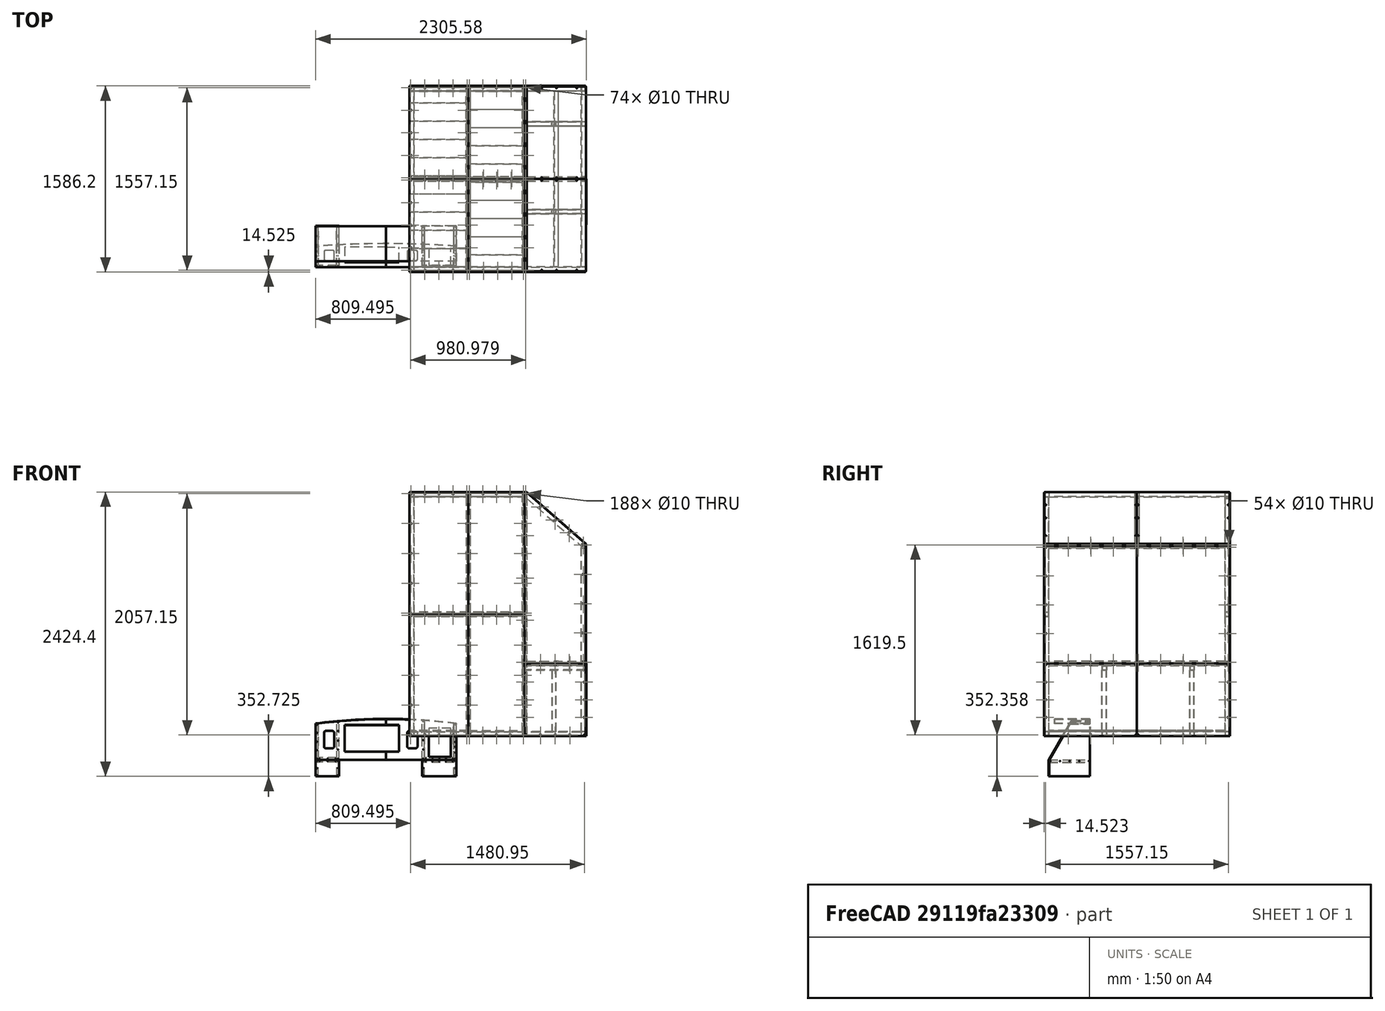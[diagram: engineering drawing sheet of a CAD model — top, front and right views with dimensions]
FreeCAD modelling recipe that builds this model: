
FCSTD DOCUMENT  (FreeCAD 1.0R39109 (Git))
Label: Estructura
License: All rights reserved
LicenseURL: https://en.wikipedia.org/wiki/All_rights_reserved
objects: Sketcher::SketchObject×137, PartDesign::SubShapeBinder×88, PartDesign::Pad×80, PartDesign::Body×74, PartDesign::Pocket×56, Part::FeaturePython×23, App::DocumentObjectGroup×18, PartDesign::Thickness×10, App::Part×4, PartDesign::Plane×3
note: 900 computed .brp shape members not serialized (recipe doc carries the construction recipe); baked Part::Feature solids carry a one-line shape summary decoded from their .brp

FEATURE [Sketcher::SketchObject] Sketch
  ArcFitTolerance = 1e-06
  AttachmentSupport = -> [XZ_Plane001]
  FullyConstrained = true
  MakeInternals = false
  MapMode = 5
  Placement = pos=(0,0,0) rot=(1,0,0;1.5708rad)
  sketch-geometry (4):
    g0: LineSegment StartX=0 StartY=0 StartZ=0 EndX=0 EndY=2000 EndZ=0
    g1: LineSegment StartX=0 StartY=0 StartZ=0 EndX=-38.1 EndY=0 EndZ=0
    g2: LineSegment StartX=-38.1 StartY=0 StartZ=0 EndX=-38.1 EndY=2000 EndZ=0
    g3: LineSegment StartX=0 StartY=2000 StartZ=0 EndX=-38.1 EndY=2000 EndZ=0
  constraints (11):
    c: Distance(g0) = 2000
    c: Coincident(g0,g-1)
    c: Vertical(g0)
    c: Distance(g1) = 38.1
    c: Coincident(g1,g0)
    c: PointOnObject(g1,g-1)
    c: Coincident(g2,g1)
    c: Vertical(g2)
    c: Coincident(g3,g0)
    c: Horizontal(g3)
    c: Coincident(g2,g3)
FEATURE [PartDesign::Pad] Pad
  Direction = (0,-1,2e-16)
  Length = 38.1
  Length2 = 10
  Placement = pos=(0,0,0) rot=(1,0,0;1.5708rad)
  Profile = -> Sketch
  ReferenceAxis = -> Sketch [N_Axis]
  Refine = true
  Suppressed = false
  Type = 0
FEATURE [Sketcher::SketchObject] Sketch001
  ArcFitTolerance = 1e-06
  AttachmentSupport = -> [Pad]
  ExternalGeometry = -> [Pad]
  FullyConstrained = true
  MakeInternals = false
  MapMode = 5
  Placement = pos=(0,8.8e-13,2000) rot=(0,0,1;3.14159rad)
  sketch-geometry (6):
    g0: LineSegment [constr] StartX=38.1 StartY=38.1 StartZ=0 EndX=0 EndY=0 EndZ=0
    g1: LineSegment StartX=2.7 StartY=2.7 StartZ=0 EndX=35.4 EndY=2.7 EndZ=0
    g2: LineSegment StartX=35.4 StartY=2.7 StartZ=0 EndX=35.4 EndY=35.4 EndZ=0
    g3: LineSegment StartX=35.4 StartY=35.4 StartZ=0 EndX=2.7 EndY=35.4 EndZ=0
    g4: LineSegment StartX=2.7 StartY=35.4 StartZ=0 EndX=2.7 EndY=2.7 EndZ=0
    g5: GeomPoint [constr] X=19.05 Y=19.05 Z=0
  constraints (14):
    c: Coincident(g0,g-3)
    c: Coincident(g0,g-1)
    c: Coincident(g1,g2)
    c: Coincident(g2,g3)
    c: Coincident(g3,g4)
    c: Coincident(g4,g1)
    c: Horizontal(g1)
    c: Horizontal(g3)
    c: Vertical(g2)
    c: Vertical(g4)
    c: Symmetric(g3,g1,g5)
    c: Symmetric(g0,g0,g5)
    c: PointOnObject(g2,g0)
    c: DistanceX(g2,g0) = 2.7
FEATURE [Sketcher::SketchObject] Sketch009
  ArcFitTolerance = 1e-06
  AttachmentSupport = -> [XY_Plane006]
  FullyConstrained = false
  MakeInternals = false
  MapMode = 5
  sketch-geometry (10):
    g0: LineSegment StartX=0 StartY=0 StartZ=0 EndX=-38.1 EndY=0 EndZ=0
    g1: LineSegment StartX=-38.1 StartY=0 StartZ=0 EndX=-38.1 EndY=-38.1 EndZ=0
    g2: LineSegment StartX=0 StartY=0 StartZ=0 EndX=-0.0294822 EndY=-38.1 EndZ=0
    g3: LineSegment StartX=-38.1 StartY=-38.1 StartZ=0 EndX=-0.0294822 EndY=-38.1 EndZ=0
    g4: LineSegment [constr] StartX=-38.1 StartY=0 StartZ=0 EndX=-0.0294822 EndY=-38.1 EndZ=0
    g5: LineSegment StartX=-2.72739 StartY=-35.4 StartZ=0 EndX=-2.72739 EndY=-2.7 EndZ=0
    g6: LineSegment StartX=-2.72739 StartY=-2.7 StartZ=0 EndX=-35.4021 EndY=-2.7 EndZ=0
    g7: LineSegment StartX=-35.4021 StartY=-2.7 StartZ=0 EndX=-35.4021 EndY=-35.4 EndZ=0
    g8: LineSegment StartX=-35.4021 StartY=-35.4 StartZ=0 EndX=-2.72739 EndY=-35.4 EndZ=0
    g9: GeomPoint [constr] X=-19.0647 Y=-19.05 Z=0
  constraints (24):
    c: Distance(g0) = 38.1
    c: Coincident(g0,g-1)
    c: PointOnObject(g0,g-1)
    c: Distance(g1) = 38.1
    c: Coincident(g1,g0)
    c: Vertical(g1)
    c: Coincident(g2,g0)
    c: Coincident(g3,g1)
    c: Horizontal(g3)
    c: Coincident(g2,g3)
    c: Coincident(g4,g0)
    c: Coincident(g4,g2)
    c: Coincident(g5,g6)
    c: Coincident(g6,g7)
    c: Coincident(g7,g8)
    c: Coincident(g8,g5)
    c: Vertical(g5)
    c: Vertical(g7)
    c: Horizontal(g6)
    c: Horizontal(g8)
    c: Symmetric(g7,g5,g9)
    c: Symmetric(g4,g4,g9)
    c: PointOnObject(g6,g4)
    c: DistanceY(g6,g0) = 2.7
FEATURE [PartDesign::Pad] Pad005
  Direction = (0,0,1)
  Length = 1600
  Length2 = 10
  Profile = -> Sketch009
  ReferenceAxis = -> Sketch009 [N_Axis]
  Refine = true
  Suppressed = false
  Type = 0
FEATURE [PartDesign::Body] Body005  label="Cuerpo008"
  AllowCompound = false
  Group = -> [Sketch009,Pad005]
  Origin = -> Origin006
  Placement = pos=(2000,0,38.1) rot=(0,0,1;0rad)
  Tip = -> Pad005
FEATURE [Part::FeaturePython] Clone016  label="Cuerpo009"  # Draft clone (typed FeaturePython)
  AttacherType = Attacher::AttachEngine3D
  Fuse = false
  Objects = -> [Body005]
  Placement = pos=(2000,1538.1,38.1) rot=(0,0,1;0rad)
  Scale = (1,1,1)
FEATURE [PartDesign::SubShapeBinder] Binder
  BindCopyOnChange = 0
  BindMode = 2
  ClaimChildren = false
  Context = -> Part [Body008.Binder.]
  Fuse = false
  MakeFace = true
  OffsetFill = false
  OffsetIntersection = false
  OffsetJoinType = 0
  OffsetOpenResult = false
  PartialLoad = false
  Refine = true
  Relative = true
  _Version = 2
FEATURE [Sketcher::SketchObject] Sketch014
  ArcFitTolerance = 1e-06
  AttachmentSupport = -> [Binder]
  ExternalGeometry = -> [Binder]
  FullyConstrained = true
  MakeInternals = false
  MapMode = 5
  Placement = pos=(0,-38.1,-8.4e-15) rot=(1,0,0;1.5708rad)
  sketch-geometry (4):
    g0: LineSegment StartX=1500 StartY=638.1 StartZ=0 EndX=1961.9 EndY=638.1 EndZ=0
    g1: LineSegment StartX=1961.9 StartY=638.1 StartZ=0 EndX=1961.9 EndY=600 EndZ=0
    g2: LineSegment StartX=1961.9 StartY=600 StartZ=0 EndX=1500 EndY=600 EndZ=0
    g3: LineSegment StartX=1500 StartY=600 StartZ=0 EndX=1500 EndY=638.1 EndZ=0
  constraints (8):
    c: Coincident(g0,g-3)
    c: Coincident(g0,g-4)
    c: Coincident(g1,g0)
    c: Coincident(g1,g-4)
    c: Coincident(g2,g1)
    c: Coincident(g2,g-3)
    c: Coincident(g3,g2)
    c: Coincident(g3,g0)
FEATURE [PartDesign::Pad] Pad008
  Direction = (0,-1,2e-16)
  Length = 38.1
  Length2 = 10
  Profile = -> Sketch014
  ReferenceAxis = -> Sketch014 [N_Axis]
  Refine = true
  Reversed = true
  Suppressed = false
  Type = 0
FEATURE [Sketcher::SketchObject] Sketch015
  ArcFitTolerance = 1e-06
  AttachmentSupport = -> [Pad008]
  ExternalGeometry = -> [Pad008]
  FullyConstrained = true
  MakeInternals = false
  MapMode = 5
  Placement = pos=(1500,0,0) rot=(0.57735,-0.57735,-0.57735;2.0944rad)
  sketch-geometry (6):
    g0: LineSegment [constr] StartX=-3.691e-13 StartY=638.1 StartZ=0 EndX=38.1 EndY=600 EndZ=0
    g1: LineSegment StartX=35.4 StartY=602.7 StartZ=0 EndX=35.4 EndY=635.4 EndZ=0
    g2: LineSegment StartX=35.4 StartY=635.4 StartZ=0 EndX=2.7 EndY=635.4 EndZ=0
    g3: LineSegment StartX=2.7 StartY=635.4 StartZ=0 EndX=2.7 EndY=602.7 EndZ=0
    g4: LineSegment StartX=2.7 StartY=602.7 StartZ=0 EndX=35.4 EndY=602.7 EndZ=0
    g5: GeomPoint [constr] X=19.05 Y=619.05 Z=0
  constraints (14):
    c: Coincident(g0,g-3)
    c: Coincident(g0,g-4)
    c: Coincident(g1,g2)
    c: Coincident(g2,g3)
    c: Coincident(g3,g4)
    c: Coincident(g4,g1)
    c: Vertical(g1)
    c: Vertical(g3)
    c: Horizontal(g2)
    c: Horizontal(g4)
    c: Symmetric(g3,g1,g5)
    c: Symmetric(g0,g0,g5)
    c: PointOnObject(g2,g0)
    c: DistanceY(g2,g0) = 2.7
FEATURE [PartDesign::Pocket] Pocket004
  BaseFeature = -> Pad008
  Direction = (1,0,0)
  Length = 5
  Length2 = 5
  Profile = -> Sketch015
  ReferenceAxis = -> Sketch015 [N_Axis]
  Refine = true
  Suppressed = false
  Type = 1
FEATURE [PartDesign::Body] Body008  label="Cuerpo"
  AllowCompound = false
  Group = -> [Binder,Sketch014,Pad008,Sketch015,Pocket004]
  Origin = -> Origin009
  Tip = -> Pocket004
FEATURE [Part::FeaturePython] Clone021  label="Cuerpo011"  # Draft clone (typed FeaturePython)
  AttacherType = Attacher::AttachEngine3D
  Fuse = false
  Objects = -> [Body008]
  Placement = pos=(-1.0872e-12,1538.1,-4.547e-13) rot=(0,0,1;0rad)
  Scale = (1,1,1)
FEATURE [App::DocumentObjectGroup] Group001  label="1.6m"
  Group = -> [Clone016,Body005]
FEATURE [Part::FeaturePython] Clone033  label="Cuerpo023"  # WARN: FeaturePython — macro-defined, semantics opaque (R4)
  AttacherType = Attacher::AttachEngine3D
  Fuse = false
  Placement = pos=(249.985,0,-1019.05) rot=(0,0,1;0rad)
  Scale = (1,1,1)
FEATURE [Part::FeaturePython] Clone034  label="Cuerpo024"  # WARN: FeaturePython — macro-defined, semantics opaque (R4)
  AttacherType = Attacher::AttachEngine3D
  Fuse = false
  Placement = pos=(249.985,1538.1,0) rot=(0,0,1;0rad)
  Scale = (1,1,1)
FEATURE [Part::FeaturePython] Clone035  label="Cuerpo025"  # WARN: FeaturePython — macro-defined, semantics opaque (R4)
  AttacherType = Attacher::AttachEngine3D
  Fuse = false
  Placement = pos=(249.985,1538.1,-1019.05) rot=(0,0,1;0rad)
  Scale = (1,1,1)
FEATURE [PartDesign::SubShapeBinder] Binder007
  BindCopyOnChange = 0
  BindMode = 2
  ClaimChildren = false
  Context = -> Body014 [Binder007.]
  Fuse = false
  MakeFace = true
  OffsetFill = false
  OffsetIntersection = false
  OffsetJoinType = 0
  OffsetOpenResult = false
  PartialLoad = false
  Refine = true
  Relative = true
  _Version = 2
FEATURE [Sketcher::SketchObject] Sketch028
  ArcFitTolerance = 1e-06
  AttachmentSupport = -> [Binder007]
  ExternalGeometry = -> [Binder007]
  FullyConstrained = true
  MakeInternals = false
  MapMode = 5
  Placement = pos=(2000,-4.4e-13,0) rot=(0.57735,0.57735,0.57735;2.0944rad)
  sketch-geometry (4):
    g0: LineSegment StartX=0 StartY=0 StartZ=0 EndX=1500 EndY=0 EndZ=0
    g1: LineSegment StartX=1500 StartY=0 StartZ=0 EndX=1500 EndY=38.1 EndZ=0
    g2: LineSegment StartX=1500 StartY=38.1 StartZ=0 EndX=0 EndY=38.1 EndZ=0
    g3: LineSegment StartX=0 StartY=38.1 StartZ=0 EndX=0 EndY=0 EndZ=0
  constraints (11):
    c: Coincident(g0,g1)
    c: Coincident(g1,g2)
    c: Coincident(g2,g3)
    c: Coincident(g3,g0)
    c: Horizontal(g0)
    c: Horizontal(g2)
    c: Vertical(g1)
    c: Vertical(g3)
    c: Coincident(g0,g-1)
    c: PointOnObject(g1,g-3)
    c: DistanceX(g0,g0) = 1500
FEATURE [PartDesign::Pad] Pad014
  Direction = (1,0,0)
  Length = 38.1
  Length2 = 10
  Profile = -> Sketch028
  ReferenceAxis = -> Sketch028 [N_Axis]
  Refine = true
  Reversed = true
  Suppressed = false
  Type = 0
FEATURE [Sketcher::SketchObject] Sketch029
  ArcFitTolerance = 1e-06
  AttachmentSupport = -> [Pad014]
  ExternalGeometry = -> [Pad014]
  FullyConstrained = true
  MakeInternals = false
  MapMode = 5
  Placement = pos=(0,1500,0) rot=(0,0.707107,0.707107;3.14159rad)
  sketch-geometry (6):
    g0: LineSegment [constr] StartX=-2000 StartY=0 StartZ=0 EndX=-1961.9 EndY=38.1 EndZ=0
    g1: LineSegment StartX=-1997.3 StartY=2.7 StartZ=0 EndX=-1964.6 EndY=2.7 EndZ=0
    g2: LineSegment StartX=-1964.6 StartY=2.7 StartZ=0 EndX=-1964.6 EndY=35.4 EndZ=0
    g3: LineSegment StartX=-1964.6 StartY=35.4 StartZ=0 EndX=-1997.3 EndY=35.4 EndZ=0
    g4: LineSegment StartX=-1997.3 StartY=35.4 StartZ=0 EndX=-1997.3 EndY=2.7 EndZ=0
    g5: GeomPoint [constr] X=-1980.95 Y=19.05 Z=0
  constraints (14):
    c: Coincident(g0,g-3)
    c: Coincident(g0,g-4)
    c: Coincident(g1,g2)
    c: Coincident(g2,g3)
    c: Coincident(g3,g4)
    c: Coincident(g4,g1)
    c: Horizontal(g1)
    c: Horizontal(g3)
    c: Vertical(g2)
    c: Vertical(g4)
    c: Symmetric(g3,g1,g5)
    c: Symmetric(g0,g0,g5)
    c: PointOnObject(g2,g0)
    c: DistanceY(g2,g0) = 2.7
FEATURE [PartDesign::Pocket] Pocket010
  BaseFeature = -> Pad014
  Direction = (0,-1,2e-16)
  Length = 5
  Length2 = 5
  Profile = -> Sketch029
  ReferenceAxis = -> Sketch029 [N_Axis]
  Refine = true
  Suppressed = false
  Type = 1
FEATURE [PartDesign::Body] Body014  label="Cuerpo026"
  AllowCompound = false
  Group = -> [Binder007,Sketch028,Pad014,Sketch029,Pocket010]
  Origin = -> Origin015
  Tip = -> Pocket010
FEATURE [Part::FeaturePython] Clone037  label="Cuerpo028"  # Draft clone (typed FeaturePython)
  AttacherType = Attacher::AttachEngine3D
  Fuse = false
  Objects = -> [Body014]
  Placement = pos=(-1.3642e-12,8.006e-13,600) rot=(0,0,1;0rad)
  Scale = (1,1,1)
FEATURE [Part::FeaturePython] Clone038  label="Cuerpo029"  # Draft clone (typed FeaturePython)
  AttacherType = Attacher::AttachEngine3D
  Fuse = false
  Objects = -> [Body014]
  Placement = pos=(-500,-7e-15,5.329e-13) rot=(0,0,1;0rad)
  Scale = (1,1,1)
FEATURE [Part::FeaturePython] Clone039  label="Cuerpo030"  # Draft clone (typed FeaturePython)
  AttacherType = Attacher::AttachEngine3D
  Fuse = false
  Objects = -> [Body014]
  Placement = pos=(-1461.93,4.4e-13,7.603e-13) rot=(0,0,1;0rad)
  Scale = (1,1,1)
FEATURE [Part::FeaturePython] Clone040  label="Cuerpo031"  # Draft clone (typed FeaturePython)
  AttacherType = Attacher::AttachEngine3D
  Fuse = false
  Objects = -> [Body014]
  Placement = pos=(-1461.93,4.4e-13,2038.1) rot=(0,0,1;0rad)
  Scale = (1,1,1)
FEATURE [Part::FeaturePython] Clone041  label="Cuerpo032"  # Draft clone (typed FeaturePython)
  AttacherType = Attacher::AttachEngine3D
  Fuse = false
  Objects = -> [Body014]
  Placement = pos=(-980.965,8.947e-13,2038.1) rot=(0,0,1;0rad)
  Scale = (1,1,1)
FEATURE [Part::FeaturePython] Clone042  label="Cuerpo033"  # Draft clone (typed FeaturePython)
  AttacherType = Attacher::AttachEngine3D
  Fuse = false
  Objects = -> [Body014]
  Placement = pos=(-500,8.947e-13,2038.1) rot=(0,0,1;0rad)
  Scale = (1,1,1)
FEATURE [Part::FeaturePython] Clone043  label="Cuerpo034"  # Draft clone (typed FeaturePython)
  AttacherType = Attacher::AttachEngine3D
  Fuse = false
  Objects = -> [Body014]
  Placement = pos=(-0.0294822,1.27e-12,1600) rot=(0,0,1;0rad)
  Scale = (1,1,1)
FEATURE [Part::FeaturePython] Clone044  label="Cuerpo035"  # Draft clone (typed FeaturePython)
  AttacherType = Attacher::AttachEngine3D
  Fuse = false
  Objects = -> [Body014]
  Placement = pos=(-230.95,5.732e-13,600) rot=(0,0,1;0rad)
  Scale = (1,1,1)
FEATURE [Part::FeaturePython] Clone045  label="Cuerpo036"  # Draft clone (typed FeaturePython)
  AttacherType = Attacher::AttachEngine3D
  Fuse = false
  Objects = -> [Body014]
  Placement = pos=(-499.971,5.732e-13,600) rot=(0,0,1;0rad)
  Scale = (1,1,1)
FEATURE [PartDesign::Pocket] Pocket
  BaseFeature = -> Pad
  Direction = (0,0,-1)
  Length = 5
  Length2 = 5
  Placement = pos=(0,0,0) rot=(1,0,0;1.5708rad)
  Profile = -> Sketch001
  ReferenceAxis = -> Sketch001 [N_Axis]
  Refine = true
  Suppressed = false
  Type = 1
FEATURE [PartDesign::Body] Body  label="SprVert"
  AllowCompound = false
  Group = -> [Sketch,Pad,Sketch001,Pocket]
  Origin = -> Origin001
  Placement = pos=(538.071,0,38.1) rot=(0,0,1;0rad)
  Tip = -> Pocket
FEATURE [Part::FeaturePython] Clone003  label="SprVert003"  # Draft clone (typed FeaturePython)
  AttacherType = Attacher::AttachEngine3D
  Fuse = false
  Objects = -> [Body]
  Placement = pos=(538.071,1538.1,38.1) rot=(0,0,1;0rad)
  Scale = (1,1,1)
FEATURE [Part::FeaturePython] Clone007  label="SprVert007"  # Draft clone (typed FeaturePython)
  AttacherType = Attacher::AttachEngine3D
  Fuse = false
  Objects = -> [Body]
  Placement = pos=(1500,1538.1,38.1) rot=(0,0,1;0rad)
  Scale = (1,1,1)
FEATURE [Part::FeaturePython] Clone008  label="SprVert008"  # Draft clone (typed FeaturePython)
  AttacherType = Attacher::AttachEngine3D
  Fuse = false
  Objects = -> [Body]
  Placement = pos=(1500,-7.4e-15,38.1) rot=(0,0,1;0rad)
  Scale = (1,1,1)
FEATURE [App::DocumentObjectGroup] Group  label="2m"
  Group = -> [Clone003,Clone007,Clone008,Body]
FEATURE [PartDesign::SubShapeBinder] Binder005
  BindCopyOnChange = 0
  BindMode = 2
  ClaimChildren = false
  Context = -> Part [Body012.Binder005.]
  Fuse = false
  MakeFace = true
  OffsetFill = false
  OffsetIntersection = false
  OffsetJoinType = 0
  OffsetOpenResult = false
  PartialLoad = false
  Refine = true
  Relative = true
  _Version = 2
FEATURE [Sketcher::SketchObject] Sketch024
  ArcFitTolerance = 1e-06
  AttachmentSupport = -> [Binder005]
  ExternalGeometry = -> [Binder005]
  FullyConstrained = true
  MakeInternals = false
  MapMode = 5
  Placement = pos=(0,-38.1,0) rot=(1,0,0;1.5708rad)
  sketch-geometry (6):
    g0: LineSegment [constr] StartX=38.1 StartY=1038.1 StartZ=0 EndX=1461.9 EndY=1038.1 EndZ=0
    g1: LineSegment StartX=1461.9 StartY=1019.05 StartZ=0 EndX=1461.9 EndY=1057.15 EndZ=0
    g2: LineSegment StartX=1461.9 StartY=1057.15 StartZ=0 EndX=38.1 EndY=1057.15 EndZ=0
    g3: LineSegment StartX=38.1 StartY=1057.15 StartZ=0 EndX=38.1 EndY=1019.05 EndZ=0
    g4: LineSegment StartX=38.1 StartY=1019.05 StartZ=0 EndX=1461.9 EndY=1019.05 EndZ=0
    g5: GeomPoint [constr] X=750 Y=1038.1 Z=0
  constraints (14):
    c: Symmetric(g-3,g-3,g0)
    c: Symmetric(g-4,g-4,g0)
    c: Coincident(g1,g2)
    c: Coincident(g2,g3)
    c: Coincident(g3,g4)
    c: Coincident(g4,g1)
    c: Vertical(g1)
    c: Vertical(g3)
    c: Horizontal(g2)
    c: Horizontal(g4)
    c: Symmetric(g3,g1,g5)
    c: Symmetric(g0,g0,g5)
    c: PointOnObject(g2,g-3)
    c: DistanceY(g1,g1) = 38.1
FEATURE [PartDesign::Pad] Pad012
  Direction = (0,-1,2e-16)
  Length = 38.1
  Length2 = 10
  Profile = -> Sketch024
  ReferenceAxis = -> Sketch024 [N_Axis]
  Refine = true
  Reversed = true
  Suppressed = false
  Type = 0
FEATURE [Sketcher::SketchObject] Sketch025
  ArcFitTolerance = 1e-06
  AttachmentSupport = -> [Pad012]
  ExternalGeometry = -> [Pad012]
  FullyConstrained = true
  MakeInternals = false
  MapMode = 5
  Placement = pos=(1461.9,0,0) rot=(0.57735,0.57735,0.57735;2.0944rad)
  sketch-geometry (6):
    g0: LineSegment [constr] StartX=-38.1 StartY=1057.15 StartZ=0 EndX=4.476e-13 EndY=1019.05 EndZ=0
    g1: LineSegment StartX=-2.7 StartY=1021.75 StartZ=0 EndX=-2.7 EndY=1054.45 EndZ=0
    g2: LineSegment StartX=-2.7 StartY=1054.45 StartZ=0 EndX=-35.4 EndY=1054.45 EndZ=0
    g3: LineSegment StartX=-35.4 StartY=1054.45 StartZ=0 EndX=-35.4 EndY=1021.75 EndZ=0
    g4: LineSegment StartX=-35.4 StartY=1021.75 StartZ=0 EndX=-2.7 EndY=1021.75 EndZ=0
    g5: GeomPoint [constr] X=-19.05 Y=1038.1 Z=0
  constraints (14):
    c: Coincident(g0,g-4)
    c: Coincident(g0,g-3)
    c: Coincident(g1,g2)
    c: Coincident(g2,g3)
    c: Coincident(g3,g4)
    c: Coincident(g4,g1)
    c: Vertical(g1)
    c: Vertical(g3)
    c: Horizontal(g2)
    c: Horizontal(g4)
    c: Symmetric(g3,g1,g5)
    c: Symmetric(g0,g0,g5)
    c: PointOnObject(g2,g0)
    c: DistanceY(g2,g0) = 2.7
FEATURE [PartDesign::Pocket] Pocket009
  BaseFeature = -> Pad012
  Direction = (-1,0,0)
  Length = 5
  Length2 = 5
  Profile = -> Sketch025
  ReferenceAxis = -> Sketch025 [N_Axis]
  Refine = true
  Suppressed = false
  Type = 1
FEATURE [PartDesign::SubShapeBinder] Binder008
  BindCopyOnChange = 0
  BindMode = 2
  ClaimChildren = false
  Context = -> Part [Body012.Binder008.]
  Fuse = false
  MakeFace = true
  OffsetFill = false
  OffsetIntersection = false
  OffsetJoinType = 0
  OffsetOpenResult = false
  PartialLoad = false
  Refine = true
  Relative = true
  _Version = 2
FEATURE [Sketcher::SketchObject] Sketch030
  ArcFitTolerance = 1e-06
  AttachmentSupport = -> [Pocket009]
  ExternalGeometry = -> [Pocket009,Binder008]
  FullyConstrained = false
  MakeInternals = false
  MapMode = 5
  Placement = pos=(0,-38.1,0) rot=(1,0,0;1.5708rad)
  sketch-geometry (6):
    g0: LineSegment StartX=538.071 StartY=1057.15 StartZ=0 EndX=38.1 EndY=1057.15 EndZ=0
    g1: LineSegment StartX=38.1 StartY=1057.15 StartZ=0 EndX=38.1 EndY=1019.05 EndZ=0
    g2: LineSegment StartX=38.1 StartY=1019.05 StartZ=0 EndX=538.071 EndY=1019.05 EndZ=0
    g3: LineSegment [constr] StartX=538.071 StartY=1210.51 StartZ=0 EndX=538.071 EndY=1019.05 EndZ=0
    g4: LineSegment [constr] StartX=538.071 StartY=1019.05 StartZ=0 EndX=415.801 EndY=1019.05 EndZ=0
    g5: LineSegment StartX=538.071 StartY=1057.15 StartZ=0 EndX=538.071 EndY=1019.05 EndZ=0
  constraints (16):
    c: Coincident(g0,g1)
    c: Coincident(g1,g2)
    c: Vertical(g1)
    c: Horizontal(g0)
    c: Horizontal(g2)
    c: PointOnObject(g3,g-5)
    c: PointOnObject(g0,g3)
    c: PointOnObject(g4,g-4)
    c: PointOnObject(g4,g-5)
    c: PointOnObject(g3,g4)
    c: Vertical(g3)
    c: Horizontal(g4)
    c: Coincident(g2,g3)
    c: Coincident(g5,g0)
    c: Coincident(g5,g4)
    c: Coincident(g0,g-3)
FEATURE [PartDesign::Pocket] Pocket011
  BaseFeature = -> Pocket009
  Direction = (0,1,-2e-16)
  Length = 5
  Length2 = 5
  Profile = -> Sketch030
  ReferenceAxis = -> Sketch030 [N_Axis]
  Refine = true
  Suppressed = false
  Type = 1
FEATURE [PartDesign::Body] Body012  label="Cuerpo018"
  AllowCompound = false
  Group = -> [Binder005,Sketch024,Pad012,Sketch025,Pocket009,Binder008,Sketch030,Pocket011]
  Origin = -> Origin013
  Placement = pos=(-6.821e-13,1538.1,4.69e-13) rot=(0,0,1;0rad)
  Tip = -> Pocket011
FEATURE [PartDesign::SubShapeBinder] Binder009
  BindCopyOnChange = 0
  BindMode = 2
  ClaimChildren = false
  Context = -> Part [Body016.Binder009.]
  Fuse = false
  MakeFace = true
  OffsetFill = false
  OffsetIntersection = false
  OffsetJoinType = 0
  OffsetOpenResult = false
  PartialLoad = false
  Refine = true
  Relative = true
  _Version = 2
FEATURE [Sketcher::SketchObject] Sketch033
  ArcFitTolerance = 1e-06
  AttachmentSupport = -> [Binder009]
  ExternalGeometry = -> [Binder009]
  FullyConstrained = true
  MakeInternals = false
  MapMode = 5
  Placement = pos=(0,0,0) rot=(1,0,0;1.5708rad)
  sketch-geometry (4):
    g0: LineSegment StartX=499.971 StartY=2076.2 StartZ=0 EndX=499.971 EndY=2038.1 EndZ=0
    g1: LineSegment StartX=499.971 StartY=2038.1 StartZ=0 EndX=1500 EndY=2038.1 EndZ=0
    g2: LineSegment StartX=1500 StartY=2038.1 StartZ=0 EndX=1500 EndY=2076.2 EndZ=0
    g3: LineSegment StartX=1500 StartY=2076.2 StartZ=0 EndX=499.971 EndY=2076.2 EndZ=0
  constraints (10):
    c: Coincident(g0,g1)
    c: Coincident(g1,g2)
    c: Coincident(g2,g3)
    c: Coincident(g3,g0)
    c: Vertical(g0)
    c: Vertical(g2)
    c: Horizontal(g1)
    c: Horizontal(g3)
    c: Coincident(g0,g-3)
    c: Coincident(g1,g-4)
FEATURE [PartDesign::Pad] Pad016
  Direction = (0,-1,2e-16)
  Length = 38.1
  Length2 = 10
  Profile = -> Sketch033
  ReferenceAxis = -> Sketch033 [N_Axis]
  Refine = true
  Suppressed = false
  Type = 0
FEATURE [Sketcher::SketchObject] Sketch034
  ArcFitTolerance = 1e-06
  AttachmentSupport = -> [Pad016]
  FullyConstrained = true
  MakeInternals = false
  MapMode = 5
  Placement = pos=(499.971,0,0) rot=(0.57735,-0.57735,-0.57735;2.0944rad)
FEATURE [PartDesign::Thickness] Thickness
  Base = -> Pad016 [Face1,Face3]
  BaseFeature = -> Pad016
  Intersection = false
  Join = 1
  Mode = 1
  Refine = true
  Reversed = true
  SupportTransform = false
  Suppressed = false
  Value = 2.7
FEATURE [PartDesign::Body] Body016  label="Cuerpo037"
  AllowCompound = false
  Group = -> [Binder009,Sketch033,Pad016,Sketch034,Thickness]
  Origin = -> Origin017
  Tip = -> Thickness
FEATURE [Part::FeaturePython] Clone047  label="Cuerpo039"  # Draft clone (typed FeaturePython)
  AttacherType = Attacher::AttachEngine3D
  Fuse = false
  Objects = -> [Body016]
  Placement = pos=(-1.1369e-12,1538.1,0) rot=(0,0,1;0rad)
  Scale = (1,1,1)
FEATURE [PartDesign::SubShapeBinder] Binder010
  BindCopyOnChange = 0
  BindMode = 2
  ClaimChildren = false
  Context = -> Part [Body017.Binder010.]
  Fuse = false
  MakeFace = true
  OffsetFill = false
  OffsetIntersection = false
  OffsetJoinType = 0
  OffsetOpenResult = false
  PartialLoad = false
  Refine = true
  Relative = true
  _Version = 2
FEATURE [Sketcher::SketchObject] Sketch035
  ArcFitTolerance = 1e-06
  AttachmentSupport = -> [Binder010]
  ExternalGeometry = -> [Binder010]
  FullyConstrained = true
  MakeInternals = false
  MapMode = 5
  Placement = pos=(0,-38.1,0) rot=(1,0,0;1.5708rad)
  sketch-geometry (6):
    g0: LineSegment [constr] StartX=38.1 StartY=1038.1 StartZ=0 EndX=1461.9 EndY=1038.1 EndZ=0
    g1: LineSegment StartX=1461.9 StartY=1019.05 StartZ=0 EndX=1461.9 EndY=1057.15 EndZ=0
    g2: LineSegment StartX=1461.9 StartY=1057.15 StartZ=0 EndX=38.1 EndY=1057.15 EndZ=0
    g3: LineSegment StartX=38.1 StartY=1057.15 StartZ=0 EndX=38.1 EndY=1019.05 EndZ=0
    g4: LineSegment StartX=38.1 StartY=1019.05 StartZ=0 EndX=1461.9 EndY=1019.05 EndZ=0
    g5: GeomPoint [constr] X=750 Y=1038.1 Z=0
  constraints (14):
    c: Symmetric(g-3,g-3,g0)
    c: Symmetric(g-4,g-4,g0)
    c: Coincident(g1,g2)
    c: Coincident(g2,g3)
    c: Coincident(g3,g4)
    c: Coincident(g4,g1)
    c: Vertical(g1)
    c: Vertical(g3)
    c: Horizontal(g2)
    c: Horizontal(g4)
    c: Symmetric(g3,g1,g5)
    c: Symmetric(g0,g0,g5)
    c: PointOnObject(g2,g-3)
    c: DistanceY(g1,g1) = 38.1
FEATURE [PartDesign::Pad] Pad017
  Direction = (0,-1,2e-16)
  Length = 38.1
  Length2 = 10
  Profile = -> Sketch035
  ReferenceAxis = -> Sketch035 [N_Axis]
  Refine = true
  Reversed = true
  Suppressed = false
  Type = 0
FEATURE [Sketcher::SketchObject] Sketch036
  ArcFitTolerance = 1e-06
  AttachmentSupport = -> [Pad017]
  ExternalGeometry = -> [Pad017]
  FullyConstrained = true
  MakeInternals = false
  MapMode = 5
  Placement = pos=(1461.9,0,0) rot=(0.57735,0.57735,0.57735;2.0944rad)
  sketch-geometry (6):
    g0: LineSegment [constr] StartX=-38.1 StartY=1057.15 StartZ=0 EndX=4.476e-13 EndY=1019.05 EndZ=0
    g1: LineSegment StartX=-2.7 StartY=1021.75 StartZ=0 EndX=-2.7 EndY=1054.45 EndZ=0
    g2: LineSegment StartX=-2.7 StartY=1054.45 StartZ=0 EndX=-35.4 EndY=1054.45 EndZ=0
    g3: LineSegment StartX=-35.4 StartY=1054.45 StartZ=0 EndX=-35.4 EndY=1021.75 EndZ=0
    g4: LineSegment StartX=-35.4 StartY=1021.75 StartZ=0 EndX=-2.7 EndY=1021.75 EndZ=0
    g5: GeomPoint [constr] X=-19.05 Y=1038.1 Z=0
  constraints (14):
    c: Coincident(g0,g-4)
    c: Coincident(g0,g-3)
    c: Coincident(g1,g2)
    c: Coincident(g2,g3)
    c: Coincident(g3,g4)
    c: Coincident(g4,g1)
    c: Vertical(g1)
    c: Vertical(g3)
    c: Horizontal(g2)
    c: Horizontal(g4)
    c: Symmetric(g3,g1,g5)
    c: Symmetric(g0,g0,g5)
    c: PointOnObject(g2,g0)
    c: DistanceY(g2,g0) = 2.7
FEATURE [PartDesign::Pocket] Pocket014
  BaseFeature = -> Pad017
  Direction = (-1,0,0)
  Length = 5
  Length2 = 5
  Profile = -> Sketch036
  ReferenceAxis = -> Sketch036 [N_Axis]
  Refine = true
  Suppressed = false
  Type = 1
FEATURE [PartDesign::SubShapeBinder] Binder011
  BindCopyOnChange = 0
  BindMode = 2
  ClaimChildren = false
  Context = -> Part [Body017.Binder011.]
  Fuse = false
  MakeFace = true
  OffsetFill = false
  OffsetIntersection = false
  OffsetJoinType = 0
  OffsetOpenResult = false
  PartialLoad = false
  Refine = true
  Relative = true
  _Version = 2
FEATURE [Sketcher::SketchObject] Sketch037
  ArcFitTolerance = 1e-06
  AttachmentSupport = -> [Pocket014]
  ExternalGeometry = -> [Pocket014,Binder011]
  FullyConstrained = false
  MakeInternals = false
  MapMode = 5
  Placement = pos=(0,-38.1,0) rot=(1,0,0;1.5708rad)
  sketch-geometry (6):
    g0: LineSegment StartX=538.071 StartY=1057.15 StartZ=0 EndX=38.1 EndY=1057.15 EndZ=0
    g1: LineSegment StartX=38.1 StartY=1057.15 StartZ=0 EndX=38.1 EndY=1019.05 EndZ=0
    g2: LineSegment StartX=38.1 StartY=1019.05 StartZ=0 EndX=538.071 EndY=1019.05 EndZ=0
    g3: LineSegment [constr] StartX=538.071 StartY=1210.51 StartZ=0 EndX=538.071 EndY=1019.05 EndZ=0
    g4: LineSegment [constr] StartX=538.071 StartY=1019.05 StartZ=0 EndX=415.801 EndY=1019.05 EndZ=0
    g5: LineSegment StartX=538.071 StartY=1057.15 StartZ=0 EndX=538.071 EndY=1019.05 EndZ=0
  constraints (16):
    c: Coincident(g0,g1)
    c: Coincident(g1,g2)
    c: Vertical(g1)
    c: Horizontal(g0)
    c: Horizontal(g2)
    c: PointOnObject(g3,g-5)
    c: PointOnObject(g0,g3)
    c: PointOnObject(g4,g-4)
    c: PointOnObject(g4,g-5)
    c: PointOnObject(g3,g4)
    c: Vertical(g3)
    c: Horizontal(g4)
    c: Coincident(g2,g3)
    c: Coincident(g5,g0)
    c: Coincident(g5,g4)
    c: Coincident(g0,g-3)
FEATURE [PartDesign::Pocket] Pocket015
  BaseFeature = -> Pocket014
  Direction = (0,1,-2e-16)
  Length = 5
  Length2 = 5
  Profile = -> Sketch037
  ReferenceAxis = -> Sketch037 [N_Axis]
  Refine = true
  Suppressed = false
  Type = 1
FEATURE [PartDesign::Body] Body017  label="Cuerpo040"
  AllowCompound = false
  Group = -> [Binder010,Sketch035,Pad017,Sketch036,Pocket014,Binder011,Sketch037,Pocket015]
  Origin = -> Origin018
  Placement = pos=(0,2.274e-13,1.43e-14) rot=(0,0,1;0rad)
  Tip = -> Pocket015
FEATURE [App::DocumentObjectGroup] Group005  label=".92"
  Group = -> [Body012,Body017]
FEATURE [Part::FeaturePython] Clone048  label="Cuerpo041"  # Draft clone (typed FeaturePython)
  AttacherType = Attacher::AttachEngine3D
  Fuse = false
  Objects = -> [Body014]
  Placement = pos=(-980.965,4.4e-13,7.958e-13) rot=(0,0,1;0rad)
  Scale = (1,1,1)
FEATURE [App::DocumentObjectGroup] Group009  label="1m"
  Group = -> [Clone047,Body016]
FEATURE [PartDesign::SubShapeBinder] Binder018
  BindCopyOnChange = 0
  BindMode = 2
  ClaimChildren = false
  Context = -> Part [Body021.Binder018.]
  Fuse = false
  MakeFace = true
  OffsetFill = false
  OffsetIntersection = false
  OffsetJoinType = 0
  OffsetOpenResult = false
  PartialLoad = false
  Refine = true
  Relative = true
  _Version = 2
FEATURE [Sketcher::SketchObject] Sketch041
  ArcFitTolerance = 1e-06
  AttachmentSupport = -> [Binder018]
  ExternalGeometry = -> [Binder018]
  FullyConstrained = false
  MakeInternals = false
  MapMode = 5
  Placement = pos=(0,-38.1,0) rot=(1,0,0;1.5708rad)
  sketch-geometry (8):
    g0: LineSegment [constr] StartX=1461.9 StartY=1057.15 StartZ=0 EndX=1461.9 EndY=2163.97 EndZ=0
    g1: LineSegment [constr] StartX=538.071 StartY=1057.15 StartZ=0 EndX=538.071 EndY=2246.61 EndZ=0
    g2: LineSegment [constr] StartX=999.985 StartY=1057.15 StartZ=0 EndX=999.985 EndY=2038.1 EndZ=0
    g3: LineSegment StartX=1019.04 StartY=1057.15 StartZ=0 EndX=1019.04 EndY=2038.1 EndZ=0
    g4: LineSegment StartX=1019.04 StartY=2038.1 StartZ=0 EndX=980.935 EndY=2038.1 EndZ=0
    g5: LineSegment StartX=980.935 StartY=2038.1 StartZ=0 EndX=980.935 EndY=1057.15 EndZ=0
    g6: LineSegment StartX=980.935 StartY=1057.15 StartZ=0 EndX=1019.04 EndY=1057.15 EndZ=0
    g7: GeomPoint [constr] X=999.985 Y=1547.62 Z=0
  constraints (16):
    c: Coincident(g0,g-4)
    c: Vertical(g0)
    c: Coincident(g1,g-3)
    c: Vertical(g1)
    c: Coincident(g3,g4)
    c: Coincident(g4,g5)
    c: Coincident(g5,g6)
    c: Coincident(g6,g3)
    c: Vertical(g3)
    c: Vertical(g5)
    c: Horizontal(g4)
    c: Horizontal(g6)
    c: Symmetric(g5,g3,g7)
    c: Symmetric(g2,g2,g7)
    c: PointOnObject(g4,g-5)
    c: DistanceX(g4,g3) = 38.1
FEATURE [PartDesign::Pad] Pad021
  Direction = (0,-1,2e-16)
  Length = 38.1
  Length2 = 10
  Profile = -> Sketch041
  ReferenceAxis = -> Sketch041 [N_Axis]
  Refine = true
  Reversed = true
  Suppressed = false
  Type = 0
FEATURE [PartDesign::Thickness] Thickness004
  Base = -> Pad021 [Face4,Face2]
  BaseFeature = -> Pad021
  Intersection = false
  Join = 0
  Mode = 0
  Refine = true
  Reversed = true
  SupportTransform = false
  Suppressed = false
  Value = 2.7
FEATURE [PartDesign::Body] Body021  label="Cuerpo045"
  AllowCompound = false
  Group = -> [Binder018,Sketch041,Pad021,Thickness004]
  Origin = -> Origin022
  Tip = -> Thickness004
FEATURE [App::DocumentObjectGroup] Group006  label=".98"
  Group = -> [Clone035,Clone033,Clone034,Body021]
FEATURE [PartDesign::SubShapeBinder] Binder020  label="Binder019"
  BindCopyOnChange = 0
  BindMode = 2
  ClaimChildren = false
  Context = -> Part [Body022.Binder019.]
  Fuse = false
  MakeFace = true
  OffsetFill = false
  OffsetIntersection = false
  OffsetJoinType = 0
  OffsetOpenResult = false
  PartialLoad = false
  Refine = true
  Relative = true
  _Version = 2
FEATURE [Sketcher::SketchObject] Sketch042
  ArcFitTolerance = 1e-06
  AttachmentSupport = -> [Binder020]
  ExternalGeometry = -> [Binder020]
  FullyConstrained = false
  MakeInternals = false
  MapMode = 5
  Placement = pos=(0,-38.1,0) rot=(1,0,0;1.5708rad)
  sketch-geometry (5):
    g0: LineSegment StartX=1500 StartY=2076.2 StartZ=0 EndX=1999.97 EndY=1638.1 EndZ=0
    g1: LineSegment StartX=1500 StartY=2025.54 StartZ=0 EndX=1961.9 EndY=1620.8 EndZ=0
    g2: LineSegment StartX=1500 StartY=2076.2 StartZ=0 EndX=1500 EndY=2025.54 EndZ=0
    g3: LineSegment StartX=1999.97 StartY=1638.1 StartZ=0 EndX=1961.9 EndY=1638.1 EndZ=0
    g4: LineSegment StartX=1961.9 StartY=1638.1 StartZ=0 EndX=1961.9 EndY=1620.8 EndZ=0
  constraints (11):
    c: Coincident(g0,g-4)
    c: Coincident(g0,g-3)
    c: Distance(g0) = 664.757
    c: Coincident(g2,g0)
    c: Vertical(g2)
    c: Coincident(g1,g2)
    c: Coincident(g3,g0)
    c: Coincident(g3,g-4)
    c: Coincident(g4,g3)
    c: Vertical(g4)
    c: Coincident(g1,g4)
FEATURE [PartDesign::Pad] Pad022
  Direction = (0,-1,2e-16)
  Length = 38.1
  Length2 = 10
  Profile = -> Sketch042
  ReferenceAxis = -> Sketch042 [N_Axis]
  Refine = true
  Reversed = true
  Suppressed = false
  Type = 0
FEATURE [PartDesign::Body] Body022  label="Cuerpo046"
  AllowCompound = false
  Group = -> [Binder020,Sketch042,Pad022]
  Origin = -> Origin023
  Tip = -> Pad022
FEATURE [Part::FeaturePython] Clone  label="Cuerpo047"  # Draft clone (typed FeaturePython)
  AttacherType = Attacher::AttachEngine3D
  Fuse = false
  Objects = -> [Body022]
  Placement = pos=(-0.0147411,769.05,0) rot=(0,0,1;0rad)
  Scale = (1,1,1)
FEATURE [Part::FeaturePython] Clone049  label="Cuerpo048"  # Draft clone (typed FeaturePython)
  AttacherType = Attacher::AttachEngine3D
  Fuse = false
  Objects = -> [Body022]
  Placement = pos=(-9.095e-13,1538.1,-4.547e-13) rot=(0,0,1;0rad)
  Scale = (1,1,1)
FEATURE [App::DocumentObjectGroup] Group004  label=".66m"
  Group = -> [Clone,Clone049,Body022]
FEATURE [Part::FeaturePython] Clone051  label="Cuerpo050"  # Draft clone (typed FeaturePython)
  AttacherType = Attacher::AttachEngine3D
  Fuse = false
  Objects = -> [Body014]
  Placement = pos=(1999.97,-2000,7.53e-13) rot=(0,0,1;1.5708rad)
  Scale = (1,1,1)
FEATURE [Part::FeaturePython] Clone052  label="Cuerpo051"  # Draft clone (typed FeaturePython)
  AttacherType = Attacher::AttachEngine3D
  Fuse = false
  Objects = -> [Body014]
  Placement = pos=(1999.97,-461.9,7.672e-13) rot=(0,0,1;1.5708rad)
  Scale = (1,1,1)
FEATURE [App::DocumentObjectGroup] Group008  label="1.5m"
  Group = -> [Clone038,Clone037,Clone040,Clone044,Clone042,Clone039,Clone045,Clone043,Clone041,Clone048,Clone052,Body014,Clone051]
FEATURE [PartDesign::SubShapeBinder] Binder021
  BindCopyOnChange = 0
  BindMode = 2
  ClaimChildren = false
  Context = -> Body023 [Binder021.]
  Fuse = false
  MakeFace = true
  OffsetFill = false
  OffsetIntersection = false
  OffsetJoinType = 0
  OffsetOpenResult = false
  PartialLoad = false
  Refine = true
  Relative = true
  _Version = 2
FEATURE [Sketcher::SketchObject] Sketch043
  ArcFitTolerance = 1e-06
  AttachmentSupport = -> [Binder021]
  ExternalGeometry = -> [Binder021]
  FullyConstrained = true
  MakeInternals = false
  MapMode = 5
  Placement = pos=(0,0,2076.2) rot=(0,0,1;0rad)
  sketch-geometry (6):
    g0: LineSegment [constr] StartX=538.071 StartY=750 StartZ=0 EndX=980.935 EndY=750 EndZ=0
    g1: LineSegment StartX=980.935 StartY=730.95 StartZ=0 EndX=980.935 EndY=769.05 EndZ=0
    g2: LineSegment StartX=980.935 StartY=769.05 StartZ=0 EndX=538.071 EndY=769.05 EndZ=0
    g3: LineSegment StartX=538.071 StartY=769.05 StartZ=0 EndX=538.071 EndY=730.95 EndZ=0
    g4: LineSegment StartX=538.071 StartY=730.95 StartZ=0 EndX=980.935 EndY=730.95 EndZ=0
    g5: GeomPoint [constr] X=759.503 Y=750 Z=0
  constraints (14):
    c: Symmetric(g-3,g-3,g0)
    c: Symmetric(g-4,g-4,g0)
    c: Coincident(g1,g2)
    c: Coincident(g2,g3)
    c: Coincident(g3,g4)
    c: Coincident(g4,g1)
    c: Vertical(g1)
    c: Vertical(g3)
    c: Horizontal(g2)
    c: Horizontal(g4)
    c: Symmetric(g3,g1,g5)
    c: Symmetric(g0,g0,g5)
    c: PointOnObject(g2,g-3)
    c: DistanceY(g1,g1) = 38.1
FEATURE [PartDesign::Pad] Pad023
  Direction = (0,0,1)
  Length = 38.1
  Length2 = 10
  Profile = -> Sketch043
  ReferenceAxis = -> Sketch043 [N_Axis]
  Refine = true
  Reversed = true
  Suppressed = false
  Type = 0
FEATURE [PartDesign::Thickness] Thickness005
  Base = -> Pad023 [Face3,Face1]
  BaseFeature = -> Pad023
  Intersection = false
  Join = 0
  Mode = 1
  Refine = true
  Reversed = true
  SupportTransform = false
  Suppressed = false
  Value = 2.7
FEATURE [PartDesign::Body] Body023  label="Cuerpo052"
  AllowCompound = false
  Group = -> [Binder021,Sketch043,Pad023,Thickness005]
  Origin = -> Origin024
  Tip = -> Thickness005
FEATURE [PartDesign::SubShapeBinder] Binder022
  BindCopyOnChange = 0
  BindMode = 2
  ClaimChildren = false
  Context = -> Body024 [Binder022.]
  Fuse = false
  MakeFace = true
  OffsetFill = false
  OffsetIntersection = false
  OffsetJoinType = 0
  OffsetOpenResult = false
  PartialLoad = false
  Refine = true
  Relative = true
  _Version = 2
FEATURE [Sketcher::SketchObject] Sketch044
  ArcFitTolerance = 1e-06
  AttachmentSupport = -> [Binder022]
  ExternalGeometry = -> [Binder022]
  FullyConstrained = true
  MakeInternals = false
  MapMode = 5
  Placement = pos=(0,0,2076.2) rot=(0,0,1;0rad)
  sketch-geometry (6):
    g0: LineSegment [constr] StartX=538.071 StartY=750 StartZ=0 EndX=980.935 EndY=750 EndZ=0
    g1: LineSegment StartX=980.935 StartY=730.95 StartZ=0 EndX=980.935 EndY=769.05 EndZ=0
    g2: LineSegment StartX=980.935 StartY=769.05 StartZ=0 EndX=538.071 EndY=769.05 EndZ=0
    g3: LineSegment StartX=538.071 StartY=769.05 StartZ=0 EndX=538.071 EndY=730.95 EndZ=0
    g4: LineSegment StartX=538.071 StartY=730.95 StartZ=0 EndX=980.935 EndY=730.95 EndZ=0
    g5: GeomPoint [constr] X=759.503 Y=750 Z=0
  constraints (14):
    c: Symmetric(g-3,g-3,g0)
    c: Symmetric(g-4,g-4,g0)
    c: Coincident(g1,g2)
    c: Coincident(g2,g3)
    c: Coincident(g3,g4)
    c: Coincident(g4,g1)
    c: Vertical(g1)
    c: Vertical(g3)
    c: Horizontal(g2)
    c: Horizontal(g4)
    c: Symmetric(g3,g1,g5)
    c: Symmetric(g0,g0,g5)
    c: PointOnObject(g2,g-3)
    c: DistanceY(g1,g1) = 38.1
FEATURE [PartDesign::Pad] Pad024
  Direction = (0,0,1)
  Length = 38.1
  Length2 = 10
  Profile = -> Sketch044
  ReferenceAxis = -> Sketch044 [N_Axis]
  Refine = true
  Reversed = true
  Suppressed = false
  Type = 0
FEATURE [PartDesign::Thickness] Thickness006
  Base = -> Pad024 [Face3,Face1]
  BaseFeature = -> Pad024
  Intersection = false
  Join = 0
  Mode = 1
  Refine = true
  Reversed = true
  SupportTransform = false
  Suppressed = false
  Value = 2.7
FEATURE [PartDesign::Body] Body024  label="Cuerpo053"
  AllowCompound = false
  Group = -> [Binder022,Sketch044,Pad024,Thickness006]
  Origin = -> Origin025
  Placement = pos=(480.965,0,-1.3642e-12) rot=(0,0,1;0rad)
  Tip = -> Thickness006
FEATURE [PartDesign::SubShapeBinder] Binder023
  BindCopyOnChange = 0
  BindMode = 2
  ClaimChildren = false
  Context = -> Part [Body025.Binder023.]
  Fuse = false
  MakeFace = true
  OffsetFill = false
  OffsetIntersection = false
  OffsetJoinType = 0
  OffsetOpenResult = false
  PartialLoad = false
  Refine = true
  Relative = true
  _Version = 2
FEATURE [Sketcher::SketchObject] Sketch045
  ArcFitTolerance = 1e-06
  AttachmentSupport = -> [Binder023]
  ExternalGeometry = -> [Binder023]
  FullyConstrained = true
  MakeInternals = false
  MapMode = 5
  Placement = pos=(0,0,38.1) rot=(0,0,1;0rad)
  sketch-geometry (6):
    g0: LineSegment [constr] StartX=1500.03 StartY=1519.05 StartZ=0 EndX=1961.93 EndY=1519.05 EndZ=0
    g1: LineSegment StartX=1961.93 StartY=1500 StartZ=0 EndX=1961.93 EndY=1538.1 EndZ=0
    g2: LineSegment StartX=1961.93 StartY=1538.1 StartZ=0 EndX=1500.03 EndY=1538.1 EndZ=0
    g3: LineSegment StartX=1500.03 StartY=1538.1 StartZ=0 EndX=1500.03 EndY=1500 EndZ=0
    g4: LineSegment StartX=1500.03 StartY=1500 StartZ=0 EndX=1961.93 EndY=1500 EndZ=0
    g5: GeomPoint [constr] X=1730.98 Y=1519.05 Z=0
  constraints (14):
    c: Symmetric(g-3,g-3,g0)
    c: Symmetric(g-4,g-4,g0)
    c: Coincident(g1,g2)
    c: Coincident(g2,g3)
    c: Coincident(g3,g4)
    c: Coincident(g4,g1)
    c: Vertical(g1)
    c: Vertical(g3)
    c: Horizontal(g2)
    c: Horizontal(g4)
    c: Symmetric(g3,g1,g5)
    c: Symmetric(g0,g0,g5)
    c: PointOnObject(g2,g-3)
    c: DistanceY(g3,g3) = 38.1
FEATURE [PartDesign::Pad] Pad025
  Direction = (0,0,1)
  Length = 38.1
  Length2 = 10
  Profile = -> Sketch045
  ReferenceAxis = -> Sketch045 [N_Axis]
  Refine = true
  Reversed = true
  Suppressed = false
  Type = 0
FEATURE [PartDesign::Thickness] Thickness007
  Base = -> Pad025 [Face1,Face3]
  BaseFeature = -> Pad025
  Intersection = false
  Join = 0
  Mode = 1
  Refine = true
  Reversed = true
  SupportTransform = false
  Suppressed = false
  Value = 2.7
FEATURE [PartDesign::Body] Body025  label="Cuerpo054"
  AllowCompound = false
  Group = -> [Binder023,Sketch045,Pad025,Thickness007]
  Origin = -> Origin026
  Placement = pos=(-0.0294822,-1048.1,5.755e-13) rot=(0,0,1;0rad)
  Tip = -> Thickness007
FEATURE [PartDesign::SubShapeBinder] Binder024
  BindCopyOnChange = 0
  BindMode = 2
  ClaimChildren = false
  Context = -> Part [Body026.Binder024.]
  Fuse = false
  MakeFace = true
  OffsetFill = false
  OffsetIntersection = false
  OffsetJoinType = 0
  OffsetOpenResult = false
  PartialLoad = false
  Refine = true
  Relative = true
  _Version = 2
FEATURE [Sketcher::SketchObject] Sketch046
  ArcFitTolerance = 1e-06
  AttachmentSupport = -> [Binder024]
  ExternalGeometry = -> [Binder024]
  FullyConstrained = true
  MakeInternals = false
  MapMode = 5
  Placement = pos=(0,0,600) rot=(1,0,0;3.14159rad)
  sketch-geometry (6):
    g0: LineSegment [constr] StartX=1461.93 StartY=-750 StartZ=0 EndX=2000 EndY=-750 EndZ=0
    g1: LineSegment StartX=1461.93 StartY=-769.05 StartZ=0 EndX=2000 EndY=-769.05 EndZ=0
    g2: LineSegment StartX=2000 StartY=-769.05 StartZ=0 EndX=2000 EndY=-730.95 EndZ=0
    g3: LineSegment StartX=2000 StartY=-730.95 StartZ=0 EndX=1461.93 EndY=-730.95 EndZ=0
    g4: LineSegment StartX=1461.93 StartY=-730.95 StartZ=0 EndX=1461.93 EndY=-769.05 EndZ=0
    g5: GeomPoint [constr] X=1730.96 Y=-750 Z=0
  constraints (14):
    c: Symmetric(g-3,g-3,g0)
    c: Symmetric(g-4,g-4,g0)
    c: Coincident(g1,g2)
    c: Coincident(g2,g3)
    c: Coincident(g3,g4)
    c: Coincident(g4,g1)
    c: Horizontal(g1)
    c: Horizontal(g3)
    c: Vertical(g2)
    c: Vertical(g4)
    c: Symmetric(g3,g1,g5)
    c: Symmetric(g0,g0,g5)
    c: PointOnObject(g2,g-4)
    c: DistanceY(g4,g4) = 38.1
FEATURE [PartDesign::Pad] Pad026
  Direction = (0,0,-1)
  Length = 38.1
  Length2 = 10
  Profile = -> Sketch046
  ReferenceAxis = -> Sketch046 [N_Axis]
  Refine = true
  Suppressed = false
  Type = 0
FEATURE [PartDesign::Thickness] Thickness008
  Base = -> Pad026 [Face4,Face2]
  BaseFeature = -> Pad026
  Intersection = false
  Join = 0
  Mode = 1
  Refine = true
  Reversed = true
  SupportTransform = false
  Suppressed = false
  Value = 2.7
FEATURE [PartDesign::Body] Body026  label="Cuerpo055"
  AllowCompound = false
  Group = -> [Binder024,Sketch046,Pad026,Thickness008]
  Origin = -> Origin027
  Placement = pos=(1.5916e-12,-279.05,0) rot=(0,0,1;0rad)
  Tip = -> Thickness008
FEATURE [PartDesign::SubShapeBinder] Binder025
  BindCopyOnChange = 0
  BindMode = 2
  ClaimChildren = false
  Context = -> Part [Body027.Binder025.]
  Fuse = false
  MakeFace = true
  OffsetFill = false
  OffsetIntersection = false
  OffsetJoinType = 0
  OffsetOpenResult = false
  PartialLoad = false
  Refine = true
  Relative = true
  _Version = 2
FEATURE [Sketcher::SketchObject] Sketch047
  ArcFitTolerance = 1e-06
  AttachmentSupport = -> [Binder025]
  ExternalGeometry = -> [Binder025]
  FullyConstrained = false
  MakeInternals = false
  MapMode = 5
  Placement = pos=(0,1500,0) rot=(1,0,0;1.5708rad)
  sketch-geometry (6):
    g0: LineSegment [constr] StartX=1730.96 StartY=561.9 StartZ=0 EndX=1730.95 EndY=38.1 EndZ=0
    g1: LineSegment StartX=1750.01 StartY=38.1 StartZ=0 EndX=1750.01 EndY=561.9 EndZ=0
    g2: LineSegment StartX=1750.01 StartY=561.9 StartZ=0 EndX=1711.91 EndY=561.9 EndZ=0
    g3: LineSegment StartX=1711.91 StartY=561.9 StartZ=0 EndX=1711.91 EndY=38.1 EndZ=0
    g4: LineSegment StartX=1711.91 StartY=38.1 StartZ=0 EndX=1750.01 EndY=38.1 EndZ=0
    g5: GeomPoint [constr] X=1730.96 Y=300 Z=0
  constraints (12):
    c: Coincident(g1,g2)
    c: Coincident(g2,g3)
    c: Coincident(g3,g4)
    c: Coincident(g4,g1)
    c: Vertical(g1)
    c: Vertical(g3)
    c: Horizontal(g2)
    c: Horizontal(g4)
    c: Symmetric(g3,g1,g5)
    c: Symmetric(g0,g0,g5)
    c: PointOnObject(g2,g-4)
    c: DistanceX(g2,g2) = 38.1
FEATURE [PartDesign::Pad] Pad027
  Direction = (0,-1,2e-16)
  Length = 38.1
  Length2 = 10
  Profile = -> Sketch047
  ReferenceAxis = -> Sketch047 [N_Axis]
  Refine = true
  Reversed = true
  Suppressed = false
  Type = 0
FEATURE [PartDesign::Thickness] Thickness009
  Base = -> Pad027 [Face2,Face4]
  BaseFeature = -> Pad027
  Intersection = false
  Join = 0
  Mode = 1
  Refine = true
  Reversed = true
  SupportTransform = false
  Suppressed = false
  Value = 2.7
FEATURE [PartDesign::Body] Body027  label="Cuerpo056"
  AllowCompound = false
  Group = -> [Binder025,Sketch047,Pad027,Thickness009]
  Origin = -> Origin028
  Placement = pos=(0.00737053,-1048.1,0) rot=(0,0,1;0rad)
  Tip = -> Thickness009
FEATURE [PartDesign::SubShapeBinder] Binder026
  BindCopyOnChange = 0
  BindMode = 2
  ClaimChildren = false
  Context = -> Part [Body028.Binder026.]
  Fuse = false
  MakeFace = true
  OffsetFill = false
  OffsetIntersection = false
  OffsetJoinType = 0
  OffsetOpenResult = false
  PartialLoad = false
  Refine = true
  Relative = true
  _Version = 2
FEATURE [Sketcher::SketchObject] Sketch048
  ArcFitTolerance = 1e-06
  AttachmentSupport = -> [Binder026]
  ExternalGeometry = -> [Binder026]
  FullyConstrained = false
  MakeInternals = false
  MapMode = 5
  Placement = pos=(0,1500,0) rot=(1,0,0;1.5708rad)
  sketch-geometry (6):
    g0: LineSegment [constr] StartX=1730.96 StartY=561.9 StartZ=0 EndX=1730.95 EndY=38.1 EndZ=0
    g1: LineSegment StartX=1750.01 StartY=38.1 StartZ=0 EndX=1750.01 EndY=561.9 EndZ=0
    g2: LineSegment StartX=1750.01 StartY=561.9 StartZ=0 EndX=1711.91 EndY=561.9 EndZ=0
    g3: LineSegment StartX=1711.91 StartY=561.9 StartZ=0 EndX=1711.91 EndY=38.1 EndZ=0
    g4: LineSegment StartX=1711.91 StartY=38.1 StartZ=0 EndX=1750.01 EndY=38.1 EndZ=0
    g5: GeomPoint [constr] X=1730.96 Y=300 Z=0
  constraints (12):
    c: Coincident(g1,g2)
    c: Coincident(g2,g3)
    c: Coincident(g3,g4)
    c: Coincident(g4,g1)
    c: Vertical(g1)
    c: Vertical(g3)
    c: Horizontal(g2)
    c: Horizontal(g4)
    c: Symmetric(g3,g1,g5)
    c: Symmetric(g0,g0,g5)
    c: PointOnObject(g2,g-4)
    c: DistanceX(g2,g2) = 38.1
FEATURE [PartDesign::Pad] Pad028
  Direction = (0,-1,2e-16)
  Length = 38.1
  Length2 = 10
  Profile = -> Sketch048
  ReferenceAxis = -> Sketch048 [N_Axis]
  Refine = true
  Reversed = true
  Suppressed = false
  Type = 0
FEATURE [PartDesign::Thickness] Thickness010
  Base = -> Pad028 [Face2,Face4]
  BaseFeature = -> Pad028
  Intersection = false
  Join = 0
  Mode = 1
  Refine = true
  Reversed = true
  SupportTransform = false
  Suppressed = false
  Value = 2.7
FEATURE [PartDesign::Body] Body028  label="Cuerpo057"
  AllowCompound = false
  Group = -> [Binder026,Sketch048,Pad028,Thickness010]
  Origin = -> Origin029
  Placement = pos=(0.00737053,-300,0) rot=(0,0,1;0rad)
  Tip = -> Thickness010
FEATURE [PartDesign::SubShapeBinder] Binder027
  BindCopyOnChange = 0
  BindMode = 2
  ClaimChildren = false
  Context = -> Part [Body029.Binder027.]
  Fuse = false
  MakeFace = true
  OffsetFill = false
  OffsetIntersection = false
  OffsetJoinType = 0
  OffsetOpenResult = false
  PartialLoad = false
  Refine = true
  Relative = true
  _Version = 2
FEATURE [Sketcher::SketchObject] Sketch049
  ArcFitTolerance = 1e-06
  AttachmentSupport = -> [Binder027]
  ExternalGeometry = -> [Binder027]
  FullyConstrained = true
  MakeInternals = false
  MapMode = 5
  Placement = pos=(0,0,38.1) rot=(0,0,1;0rad)
  sketch-geometry (6):
    g0: LineSegment [constr] StartX=1500.03 StartY=1519.05 StartZ=0 EndX=1961.93 EndY=1519.05 EndZ=0
    g1: LineSegment StartX=1961.93 StartY=1500 StartZ=0 EndX=1961.93 EndY=1538.1 EndZ=0
    g2: LineSegment StartX=1961.93 StartY=1538.1 StartZ=0 EndX=1500.03 EndY=1538.1 EndZ=0
    g3: LineSegment StartX=1500.03 StartY=1538.1 StartZ=0 EndX=1500.03 EndY=1500 EndZ=0
    g4: LineSegment StartX=1500.03 StartY=1500 StartZ=0 EndX=1961.93 EndY=1500 EndZ=0
    g5: GeomPoint [constr] X=1730.98 Y=1519.05 Z=0
  constraints (14):
    c: Symmetric(g-3,g-3,g0)
    c: Symmetric(g-4,g-4,g0)
    c: Coincident(g1,g2)
    c: Coincident(g2,g3)
    c: Coincident(g3,g4)
    c: Coincident(g4,g1)
    c: Vertical(g1)
    c: Vertical(g3)
    c: Horizontal(g2)
    c: Horizontal(g4)
    c: Symmetric(g3,g1,g5)
    c: Symmetric(g0,g0,g5)
    c: PointOnObject(g2,g-3)
    c: DistanceY(g3,g3) = 38.1
FEATURE [PartDesign::Pad] Pad029
  Direction = (0,0,1)
  Length = 38.1
  Length2 = 10
  Profile = -> Sketch049
  ReferenceAxis = -> Sketch049 [N_Axis]
  Refine = true
  Reversed = true
  Suppressed = false
  Type = 0
FEATURE [PartDesign::Thickness] Thickness011
  Base = -> Pad029 [Face1,Face3]
  BaseFeature = -> Pad029
  Intersection = false
  Join = 0
  Mode = 1
  Refine = true
  Reversed = true
  SupportTransform = false
  Suppressed = false
  Value = 2.7
FEATURE [PartDesign::Body] Body029  label="Cuerpo058"
  AllowCompound = false
  Group = -> [Binder027,Sketch049,Pad029,Thickness011]
  Origin = -> Origin030
  Placement = pos=(-0.0294822,-300,5.755e-13) rot=(0,0,1;0rad)
  Tip = -> Thickness011
FEATURE [PartDesign::SubShapeBinder] Binder028
  BindCopyOnChange = 0
  BindMode = 2
  ClaimChildren = false
  Context = -> Part [Body030.Binder028.]
  Fuse = false
  MakeFace = true
  OffsetFill = false
  OffsetIntersection = false
  OffsetJoinType = 0
  OffsetOpenResult = false
  PartialLoad = false
  Refine = true
  Relative = true
  _Version = 2
FEATURE [Sketcher::SketchObject] Sketch050
  ArcFitTolerance = 1e-06
  AttachmentSupport = -> [Binder028]
  ExternalGeometry = -> [Binder028]
  FullyConstrained = true
  MakeInternals = false
  MapMode = 5
  Placement = pos=(0,0,600) rot=(1,0,0;3.14159rad)
  sketch-geometry (6):
    g0: LineSegment [constr] StartX=1461.93 StartY=-750 StartZ=0 EndX=2000 EndY=-750 EndZ=0
    g1: LineSegment StartX=1461.93 StartY=-769.05 StartZ=0 EndX=2000 EndY=-769.05 EndZ=0
    g2: LineSegment StartX=2000 StartY=-769.05 StartZ=0 EndX=2000 EndY=-730.95 EndZ=0
    g3: LineSegment StartX=2000 StartY=-730.95 StartZ=0 EndX=1461.93 EndY=-730.95 EndZ=0
    g4: LineSegment StartX=1461.93 StartY=-730.95 StartZ=0 EndX=1461.93 EndY=-769.05 EndZ=0
    g5: GeomPoint [constr] X=1730.96 Y=-750 Z=0
  constraints (14):
    c: Symmetric(g-3,g-3,g0)
    c: Symmetric(g-4,g-4,g0)
    c: Coincident(g1,g2)
    c: Coincident(g2,g3)
    c: Coincident(g3,g4)
    c: Coincident(g4,g1)
    c: Horizontal(g1)
    c: Horizontal(g3)
    c: Vertical(g2)
    c: Vertical(g4)
    c: Symmetric(g3,g1,g5)
    c: Symmetric(g0,g0,g5)
    c: PointOnObject(g2,g-4)
    c: DistanceY(g4,g4) = 38.1
FEATURE [PartDesign::Pad] Pad030
  Direction = (0,0,-1)
  Length = 38.1
  Length2 = 10
  Profile = -> Sketch050
  ReferenceAxis = -> Sketch050 [N_Axis]
  Refine = true
  Suppressed = false
  Type = 0
FEATURE [PartDesign::Thickness] Thickness012
  Base = -> Pad030 [Face4,Face2]
  BaseFeature = -> Pad030
  Intersection = false
  Join = 0
  Mode = 1
  Refine = true
  Reversed = true
  SupportTransform = false
  Suppressed = false
  Value = 2.7
FEATURE [PartDesign::Body] Body030  label="Cuerpo059"
  AllowCompound = false
  Group = -> [Binder028,Sketch050,Pad030,Thickness012]
  Origin = -> Origin031
  Placement = pos=(1.5916e-12,469.05,0) rot=(0,0,1;0rad)
  Tip = -> Thickness012
FEATURE [App::DocumentObjectGroup] Group002  label=".46 m"
  Group = -> [Clone021,Body008,Body025,Body026,Body029,Body030]
FEATURE [App::DocumentObjectGroup] Group010  label=".44"
  Group = -> [Body023,Body024]
FEATURE [App::DocumentObjectGroup] Group011  label=".52"
  Group = -> [Body027,Body028]
FEATURE [App::DocumentObjectGroup] Group007  label="Main"
  Group = -> [Group,Group001,Group008,Group009,Group006,Group005,Group004,Group011,Group002,Group010]
FEATURE [App::Part] Part
  Group = -> [Group001,Group,Group005,Group008,Group004,Group006,Group009,Group007,Clone016,Clone003,Clone035,Clone038,Clone007,Clone008,Clone033,Clone034,Clone037,Clone040,Clone044,Clone042,Clone,Clone047,Clone039,Clone045,Clone043,Clone041,Clone048,Clone051,Clone052,Clone049,Body,Body014,Body005,Body012,Body008,Clone021,Group002,Body016,Body017,Body022,Body021,Group010,Body023,Body024,Body025,Body026,+5 more]
  Origin = -> Origin
FEATURE [PartDesign::SubShapeBinder] Binder029
  BindCopyOnChange = 0
  BindMode = 2
  ClaimChildren = false
  Context = -> Part001 [Body003.Binder029.]
  Fuse = false
  MakeFace = true
  OffsetFill = false
  OffsetIntersection = false
  OffsetJoinType = 0
  OffsetOpenResult = false
  PartialLoad = false
  Refine = true
  Relative = true
  _Version = 2
FEATURE [PartDesign::SubShapeBinder] Binder002
  BindCopyOnChange = 0
  BindMode = 2
  ClaimChildren = false
  Context = -> Part001 [Body032.Binder002.]
  Fuse = false
  MakeFace = true
  OffsetFill = false
  OffsetIntersection = false
  OffsetJoinType = 0
  OffsetOpenResult = false
  PartialLoad = false
  Refine = true
  Relative = true
  _Version = 2
FEATURE [PartDesign::SubShapeBinder] Binder003
  BindCopyOnChange = 0
  BindMode = 2
  ClaimChildren = false
  Context = -> Part001 [Body006.Binder003.]
  Fuse = false
  MakeFace = true
  OffsetFill = false
  OffsetIntersection = false
  OffsetJoinType = 0
  OffsetOpenResult = false
  PartialLoad = false
  Refine = true
  Relative = true
  _Version = 2
FEATURE [PartDesign::SubShapeBinder] Binder004
  BindCopyOnChange = 0
  BindMode = 2
  ClaimChildren = false
  Context = -> Part001 [Body004.Binder004.]
  Fuse = false
  MakeFace = true
  OffsetFill = false
  OffsetIntersection = false
  OffsetJoinType = 0
  OffsetOpenResult = false
  PartialLoad = false
  Refine = true
  Relative = true
  _Version = 2
FEATURE [PartDesign::SubShapeBinder] Binder030
  BindCopyOnChange = 0
  BindMode = 2
  ClaimChildren = false
  Context = -> Part001 [Body003.Binder030.]
  Fuse = false
  MakeFace = true
  OffsetFill = false
  OffsetIntersection = false
  OffsetJoinType = 0
  OffsetOpenResult = false
  PartialLoad = false
  Refine = true
  Relative = true
  _Version = 2
FEATURE [PartDesign::SubShapeBinder] Binder006
  BindCopyOnChange = 0
  BindMode = 2
  ClaimChildren = false
  Context = -> Part001 [Body007.Binder006.]
  Fuse = false
  MakeFace = true
  OffsetFill = false
  OffsetIntersection = false
  OffsetJoinType = 0
  OffsetOpenResult = false
  PartialLoad = false
  Refine = true
  Relative = true
  _Version = 2
FEATURE [PartDesign::SubShapeBinder] Binder031
  BindCopyOnChange = 0
  BindMode = 2
  ClaimChildren = false
  Context = -> Part001 [Body003.Binder031.]
  Fuse = false
  MakeFace = true
  OffsetFill = false
  OffsetIntersection = false
  OffsetJoinType = 0
  OffsetOpenResult = false
  PartialLoad = false
  Refine = true
  Relative = true
  _Version = 2
FEATURE [PartDesign::SubShapeBinder] Binder032
  BindCopyOnChange = 0
  BindMode = 2
  ClaimChildren = false
  Context = -> Part001 [Body033.Binder009.]
  Fuse = false
  MakeFace = true
  OffsetFill = false
  OffsetIntersection = false
  OffsetJoinType = 0
  OffsetOpenResult = false
  PartialLoad = false
  Refine = true
  Relative = true
  _Version = 2
FEATURE [PartDesign::SubShapeBinder] Binder012
  BindCopyOnChange = 0
  BindMode = 2
  ClaimChildren = false
  Context = -> Part001 [Body009.Binder012.]
  Fuse = false
  MakeFace = true
  OffsetFill = false
  OffsetIntersection = false
  OffsetJoinType = 0
  OffsetOpenResult = false
  PartialLoad = false
  Refine = true
  Relative = true
  _Version = 2
FEATURE [PartDesign::SubShapeBinder] Binder013
  BindCopyOnChange = 0
  BindMode = 2
  ClaimChildren = false
  Context = -> Part001 [Body010.Binder013.]
  Fuse = false
  MakeFace = true
  OffsetFill = false
  OffsetIntersection = false
  OffsetJoinType = 0
  OffsetOpenResult = false
  PartialLoad = false
  Refine = true
  Relative = true
  _Version = 2
FEATURE [PartDesign::SubShapeBinder] Binder014
  BindCopyOnChange = 0
  BindMode = 2
  ClaimChildren = false
  Context = -> Part001 [Body002.Binder014.]
  Fuse = false
  MakeFace = true
  OffsetFill = false
  OffsetIntersection = false
  OffsetJoinType = 0
  OffsetOpenResult = false
  PartialLoad = false
  Refine = true
  Relative = true
  _Version = 2
FEATURE [PartDesign::SubShapeBinder] Binder015
  BindCopyOnChange = 0
  BindMode = 2
  ClaimChildren = false
  Context = -> Part001 [Body011.Binder015.]
  Fuse = false
  MakeFace = true
  OffsetFill = false
  OffsetIntersection = false
  OffsetJoinType = 0
  OffsetOpenResult = false
  PartialLoad = false
  Refine = true
  Relative = true
  _Version = 2
FEATURE [PartDesign::SubShapeBinder] Binder016
  BindCopyOnChange = 0
  BindMode = 0
  ClaimChildren = false
  Context = -> Part001 [Body002.Binder016.]
  Fuse = false
  MakeFace = true
  OffsetFill = false
  OffsetIntersection = false
  OffsetJoinType = 0
  OffsetOpenResult = false
  PartialLoad = false
  Refine = true
  Relative = true
  Support = -> [Body011[Pocket044.Face21,Pocket044.Face5]]
  _Version = 2
FEATURE [PartDesign::SubShapeBinder] Binder017
  BindCopyOnChange = 0
  BindMode = 0
  ClaimChildren = false
  Context = -> Part001 [Body031.Binder017.]
  Fuse = false
  MakeFace = true
  OffsetFill = false
  OffsetIntersection = false
  OffsetJoinType = 0
  OffsetOpenResult = false
  PartialLoad = false
  Refine = true
  Relative = true
  Support = -> [Body011[Pocket044.Face5]]
  _Version = 2
FEATURE [PartDesign::SubShapeBinder] Binder033
  BindCopyOnChange = 0
  BindMode = 0
  ClaimChildren = false
  Context = -> Part001 [Body010.Binder033.]
  Fuse = false
  MakeFace = true
  OffsetFill = false
  OffsetIntersection = false
  OffsetJoinType = 0
  OffsetOpenResult = false
  PartialLoad = false
  Refine = true
  Relative = true
  Support = -> [Body011[Pocket044.Face2]]
  _Version = 2
FEATURE [PartDesign::SubShapeBinder] Binder019  label="Binder034"
  BindCopyOnChange = 0
  BindMode = 0
  ClaimChildren = false
  Context = -> Part001 [Body009.Binder019.]
  Fuse = false
  MakeFace = true
  OffsetFill = false
  OffsetIntersection = false
  OffsetJoinType = 0
  OffsetOpenResult = false
  PartialLoad = false
  Refine = true
  Relative = true
  Support = -> [Body011[Pocket044.Face4]]
  _Version = 2
FEATURE [PartDesign::SubShapeBinder] Binder034  label="Binder035"
  BindCopyOnChange = 0
  BindMode = 0
  ClaimChildren = false
  Context = -> Part001 [Body004.Binder034.]
  Fuse = false
  MakeFace = true
  OffsetFill = false
  OffsetIntersection = false
  OffsetJoinType = 0
  OffsetOpenResult = false
  PartialLoad = false
  Refine = true
  Relative = true
  Support = -> [Body033[Pocket051.Face2]]
  _Version = 2
FEATURE [PartDesign::SubShapeBinder] Binder035  label="Binder036"
  BindCopyOnChange = 0
  BindMode = 0
  ClaimChildren = false
  Context = -> Part001 [Body007.Binder035.]
  Fuse = false
  MakeFace = true
  OffsetFill = false
  OffsetIntersection = false
  OffsetJoinType = 0
  OffsetOpenResult = false
  PartialLoad = false
  Refine = true
  Relative = true
  Support = -> [Body033[Pocket051.Face4]]
  _Version = 2
FEATURE [PartDesign::SubShapeBinder] Binder036  label="Binder037"
  BindCopyOnChange = 0
  BindMode = 0
  ClaimChildren = false
  Context = -> Part001 [Body003.Binder036.]
  Fuse = false
  MakeFace = true
  OffsetFill = false
  OffsetIntersection = false
  OffsetJoinType = 0
  OffsetOpenResult = false
  PartialLoad = false
  Refine = true
  Relative = true
  Support = -> [Body033[Pocket051.Face34]]
  _Version = 2
FEATURE [PartDesign::SubShapeBinder] Binder037  label="Binder038"
  BindCopyOnChange = 0
  BindMode = 0
  ClaimChildren = false
  Context = -> Part001 [Body001.Binder037.]
  Fuse = false
  MakeFace = true
  OffsetFill = false
  OffsetIntersection = false
  OffsetJoinType = 0
  OffsetOpenResult = false
  PartialLoad = false
  Refine = true
  Relative = true
  Support = -> [Body033[Pocket051.Face5]]
  _Version = 2
FEATURE [PartDesign::Plane] CopyDatumPlane001
  Length = 1867.38
  Placement = pos=(0,198.18,0) rot=(1,0,0;1.5708rad)
  ResizeMode = 0
  Width = 292.292
FEATURE [PartDesign::Plane] DatumPlane001
  AttachmentSupport = -> [XZ_Plane034,Binder002]
  Length = 664.107
  MapMode = 53
  Placement = pos=(0,-71.8202,-1.59e-14) rot=(1,0,0;1.5708rad)
  ResizeMode = 0
  Width = 235.347
FEATURE [App::DocumentObjectGroup] Group014  label="CENTER"
FEATURE [Sketcher::SketchObject] Sketch051
  ArcFitTolerance = 1e-06
  AttachmentSupport = -> [YZ_Plane033]
  FullyConstrained = true
  MakeInternals = false
  MapMode = 5
  Placement = pos=(0,0,0) rot=(0.57735,0.57735,0.57735;2.0944rad)
  sketch-geometry (4):
    g0: LineSegment StartX=2 StartY=0 StartZ=0 EndX=2 EndY=140 EndZ=0
    g1: LineSegment StartX=0 StartY=140 StartZ=0 EndX=0 EndY=0 EndZ=0
    g2: LineSegment StartX=0 StartY=0 StartZ=0 EndX=2 EndY=0 EndZ=0
    g3: LineSegment StartX=0 StartY=140 StartZ=0 EndX=2 EndY=140 EndZ=0
  constraints (11):
    c: Vertical(g0)
    c: Vertical(g1)
    c: Distance(g0,g1) = 2
    c: Distance(g1,g1) = 140
    c: Coincident(g1,g2)
    c: Coincident(g1,g-1)
    c: Coincident(g0,g2)
    c: PointOnObject(g0,g-1)
    c: Coincident(g3,g1)
    c: Coincident(g3,g0)
    c: Horizontal(g3)
FEATURE [PartDesign::Pad] Pad031
  Direction = (1,0,0)
  Length = 200
  Length2 = 10
  Placement = pos=(0,0,0) rot=(1,1,1;2.0944rad)
  Profile = -> Sketch051
  ReferenceAxis = -> Sketch051 [N_Axis]
  Refine = true
  Suppressed = false
  Type = 0
FEATURE [Sketcher::SketchObject] Sketch005
  ArcFitTolerance = 1e-06
  AttachmentSupport = -> [YZ_Plane002]
  FullyConstrained = true
  MakeInternals = false
  MapMode = 5
  Placement = pos=(0,0,0) rot=(0.57735,0.57735,0.57735;2.0944rad)
  sketch-geometry (4):
    g0: LineSegment StartX=0 StartY=0 StartZ=0 EndX=0 EndY=140 EndZ=0
    g1: LineSegment StartX=0 StartY=0 StartZ=0 EndX=2 EndY=0 EndZ=0
    g2: LineSegment StartX=2 StartY=0 StartZ=0 EndX=2 EndY=140 EndZ=0
    g3: LineSegment StartX=0 StartY=140 StartZ=0 EndX=2 EndY=140 EndZ=0
  constraints (11):
    c: Distance(g0) = 140
    c: Coincident(g0,g-1)
    c: PointOnObject(g0,g-2)
    c: Distance(g1) = 2
    c: Coincident(g1,g0)
    c: Vertical(g2)
    c: Coincident(g3,g0)
    c: Coincident(g3,g2)
    c: Horizontal(g3)
    c: Coincident(g2,g1)
    c: Horizontal(g1)
FEATURE [PartDesign::Pad] Pad002
  Direction = (1,0,0)
  Length = 295
  Length2 = 10
  Placement = pos=(0,0,0) rot=(1,1,1;2.0944rad)
  Profile = -> Sketch005
  ReferenceAxis = -> Sketch005 [N_Axis]
  Refine = true
  Suppressed = false
  Type = 0
FEATURE [Sketcher::SketchObject] Sketch052
  ArcFitTolerance = 1e-06
  AttachmentSupport = -> [XZ_Plane003]
  FullyConstrained = false
  MakeInternals = false
  MapMode = 5
  Placement = pos=(0,0,0) rot=(1,0,0;1.5708rad)
  sketch-geometry (31):
    g0: LineSegment StartX=-300 StartY=-200 StartZ=0 EndX=300 EndY=-200 EndZ=0
    g1: LineSegment StartX=300 StartY=-200 StartZ=0 EndX=300 EndY=-120 EndZ=0
    g2: LineSegment StartX=-300 StartY=154.794 StartZ=0 EndX=-300 EndY=-200 EndZ=0
    g3: GeomPoint [constr] X=0 Y=0 Z=0
    g4: LineSegment StartX=-230 StartY=65.1308 StartZ=0 EndX=-230 EndY=-68.8692 EndZ=0
    g5: LineSegment StartX=-210 StartY=-88.8692 StartZ=0 EndX=-163 EndY=-88.8692 EndZ=0
    g6: LineSegment StartX=-143 StartY=-68.8692 StartZ=0 EndX=-143 EndY=65.1308 EndZ=0
    g7: LineSegment StartX=-163 StartY=85.1308 StartZ=0 EndX=-210 EndY=85.1308 EndZ=0
    g8: ArcOfCircle CenterX=-210 CenterY=65.1308 CenterZ=0 NormalX=0 NormalY=0 NormalZ=1 AngleXU=0 Radius=20 StartAngle=1.5708 EndAngle=3.14159
    g9: ArcOfCircle CenterX=-210 CenterY=-68.8692 CenterZ=0 NormalX=0 NormalY=0 NormalZ=1 AngleXU=0 Radius=20 StartAngle=3.14159 EndAngle=4.71239
    g10: ArcOfCircle CenterX=-163 CenterY=-68.8692 CenterZ=0 NormalX=0 NormalY=0 NormalZ=1 AngleXU=0 Radius=20 StartAngle=4.71239 EndAngle=6.28319
    g11: ArcOfCircle CenterX=-163 CenterY=65.1308 CenterZ=0 NormalX=0 NormalY=0 NormalZ=1 AngleXU=0 Radius=20 StartAngle=0 EndAngle=1.5708
    g12: GeomPoint [constr] X=-230 Y=85.1308 Z=0
    g13: GeomPoint [constr] X=-143 Y=-88.8692 Z=0
    g14: LineSegment [constr] StartX=-300 StartY=-120 StartZ=0 EndX=-55 EndY=-120 EndZ=0
    g15: LineSegment [constr] StartX=-55 StartY=-200 StartZ=0 EndX=-55 EndY=-120 EndZ=0
    g16: LineSegment StartX=-55 StartY=-120 StartZ=0 EndX=300 EndY=-120 EndZ=0
    g17: LineSegment StartX=300 StartY=142 StartZ=0 EndX=-55 EndY=142 EndZ=0
    g18: LineSegment StartX=-55 StartY=142 StartZ=0 EndX=-55 EndY=-120 EndZ=0
    g19: LineSegment [constr] StartX=-300 StartY=150 StartZ=0 EndX=-300 EndY=105.005 EndZ=0
    g20: LineSegment [constr] StartX=-300.037 StartY=80 StartZ=0 EndX=-234.617 EndY=80 EndZ=0
    g21: LineSegment [constr] StartX=-234.617 StartY=80 StartZ=0 EndX=-234.617 EndY=175 EndZ=0
    g22: LineSegment [constr] StartX=-234.617 StartY=175 StartZ=0 EndX=-300 EndY=150 EndZ=0
    g23: LineSegment StartX=300 StartY=142 StartZ=0 EndX=300 EndY=200 EndZ=0
    g24: LineSegment [constr] StartX=122.5 StartY=-120 StartZ=0 EndX=122.5 EndY=-200 EndZ=0
    g25: LineSegment [constr] StartX=-300 StartY=154.794 StartZ=0 EndX=900 EndY=154.794 EndZ=0
    g26: ArcOfCircle CenterX=299.932 CenterY=-3803.45 CenterZ=0 NormalX=0 NormalY=0 NormalZ=1 AngleXU=0 Radius=4003.45 StartAngle=1.57078 EndAngle=1.72122
    g27: LineSegment [constr] StartX=-230 StartY=65.1308 StartZ=0 EndX=-143 EndY=65.1308 EndZ=0
    g28: LineSegment [constr] StartX=-230 StartY=-68.8692 StartZ=0 EndX=-143 EndY=-68.8692 EndZ=0
    g29: LineSegment [constr] StartX=-186.5 StartY=-68.8692 StartZ=0 EndX=-186.5 EndY=126.261 EndZ=0
    g30: LineSegment [constr] StartX=-300 StartY=15.0643 StartZ=0 EndX=-230 EndY=15.0643 EndZ=0
  constraints (78):
    c: Coincident(g0,g1)
    c: Coincident(g2,g0)
    c: Horizontal(g0)
    c: Vertical(g1)
    c: Vertical(g2)
    c: Symmetric(g23,g0,g3)
    c: Distance(g1,g2) = 600
    c: Distance(g0,g19) = 350
    c: Coincident(g3,g-1)
    c: Tangent(g4,g8) = -1.5708
    c: Tangent(g4,g9) = -1.5708
    c: Tangent(g5,g9) = -1.5708
    c: Tangent(g5,g10) = -1.5708
    c: Tangent(g6,g10) = -1.5708
    c: Tangent(g6,g11) = -1.5708
    c: Tangent(g7,g11) = -1.5708
    c: Tangent(g7,g8) = -1.5708
    c: Vertical(g4)
    c: Vertical(g6)
    c: Horizontal(g5)
    c: Horizontal(g7)
    c: Equal(g8,g9)
    c: Equal(g9,g10)
    c: Equal(g10,g11)
    c: PointOnObject(g12,g4)
    c: PointOnObject(g12,g7)
    c: PointOnObject(g13,g5)
    c: PointOnObject(g13,g6)
    c: Radius(g9) = 20
    c: Distance(g14) = 245
    c: PointOnObject(g14,g2)
    c: Horizontal(g14)
    c: Distance(g15) = 80
    c: PointOnObject(g15,g0)
    c: Vertical(g15)
    c: Coincident(g14,g15)
    c: Coincident(g17,g18)
    c: Coincident(g18,g16)
    c: Horizontal(g16)
    c: Horizontal(g17)
    c: Vertical(g18)
    c: Distance(g16,g17) = 262
    c: Coincident(g16,g14)
    c: Coincident(g20,g21)
    c: Coincident(g21,g22)
    c: Coincident(g22,g19)
    c: Vertical(g19)
    c: Vertical(g21)
    c: Horizontal(g20)
    c: Distance(g19,g21) = 70
    c: Distance(g20,g22) = 70
    c: PointOnObject(g17,g23)
    c: Coincident(g1,g16)
    c: PointOnObject(g23,g17)
    c: Symmetric(g16,g16,g24)
    c: PointOnObject(g24,g0)
    c: Vertical(g24)
    c: Vertical(g23)
    c: Distance(g25) = 1200
    c: PointOnObject(g25,g19)
    c: Horizontal(g25)
    c: Coincident(g26,g25)
    c: Coincident(g2,g25)
    c: Coincident(g23,g26)
    c: DistanceY(g0,g23) = 400
    c: Coincident(g27,g4)
    c: Coincident(g27,g6)
    c: Coincident(g28,g4)
    c: Coincident(g28,g6)
    c: Symmetric(g28,g28,g29)
    c: Vertical(g29)
    c: Distance(g30) = 70
    c: PointOnObject(g30,g2)
    c: Horizontal(g30)
    c: DistanceY(g5,g7) = 174
    c: DistanceX(g4,g6) = 87
    c: DistanceX(g17,g17) = 355
    c: PointOnObject(g30,g4)
FEATURE [PartDesign::Pad] Pad003
  Direction = (0,-1,2e-16)
  Length = 2
  Length2 = 10
  Placement = pos=(0,0,0) rot=(1,0,0;1.5708rad)
  Profile = -> Sketch052
  ReferenceAxis = -> Sketch052 [N_Axis]
  Refine = true
  Reversed = true
  Suppressed = false
  Type = 0
FEATURE [Sketcher::SketchObject] Sketch012
  ArcFitTolerance = 1e-06
  AttachmentSupport = -> [Binder029]
  ExternalGeometry = -> [Binder029]
  FullyConstrained = true
  MakeInternals = false
  MapMode = 5
  Placement = pos=(0,86.1695,-49.75) rot=(1,0,0;1.0472rad)
  sketch-geometry (24):
    g0: LineSegment StartX=300 StartY=-176 StartZ=0 EndX=900 EndY=-176 EndZ=0
    g1: LineSegment StartX=900 StartY=-176 StartZ=0 EndX=900 EndY=178.794 EndZ=0
    g2: LineSegment StartX=300 StartY=-96 StartZ=0 EndX=410 EndY=-96 EndZ=0
    g3: LineSegment StartX=410 StartY=-96 StartZ=0 EndX=410 EndY=166 EndZ=0
    g4: LineSegment StartX=300 StartY=166 StartZ=0 EndX=410 EndY=166 EndZ=0
    g5: LineSegment [constr] StartX=-300 StartY=178.794 StartZ=0 EndX=900 EndY=178.794 EndZ=0
    g6: ArcOfCircle CenterX=299.932 CenterY=-3779.45 CenterZ=0 NormalX=0 NormalY=0 NormalZ=1 AngleXU=0 Radius=4003.47 StartAngle=1.42034 EndAngle=1.57078
    g7: LineSegment StartX=300 StartY=-96 StartZ=0 EndX=300 EndY=-176 EndZ=0
    g8: LineSegment StartX=500 StartY=-64.8692 StartZ=0 EndX=547 EndY=-64.8692 EndZ=0
    g9: LineSegment StartX=567 StartY=-44.8692 StartZ=0 EndX=567 EndY=89.1308 EndZ=0
    g10: LineSegment StartX=547 StartY=109.131 StartZ=0 EndX=500 EndY=109.131 EndZ=0
    g11: LineSegment StartX=480 StartY=89.1308 StartZ=0 EndX=480 EndY=-44.8692 EndZ=0
    g12: ArcOfCircle CenterX=500 CenterY=-44.8692 CenterZ=0 NormalX=0 NormalY=0 NormalZ=1 AngleXU=0 Radius=20 StartAngle=3.14159 EndAngle=4.71239
    g13: ArcOfCircle CenterX=547 CenterY=-44.8692 CenterZ=0 NormalX=0 NormalY=0 NormalZ=1 AngleXU=0 Radius=20 StartAngle=4.71239 EndAngle=6.28319
    g14: ArcOfCircle CenterX=547 CenterY=89.1308 CenterZ=0 NormalX=0 NormalY=0 NormalZ=1 AngleXU=0 Radius=20 StartAngle=0 EndAngle=1.5708
    g15: ArcOfCircle CenterX=500 CenterY=89.1308 CenterZ=0 NormalX=0 NormalY=0 NormalZ=1 AngleXU=0 Radius=20 StartAngle=1.5708 EndAngle=3.14159
    g16: GeomPoint [constr] X=480 Y=-64.8692 Z=0
    g17: GeomPoint [constr] X=567 Y=109.131 Z=0
    g18: LineSegment [constr] StartX=-143 StartY=-44.8692 StartZ=0 EndX=480 EndY=-44.8692 EndZ=0
    g19: LineSegment StartX=665 StartY=-146 StartZ=0 EndX=850 EndY=-146 EndZ=0
    g20: LineSegment StartX=850 StartY=-146 StartZ=0 EndX=850 EndY=134 EndZ=0
    g21: LineSegment StartX=850 StartY=134 StartZ=0 EndX=665 EndY=134 EndZ=0
    g22: LineSegment StartX=665 StartY=134 StartZ=0 EndX=665 EndY=-146 EndZ=0
    g23: LineSegment StartX=300 StartY=224.02 StartZ=0 EndX=300 EndY=166 EndZ=0
  constraints (61):
    c: Coincident(g0,g-3)
    c: Horizontal(g0)
    c: Coincident(g1,g0)
    c: Vertical(g1)
    c: Coincident(g2,g-7)
    c: Horizontal(g2)
    c: Coincident(g3,g2)
    c: Vertical(g3)
    c: Coincident(g4,g-5)
    c: Horizontal(g4)
    c: Coincident(g3,g4)
    c: DistanceX(g0,g0) = 600
    c: Coincident(g5,g-6)
    c: Coincident(g5,g1)
    c: Horizontal(g5)
    c: Coincident(g6,g-6)
    c: Coincident(g6,g1)
    c: Coincident(g7,g2)
    c: Coincident(g7,g0)
    c: DistanceX(g4,g4) = 110
    c: Tangent(g8,g12) = -1.5708
    c: Tangent(g8,g13) = -1.5708
    c: Tangent(g9,g13) = -1.5708
    c: Tangent(g9,g14) = -1.5708
    c: Tangent(g10,g14) = -1.5708
    c: Tangent(g10,g15) = -1.5708
    c: Tangent(g11,g15) = -1.5708
    c: Tangent(g11,g12) = -1.5708
    c: Horizontal(g8)
    c: Horizontal(g10)
    c: Vertical(g9)
    c: Vertical(g11)
    c: Equal(g12,g13)
    c: Equal(g13,g14)
    c: Equal(g14,g15)
    c: PointOnObject(g16,g8)
    c: PointOnObject(g16,g11)
    c: PointOnObject(g17,g9)
    c: PointOnObject(g17,g10)
    c: Equal(g15,g-8)
    c: Equal(g-10,g10)
    c: Equal(g-9,g11)
    c: Coincident(g18,g-9)
    c: Coincident(g18,g11)
    c: Horizontal(g18)
    c: DistanceX(g3,g11) = 70
    c: Coincident(g19,g20)
    c: Coincident(g20,g21)
    c: Coincident(g21,g22)
    c: Coincident(g22,g19)
    c: Horizontal(g19)
    c: Horizontal(g21)
    c: Vertical(g20)
    c: Vertical(g22)
    c: DistanceY(g22,g22) = 280
    c: DistanceX(g21,g21) = 185
    c: DistanceY(g0,g19) = 30
    c: DistanceX(g20,g1) = 50
    c: Coincident(g23,g6)
    c: Coincident(g23,g4)
    c: Vertical(g23)
FEATURE [PartDesign::Pad] Pad004
  Direction = (0,-0.866025,0.5)
  Length = 2
  Length2 = 10
  Profile = -> Sketch012
  ReferenceAxis = -> Sketch012 [N_Axis]
  Refine = true
  Reversed = true
  Suppressed = false
  Type = 0
FEATURE [Sketcher::SketchObject] Sketch053
  ArcFitTolerance = 1e-06
  AttachmentSupport = -> [DatumPlane001]
  ExternalGeometry = -> [Binder002]
  FullyConstrained = false
  MakeInternals = false
  MapMode = 5
  Placement = pos=(0,-71.8202,-1.59e-14) rot=(1,0,0;1.5708rad)
  sketch-geometry (4):
    g0: ArcOfCircle CenterX=299.094 CenterY=-4459.19 CenterZ=0 NormalX=0 NormalY=0 NormalZ=1 AngleXU=0 Radius=4603.43 StartAngle=1.5706 EndAngle=1.70131
    g1: LineSegment StartX=300 StartY=144.24 StartZ=0 EndX=300 EndY=146.24 EndZ=0
    g2: LineSegment StartX=-300 StartY=105.09 StartZ=0 EndX=-300 EndY=107.09 EndZ=0
    g3: ArcOfCircle CenterX=299.093 CenterY=-4457.17 CenterZ=0 NormalX=0 NormalY=0 NormalZ=1 AngleXU=0 Radius=4603.41 StartAngle=1.5706 EndAngle=1.70131
  constraints (10):
    c: Coincident(g0,g-5)
    c: Coincident(g0,g-4)
    c: Distance(g1) = 2
    c: Coincident(g1,g0)
    c: Vertical(g1)
    c: Distance(g2) = 2
    c: Coincident(g3,g2)
    c: Vertical(g2)
    c: Coincident(g3,g1)
    c: Coincident(g2,g0)
FEATURE [PartDesign::Pad] Pad032
  Direction = (0,-1,2e-16)
  Length = 300
  Length2 = 10
  Midplane = true
  Placement = pos=(0,-71.8202,-1.59e-14) rot=(1,0,0;1.5708rad)
  Profile = -> Sketch053
  ReferenceAxis = -> Sketch053 [N_Axis]
  Refine = true
  Suppressed = false
  Type = 0
FEATURE [PartDesign::Plane] DatumPlane002  label="Plano de refencia "
  AttachmentSupport = -> [Pad032]
  Length = 216.57
  MapMode = 5
  Placement = pos=(300,-71.8202,-1.59e-14) rot=(0.707107,0,0.707107;3.14159rad)
  ResizeMode = 0
  Width = 345.331
FEATURE [PartDesign::Body] Body032  label="LaminaSprPt1"
  AllowCompound = false
  Group = -> [Binder002,DatumPlane001,Sketch053,Pad032,DatumPlane002]
  Origin = -> Origin034
  Placement = pos=(0,270,0) rot=(0,0,1;0rad)
  Tip = -> Pad032
FEATURE [Sketcher::SketchObject] Sketch054
  ArcFitTolerance = 1e-06
  AttachmentSupport = -> [CopyDatumPlane001]
  ExternalGeometry = -> [Binder003]
  FullyConstrained = false
  MakeInternals = false
  MapMode = 5
  Placement = pos=(0,198.18,0) rot=(1,0,0;1.5708rad)
  sketch-geometry (4):
    g0: ArcOfCircle CenterX=-1712.36 CenterY=-4462.69 CenterZ=0 NormalX=0 NormalY=0 NormalZ=1 AngleXU=0 Radius=4346.96 StartAngle=1.43642 EndAngle=1.57485
    g1: LineSegment StartX=-1130 StartY=-154.91 StartZ=0 EndX=-1130 EndY=-152.91 EndZ=0
    g2: ArcOfCircle CenterX=-1712.37 CenterY=-4460.9 CenterZ=0 NormalX=0 NormalY=0 NormalZ=1 AngleXU=0 Radius=4347.18 StartAngle=1.43643 EndAngle=1.57485
    g3: LineSegment StartX=-1730 StartY=-113.76 StartZ=0 EndX=-1730 EndY=-115.76 EndZ=0
  constraints (10):
    c: Coincident(g0,g-5)
    c: Coincident(g0,g-4)
    c: Distance(g1) = 2
    c: Coincident(g1,g0)
    c: Vertical(g1)
    c: Coincident(g3,g2)
    c: Coincident(g3,g0)
    c: Vertical(g3)
    c: Coincident(g2,g1)
    c: DistanceY(g3,g3) = 2
FEATURE [PartDesign::Pad] Pad006
  Direction = (0,-1,2e-16)
  Length = 300
  Length2 = 10
  Midplane = true
  Placement = pos=(0,198.18,0) rot=(1,0,0;1.5708rad)
  Profile = -> Sketch054
  ReferenceAxis = -> Sketch054 [N_Axis]
  Refine = true
  Suppressed = false
  Type = 0
FEATURE [PartDesign::Body] Body006  label="LaminaSprPt2"
  AllowCompound = false
  Group = -> [CopyDatumPlane001,Sketch054,Binder003,Pad006]
  Origin = -> Origin007
  Placement = pos=(2030,0,260) rot=(0,0,1;0rad)
  Tip = -> Pad006
FEATURE [Sketcher::SketchObject] Sketch019
  ArcFitTolerance = 1e-06
  AttachmentSupport = -> [Pad002]
  ExternalGeometry = -> [Pad002]
  FullyConstrained = false
  MakeInternals = false
  MapMode = 5
  Placement = pos=(0,0,0) rot=(0.57735,0.57735,-0.57735;2.0944rad)
  sketch-geometry (26):
    g0: LineSegment [constr] StartX=-3.2e-14 StartY=295 StartZ=0 EndX=-10 EndY=295 EndZ=0
    g1: LineSegment [constr] StartX=-10 StartY=295 StartZ=0 EndX=-10 EndY=285 EndZ=0
    g2: LineSegment [constr] StartX=-10 StartY=285 StartZ=0 EndX=-3.2e-14 EndY=285 EndZ=0
    g3: LineSegment [constr] StartX=-3.2e-14 StartY=285 StartZ=0 EndX=-3.2e-14 EndY=295 EndZ=0
    g4: LineSegment [constr] StartX=-140 StartY=295 StartZ=0 EndX=-140 EndY=285 EndZ=0
    g5: LineSegment [constr] StartX=-140 StartY=285 StartZ=0 EndX=-130 EndY=285 EndZ=0
    g6: LineSegment [constr] StartX=-130 StartY=285 StartZ=0 EndX=-130 EndY=295 EndZ=0
    g7: LineSegment [constr] StartX=-130 StartY=295 StartZ=0 EndX=-140 EndY=295 EndZ=0
    g8: LineSegment [constr] StartX=-70 StartY=295 StartZ=0 EndX=-70 EndY=0 EndZ=0
    g9: LineSegment [constr] StartX=0 StartY=147.5 StartZ=0 EndX=-140 EndY=147.5 EndZ=0
    g10: Circle CenterX=-130 CenterY=285 CenterZ=0 NormalX=0 NormalY=0 NormalZ=1 AngleXU=0 Radius=1.5
    g11: Circle CenterX=-10 CenterY=285 CenterZ=0 NormalX=0 NormalY=0 NormalZ=1 AngleXU=0 Radius=1.5
    g12: LineSegment [constr] StartX=-10 StartY=285 StartZ=0 EndX=-130 EndY=285 EndZ=0
    g13: Circle CenterX=-70 CenterY=283.786 CenterZ=0 NormalX=0 NormalY=0 NormalZ=1 AngleXU=0 Radius=1.21447
    g14: LineSegment [constr] StartX=0 StartY=0 StartZ=0 EndX=0 EndY=10 EndZ=0
    g15: LineSegment [constr] StartX=0 StartY=10 StartZ=0 EndX=-10 EndY=10 EndZ=0
    g16: LineSegment [constr] StartX=-10 StartY=10 StartZ=0 EndX=-10 EndY=0 EndZ=0
    g17: LineSegment [constr] StartX=-10 StartY=0 StartZ=0 EndX=0 EndY=0 EndZ=0
    g18: LineSegment [constr] StartX=-140 StartY=0 StartZ=0 EndX=-130 EndY=0 EndZ=0
    g19: LineSegment [constr] StartX=-130 StartY=0 StartZ=0 EndX=-130 EndY=10 EndZ=0
    g20: LineSegment [constr] StartX=-130 StartY=10 StartZ=0 EndX=-140 EndY=10 EndZ=0
    g21: LineSegment [constr] StartX=-140 StartY=10 StartZ=0 EndX=-140 EndY=0 EndZ=0
    g22: LineSegment [constr] StartX=-130 StartY=9.85879 StartZ=0 EndX=-10 EndY=9.85879 EndZ=0
    g23: Circle CenterX=-10 CenterY=10 CenterZ=0 NormalX=0 NormalY=0 NormalZ=1 AngleXU=0 Radius=1.5
    g24: Circle CenterX=-70 CenterY=11.3588 CenterZ=0 NormalX=0 NormalY=0 NormalZ=1 AngleXU=0 Radius=1.5
    g25: Circle CenterX=-130 CenterY=10 CenterZ=0 NormalX=0 NormalY=0 NormalZ=1 AngleXU=0 Radius=1.5
  constraints (56):
    c: Coincident(g0,g1)
    c: Coincident(g1,g2)
    c: Coincident(g2,g3)
    c: Coincident(g3,g0)
    c: Horizontal(g0)
    c: Horizontal(g2)
    c: Vertical(g1)
    c: Vertical(g3)
    c: Distance(g1,g3) = 10
    c: Distance(g0,g2) = 10
    c: Coincident(g0,g-3)
    c: Coincident(g4,g5)
    c: Coincident(g5,g6)
    c: Coincident(g6,g7)
    c: Coincident(g7,g4)
    c: Vertical(g4)
    c: Vertical(g6)
    c: Horizontal(g5)
    c: Horizontal(g7)
    c: Distance(g4,g6) = 10
    c: Distance(g5,g7) = 10
    c: Coincident(g4,g-4)
    c: PointOnObject(g8,g-1)
    c: Vertical(g8)
    c: Symmetric(g-6,g-6,g9)
    c: Symmetric(g-7,g-7,g9)
    c: Coincident(g11,g1)
    c: Coincident(g12,g1)
    c: Coincident(g12,g10)
    c: Horizontal(g12)
    c: Tangent(g13,g12)
    c: Coincident(g14,g15)
    c: Coincident(g15,g16)
    c: Coincident(g16,g17)
    c: Coincident(g17,g14)
    c: Vertical(g14)
    c: Vertical(g16)
    c: Horizontal(g15)
    c: Horizontal(g17)
    c: Distance(g14,g16) = 10
    c: Distance(g15,g17) = 10
    c: Coincident(g14,g-1)
    c: Coincident(g18,g19)
    c: Coincident(g19,g20)
    c: Coincident(g20,g21)
    c: Coincident(g21,g18)
    c: Horizontal(g18)
    c: Horizontal(g20)
    c: Vertical(g19)
    c: Vertical(g21)
    c: Distance(g19,g21) = 10
    c: Distance(g18,g20) = 10
    c: Coincident(g18,g-7)
    c: Diameter(g24) = 3
    c: PointOnObject(g24,g8)
    c: Tangent(g24,g22)
FEATURE [PartDesign::Pocket] Pocket008
  BaseFeature = -> Pad002
  Direction = (0,1,0)
  Length = 5
  Length2 = 5
  Placement = pos=(0,0,0) rot=(1,1,1;2.0944rad)
  Profile = -> Sketch019
  ReferenceAxis = -> Sketch019 [N_Axis]
  Refine = true
  Suppressed = false
  Type = 0
FEATURE [Sketcher::SketchObject] Sketch020
  ArcFitTolerance = 1e-06
  AttachmentSupport = -> [Binder004]
  ExternalGeometry = -> [Binder004]
  FullyConstrained = false
  MakeInternals = false
  MapMode = 5
  Placement = pos=(-9e-16,-4.1,0) rot=(0,0.707107,0.707107;3.14159rad)
  sketch-geometry (10):
    g0: LineSegment [constr] StartX=-1180 StartY=-343.2 StartZ=0 EndX=-1160 EndY=-343.2 EndZ=0
    g1: LineSegment StartX=-1160 StartY=-341.2 StartZ=0 EndX=-1160 EndY=106.007 EndZ=0
    g2: LineSegment StartX=-1160 StartY=-343.2 StartZ=0 EndX=-1158 EndY=-343.2 EndZ=0
    g3: LineSegment StartX=-1158 StartY=-343.2 StartZ=0 EndX=-1158 EndY=108.007 EndZ=0
    g4: LineSegment StartX=-1158 StartY=108.007 StartZ=0 EndX=-1180 EndY=105.09 EndZ=0
    g5: LineSegment StartX=-1180 StartY=105.09 StartZ=0 EndX=-1180 EndY=103.09 EndZ=0
    g6: LineSegment StartX=-1180 StartY=103.09 StartZ=0 EndX=-1160 EndY=106.007 EndZ=0
    g7: LineSegment StartX=-1160 StartY=-343.2 StartZ=0 EndX=-1180 EndY=-343.2 EndZ=0
    g8: LineSegment StartX=-1180 StartY=-343.2 StartZ=0 EndX=-1180 EndY=-341.2 EndZ=0
    g9: LineSegment StartX=-1180 StartY=-341.2 StartZ=0 EndX=-1160 EndY=-341.2 EndZ=0
  constraints (26):
    c: Distance(g0) = 20
    c: Coincident(g0,g-3)
    c: Horizontal(g0)
    c: Vertical(g1)
    c: Distance(g2) = 2
    c: Coincident(g2,g0)
    c: Horizontal(g2)
    c: Coincident(g3,g2)
    c: PointOnObject(g3,g-5)
    c: Vertical(g3)
    c: Coincident(g4,g3)
    c: Coincident(g4,g-5)
    c: Distance(g5) = 2
    c: Coincident(g5,g4)
    c: Vertical(g5)
    c: Coincident(g6,g5)
    c: Coincident(g1,g6)
    c: DistanceY(g1,g3) = 2
    c: Coincident(g7,g0)
    c: Coincident(g7,g0)
    c: Distance(g8) = 2
    c: Coincident(g8,g0)
    c: Vertical(g8)
    c: Coincident(g9,g8)
    c: Horizontal(g9)
    c: Coincident(g1,g9)
FEATURE [PartDesign::Pad] Pad007
  Direction = (0,1,-2e-16)
  Length = 350
  Length2 = 10
  Profile = -> Sketch020
  ReferenceAxis = -> Sketch020 [N_Axis]
  Refine = true
  Suppressed = false
  Type = 0
FEATURE [Sketcher::SketchObject] Sketch021
  ArcFitTolerance = 1e-06
  AttachmentSupport = -> [Pad007]
  ExternalGeometry = -> [Binder004,Pad007]
  FullyConstrained = false
  MakeInternals = false
  MapMode = 5
  Placement = pos=(1160,0,0) rot=(0.57735,0.57735,0.57735;2.0944rad)
  sketch-geometry (3):
    g0: LineSegment StartX=-4.1 StartY=-203.2 StartZ=0 EndX=175.575 EndY=108.007 EndZ=0
    g1: LineSegment StartX=-4.1 StartY=108.007 StartZ=0 EndX=-4.1 EndY=-203.2 EndZ=0
    g2: LineSegment StartX=-4.1 StartY=108.007 StartZ=0 EndX=175.575 EndY=108.007 EndZ=0
  constraints (6):
    c: Angle(g-1,g0) = 1.0472
    c: Coincident(g0,g-4)
    c: Coincident(g1,g-5)
    c: Coincident(g1,g0)
    c: Coincident(g2,g1)
    c: Coincident(g0,g2)
FEATURE [PartDesign::Pocket] Pocket017
  BaseFeature = -> Pad007
  Direction = (-1,0,0)
  Length = 5
  Length2 = 5
  Midplane = true
  Profile = -> Sketch021
  ReferenceAxis = -> Sketch021 [N_Axis]
  Refine = true
  Suppressed = false
  Type = 1
FEATURE [Sketcher::SketchObject] Sketch022
  ArcFitTolerance = 1e-06
  AttachmentSupport = -> [Pocket017]
  ExternalGeometry = -> [Pocket017]
  FullyConstrained = true
  MakeInternals = false
  MapMode = 5
  Placement = pos=(1160,0,0) rot=(0.57735,0.57735,0.57735;2.0944rad)
  sketch-geometry (7):
    g0: LineSegment StartX=-4.1 StartY=-341.2 StartZ=0 EndX=-2.1 EndY=-341.2 EndZ=0
    g1: LineSegment StartX=-4.1 StartY=-341.2 StartZ=0 EndX=-4.1 EndY=-203.2 EndZ=0
    g2: LineSegment StartX=-4.1 StartY=-203.2 StartZ=0 EndX=172.736 EndY=103.09 EndZ=0
    g3: LineSegment StartX=-2.1 StartY=-341.2 StartZ=0 EndX=-2.1 EndY=-203.2 EndZ=0
    g4: LineSegment [constr] StartX=-4.1 StartY=-203.2 StartZ=0 EndX=-2.1 EndY=-203.2 EndZ=0
    g5: LineSegment StartX=-2.1 StartY=-203.2 StartZ=0 EndX=174.736 EndY=103.09 EndZ=0
    g6: LineSegment StartX=172.736 StartY=103.09 StartZ=0 EndX=174.736 EndY=103.09 EndZ=0
  constraints (17):
    c: Distance(g0) = 2
    c: Coincident(g0,g-5)
    c: Horizontal(g0)
    c: Coincident(g1,g0)
    c: Coincident(g1,g-5)
    c: Coincident(g2,g1)
    c: Coincident(g2,g-3)
    c: Coincident(g3,g0)
    c: Vertical(g3)
    c: Coincident(g4,g1)
    c: Coincident(g4,g3)
    c: Horizontal(g4)
    c: PointOnObject(g5,g-3)
    c: Coincident(g6,g2)
    c: Coincident(g6,g5)
    c: DistanceX(g6,g6) = 2
    c: Coincident(g5,g3)
FEATURE [PartDesign::Pad] Pad033
  BaseFeature = -> Pocket017
  Direction = (1,0,0)
  Length = 20
  Length2 = 10
  Profile = -> Sketch022
  ReferenceAxis = -> Sketch022 [N_Axis]
  Refine = true
  Suppressed = false
  Type = 0
FEATURE [Sketcher::SketchObject] Sketch023
  ArcFitTolerance = 1e-06
  AttachmentSupport = -> [Binder004]
  ExternalGeometry = -> [Binder004]
  FullyConstrained = true
  MakeInternals = false
  MapMode = 5
  Placement = pos=(-9e-16,-4.1,0) rot=(0,0.707107,0.707107;3.14159rad)
  sketch-geometry (3):
    g0: Circle CenterX=-1170 CenterY=-333.2 CenterZ=0 NormalX=0 NormalY=0 NormalZ=1 AngleXU=0 Radius=1.5
    g1: Circle CenterX=-1168.79 CenterY=-273.2 CenterZ=0 NormalX=0 NormalY=0 NormalZ=1 AngleXU=0 Radius=1.21447
    g2: Circle CenterX=-1170 CenterY=-213.2 CenterZ=0 NormalX=0 NormalY=0 NormalZ=1 AngleXU=0 Radius=1.5
  constraints (6):
    c: Coincident(g0,g-5)
    c: Equal(g0,g-5)
    c: Coincident(g1,g-4)
    c: Equal(g1,g-4)
    c: Coincident(g2,g-3)
    c: Equal(g2,g-3)
FEATURE [PartDesign::Pocket] Pocket018
  BaseFeature = -> Pad033
  Direction = (0,-1,2e-16)
  Length = 3
  Length2 = 5
  Profile = -> Sketch023
  ReferenceAxis = -> Sketch023 [N_Axis]
  Refine = true
  Reversed = true
  Suppressed = false
  Type = 0
FEATURE [Sketcher::SketchObject] Sketch055
  ArcFitTolerance = 1e-06
  AttachmentSupport = -> [Pocket018]
  ExternalGeometry = -> [Pocket018]
  FullyConstrained = false
  MakeInternals = false
  MapMode = 5
  Placement = pos=(-3.912e-13,84.9131,-49.0246) rot=(1,0,0;1.0472rad)
  sketch-geometry (45):
    g0: LineSegment [constr] StartX=1170 StartY=-186.687 StartZ=0 EndX=1180 EndY=-186.687 EndZ=0
    g1: LineSegment [constr] StartX=1170 StartY=-186.687 StartZ=0 EndX=1160 EndY=-186.687 EndZ=0
    g2: LineSegment [constr] StartX=1160 StartY=-186.687 StartZ=0 EndX=1160 EndY=175.647 EndZ=0
    g3: LineSegment [constr] StartX=1170 StartY=-186.687 StartZ=0 EndX=1170 EndY=-178.026 EndZ=0
    g4: LineSegment [constr] StartX=1170 StartY=-178.026 StartZ=0 EndX=1170 EndY=173.112 EndZ=0
    g5: LineSegment [constr] StartX=1170 StartY=173.112 StartZ=0 EndX=1170 EndY=153.112 EndZ=0
    g6: LineSegment [constr] StartX=1170 StartY=-178.06 StartZ=0 EndX=1180 EndY=-178.06 EndZ=0
    g7: LineSegment [constr] StartX=1180 StartY=-178.06 StartZ=0 EndX=1180 EndY=-168.06 EndZ=0
    g8: LineSegment [constr] StartX=1180 StartY=-168.06 StartZ=0 EndX=1170 EndY=-168.06 EndZ=0
    g9: LineSegment [constr] StartX=1170 StartY=-168.06 StartZ=0 EndX=1170 EndY=-178.06 EndZ=0
    g10: Circle CenterX=1170 CenterY=-168.06 CenterZ=0 NormalX=0 NormalY=0 NormalZ=1 AngleXU=0 Radius=1.5
    g11: LineSegment [constr] StartX=1170 StartY=-2.45712 StartZ=0 EndX=1180 EndY=-2.45712 EndZ=0
    g12: LineSegment [constr] StartX=1180 StartY=-2.45712 StartZ=0 EndX=1180 EndY=7.54288 EndZ=0
    g13: LineSegment [constr] StartX=1180 StartY=7.54288 StartZ=0 EndX=1170 EndY=7.54288 EndZ=0
    g14: LineSegment [constr] StartX=1170 StartY=7.54288 StartZ=0 EndX=1170 EndY=-2.45712 EndZ=0
    g15: Circle CenterX=1170 CenterY=-2.45712 CenterZ=0 NormalX=0 NormalY=0 NormalZ=1 AngleXU=0 Radius=1.5
    g16: LineSegment [constr] StartX=1170 StartY=173.112 StartZ=0 EndX=1170 EndY=163.112 EndZ=0
    g17: LineSegment [constr] StartX=1170 StartY=163.112 StartZ=0 EndX=1180 EndY=163.112 EndZ=0
    g18: LineSegment [constr] StartX=1180 StartY=163.112 StartZ=0 EndX=1180 EndY=173.112 EndZ=0
    g19: LineSegment [constr] StartX=1180 StartY=173.112 StartZ=0 EndX=1170 EndY=173.112 EndZ=0
    g20: Circle CenterX=1170 CenterY=165.291 CenterZ=0 NormalX=0 NormalY=0 NormalZ=1 AngleXU=0 Radius=1.5
    g21: LineSegment [constr] StartX=1297.09 StartY=68.0791 StartZ=0 EndX=1297.09 EndY=-37.9114 EndZ=0
    g22: LineSegment [constr] StartX=1297.09 StartY=15.0839 StartZ=0 EndX=1329.21 EndY=15.0839 EndZ=0
    g23: LineSegment [constr] StartX=1297.09 StartY=41.8939 StartZ=0 EndX=1329.2 EndY=41.8939 EndZ=0
    g24: LineSegment [constr] StartX=1297.09 StartY=-11.7261 StartZ=0 EndX=1329.2 EndY=-11.7261 EndZ=0
    g25: LineSegment [constr] StartX=1170 StartY=113.145 StartZ=0 EndX=1170 EndY=103.145 EndZ=0
    g26: LineSegment [constr] StartX=1170 StartY=103.145 StartZ=0 EndX=1180 EndY=103.145 EndZ=0
    g27: LineSegment [constr] StartX=1180 StartY=103.145 StartZ=0 EndX=1180 EndY=113.145 EndZ=0
    g28: LineSegment [constr] StartX=1180 StartY=113.145 StartZ=0 EndX=1170 EndY=113.145 EndZ=0
    g29: LineSegment [constr] StartX=1170 StartY=-51.3242 StartZ=0 EndX=1170 EndY=-61.3242 EndZ=0
    g30: LineSegment [constr] StartX=1170 StartY=-61.3242 StartZ=0 EndX=1180 EndY=-61.3242 EndZ=0
    g31: LineSegment [constr] StartX=1180 StartY=-61.3242 StartZ=0 EndX=1180 EndY=-51.3242 EndZ=0
    g32: LineSegment [constr] StartX=1180 StartY=-51.3242 StartZ=0 EndX=1170 EndY=-51.3242 EndZ=0
    g33: LineSegment [constr] StartX=1170 StartY=-118.06 StartZ=0 EndX=1180 EndY=-118.06 EndZ=0
    g34: LineSegment [constr] StartX=1180 StartY=-118.06 StartZ=0 EndX=1180 EndY=-108.06 EndZ=0
    g35: LineSegment [constr] StartX=1180 StartY=-108.06 StartZ=0 EndX=1170 EndY=-108.06 EndZ=0
    g36: LineSegment [constr] StartX=1170 StartY=-108.06 StartZ=0 EndX=1170 EndY=-118.06 EndZ=0
    g37: LineSegment [constr] StartX=1170 StartY=56.41 StartZ=0 EndX=1170 EndY=46.41 EndZ=0
    g38: LineSegment [constr] StartX=1170 StartY=46.41 StartZ=0 EndX=1180 EndY=46.41 EndZ=0
    g39: LineSegment [constr] StartX=1180 StartY=46.41 StartZ=0 EndX=1180 EndY=56.41 EndZ=0
    g40: LineSegment [constr] StartX=1180 StartY=56.41 StartZ=0 EndX=1170 EndY=56.41 EndZ=0
    g41: Circle CenterX=1170 CenterY=-108.06 CenterZ=0 NormalX=0 NormalY=0 NormalZ=1 AngleXU=0 Radius=1.5
    g42: Circle CenterX=1170 CenterY=-51.4132 CenterZ=0 NormalX=0 NormalY=0 NormalZ=1 AngleXU=0 Radius=1.5
    g43: Circle CenterX=1170 CenterY=46.41 CenterZ=0 NormalX=0 NormalY=0 NormalZ=1 AngleXU=0 Radius=1.5
    g44: Circle CenterX=1170 CenterY=103.145 CenterZ=0 NormalX=0 NormalY=0 NormalZ=1 AngleXU=0 Radius=1.5
  constraints (120):
    c: Coincident(g0,g-3)
    c: PointOnObject(g0,g-6)
    c: Horizontal(g0)
    c: Distance(g1) = 10
    c: Coincident(g1,g0)
    c: Horizontal(g1)
    c: Coincident(g2,g1)
    c: PointOnObject(g2,g-5)
    c: Vertical(g2)
    c: Coincident(g3,g0)
    c: PointOnObject(g3,g-4)
    c: Vertical(g3)
    c: Coincident(g4,g3)
    c: Vertical(g4)
    c: Distance(g5) = 20
    c: Coincident(g5,g4)
    c: PointOnObject(g5,g4)
    c: Coincident(g6,g7)
    c: Coincident(g7,g8)
    c: Coincident(g8,g9)
    c: Coincident(g9,g6)
    c: Horizontal(g6)
    c: Horizontal(g8)
    c: Vertical(g7)
    c: Vertical(g9)
    c: Distance(g7,g9) = 10
    c: Distance(g6,g8) = 10
    c: PointOnObject(g6,g3)
    c: Diameter(g10) = 3
    c: Coincident(g10,g8)
    c: Coincident(g11,g12)
    c: Coincident(g12,g13)
    c: Coincident(g13,g14)
    c: Coincident(g14,g11)
    c: Horizontal(g11)
    c: Horizontal(g13)
    c: Vertical(g12)
    c: Vertical(g14)
    c: Distance(g12,g14) = 10
    c: Distance(g11,g13) = 10
    c: Symmetric(g4,g4,g11)
    c: Diameter(g15) = 3
    c: Symmetric(g4,g4,g15)
    c: Coincident(g16,g17)
    c: Coincident(g17,g18)
    c: Coincident(g18,g19)
    c: Coincident(g19,g16)
    c: Vertical(g16)
    c: Vertical(g18)
    c: Horizontal(g17)
    c: Horizontal(g19)
    c: Distance(g16,g18) = 10
    c: Distance(g17,g19) = 10
    c: Coincident(g16,g4)
    c: Diameter(g20) = 3
    c: PointOnObject(g20,g4)
    c: Vertical(g21)
    c: Symmetric(g21,g21,g22)
    c: Horizontal(g22)
    c: PointOnObject(g23,g21)
    c: Horizontal(g23)
    c: PointOnObject(g24,g21)
    c: Horizontal(g24)
    c: Symmetric(g23,g24,g22)
    c: DistanceY(g22,g23) = 26.81
    c: Coincident(g25,g26)
    c: Coincident(g26,g27)
    c: Coincident(g27,g28)
    c: Coincident(g28,g25)
    c: Vertical(g25)
    c: Vertical(g27)
    c: Horizontal(g26)
    c: Horizontal(g28)
    c: Distance(g25,g27) = 10
    c: Distance(g26,g28) = 10
    c: PointOnObject(g25,g4)
    c: Coincident(g29,g30)
    c: Coincident(g30,g31)
    c: Coincident(g31,g32)
    c: Coincident(g32,g29)
    c: Vertical(g29)
    c: Vertical(g31)
    c: Horizontal(g30)
    c: Horizontal(g32)
    c: Distance(g29,g31) = 10
    c: Distance(g30,g32) = 10
    c: PointOnObject(g29,g4)
    c: Coincident(g33,g34)
    c: Coincident(g34,g35)
    c: Coincident(g35,g36)
    c: Coincident(g36,g33)
    c: Horizontal(g33)
    c: Horizontal(g35)
    c: Vertical(g34)
    c: Vertical(g36)
    c: Distance(g34,g36) = 10
    c: Distance(g33,g35) = 10
    c: Coincident(g37,g38)
    c: Coincident(g38,g39)
    c: Coincident(g39,g40)
    c: Coincident(g40,g37)
    c: Vertical(g37)
    c: Vertical(g39)
    c: Horizontal(g38)
    c: Horizontal(g40)
    c: Distance(g37,g39) = 10
    c: Distance(g38,g40) = 10
    c: Block(g11)
    c: Symmetric(g37,g29,g11)
    c: Symmetric(g35,g25,g11)
    c: Block(g8)
    c: DistanceY(g7,g33) = 50
    c: Diameter(g41) = 3
    c: Coincident(g41,g35)
    c: Diameter(g42) = 3
    c: PointOnObject(g42,g4)
    c: Diameter(g43) = 3
    c: Coincident(g43,g37)
    c: Diameter(g44) = 3
    c: Coincident(g44,g25)
FEATURE [PartDesign::Pocket] Pocket019
  BaseFeature = -> Pocket018
  Direction = (-4e-15,0.866026,-0.5)
  Length = 5
  Length2 = 5
  Profile = -> Sketch055
  ReferenceAxis = -> Sketch055 [N_Axis]
  Refine = true
  Suppressed = false
  Type = 0
FEATURE [Sketcher::SketchObject] Sketch056
  ArcFitTolerance = 1e-06
  AttachmentSupport = -> [Pocket019]
  ExternalGeometry = -> [Pocket019]
  FullyConstrained = true
  MakeInternals = false
  MapMode = 5
  Placement = pos=(34.0789,5.7e-14,257.027) rot=(0,1,0;0.13182rad)
  sketch-geometry (17):
    g0: LineSegment [constr] StartX=1155.95 StartY=345.9 StartZ=0 EndX=1145.95 EndY=345.9 EndZ=0
    g1: LineSegment [constr] StartX=1145.95 StartY=345.9 StartZ=0 EndX=1145.95 EndY=335.9 EndZ=0
    g2: LineSegment [constr] StartX=1145.95 StartY=335.9 StartZ=0 EndX=1155.95 EndY=335.9 EndZ=0
    g3: LineSegment [constr] StartX=1155.95 StartY=335.9 StartZ=0 EndX=1155.95 EndY=345.9 EndZ=0
    g4: LineSegment [constr] StartX=1155.95 StartY=173.891 StartZ=0 EndX=1155.95 EndY=183.891 EndZ=0
    g5: LineSegment [constr] StartX=1155.95 StartY=183.891 StartZ=0 EndX=1145.95 EndY=183.891 EndZ=0
    g6: LineSegment [constr] StartX=1145.95 StartY=183.891 StartZ=0 EndX=1145.95 EndY=173.891 EndZ=0
    g7: LineSegment [constr] StartX=1145.95 StartY=173.891 StartZ=0 EndX=1155.95 EndY=173.891 EndZ=0
    g8: LineSegment [constr] StartX=1155.95 StartY=259.896 StartZ=0 EndX=1155.95 EndY=269.896 EndZ=0
    g9: LineSegment [constr] StartX=1155.95 StartY=269.896 StartZ=0 EndX=1145.95 EndY=269.896 EndZ=0
    g10: LineSegment [constr] StartX=1145.95 StartY=269.896 StartZ=0 EndX=1145.95 EndY=259.896 EndZ=0
    g11: LineSegment [constr] StartX=1145.95 StartY=259.896 StartZ=0 EndX=1155.95 EndY=259.896 EndZ=0
    g12: LineSegment [constr] StartX=1145.95 StartY=335.9 StartZ=0 EndX=1145.95 EndY=269.896 EndZ=0
    g13: LineSegment [constr] StartX=1145.95 StartY=259.896 StartZ=0 EndX=1145.95 EndY=183.891 EndZ=0
    g14: Circle CenterX=1145.95 CenterY=183.891 CenterZ=0 NormalX=0 NormalY=0 NormalZ=1 AngleXU=0 Radius=1.5
    g15: Circle CenterX=1145.95 CenterY=259.896 CenterZ=0 NormalX=0 NormalY=0 NormalZ=1 AngleXU=0 Radius=1.5
    g16: Circle CenterX=1145.95 CenterY=335.9 CenterZ=0 NormalX=0 NormalY=0 NormalZ=1 AngleXU=0 Radius=1.5
  constraints (43):
    c: Coincident(g0,g1)
    c: Coincident(g1,g2)
    c: Coincident(g2,g3)
    c: Coincident(g3,g0)
    c: Horizontal(g0)
    c: Horizontal(g2)
    c: Vertical(g1)
    c: Vertical(g3)
    c: Distance(g1,g3) = 10
    c: Distance(g0,g2) = 10
    c: Coincident(g0,g-4)
    c: Coincident(g4,g5)
    c: Coincident(g5,g6)
    c: Coincident(g6,g7)
    c: Coincident(g7,g4)
    c: Vertical(g4)
    c: Vertical(g6)
    c: Horizontal(g5)
    c: Horizontal(g7)
    c: Distance(g4,g6) = 10
    c: Distance(g5,g7) = 10
    c: Coincident(g4,g-3)
    c: Coincident(g8,g9)
    c: Coincident(g9,g10)
    c: Coincident(g10,g11)
    c: Coincident(g11,g8)
    c: Vertical(g8)
    c: Vertical(g10)
    c: Horizontal(g9)
    c: Horizontal(g11)
    c: Distance(g8,g10) = 10
    c: Distance(g9,g11) = 10
    c: Symmetric(g-3,g-3,g8)
    c: Coincident(g12,g1)
    c: Coincident(g12,g9)
    c: Coincident(g13,g10)
    c: Coincident(g13,g5)
    c: Diameter(g14) = 3
    c: Coincident(g14,g5)
    c: Diameter(g15) = 3
    c: Coincident(g15,g10)
    c: Diameter(g16) = 3
    c: Coincident(g16,g1)
FEATURE [PartDesign::Pocket] Pocket012
  BaseFeature = -> Pocket019
  Direction = (-0.131439,0,-0.991324)
  Length = 5
  Length2 = 5
  Profile = -> Sketch056
  ReferenceAxis = -> Sketch056 [N_Axis]
  Refine = true
  Suppressed = false
  Type = 0
FEATURE [Sketcher::SketchObject] Sketch026
  ArcFitTolerance = 1e-06
  AttachmentSupport = -> [Pocket012]
  ExternalGeometry = -> [Pocket012]
  FullyConstrained = false
  MakeInternals = false
  MapMode = 5
  Placement = pos=(0,-7.51e-14,-341.2) rot=(0,0,1;0rad)
  sketch-geometry (27):
    g0: LineSegment [constr] StartX=1180 StartY=345.9 StartZ=0 EndX=1170 EndY=345.9 EndZ=0
    g1: LineSegment [constr] StartX=1170 StartY=345.9 StartZ=0 EndX=1170 EndY=335.9 EndZ=0
    g2: LineSegment [constr] StartX=1170 StartY=335.9 StartZ=0 EndX=1180 EndY=335.9 EndZ=0
    g3: LineSegment [constr] StartX=1180 StartY=335.9 StartZ=0 EndX=1180 EndY=345.9 EndZ=0
    g4: LineSegment [constr] StartX=1180 StartY=-2.1 StartZ=0 EndX=1180 EndY=7.9 EndZ=0
    g5: LineSegment [constr] StartX=1180 StartY=7.9 StartZ=0 EndX=1170 EndY=7.9 EndZ=0
    g6: LineSegment [constr] StartX=1170 StartY=7.9 StartZ=0 EndX=1170 EndY=-2.1 EndZ=0
    g7: LineSegment [constr] StartX=1170 StartY=-2.1 StartZ=0 EndX=1180 EndY=-2.1 EndZ=0
    g8: LineSegment [constr] StartX=1180 StartY=171.9 StartZ=0 EndX=1180 EndY=181.9 EndZ=0
    g9: LineSegment [constr] StartX=1180 StartY=181.9 StartZ=0 EndX=1170 EndY=181.9 EndZ=0
    g10: LineSegment [constr] StartX=1170 StartY=181.9 StartZ=0 EndX=1170 EndY=171.9 EndZ=0
    g11: LineSegment [constr] StartX=1170 StartY=171.9 StartZ=0 EndX=1180 EndY=171.9 EndZ=0
    g12: LineSegment [constr] StartX=1170 StartY=181.9 StartZ=0 EndX=1170 EndY=335.9 EndZ=0
    g13: LineSegment [constr] StartX=1170 StartY=258.9 StartZ=0 EndX=1180 EndY=258.9 EndZ=0
    g14: LineSegment [constr] StartX=1180 StartY=258.9 StartZ=0 EndX=1180 EndY=268.9 EndZ=0
    g15: LineSegment [constr] StartX=1180 StartY=268.9 StartZ=0 EndX=1170 EndY=268.9 EndZ=0
    g16: LineSegment [constr] StartX=1170 StartY=268.9 StartZ=0 EndX=1170 EndY=258.9 EndZ=0
    g17: LineSegment [constr] StartX=1170 StartY=171.9 StartZ=0 EndX=1170 EndY=7.9 EndZ=0
    g18: LineSegment [constr] StartX=1170 StartY=89.9 StartZ=0 EndX=1180 EndY=89.9 EndZ=0
    g19: LineSegment [constr] StartX=1180 StartY=89.9 StartZ=0 EndX=1180 EndY=99.9 EndZ=0
    g20: LineSegment [constr] StartX=1180 StartY=99.9 StartZ=0 EndX=1170 EndY=99.9 EndZ=0
    g21: LineSegment [constr] StartX=1170 StartY=99.9 StartZ=0 EndX=1170 EndY=89.9 EndZ=0
    g22: Circle CenterX=1170 CenterY=335.9 CenterZ=0 NormalX=0 NormalY=0 NormalZ=1 AngleXU=0 Radius=1.5
    g23: Circle CenterX=1170 CenterY=258.9 CenterZ=0 NormalX=0 NormalY=0 NormalZ=1 AngleXU=0 Radius=1.5
    g24: Circle CenterX=1170 CenterY=171.9 CenterZ=0 NormalX=0 NormalY=0 NormalZ=1 AngleXU=0 Radius=1.5
    g25: Circle CenterX=1170 CenterY=89.9 CenterZ=0 NormalX=0 NormalY=0 NormalZ=1 AngleXU=0 Radius=1.5
    g26: Circle CenterX=1170 CenterY=7.9 CenterZ=0 NormalX=0 NormalY=0 NormalZ=1 AngleXU=0 Radius=1.5
  constraints (59):
    c: Coincident(g0,g1)
    c: Coincident(g1,g2)
    c: Coincident(g2,g3)
    c: Coincident(g3,g0)
    c: Horizontal(g0)
    c: Horizontal(g2)
    c: Vertical(g1)
    c: Vertical(g3)
    c: Distance(g1,g3) = 10
    c: Distance(g0,g2) = 10
    c: Coincident(g0,g-3)
    c: Coincident(g4,g5)
    c: Coincident(g5,g6)
    c: Coincident(g6,g7)
    c: Coincident(g7,g4)
    c: Vertical(g4)
    c: Vertical(g6)
    c: Horizontal(g5)
    c: Horizontal(g7)
    c: Distance(g4,g6) = 10
    c: Distance(g5,g7) = 10
    c: Coincident(g4,g-3)
    c: Coincident(g8,g9)
    c: Coincident(g9,g10)
    c: Coincident(g10,g11)
    c: Coincident(g11,g8)
    c: Vertical(g8)
    c: Vertical(g10)
    c: Horizontal(g9)
    c: Horizontal(g11)
    c: Distance(g8,g10) = 10
    c: Distance(g9,g11) = 10
    c: Symmetric(g-3,g-3,g8)
    c: Coincident(g12,g9)
    c: Coincident(g12,g1)
    c: Coincident(g13,g14)
    c: Coincident(g14,g15)
    c: Coincident(g15,g16)
    c: Coincident(g16,g13)
    c: Horizontal(g13)
    c: Horizontal(g15)
    c: Vertical(g14)
    c: Vertical(g16)
    c: Distance(g13,g15) = 10
    c: Symmetric(g12,g12,g13)
    c: PointOnObject(g14,g-3)
    c: Coincident(g17,g10)
    c: Coincident(g17,g5)
    c: Coincident(g18,g19)
    c: Coincident(g19,g20)
    c: Coincident(g20,g21)
    c: Coincident(g21,g18)
    c: Horizontal(g18)
    c: Horizontal(g20)
    c: Vertical(g19)
    c: Vertical(g21)
    c: Distance(g18,g20) = 10
    c: Symmetric(g17,g17,g18)
    c: PointOnObject(g19,g-3)
FEATURE [PartDesign::Pocket] Pocket013
  BaseFeature = -> Pocket012
  Direction = (0,0,-1)
  Length = 5
  Length2 = 5
  Profile = -> Sketch026
  ReferenceAxis = -> Sketch026 [N_Axis]
  Refine = true
  Suppressed = false
  Type = 0
FEATURE [Sketcher::SketchObject] Sketch027
  ArcFitTolerance = 1e-06
  AttachmentSupport = -> [Pad004]
  ExternalGeometry = -> [Binder030]
  FullyConstrained = false
  MakeInternals = false
  MapMode = 5
  Placement = pos=(0,87.9016,-50.75) rot=(0,0.866025,0.5;3.14159rad)
  sketch-geometry (7):
    g0: Circle CenterX=-890 CenterY=167.291 CenterZ=0 NormalX=0 NormalY=0 NormalZ=1 AngleXU=0 Radius=1.5
    g1: Circle CenterX=-890 CenterY=105.145 CenterZ=0 NormalX=0 NormalY=0 NormalZ=1 AngleXU=0 Radius=1.5
    g2: Circle CenterX=-890 CenterY=48.4101 CenterZ=0 NormalX=0 NormalY=0 NormalZ=1 AngleXU=0 Radius=1.5
    g3: Circle CenterX=-890 CenterY=-0.457073 CenterZ=0 NormalX=0 NormalY=0 NormalZ=1 AngleXU=0 Radius=1.5
    g4: Circle CenterX=-890 CenterY=-49.4131 CenterZ=0 NormalX=0 NormalY=0 NormalZ=1 AngleXU=0 Radius=1.5
    g5: Circle CenterX=-890 CenterY=-106.06 CenterZ=0 NormalX=0 NormalY=0 NormalZ=1 AngleXU=0 Radius=1.5
    g6: Circle CenterX=-890 CenterY=-166.06 CenterZ=0 NormalX=0 NormalY=0 NormalZ=1 AngleXU=0 Radius=1.5
  constraints (7):
    c: Coincident(g0,g-3)
    c: Coincident(g1,g-4)
    c: Coincident(g2,g-5)
    c: Coincident(g3,g-6)
    c: Coincident(g4,g-7)
    c: Coincident(g5,g-8)
    c: Coincident(g6,g-9)
FEATURE [PartDesign::Pocket] Pocket020
  BaseFeature = -> Pad004
  Direction = (0,-0.866025,0.5)
  Length = 5
  Length2 = 5
  Profile = -> Sketch027
  ReferenceAxis = -> Sketch027 [N_Axis]
  Refine = true
  Suppressed = false
  Type = 0
FEATURE [Sketcher::SketchObject] Sketch057
  ArcFitTolerance = 1e-06
  AttachmentSupport = -> [Binder006]
  ExternalGeometry = -> [Binder006]
  FullyConstrained = true
  MakeInternals = false
  MapMode = 5
  Placement = pos=(0,-0.1,0) rot=(0,0.707107,0.707107;3.14159rad)
  sketch-geometry (8):
    g0: LineSegment StartX=-627 StartY=-343.2 StartZ=0 EndX=-627 EndY=133.254 EndZ=0
    g1: LineSegment StartX=-625 StartY=-341.2 StartZ=0 EndX=-625 EndY=131.254 EndZ=0
    g2: LineSegment StartX=-627 StartY=133.254 StartZ=0 EndX=-605.052 EndY=134.764 EndZ=0
    g3: LineSegment StartX=-605.052 StartY=134.764 StartZ=0 EndX=-605.052 EndY=132.764 EndZ=0
    g4: LineSegment StartX=-605.052 StartY=132.764 StartZ=0 EndX=-625 EndY=131.254 EndZ=0
    g5: LineSegment StartX=-605 StartY=-343.2 StartZ=0 EndX=-627 EndY=-343.2 EndZ=0
    g6: LineSegment StartX=-605 StartY=-343.2 StartZ=0 EndX=-605 EndY=-341.2 EndZ=0
    g7: LineSegment StartX=-605 StartY=-341.2 StartZ=0 EndX=-625 EndY=-341.2 EndZ=0
  constraints (23):
    c: Vertical(g0)
    c: Vertical(g1)
    c: PointOnObject(g0,g-4)
    c: Distance(g2) = 22
    c: Coincident(g2,g0)
    c: PointOnObject(g2,g-4)
    c: Distance(g3) = 2
    c: Coincident(g3,g2)
    c: Vertical(g3)
    c: Coincident(g4,g3)
    c: Coincident(g1,g4)
    c: DistanceY(g1,g0) = 2
    c: Coincident(g5,g-3)
    c: Horizontal(g5)
    c: Distance(g6) = 2
    c: Coincident(g6,g5)
    c: Vertical(g6)
    c: Coincident(g7,g6)
    c: Horizontal(g7)
    c: Coincident(g7,g1)
    c: Coincident(g5,g0)
    c: DistanceX(g0,g1) = 2
    c: DistanceX(g7,g7) = 20
FEATURE [PartDesign::Pad] Pad009
  Direction = (0,1,-2e-16)
  Length = 350
  Length2 = 10
  Profile = -> Sketch057
  ReferenceAxis = -> Sketch057 [N_Axis]
  Refine = true
  Suppressed = false
  Type = 0
FEATURE [Sketcher::SketchObject] Sketch058
  ArcFitTolerance = 1e-06
  AttachmentSupport = -> [Pad009]
  ExternalGeometry = -> [Binder006,Pad009]
  FullyConstrained = true
  MakeInternals = false
  MapMode = 5
  Placement = pos=(627,0,0) rot=(0.57735,0.57735,0.57735;2.0944rad)
  sketch-geometry (3):
    g0: LineSegment StartX=-0.1 StartY=-203.2 StartZ=0 EndX=195.023 EndY=134.764 EndZ=0
    g1: LineSegment StartX=195.023 StartY=134.764 StartZ=0 EndX=-0.1 EndY=134.764 EndZ=0
    g2: LineSegment StartX=-0.1 StartY=134.764 StartZ=0 EndX=-0.1 EndY=-203.2 EndZ=0
  constraints (8):
    c: Angle(g-1,g0) = 1.0472
    c: Coincident(g0,g-3)
    c: PointOnObject(g0,g-4)
    c: Coincident(g1,g0)
    c: Horizontal(g1)
    c: Coincident(g2,g1)
    c: Coincident(g2,g0)
    c: Vertical(g2)
FEATURE [PartDesign::Pocket] Pocket021
  BaseFeature = -> Pad009
  Direction = (-1,0,0)
  Length = 5
  Length2 = 5
  Profile = -> Sketch058
  ReferenceAxis = -> Sketch058 [N_Axis]
  Refine = true
  Suppressed = false
  Type = 1
FEATURE [Sketcher::SketchObject] Sketch059
  ArcFitTolerance = 1e-06
  AttachmentSupport = -> [Pocket021]
  ExternalGeometry = -> [Pocket021]
  FullyConstrained = true
  MakeInternals = false
  MapMode = 5
  Placement = pos=(625,0,0) rot=(0.57735,-0.57735,-0.57735;2.0944rad)
  sketch-geometry (7):
    g0: LineSegment StartX=0.1 StartY=-341.2 StartZ=0 EndX=0.1 EndY=-203.2 EndZ=0
    g1: LineSegment StartX=0.1 StartY=-203.2 StartZ=0 EndX=-192.997 EndY=131.254 EndZ=0
    g2: LineSegment StartX=-192.997 StartY=131.254 StartZ=0 EndX=-194.997 EndY=131.254 EndZ=0
    g3: LineSegment StartX=-194.997 StartY=131.254 StartZ=0 EndX=-1.9 EndY=-203.2 EndZ=0
    g4: LineSegment StartX=0.1 StartY=-341.2 StartZ=0 EndX=-1.9 EndY=-341.2 EndZ=0
    g5: LineSegment StartX=-1.9 StartY=-341.2 StartZ=0 EndX=-1.9 EndY=-203.2 EndZ=0
    g6: LineSegment [constr] StartX=-1.9 StartY=-203.2 StartZ=0 EndX=0.1 EndY=-203.2 EndZ=0
  constraints (17):
    c: Coincident(g0,g-3)
    c: Coincident(g0,g-4)
    c: Coincident(g1,g0)
    c: Coincident(g1,g-4)
    c: Distance(g2) = 2
    c: Coincident(g2,g1)
    c: Horizontal(g2)
    c: Coincident(g3,g2)
    c: Distance(g4) = 2
    c: Coincident(g4,g0)
    c: Horizontal(g4)
    c: Coincident(g5,g4)
    c: Coincident(g5,g3)
    c: Vertical(g5)
    c: Coincident(g6,g3)
    c: Coincident(g6,g0)
    c: Horizontal(g6)
FEATURE [PartDesign::Pad] Pad010
  BaseFeature = -> Pocket021
  Direction = (-1,0,0)
  Length = 20
  Length2 = 10
  Profile = -> Sketch059
  ReferenceAxis = -> Sketch059 [N_Axis]
  Refine = true
  Suppressed = false
  Type = 0
FEATURE [Sketcher::SketchObject] Sketch031
  ArcFitTolerance = 1e-06
  AttachmentSupport = -> [Binder006]
  ExternalGeometry = -> [Binder006]
  FullyConstrained = true
  MakeInternals = false
  MapMode = 5
  Placement = pos=(0,-0.1,0) rot=(0,0.707107,0.707107;3.14159rad)
  sketch-geometry (3):
    g0: Circle CenterX=-615 CenterY=-213.2 CenterZ=0 NormalX=0 NormalY=0 NormalZ=1 AngleXU=0 Radius=1.5
    g1: Circle CenterX=-616.359 CenterY=-273.2 CenterZ=0 NormalX=0 NormalY=0 NormalZ=1 AngleXU=0 Radius=1.5
    g2: Circle CenterX=-615 CenterY=-333.2 CenterZ=0 NormalX=0 NormalY=0 NormalZ=1 AngleXU=0 Radius=1.5
  constraints (6):
    c: Coincident(g0,g-3)
    c: Equal(g0,g-3)
    c: Coincident(g1,g-4)
    c: Equal(g1,g-4)
    c: Coincident(g2,g-5)
    c: Equal(g2,g-5)
FEATURE [PartDesign::Pocket] Pocket022
  BaseFeature = -> Pad010
  Direction = (0,-1,2e-16)
  Length = 5
  Length2 = 5
  Profile = -> Sketch031
  ReferenceAxis = -> Sketch031 [N_Axis]
  Refine = true
  Reversed = true
  Suppressed = false
  Type = 0
FEATURE [Sketcher::SketchObject] Sketch032
  ArcFitTolerance = 1e-06
  AttachmentSupport = -> [Pocket022]
  ExternalGeometry = -> [Pocket022]
  FullyConstrained = false
  MakeInternals = false
  MapMode = 5
  Placement = pos=(1.797e-13,87.9131,-50.7566) rot=(1,0,0;1.0472rad)
  sketch-geometry (26):
    g0: LineSegment [constr] StartX=605 StartY=-176.026 StartZ=0 EndX=615 EndY=-176.026 EndZ=0
    g1: LineSegment [constr] StartX=615 StartY=-176.026 StartZ=0 EndX=615 EndY=-166.026 EndZ=0
    g2: LineSegment [constr] StartX=615 StartY=-166.026 StartZ=0 EndX=605 EndY=-166.026 EndZ=0
    g3: LineSegment [constr] StartX=605 StartY=-166.026 StartZ=0 EndX=605 EndY=-176.026 EndZ=0
    g4: LineSegment [constr] StartX=605 StartY=210.167 StartZ=0 EndX=605 EndY=200.167 EndZ=0
    g5: LineSegment [constr] StartX=605 StartY=200.167 StartZ=0 EndX=615 EndY=200.167 EndZ=0
    g6: LineSegment [constr] StartX=615 StartY=200.167 StartZ=0 EndX=615 EndY=210.167 EndZ=0
    g7: LineSegment [constr] StartX=615 StartY=210.167 StartZ=0 EndX=605 EndY=210.167 EndZ=0
    g8: LineSegment [constr] StartX=605 StartY=17.0704 StartZ=0 EndX=615 EndY=17.0704 EndZ=0
    g9: LineSegment [constr] StartX=615 StartY=17.0704 StartZ=0 EndX=615 EndY=27.0704 EndZ=0
    g10: LineSegment [constr] StartX=615 StartY=27.0704 StartZ=0 EndX=605 EndY=27.0704 EndZ=0
    g11: LineSegment [constr] StartX=605 StartY=27.0704 StartZ=0 EndX=605 EndY=17.0704 EndZ=0
    g12: LineSegment [constr] StartX=615 StartY=-74.478 StartZ=0 EndX=605 EndY=-74.478 EndZ=0
    g13: LineSegment [constr] StartX=615 StartY=113.619 StartZ=0 EndX=615 EndY=123.619 EndZ=0
    g14: LineSegment [constr] StartX=615 StartY=123.619 StartZ=0 EndX=605 EndY=123.619 EndZ=0
    g15: LineSegment [constr] StartX=605 StartY=123.619 StartZ=0 EndX=605 EndY=113.619 EndZ=0
    g16: LineSegment [constr] StartX=605 StartY=113.619 StartZ=0 EndX=615 EndY=113.619 EndZ=0
    g17: LineSegment [constr] StartX=615 StartY=113.619 StartZ=0 EndX=615 EndY=200.167 EndZ=0
    g18: LineSegment [constr] StartX=615 StartY=113.619 StartZ=0 EndX=615 EndY=17.0704 EndZ=0
    g19: LineSegment [constr] StartX=615 StartY=-166.026 StartZ=0 EndX=615 EndY=-74.478 EndZ=0
    g20: LineSegment [constr] StartX=615 StartY=17.0704 StartZ=0 EndX=615 EndY=-74.478 EndZ=0
    g21: Circle CenterX=615 CenterY=-166.026 CenterZ=0 NormalX=0 NormalY=0 NormalZ=1 AngleXU=0 Radius=1.5
    g22: Circle CenterX=615 CenterY=17.0704 CenterZ=0 NormalX=0 NormalY=0 NormalZ=1 AngleXU=0 Radius=1.5
    g23: Circle CenterX=615 CenterY=113.619 CenterZ=0 NormalX=0 NormalY=0 NormalZ=1 AngleXU=0 Radius=1.5
    g24: Circle CenterX=615 CenterY=200.167 CenterZ=0 NormalX=0 NormalY=0 NormalZ=1 AngleXU=0 Radius=1.5
    g25: Circle CenterX=615 CenterY=-74.478 CenterZ=0 NormalX=0 NormalY=0 NormalZ=1 AngleXU=0 Radius=1.5
FEATURE [PartDesign::Pocket] Pocket023
  BaseFeature = -> Pocket022
  Direction = (1.3e-15,0.866026,-0.5)
  Length = 5
  Length2 = 5
  Profile = -> Sketch032
  ReferenceAxis = -> Sketch032 [N_Axis]
  Refine = true
  Suppressed = false
  Type = 0
FEATURE [Sketcher::SketchObject] Sketch060
  ArcFitTolerance = 1e-06
  AttachmentSupport = -> [Pocket023]
  ExternalGeometry = -> [Pocket023]
  FullyConstrained = false
  MakeInternals = false
  MapMode = 5
  Placement = pos=(0,-7.51e-14,-341.2) rot=(0,0,1;0rad)
  sketch-geometry (28):
    g0: LineSegment [constr] StartX=615 StartY=349.9 StartZ=0 EndX=615 EndY=1.9 EndZ=0
    g1: LineSegment [constr] StartX=615 StartY=175.9 StartZ=0 EndX=605 EndY=175.9 EndZ=0
    g2: LineSegment [constr] StartX=605 StartY=175.9 StartZ=0 EndX=605 EndY=185.9 EndZ=0
    g3: LineSegment [constr] StartX=605 StartY=185.9 StartZ=0 EndX=615 EndY=185.9 EndZ=0
    g4: LineSegment [constr] StartX=615 StartY=185.9 StartZ=0 EndX=615 EndY=175.9 EndZ=0
    g5: LineSegment [constr] StartX=605 StartY=185.9 StartZ=0 EndX=605 EndY=349.9 EndZ=0
    g6: LineSegment [constr] StartX=605 StartY=267.9 StartZ=0 EndX=615 EndY=267.9 EndZ=0
    g7: LineSegment [constr] StartX=615 StartY=267.9 StartZ=0 EndX=615 EndY=277.9 EndZ=0
    g8: LineSegment [constr] StartX=615 StartY=277.9 StartZ=0 EndX=605 EndY=277.9 EndZ=0
    g9: LineSegment [constr] StartX=605 StartY=277.9 StartZ=0 EndX=605 EndY=267.9 EndZ=0
    g10: LineSegment [constr] StartX=605 StartY=349.9 StartZ=0 EndX=605 EndY=339.9 EndZ=0
    g11: LineSegment [constr] StartX=605 StartY=339.9 StartZ=0 EndX=615 EndY=339.9 EndZ=0
    g12: LineSegment [constr] StartX=615 StartY=339.9 StartZ=0 EndX=615 EndY=349.9 EndZ=0
    g13: LineSegment [constr] StartX=615 StartY=349.9 StartZ=0 EndX=605 EndY=349.9 EndZ=0
    g14: LineSegment [constr] StartX=615 StartY=1.9 StartZ=0 EndX=615 EndY=11.9 EndZ=0
    g15: LineSegment [constr] StartX=615 StartY=11.9 StartZ=0 EndX=605 EndY=11.9 EndZ=0
    g16: LineSegment [constr] StartX=605 StartY=11.9 StartZ=0 EndX=605 EndY=1.9 EndZ=0
    g17: LineSegment [constr] StartX=605 StartY=1.9 StartZ=0 EndX=615 EndY=1.9 EndZ=0
    g18: LineSegment [constr] StartX=605 StartY=175.9 StartZ=0 EndX=605 EndY=11.9 EndZ=0
    g19: LineSegment [constr] StartX=605 StartY=93.9 StartZ=0 EndX=615 EndY=93.9 EndZ=0
    g20: LineSegment [constr] StartX=615 StartY=93.9 StartZ=0 EndX=615 EndY=103.9 EndZ=0
    g21: LineSegment [constr] StartX=615 StartY=103.9 StartZ=0 EndX=605 EndY=103.9 EndZ=0
    g22: LineSegment [constr] StartX=605 StartY=103.9 StartZ=0 EndX=605 EndY=93.9 EndZ=0
    g23: Circle CenterX=615 CenterY=11.9 CenterZ=0 NormalX=0 NormalY=0 NormalZ=1 AngleXU=0 Radius=1.5
    g24: Circle CenterX=615 CenterY=93.9 CenterZ=0 NormalX=0 NormalY=0 NormalZ=1 AngleXU=0 Radius=1.5
    g25: Circle CenterX=615 CenterY=175.9 CenterZ=0 NormalX=0 NormalY=0 NormalZ=1 AngleXU=0 Radius=1.5
    g26: Circle CenterX=615 CenterY=267.9 CenterZ=0 NormalX=0 NormalY=0 NormalZ=1 AngleXU=0 Radius=1.5
    g27: Circle CenterX=615 CenterY=339.9 CenterZ=0 NormalX=0 NormalY=0 NormalZ=1 AngleXU=0 Radius=1.5
  constraints (59):
    c: Symmetric(g-4,g-4,g0)
    c: Symmetric(g-3,g-3,g0)
    c: Coincident(g1,g2)
    c: Coincident(g2,g3)
    c: Coincident(g3,g4)
    c: Coincident(g4,g1)
    c: Horizontal(g1)
    c: Horizontal(g3)
    c: Vertical(g2)
    c: Vertical(g4)
    c: Symmetric(g0,g0,g1)
    c: DistanceY(g2,g2) = 10
    c: DistanceX(g3,g3) = 10
    c: Coincident(g5,g2)
    c: Coincident(g5,g-4)
    c: Coincident(g6,g7)
    c: Coincident(g7,g8)
    c: Coincident(g8,g9)
    c: Coincident(g9,g6)
    c: Horizontal(g6)
    c: Horizontal(g8)
    c: Vertical(g7)
    c: Vertical(g9)
    c: Distance(g6,g8) = 10
    c: Symmetric(g5,g5,g6)
    c: Coincident(g10,g11)
    c: Coincident(g11,g12)
    c: Coincident(g12,g13)
    c: Coincident(g13,g10)
    c: Vertical(g10)
    c: Vertical(g12)
    c: Horizontal(g11)
    c: Horizontal(g13)
    c: Distance(g11,g13) = 10
    c: Coincident(g10,g5)
    c: Coincident(g14,g15)
    c: Coincident(g15,g16)
    c: Coincident(g16,g17)
    c: Coincident(g17,g14)
    c: Vertical(g14)
    c: Vertical(g16)
    c: Horizontal(g15)
    c: Horizontal(g17)
    c: Distance(g14,g16) = 10
    c: Distance(g15,g17) = 10
    c: Coincident(g14,g0)
    c: Coincident(g18,g1)
    c: Coincident(g18,g15)
    c: Coincident(g19,g20)
    c: Coincident(g20,g21)
    c: Coincident(g21,g22)
    c: Coincident(g22,g19)
    c: Horizontal(g19)
    c: Horizontal(g21)
    c: Vertical(g20)
    c: Vertical(g22)
    c: Distance(g19,g21) = 10
    c: Symmetric(g18,g18,g19)
    c: Coincident(g25,g1)
FEATURE [PartDesign::Pocket] Pocket024
  BaseFeature = -> Pocket023
  Direction = (0,0,-1)
  Length = 5
  Length2 = 5
  Profile = -> Sketch060
  ReferenceAxis = -> Sketch060 [N_Axis]
  Refine = true
  Suppressed = false
  Type = 0
FEATURE [Sketcher::SketchObject] Sketch061
  ArcFitTolerance = 1e-06
  AttachmentSupport = -> [Binder031]
  ExternalGeometry = -> [Binder031]
  FullyConstrained = true
  MakeInternals = false
  MapMode = 5
  Placement = pos=(1.797e-13,87.9131,-50.7566) rot=(1,0,0;1.0472rad)
  sketch-geometry (5):
    g0: Circle CenterX=615 CenterY=-166.026 CenterZ=0 NormalX=0 NormalY=0 NormalZ=1 AngleXU=0 Radius=1.5
    g1: Circle CenterX=615 CenterY=-74.478 CenterZ=0 NormalX=0 NormalY=0 NormalZ=1 AngleXU=0 Radius=1.5
    g2: Circle CenterX=615 CenterY=17.0704 CenterZ=0 NormalX=0 NormalY=0 NormalZ=1 AngleXU=0 Radius=1.5
    g3: Circle CenterX=615 CenterY=113.619 CenterZ=0 NormalX=0 NormalY=0 NormalZ=1 AngleXU=0 Radius=1.5
    g4: Circle CenterX=615 CenterY=200.167 CenterZ=0 NormalX=0 NormalY=0 NormalZ=1 AngleXU=0 Radius=1.5
  constraints (10):
    c: Coincident(g0,g-7)
    c: Equal(g0,g-7)
    c: Coincident(g1,g-6)
    c: Equal(g1,g-6)
    c: Coincident(g2,g-5)
    c: Equal(g2,g-5)
    c: Coincident(g3,g-4)
    c: Equal(g3,g-4)
    c: Coincident(g4,g-3)
    c: Equal(g4,g-3)
FEATURE [PartDesign::Pocket] Pocket025
  BaseFeature = -> Pocket020
  Direction = (1.3e-15,0.866026,-0.5)
  Length = 5
  Length2 = 5
  Profile = -> Sketch061
  ReferenceAxis = -> Sketch061 [N_Axis]
  Refine = true
  Reversed = true
  Suppressed = false
  Type = 0
FEATURE [Sketcher::SketchObject] Sketch062
  ArcFitTolerance = 1e-06
  AttachmentSupport = -> [Pocket024]
  ExternalGeometry = -> [Pocket024]
  FullyConstrained = false
  MakeInternals = false
  MapMode = 5
  Placement = pos=(12.0795,3.87e-14,175.563) rot=(0,1,0;0.068696rad)
  sketch-geometry (16):
    g0: LineSegment [constr] StartX=594.374 StartY=195.023 StartZ=0 EndX=604.374 EndY=195.023 EndZ=0
    g1: LineSegment [constr] StartX=604.374 StartY=195.023 StartZ=0 EndX=604.374 EndY=205.023 EndZ=0
    g2: LineSegment [constr] StartX=604.374 StartY=205.023 StartZ=0 EndX=594.374 EndY=205.023 EndZ=0
    g3: LineSegment [constr] StartX=594.374 StartY=205.023 StartZ=0 EndX=594.374 EndY=195.023 EndZ=0
    g4: LineSegment [constr] StartX=594.374 StartY=349.9 StartZ=0 EndX=594.374 EndY=339.9 EndZ=0
    g5: LineSegment [constr] StartX=594.374 StartY=339.9 StartZ=0 EndX=604.374 EndY=339.9 EndZ=0
    g6: LineSegment [constr] StartX=604.374 StartY=339.9 StartZ=0 EndX=604.374 EndY=349.9 EndZ=0
    g7: LineSegment [constr] StartX=604.374 StartY=349.9 StartZ=0 EndX=594.374 EndY=349.9 EndZ=0
    g8: LineSegment [constr] StartX=604.374 StartY=339.9 StartZ=0 EndX=604.374 EndY=205.023 EndZ=0
    g9: LineSegment [constr] StartX=604.374 StartY=272.462 StartZ=0 EndX=604.374 EndY=282.462 EndZ=0
    g10: LineSegment [constr] StartX=604.374 StartY=282.462 StartZ=0 EndX=594.374 EndY=282.462 EndZ=0
    g11: LineSegment [constr] StartX=594.374 StartY=282.462 StartZ=0 EndX=594.374 EndY=272.462 EndZ=0
    g12: LineSegment [constr] StartX=594.374 StartY=272.462 StartZ=0 EndX=604.374 EndY=272.462 EndZ=0
    g13: Circle CenterX=604.374 CenterY=272.462 CenterZ=0 NormalX=0 NormalY=0 NormalZ=1 AngleXU=0 Radius=1.5
    g14: Circle CenterX=604.374 CenterY=339.9 CenterZ=0 NormalX=0 NormalY=0 NormalZ=1 AngleXU=0 Radius=1.5
    g15: Circle CenterX=604.374 CenterY=205.023 CenterZ=0 NormalX=0 NormalY=0 NormalZ=1 AngleXU=0 Radius=1.5
  constraints (40):
    c: Coincident(g0,g1)
    c: Coincident(g1,g2)
    c: Coincident(g2,g3)
    c: Coincident(g3,g0)
    c: Horizontal(g0)
    c: Horizontal(g2)
    c: Vertical(g1)
    c: Vertical(g3)
    c: Distance(g1,g3) = 10
    c: Distance(g0,g2) = 10
    c: Coincident(g0,g-5)
    c: Coincident(g4,g5)
    c: Coincident(g5,g6)
    c: Coincident(g6,g7)
    c: Coincident(g7,g4)
    c: Vertical(g4)
    c: Vertical(g6)
    c: Horizontal(g5)
    c: Horizontal(g7)
    c: Distance(g4,g6) = 10
    c: Distance(g5,g7) = 10
    c: Coincident(g4,g-6)
    c: Coincident(g8,g5)
    c: Coincident(g8,g1)
    c: Coincident(g9,g10)
    c: Coincident(g10,g11)
    c: Coincident(g11,g12)
    c: Coincident(g12,g9)
    c: Vertical(g9)
    c: Vertical(g11)
    c: Horizontal(g10)
    c: Horizontal(g12)
    c: Distance(g9,g11) = 10
    c: Distance(g10,g12) = 10
    c: Symmetric(g8,g8,g9)
    c: Diameter(g13) = 3
    c: Coincident(g13,g9)
    c: Diameter(g14) = 3
    c: Coincident(g14,g5)
    c: Coincident(g15,g1)
FEATURE [PartDesign::Pocket] Pocket026
  BaseFeature = -> Pocket024
  Direction = (-0.0686421,0,-0.997641)
  Length = 5
  Length2 = 5
  Profile = -> Sketch062
  ReferenceAxis = -> Sketch062 [N_Axis]
  Refine = true
  Suppressed = false
  Type = 0
FEATURE [Sketcher::SketchObject] Sketch063
  ArcFitTolerance = 1e-06
  AttachmentSupport = -> [Binder032]
  ExternalGeometry = -> [Binder032]
  FullyConstrained = false
  MakeInternals = false
  MapMode = 5
  Placement = pos=(0,-0.1,0) rot=(0,0.707107,0.707107;3.14159rad)
  sketch-geometry (8):
    g0: LineSegment [constr] StartX=-627 StartY=-239.145 StartZ=0 EndX=-627 EndY=-203.17 EndZ=0
    g1: LineSegment [constr] StartX=-627 StartY=-203.17 StartZ=0 EndX=-655.447 EndY=-203.17 EndZ=0
    g2: LineSegment [constr] StartX=-878 StartY=-203.17 StartZ=0 EndX=-878 EndY=-225.17 EndZ=0
    g3: LineSegment [constr] StartX=-878 StartY=-203.17 StartZ=0 EndX=-789.259 EndY=-203.17 EndZ=0
    g4: LineSegment StartX=-878 StartY=-225.17 StartZ=0 EndX=-627 EndY=-225.17 EndZ=0
    g5: LineSegment StartX=-878 StartY=-183.17 StartZ=0 EndX=-627 EndY=-183.17 EndZ=0
    g6: LineSegment StartX=-627 StartY=-225.17 StartZ=0 EndX=-627 EndY=-183.17 EndZ=0
    g7: LineSegment StartX=-878 StartY=-183.17 StartZ=0 EndX=-878 EndY=-225.17 EndZ=0
  constraints (17):
    c: Coincident(g3,g2)
    c: DistanceY(g2,g2) = 22
    c: PointOnObject(g2,g-3)
    c: PointOnObject(g3,g-4)
    c: Horizontal(g3)
    c: Vertical(g2)
    c: Coincident(g4,g2)
    c: PointOnObject(g4,g0)
    c: Horizontal(g4)
    c: PointOnObject(g5,g-3)
    c: PointOnObject(g5,g-5)
    c: Horizontal(g5)
    c: Coincident(g6,g4)
    c: Coincident(g6,g5)
    c: Vertical(g6)
    c: Coincident(g7,g5)
    c: Coincident(g7,g2)
FEATURE [PartDesign::Pad] Pad011
  Direction = (0,1,-2e-16)
  Length = 350
  Length2 = 10
  Profile = -> Sketch063
  ReferenceAxis = -> Sketch063 [N_Axis]
  Refine = true
  Suppressed = false
  Type = 0
FEATURE [Sketcher::SketchObject] Sketch064
  ArcFitTolerance = 1e-06
  AttachmentSupport = -> [Pad011]
  ExternalGeometry = -> [Pad011,Binder032]
  FullyConstrained = false
  MakeInternals = false
  MapMode = 5
  Placement = pos=(878,0,0) rot=(0.57735,0.57735,0.57735;2.0944rad)
  sketch-geometry (3):
    g0: LineSegment StartX=-0.1 StartY=-183.17 StartZ=0 EndX=11.464 EndY=-183.17 EndZ=0
    g1: LineSegment StartX=-0.1 StartY=-203.2 StartZ=0 EndX=-0.1 EndY=-183.17 EndZ=0
    g2: LineSegment StartX=-0.1 StartY=-203.2 StartZ=0 EndX=11.464 EndY=-183.17 EndZ=0
  constraints (6):
    c: Coincident(g0,g-3)
    c: PointOnObject(g0,g-3)
    c: Coincident(g1,g-4)
    c: Coincident(g1,g0)
    c: Coincident(g2,g1)
    c: PointOnObject(g2,g0)
FEATURE [PartDesign::Pocket] Pocket027
  BaseFeature = -> Pad011
  Direction = (-1,0,0)
  Length = 5
  Length2 = 5
  Profile = -> Sketch064
  ReferenceAxis = -> Sketch064 [N_Axis]
  Refine = true
  Suppressed = false
  Type = 1
FEATURE [Sketcher::SketchObject] Sketch038
  ArcFitTolerance = 1e-06
  AttachmentSupport = -> [Pocket027]
  ExternalGeometry = -> [Pocket027]
  FullyConstrained = false
  MakeInternals = false
  MapMode = 5
  Placement = pos=(878,0,0) rot=(0.57735,0.57735,0.57735;2.0944rad)
  sketch-geometry (6):
    g0: LineSegment StartX=13.464 StartY=-183.17 StartZ=0 EndX=1.9 EndY=-203.2 EndZ=0
    g1: LineSegment StartX=1.9 StartY=-203.2 StartZ=0 EndX=1.9 EndY=-223.17 EndZ=0
    g2: LineSegment StartX=1.9 StartY=-223.17 StartZ=0 EndX=349.9 EndY=-223.17 EndZ=0
    g3: LineSegment [constr] StartX=1.9 StartY=-203.2 StartZ=0 EndX=-0.1 EndY=-203.2 EndZ=0
    g4: LineSegment StartX=349.9 StartY=-223.17 StartZ=0 EndX=349.9 EndY=-183.17 EndZ=0
    g5: LineSegment StartX=349.9 StartY=-183.17 StartZ=0 EndX=13.464 EndY=-183.17 EndZ=0
  constraints (15):
    c: Coincident(g1,g0)
    c: Vertical(g1)
    c: Coincident(g2,g1)
    c: Horizontal(g2)
    c: Coincident(g3,g0)
    c: Horizontal(g3)
    c: DistanceX(g3,g3) = 2
    c: DistanceX(g-3,g0) = 2
    c: DistanceY(g-4,g1) = 2
    c: Coincident(g4,g2)
    c: Coincident(g4,g-5)
    c: Vertical(g4)
    c: Coincident(g5,g4)
    c: Coincident(g5,g0)
    c: Horizontal(g5)
FEATURE [PartDesign::Pocket] Pocket028
  BaseFeature = -> Pocket027
  Direction = (-1,0,0)
  Length = 5
  Length2 = 5
  Profile = -> Sketch038
  ReferenceAxis = -> Sketch038 [N_Axis]
  Refine = true
  Suppressed = false
  Type = 1
FEATURE [Sketcher::SketchObject] Sketch039
  ArcFitTolerance = 1e-06
  AttachmentSupport = -> [Pocket028]
  ExternalGeometry = -> [Pocket028]
  FullyConstrained = false
  MakeInternals = false
  MapMode = 5
  Placement = pos=(0,0,-223.17) rot=(0,0,1;0rad)
  sketch-geometry (16):
    g0: LineSegment StartX=878 StartY=349.9 StartZ=0 EndX=876 EndY=349.9 EndZ=0
    g1: LineSegment StartX=878 StartY=1.9 StartZ=0 EndX=878 EndY=349.9 EndZ=0
    g2: LineSegment StartX=627 StartY=349.9 StartZ=0 EndX=627 EndY=1.9 EndZ=0
    g3: LineSegment StartX=627 StartY=349.9 StartZ=0 EndX=629 EndY=349.9 EndZ=0
    g4: LineSegment [constr] StartX=627 StartY=1.9 StartZ=0 EndX=629 EndY=1.9 EndZ=0
    g5: LineSegment [constr] StartX=629 StartY=1.9 StartZ=0 EndX=629 EndY=3.9 EndZ=0
    g6: LineSegment [constr] StartX=629 StartY=3.9 StartZ=0 EndX=627 EndY=3.9 EndZ=0
    g7: LineSegment [constr] StartX=627 StartY=3.9 StartZ=0 EndX=627 EndY=1.9 EndZ=0
    g8: LineSegment [constr] StartX=878 StartY=1.9 StartZ=0 EndX=878 EndY=3.9 EndZ=0
    g9: LineSegment [constr] StartX=878 StartY=3.9 StartZ=0 EndX=876 EndY=3.9 EndZ=0
    g10: LineSegment [constr] StartX=876 StartY=3.9 StartZ=0 EndX=876 EndY=1.9 EndZ=0
    g11: LineSegment [constr] StartX=876 StartY=1.9 StartZ=0 EndX=878 EndY=1.9 EndZ=0
    g12: LineSegment StartX=627 StartY=1.9 StartZ=0 EndX=629 EndY=1.9 EndZ=0
    g13: LineSegment StartX=629 StartY=1.9 StartZ=0 EndX=629 EndY=349.9 EndZ=0
    g14: LineSegment StartX=878 StartY=1.9 StartZ=0 EndX=876 EndY=1.9 EndZ=0
    g15: LineSegment StartX=876 StartY=1.9 StartZ=0 EndX=876 EndY=349.9 EndZ=0
  constraints (37):
    c: Distance(g0) = 2
    c: Coincident(g0,g-4)
    c: Horizontal(g0)
    c: Coincident(g1,g-5)
    c: Coincident(g1,g0)
    c: Coincident(g2,g-3)
    c: Distance(g3) = 2
    c: Coincident(g3,g2)
    c: Horizontal(g3)
    c: Coincident(g4,g5)
    c: Coincident(g5,g6)
    c: Coincident(g6,g7)
    c: Coincident(g7,g4)
    c: Horizontal(g4)
    c: Horizontal(g6)
    c: Vertical(g7)
    c: Distance(g4,g6) = 2
    c: Coincident(g8,g9)
    c: Coincident(g9,g10)
    c: Coincident(g10,g11)
    c: Coincident(g11,g8)
    c: Vertical(g8)
    c: Vertical(g10)
    c: Horizontal(g9)
    c: Horizontal(g11)
    c: Distance(g8,g10) = 2
    c: Coincident(g8,g1)
    c: Coincident(g12,g2)
    c: Coincident(g12,g4)
    c: Horizontal(g12)
    c: Coincident(g13,g4)
    c: Coincident(g13,g3)
    c: Vertical(g13)
    c: Coincident(g14,g1)
    c: Coincident(g14,g10)
    c: Coincident(g15,g10)
    c: Coincident(g15,g0)
FEATURE [PartDesign::Pad] Pad034
  BaseFeature = -> Pocket028
  Direction = (0,0,1)
  Length = 20
  Length2 = 10
  Profile = -> Sketch039
  ReferenceAxis = -> Sketch039 [N_Axis]
  Refine = true
  Suppressed = false
  Type = 0
FEATURE [Sketcher::SketchObject] Sketch040
  ArcFitTolerance = 1e-06
  AttachmentSupport = -> [Pad031]
  ExternalGeometry = -> [Pad031]
  FullyConstrained = false
  MakeInternals = false
  MapMode = 5
  Placement = pos=(0,0,0) rot=(0.57735,0.57735,-0.57735;2.0944rad)
  sketch-geometry (32):
    g0: LineSegment [constr] StartX=-140 StartY=0 StartZ=0 EndX=0 EndY=0 EndZ=0
    g1: LineSegment [constr] StartX=-140 StartY=200 StartZ=0 EndX=0 EndY=200 EndZ=0
    g2: LineSegment [constr] StartX=0 StartY=0 StartZ=0 EndX=0 EndY=10 EndZ=0
    g3: LineSegment [constr] StartX=0 StartY=10 StartZ=0 EndX=-10 EndY=10 EndZ=0
    g4: LineSegment [constr] StartX=-10 StartY=10 StartZ=0 EndX=-10 EndY=0 EndZ=0
    g5: LineSegment [constr] StartX=-10 StartY=0 StartZ=0 EndX=0 EndY=0 EndZ=0
    g6: LineSegment [constr] StartX=-140 StartY=0 StartZ=0 EndX=-130 EndY=0 EndZ=0
    g7: LineSegment [constr] StartX=-130 StartY=0 StartZ=0 EndX=-130 EndY=10 EndZ=0
    g8: LineSegment [constr] StartX=-130 StartY=10 StartZ=0 EndX=-140 EndY=10 EndZ=0
    g9: LineSegment [constr] StartX=-140 StartY=10 StartZ=0 EndX=-140 EndY=0 EndZ=0
    g10: LineSegment [constr] StartX=-140 StartY=200 StartZ=0 EndX=-140 EndY=190 EndZ=0
    g11: LineSegment [constr] StartX=-140 StartY=190 StartZ=0 EndX=-130 EndY=190 EndZ=0
    g12: LineSegment [constr] StartX=-130 StartY=190 StartZ=0 EndX=-130 EndY=200 EndZ=0
    g13: LineSegment [constr] StartX=-130 StartY=200 StartZ=0 EndX=-140 EndY=200 EndZ=0
    g14: LineSegment [constr] StartX=0 StartY=200 StartZ=0 EndX=-10 EndY=200 EndZ=0
    g15: LineSegment [constr] StartX=-10 StartY=200 StartZ=0 EndX=-10 EndY=190 EndZ=0
    g16: LineSegment [constr] StartX=-10 StartY=190 StartZ=0 EndX=0 EndY=190 EndZ=0
    g17: LineSegment [constr] StartX=0 StartY=190 StartZ=0 EndX=0 EndY=200 EndZ=0
    g18: LineSegment [constr] StartX=-70 StartY=200 StartZ=0 EndX=-80 EndY=200 EndZ=0
    g19: LineSegment [constr] StartX=-80 StartY=200 StartZ=0 EndX=-80 EndY=190 EndZ=0
    g20: LineSegment [constr] StartX=-80 StartY=190 StartZ=0 EndX=-70 EndY=190 EndZ=0
    g21: LineSegment [constr] StartX=-70 StartY=190 StartZ=0 EndX=-70 EndY=200 EndZ=0
    g22: LineSegment [constr] StartX=-70 StartY=0 StartZ=0 EndX=-70 EndY=10 EndZ=0
    g23: LineSegment [constr] StartX=-70 StartY=10 StartZ=0 EndX=-80 EndY=10 EndZ=0
    g24: LineSegment [constr] StartX=-80 StartY=10 StartZ=0 EndX=-80 EndY=0 EndZ=0
    g25: LineSegment [constr] StartX=-80 StartY=0 StartZ=0 EndX=-70 EndY=0 EndZ=0
    g26: Circle CenterX=-130 CenterY=190 CenterZ=0 NormalX=0 NormalY=0 NormalZ=1 AngleXU=0 Radius=1.5
    g27: Circle CenterX=-70 CenterY=190 CenterZ=0 NormalX=0 NormalY=0 NormalZ=1 AngleXU=0 Radius=1.5
    g28: Circle CenterX=-10 CenterY=190 CenterZ=0 NormalX=0 NormalY=0 NormalZ=1 AngleXU=0 Radius=1.5
    g29: Circle CenterX=-10 CenterY=10 CenterZ=0 NormalX=0 NormalY=0 NormalZ=1 AngleXU=0 Radius=1.5
    g30: Circle CenterX=-70 CenterY=10 CenterZ=0 NormalX=0 NormalY=0 NormalZ=1 AngleXU=0 Radius=1.5
    g31: Circle CenterX=-130 CenterY=10 CenterZ=0 NormalX=0 NormalY=0 NormalZ=1 AngleXU=0 Radius=1.5
  constraints (71):
    c: Coincident(g0,g-5)
    c: Coincident(g0,g-1)
    c: Coincident(g1,g-4)
    c: Coincident(g1,g-3)
    c: Coincident(g2,g3)
    c: Coincident(g3,g4)
    c: Coincident(g4,g5)
    c: Coincident(g5,g2)
    c: Vertical(g2)
    c: Vertical(g4)
    c: Horizontal(g3)
    c: Horizontal(g5)
    c: Distance(g2,g4) = 10
    c: Distance(g3,g5) = 10
    c: Coincident(g2,g0)
    c: Coincident(g6,g7)
    c: Coincident(g7,g8)
    c: Coincident(g8,g9)
    c: Coincident(g9,g6)
    c: Horizontal(g6)
    c: Horizontal(g8)
    c: Vertical(g7)
    c: Vertical(g9)
    c: Distance(g7,g9) = 10
    c: Distance(g6,g8) = 10
    c: Coincident(g6,g0)
    c: Coincident(g10,g11)
    c: Coincident(g11,g12)
    c: Coincident(g12,g13)
    c: Coincident(g13,g10)
    c: Vertical(g10)
    c: Vertical(g12)
    c: Horizontal(g11)
    c: Horizontal(g13)
    c: Distance(g10,g12) = 10
    c: Distance(g11,g13) = 10
    c: Coincident(g10,g1)
    c: Coincident(g14,g15)
    c: Coincident(g15,g16)
    c: Coincident(g16,g17)
    c: Coincident(g17,g14)
    c: Horizontal(g14)
    c: Horizontal(g16)
    c: Vertical(g15)
    c: Vertical(g17)
    c: Distance(g15,g17) = 10
    c: Distance(g14,g16) = 10
    c: Coincident(g14,g1)
    c: Coincident(g18,g19)
    c: Coincident(g19,g20)
    c: Coincident(g20,g21)
    c: Coincident(g21,g18)
    c: Horizontal(g18)
    c: Horizontal(g20)
    c: Vertical(g19)
    c: Vertical(g21)
    c: Distance(g19,g21) = 10
    c: Distance(g18,g20) = 10
    c: Symmetric(g1,g1,g18)
    c: Coincident(g22,g23)
    c: Coincident(g23,g24)
    c: Coincident(g24,g25)
    c: Coincident(g25,g22)
    c: Vertical(g22)
    c: Vertical(g24)
    c: Horizontal(g23)
    c: Horizontal(g25)
    c: Distance(g22,g24) = 10
    c: Distance(g23,g25) = 10
    c: Symmetric(g0,g0,g22)
    c: Coincident(g26,g11)
FEATURE [PartDesign::Pocket] Pocket016
  BaseFeature = -> Pad031
  Direction = (0,1,0)
  Length = 5
  Length2 = 5
  Placement = pos=(0,0,0) rot=(1,1,1;2.0944rad)
  Profile = -> Sketch040
  ReferenceAxis = -> Sketch040 [N_Axis]
  Refine = true
  Suppressed = false
  Type = 0
FEATURE [Sketcher::SketchObject] Sketch065
  ArcFitTolerance = 1e-06
  AttachmentSupport = -> [Binder012]
  ExternalGeometry = -> [Binder012]
  FullyConstrained = true
  MakeInternals = false
  MapMode = 5
  Placement = pos=(0,-0.1,0) rot=(0,0.707107,0.707107;3.14159rad)
  sketch-geometry (8):
    g0: LineSegment StartX=278 StartY=-343.2 StartZ=0 EndX=278 EndY=107.924 EndZ=0
    g1: LineSegment StartX=278 StartY=107.924 StartZ=0 EndX=300 EndY=105.09 EndZ=0
    g2: LineSegment StartX=300 StartY=-343.2 StartZ=0 EndX=278 EndY=-343.2 EndZ=0
    g3: LineSegment StartX=300 StartY=-343.2 StartZ=0 EndX=300 EndY=-341.2 EndZ=0
    g4: LineSegment StartX=300 StartY=-341.2 StartZ=0 EndX=280 EndY=-341.2 EndZ=0
    g5: LineSegment StartX=280 StartY=-341.2 StartZ=0 EndX=280 EndY=105.924 EndZ=0
    g6: LineSegment StartX=300 StartY=105.09 StartZ=0 EndX=300 EndY=103.09 EndZ=0
    g7: LineSegment StartX=300 StartY=103.09 StartZ=0 EndX=280 EndY=105.924 EndZ=0
  constraints (22):
    c: PointOnObject(g0,g-4)
    c: Vertical(g0)
    c: Coincident(g1,g0)
    c: Coincident(g1,g-4)
    c: Distance(g2) = 22
    c: Coincident(g2,g-3)
    c: Horizontal(g2)
    c: Coincident(g0,g2)
    c: Distance(g3) = 2
    c: Coincident(g3,g2)
    c: Vertical(g3)
    c: Distance(g4) = 20
    c: Coincident(g4,g3)
    c: Horizontal(g4)
    c: Coincident(g5,g4)
    c: Vertical(g5)
    c: Coincident(g6,g1)
    c: Vertical(g6)
    c: Coincident(g7,g6)
    c: Coincident(g7,g5)
    c: DistanceY(g6,g6) = 2
    c: DistanceY(g5,g0) = 2
FEATURE [PartDesign::Pad] Pad013
  Direction = (0,1,-2e-16)
  Length = 350
  Length2 = 10
  Profile = -> Sketch065
  ReferenceAxis = -> Sketch065 [N_Axis]
  Refine = true
  Suppressed = false
  Type = 0
FEATURE [Sketcher::SketchObject] Sketch066
  ArcFitTolerance = 1e-06
  AttachmentSupport = -> [Pad013]
  ExternalGeometry = -> [Binder012,Pad013]
  FullyConstrained = true
  MakeInternals = false
  MapMode = 5
  Placement = pos=(-280,0,0) rot=(0.57735,-0.57735,-0.57735;2.0944rad)
  sketch-geometry (3):
    g0: LineSegment StartX=0.1 StartY=-203.2 StartZ=0 EndX=-179.527 EndY=107.924 EndZ=0
    g1: LineSegment StartX=0.1 StartY=107.924 StartZ=0 EndX=-179.527 EndY=107.924 EndZ=0
    g2: LineSegment StartX=0.1 StartY=107.924 StartZ=0 EndX=0.1 EndY=-203.2 EndZ=0
  constraints (7):
    c: PointOnObject(g-5,g0)
    c: Coincident(g0,g-3)
    c: Coincident(g1,g-4)
    c: Coincident(g2,g1)
    c: Coincident(g2,g0)
    c: PointOnObject(g0,g-4)
    c: Coincident(g1,g0)
FEATURE [PartDesign::Pocket] Pocket029
  BaseFeature = -> Pad013
  Direction = (1,0,0)
  Length = 5
  Length2 = 5
  Midplane = true
  Profile = -> Sketch066
  ReferenceAxis = -> Sketch066 [N_Axis]
  Refine = true
  Suppressed = false
  Type = 1
FEATURE [Sketcher::SketchObject] Sketch067
  ArcFitTolerance = 1e-06
  AttachmentSupport = -> [Pocket029]
  ExternalGeometry = -> [Pocket029]
  FullyConstrained = true
  MakeInternals = false
  MapMode = 5
  Placement = pos=(-280,0,0) rot=(0.57735,-0.57735,-0.57735;2.0944rad)
  sketch-geometry (7):
    g0: LineSegment StartX=-176.737 StartY=103.09 StartZ=0 EndX=0.1 EndY=-203.2 EndZ=0
    g1: LineSegment StartX=0.1 StartY=-203.2 StartZ=0 EndX=0.1 EndY=-341.2 EndZ=0
    g2: LineSegment StartX=0.1 StartY=-341.2 StartZ=0 EndX=-1.9 EndY=-341.2 EndZ=0
    g3: LineSegment StartX=-1.9 StartY=-341.2 StartZ=0 EndX=-1.9 EndY=-203.2 EndZ=0
    g4: LineSegment StartX=-1.9 StartY=-203.2 StartZ=0 EndX=-178.737 EndY=103.09 EndZ=0
    g5: LineSegment StartX=-178.737 StartY=103.09 StartZ=0 EndX=-176.737 EndY=103.09 EndZ=0
    g6: LineSegment [constr] StartX=-1.9 StartY=-203.2 StartZ=0 EndX=0.1 EndY=-203.2 EndZ=0
  constraints (17):
    c: Coincident(g0,g-3)
    c: Coincident(g0,g-5)
    c: Coincident(g1,g0)
    c: Coincident(g1,g-4)
    c: Distance(g2) = 2
    c: Coincident(g2,g1)
    c: Horizontal(g2)
    c: Coincident(g3,g2)
    c: Vertical(g3)
    c: Coincident(g4,g3)
    c: PointOnObject(g4,g-3)
    c: Coincident(g5,g4)
    c: Coincident(g5,g0)
    c: DistanceX(g5,g5) = 2
    c: Coincident(g6,g3)
    c: Coincident(g6,g0)
    c: Horizontal(g6)
FEATURE [PartDesign::Pad] Pad035
  BaseFeature = -> Pocket029
  Direction = (-1,0,0)
  Length = 20
  Length2 = 10
  Profile = -> Sketch067
  ReferenceAxis = -> Sketch067 [N_Axis]
  Refine = true
  Suppressed = false
  Type = 0
FEATURE [Sketcher::SketchObject] Sketch068
  ArcFitTolerance = 1e-06
  AttachmentSupport = -> [Binder013]
  ExternalGeometry = -> [Binder013]
  FullyConstrained = true
  MakeInternals = false
  MapMode = 5
  Placement = pos=(0,-0.1,0) rot=(0,0.707107,0.707107;3.14159rad)
  sketch-geometry (9):
    g0: LineSegment StartX=100 StartY=-343.2 StartZ=0 EndX=100 EndY=-341.2 EndZ=0
    g1: LineSegment StartX=100 StartY=-341.2 StartZ=0 EndX=120 EndY=-341.2 EndZ=0
    g2: LineSegment StartX=120 StartY=-341.2 StartZ=0 EndX=120 EndY=122.94 EndZ=0
    g3: LineSegment StartX=100 StartY=-343.2 StartZ=0 EndX=122 EndY=-343.2 EndZ=0
    g4: LineSegment StartX=122 StartY=-343.2 StartZ=0 EndX=122 EndY=124.94 EndZ=0
    g5: LineSegment [constr] StartX=100 StartY=-341.2 StartZ=0 EndX=100 EndY=126.907 EndZ=0
    g6: LineSegment StartX=122 StartY=124.94 StartZ=0 EndX=100 EndY=126.907 EndZ=0
    g7: LineSegment StartX=100 StartY=126.907 StartZ=0 EndX=100 EndY=124.907 EndZ=0
    g8: LineSegment StartX=100 StartY=124.907 StartZ=0 EndX=120 EndY=122.94 EndZ=0
  constraints (25):
    c: Distance(g0) = 2
    c: Coincident(g0,g-3)
    c: Vertical(g0)
    c: Distance(g1) = 20
    c: Coincident(g1,g0)
    c: Horizontal(g1)
    c: Coincident(g2,g1)
    c: Vertical(g2)
    c: Distance(g3) = 22
    c: Coincident(g3,g0)
    c: Horizontal(g3)
    c: Coincident(g4,g3)
    c: PointOnObject(g4,g-4)
    c: Vertical(g4)
    c: Coincident(g5,g0)
    c: PointOnObject(g5,g-4)
    c: Vertical(g5)
    c: Coincident(g6,g4)
    c: Coincident(g6,g5)
    c: Distance(g7) = 2
    c: Coincident(g7,g5)
    c: PointOnObject(g7,g5)
    c: Coincident(g8,g7)
    c: Coincident(g2,g8)
    c: DistanceY(g2,g4) = 2
FEATURE [PartDesign::Pad] Pad015
  Direction = (0,1,-2e-16)
  Length = 350
  Length2 = 10
  Profile = -> Sketch068
  ReferenceAxis = -> Sketch068 [N_Axis]
  Refine = true
  Suppressed = false
  Type = 0
FEATURE [Sketcher::SketchObject] Sketch069
  ArcFitTolerance = 1e-06
  AttachmentSupport = -> [Pad015]
  ExternalGeometry = -> [Pad015]
  FullyConstrained = false
  MakeInternals = false
  MapMode = 5
  Placement = pos=(-120,0,0) rot=(0.57735,0.57735,0.57735;2.0944rad)
  sketch-geometry (3):
    g0: LineSegment StartX=-0.1 StartY=-203.2 StartZ=0 EndX=190.488 EndY=126.907 EndZ=0
    g1: LineSegment StartX=-0.1 StartY=126.907 StartZ=0 EndX=190.488 EndY=126.907 EndZ=0
    g2: LineSegment StartX=-0.1 StartY=126.907 StartZ=0 EndX=-0.1 EndY=-203.2 EndZ=0
  constraints (6):
    c: Coincident(g0,g-3)
    c: PointOnObject(g-3,g0)
    c: Coincident(g1,g-4)
    c: Coincident(g2,g1)
    c: Coincident(g2,g0)
    c: Coincident(g0,g1)
FEATURE [PartDesign::Pocket] Pocket030
  BaseFeature = -> Pad015
  Direction = (-1,0,0)
  Length = 5
  Length2 = 5
  Midplane = true
  Profile = -> Sketch069
  ReferenceAxis = -> Sketch069 [N_Axis]
  Refine = true
  Suppressed = false
  Type = 1
FEATURE [Sketcher::SketchObject] Sketch070
  ArcFitTolerance = 1e-06
  AttachmentSupport = -> [Pocket030]
  ExternalGeometry = -> [Pocket030]
  FullyConstrained = true
  MakeInternals = false
  MapMode = 5
  Placement = pos=(-120,0,0) rot=(0.57735,0.57735,0.57735;2.0944rad)
  sketch-geometry (7):
    g0: LineSegment StartX=188.197 StartY=122.94 StartZ=0 EndX=190.197 EndY=122.94 EndZ=0
    g1: LineSegment StartX=188.197 StartY=122.94 StartZ=0 EndX=-0.1 EndY=-203.2 EndZ=0
    g2: LineSegment StartX=-0.1 StartY=-203.2 StartZ=0 EndX=-0.1 EndY=-341.2 EndZ=0
    g3: LineSegment StartX=-0.1 StartY=-341.2 StartZ=0 EndX=1.9 EndY=-341.2 EndZ=0
    g4: LineSegment StartX=1.9 StartY=-341.2 StartZ=0 EndX=1.9 EndY=-203.2 EndZ=0
    g5: LineSegment StartX=1.9 StartY=-203.2 StartZ=0 EndX=190.197 EndY=122.94 EndZ=0
    g6: LineSegment [constr] StartX=-0.1 StartY=-203.2 StartZ=0 EndX=1.9 EndY=-203.2 EndZ=0
  constraints (17):
    c: Distance(g0) = 2
    c: Coincident(g0,g-7)
    c: PointOnObject(g0,g-7)
    c: Coincident(g1,g0)
    c: Coincident(g1,g-4)
    c: Coincident(g2,g1)
    c: Coincident(g2,g-4)
    c: Distance(g3) = 2
    c: Coincident(g3,g2)
    c: Horizontal(g3)
    c: Coincident(g4,g3)
    c: Vertical(g4)
    c: Coincident(g5,g4)
    c: Coincident(g5,g0)
    c: Coincident(g6,g1)
    c: Coincident(g6,g4)
    c: Horizontal(g6)
FEATURE [PartDesign::Pad] Pad036
  BaseFeature = -> Pocket030
  Direction = (1,0,0)
  Length = 20
  Length2 = 10
  Profile = -> Sketch070
  ReferenceAxis = -> Sketch070 [N_Axis]
  Refine = true
  Suppressed = false
  Type = 0
FEATURE [Sketcher::SketchObject] Sketch071
  ArcFitTolerance = 1e-06
  AttachmentSupport = -> [Pad035]
  ExternalGeometry = -> [Pad035]
  FullyConstrained = false
  MakeInternals = false
  MapMode = 5
  Placement = pos=(0,-7.51e-14,-341.2) rot=(0,0,1;0rad)
  sketch-geometry (28):
    g0: LineSegment [constr] StartX=-300 StartY=1.9 StartZ=0 EndX=-290 EndY=1.9 EndZ=0
    g1: LineSegment [constr] StartX=-290 StartY=1.9 StartZ=0 EndX=-290 EndY=11.9 EndZ=0
    g2: LineSegment [constr] StartX=-290 StartY=11.9 StartZ=0 EndX=-300 EndY=11.9 EndZ=0
    g3: LineSegment [constr] StartX=-300 StartY=11.9 StartZ=0 EndX=-300 EndY=1.9 EndZ=0
    g4: LineSegment [constr] StartX=-300 StartY=1.9 StartZ=0 EndX=-300 EndY=349.9 EndZ=0
    g5: LineSegment [constr] StartX=-300 StartY=349.9 StartZ=0 EndX=-300 EndY=339.9 EndZ=0
    g6: LineSegment [constr] StartX=-300 StartY=339.9 StartZ=0 EndX=-290 EndY=339.9 EndZ=0
    g7: LineSegment [constr] StartX=-290 StartY=339.9 StartZ=0 EndX=-290 EndY=349.9 EndZ=0
    g8: LineSegment [constr] StartX=-290 StartY=349.9 StartZ=0 EndX=-300 EndY=349.9 EndZ=0
    g9: LineSegment [constr] StartX=-300 StartY=175.9 StartZ=0 EndX=-290 EndY=175.9 EndZ=0
    g10: LineSegment [constr] StartX=-290 StartY=175.9 StartZ=0 EndX=-290 EndY=185.9 EndZ=0
    g11: LineSegment [constr] StartX=-290 StartY=185.9 StartZ=0 EndX=-300 EndY=185.9 EndZ=0
    g12: LineSegment [constr] StartX=-300 StartY=185.9 StartZ=0 EndX=-300 EndY=175.9 EndZ=0
    g13: LineSegment [constr] StartX=-290 StartY=339.9 StartZ=0 EndX=-290 EndY=185.9 EndZ=0
    g14: LineSegment [constr] StartX=-290 StartY=11.9 StartZ=0 EndX=-290 EndY=175.9 EndZ=0
    g15: LineSegment [constr] StartX=-290 StartY=93.9 StartZ=0 EndX=-290 EndY=103.9 EndZ=0
    g16: LineSegment [constr] StartX=-290 StartY=103.9 StartZ=0 EndX=-300 EndY=103.9 EndZ=0
    g17: LineSegment [constr] StartX=-300 StartY=103.9 StartZ=0 EndX=-300 EndY=93.9 EndZ=0
    g18: LineSegment [constr] StartX=-300 StartY=93.9 StartZ=0 EndX=-290 EndY=93.9 EndZ=0
    g19: LineSegment [constr] StartX=-290 StartY=262.9 StartZ=0 EndX=-290 EndY=272.9 EndZ=0
    g20: LineSegment [constr] StartX=-290 StartY=272.9 StartZ=0 EndX=-300 EndY=272.9 EndZ=0
    g21: LineSegment [constr] StartX=-300 StartY=272.9 StartZ=0 EndX=-300 EndY=262.9 EndZ=0
    g22: LineSegment [constr] StartX=-300 StartY=262.9 StartZ=0 EndX=-290 EndY=262.9 EndZ=0
    g23: Circle CenterX=-290 CenterY=339.9 CenterZ=0 NormalX=0 NormalY=0 NormalZ=1 AngleXU=0 Radius=1.5
    g24: Circle CenterX=-290 CenterY=262.9 CenterZ=0 NormalX=0 NormalY=0 NormalZ=1 AngleXU=0 Radius=1.5
    g25: Circle CenterX=-290 CenterY=175.9 CenterZ=0 NormalX=0 NormalY=0 NormalZ=1 AngleXU=0 Radius=1.5
    g26: Circle CenterX=-290 CenterY=93.9 CenterZ=0 NormalX=0 NormalY=0 NormalZ=1 AngleXU=0 Radius=1.5
    g27: Circle CenterX=-290 CenterY=11.9 CenterZ=0 NormalX=0 NormalY=0 NormalZ=1 AngleXU=0 Radius=1.5
  constraints (61):
    c: Coincident(g0,g1)
    c: Coincident(g1,g2)
    c: Coincident(g2,g3)
    c: Coincident(g3,g0)
    c: Horizontal(g0)
    c: Horizontal(g2)
    c: Vertical(g1)
    c: Vertical(g3)
    c: Distance(g1,g3) = 10
    c: Distance(g0,g2) = 10
    c: Coincident(g0,g-4)
    c: Coincident(g4,g0)
    c: Coincident(g4,g-3)
    c: Coincident(g5,g6)
    c: Coincident(g6,g7)
    c: Coincident(g7,g8)
    c: Coincident(g8,g5)
    c: Vertical(g5)
    c: Vertical(g7)
    c: Horizontal(g6)
    c: Horizontal(g8)
    c: Distance(g5,g7) = 10
    c: Distance(g6,g8) = 10
    c: Coincident(g5,g4)
    c: Coincident(g9,g10)
    c: Coincident(g10,g11)
    c: Coincident(g11,g12)
    c: Coincident(g12,g9)
    c: Horizontal(g9)
    c: Horizontal(g11)
    c: Vertical(g10)
    c: Vertical(g12)
    c: Distance(g10,g12) = 10
    c: Distance(g9,g11) = 10
    c: Symmetric(g4,g4,g9)
    c: Coincident(g13,g6)
    c: Coincident(g13,g10)
    c: Coincident(g14,g1)
    c: Coincident(g14,g9)
    c: Coincident(g15,g16)
    c: Coincident(g16,g17)
    c: Coincident(g17,g18)
    c: Coincident(g18,g15)
    c: Vertical(g15)
    c: Vertical(g17)
    c: Horizontal(g16)
    c: Horizontal(g18)
    c: Distance(g16,g18) = 10
    c: Symmetric(g14,g14,g15)
    c: PointOnObject(g16,g4)
    c: Coincident(g19,g20)
    c: Coincident(g20,g21)
    c: Coincident(g21,g22)
    c: Coincident(g22,g19)
    c: Vertical(g19)
    c: Vertical(g21)
    c: Horizontal(g20)
    c: Horizontal(g22)
    c: Distance(g20,g22) = 10
    c: Symmetric(g13,g13,g19)
    c: Coincident(g23,g6)
FEATURE [PartDesign::Pocket] Pocket031
  BaseFeature = -> Pad035
  Direction = (0,0,-1)
  Length = 5
  Length2 = 5
  Profile = -> Sketch071
  ReferenceAxis = -> Sketch071 [N_Axis]
  Refine = true
  Suppressed = false
  Type = 0
FEATURE [Sketcher::SketchObject] Sketch072
  ArcFitTolerance = 1e-06
  AttachmentSupport = -> [Pocket031]
  ExternalGeometry = -> [Pocket031]
  FullyConstrained = true
  MakeInternals = false
  MapMode = 5
  Placement = pos=(-20.2233,3.17e-14,142.731) rot=(0.997525,0,0.070317;3.14159rad)
  sketch-geometry (16):
    g0: LineSegment [constr] StartX=-282.571 StartY=-349.9 StartZ=0 EndX=-272.571 EndY=-349.9 EndZ=0
    g1: LineSegment [constr] StartX=-272.571 StartY=-349.9 StartZ=0 EndX=-272.571 EndY=-339.9 EndZ=0
    g2: LineSegment [constr] StartX=-272.571 StartY=-339.9 StartZ=0 EndX=-282.571 EndY=-339.9 EndZ=0
    g3: LineSegment [constr] StartX=-282.571 StartY=-339.9 StartZ=0 EndX=-282.571 EndY=-349.9 EndZ=0
    g4: LineSegment [constr] StartX=-282.571 StartY=-349.9 StartZ=0 EndX=-282.571 EndY=-176.737 EndZ=0
    g5: LineSegment [constr] StartX=-282.571 StartY=-176.737 StartZ=0 EndX=-282.571 EndY=-186.737 EndZ=0
    g6: LineSegment [constr] StartX=-282.571 StartY=-186.737 StartZ=0 EndX=-272.571 EndY=-186.737 EndZ=0
    g7: LineSegment [constr] StartX=-272.571 StartY=-186.737 StartZ=0 EndX=-272.571 EndY=-176.737 EndZ=0
    g8: LineSegment [constr] StartX=-272.571 StartY=-176.737 StartZ=0 EndX=-282.571 EndY=-176.737 EndZ=0
    g9: LineSegment [constr] StartX=-282.571 StartY=-263.318 StartZ=0 EndX=-272.571 EndY=-263.318 EndZ=0
    g10: LineSegment [constr] StartX=-272.571 StartY=-263.318 StartZ=0 EndX=-272.571 EndY=-253.318 EndZ=0
    g11: LineSegment [constr] StartX=-272.571 StartY=-253.318 StartZ=0 EndX=-282.571 EndY=-253.318 EndZ=0
    g12: LineSegment [constr] StartX=-282.571 StartY=-253.318 StartZ=0 EndX=-282.571 EndY=-263.318 EndZ=0
    g13: Circle CenterX=-272.571 CenterY=-263.318 CenterZ=0 NormalX=0 NormalY=0 NormalZ=1 AngleXU=0 Radius=1.5
    g14: Circle CenterX=-272.571 CenterY=-186.737 CenterZ=0 NormalX=0 NormalY=0 NormalZ=1 AngleXU=0 Radius=1.5
    g15: Circle CenterX=-272.571 CenterY=-339.9 CenterZ=0 NormalX=0 NormalY=0 NormalZ=1 AngleXU=0 Radius=1.5
  constraints (41):
    c: Coincident(g0,g1)
    c: Coincident(g1,g2)
    c: Coincident(g2,g3)
    c: Coincident(g3,g0)
    c: Horizontal(g0)
    c: Horizontal(g2)
    c: Vertical(g1)
    c: Vertical(g3)
    c: Distance(g1,g3) = 10
    c: Distance(g0,g2) = 10
    c: Coincident(g0,g-3)
    c: Coincident(g4,g0)
    c: Coincident(g4,g-5)
    c: Coincident(g5,g6)
    c: Coincident(g6,g7)
    c: Coincident(g7,g8)
    c: Coincident(g8,g5)
    c: Vertical(g5)
    c: Vertical(g7)
    c: Horizontal(g6)
    c: Horizontal(g8)
    c: Distance(g5,g7) = 10
    c: Distance(g6,g8) = 10
    c: Coincident(g5,g4)
    c: Coincident(g9,g10)
    c: Coincident(g10,g11)
    c: Coincident(g11,g12)
    c: Coincident(g12,g9)
    c: Horizontal(g9)
    c: Horizontal(g11)
    c: Vertical(g10)
    c: Vertical(g12)
    c: Distance(g10,g12) = 10
    c: Distance(g9,g11) = 10
    c: Symmetric(g4,g4,g9)
    c: Diameter(g13) = 3
    c: Coincident(g13,g9)
    c: Diameter(g14) = 3
    c: Coincident(g14,g6)
    c: Diameter(g15) = 3
    c: Coincident(g15,g1)
FEATURE [PartDesign::Pocket] Pocket032
  BaseFeature = -> Pocket031
  Direction = (-0.140287,0,0.990111)
  Length = 5
  Length2 = 5
  Profile = -> Sketch072
  ReferenceAxis = -> Sketch072 [N_Axis]
  Refine = true
  Suppressed = false
  Type = 0
FEATURE [Sketcher::SketchObject] Sketch073
  ArcFitTolerance = 1e-06
  AttachmentSupport = -> [Pocket032]
  ExternalGeometry = -> [Pocket032]
  FullyConstrained = false
  MakeInternals = false
  MapMode = 5
  Placement = pos=(4.659e-13,87.9132,-50.7567) rot=(1,0,0;1.0472rad)
  sketch-geometry (28):
    g0: LineSegment [constr] StartX=-300 StartY=-176.026 StartZ=0 EndX=-300 EndY=177.647 EndZ=0
    g1: LineSegment [constr] StartX=-300 StartY=-176.026 StartZ=0 EndX=-290 EndY=-176.026 EndZ=0
    g2: LineSegment [constr] StartX=-290 StartY=-176.026 StartZ=0 EndX=-290 EndY=-166.026 EndZ=0
    g3: LineSegment [constr] StartX=-290 StartY=-166.026 StartZ=0 EndX=-300 EndY=-166.026 EndZ=0
    g4: LineSegment [constr] StartX=-300 StartY=-166.026 StartZ=0 EndX=-300 EndY=-176.026 EndZ=0
    g5: LineSegment [constr] StartX=-300 StartY=177.647 StartZ=0 EndX=-300 EndY=167.647 EndZ=0
    g6: LineSegment [constr] StartX=-300 StartY=167.647 StartZ=0 EndX=-290 EndY=167.647 EndZ=0
    g7: LineSegment [constr] StartX=-290 StartY=167.647 StartZ=0 EndX=-290 EndY=177.647 EndZ=0
    g8: LineSegment [constr] StartX=-290 StartY=177.647 StartZ=0 EndX=-300 EndY=177.647 EndZ=0
    g9: LineSegment [constr] StartX=-300 StartY=0.810216 StartZ=0 EndX=-290 EndY=0.810216 EndZ=0
    g10: LineSegment [constr] StartX=-290 StartY=0.810216 StartZ=0 EndX=-290 EndY=10.8102 EndZ=0
    g11: LineSegment [constr] StartX=-290 StartY=10.8102 StartZ=0 EndX=-300 EndY=10.8102 EndZ=0
    g12: LineSegment [constr] StartX=-300 StartY=10.8102 StartZ=0 EndX=-300 EndY=0.810216 EndZ=0
    g13: LineSegment [constr] StartX=-290 StartY=167.647 StartZ=0 EndX=-290 EndY=10.8102 EndZ=0
    g14: LineSegment [constr] StartX=-290 StartY=0.810216 StartZ=0 EndX=-290 EndY=-166.026 EndZ=0
    g15: LineSegment [constr] StartX=-290 StartY=-82.6081 StartZ=0 EndX=-290 EndY=-72.6081 EndZ=0
    g16: LineSegment [constr] StartX=-290 StartY=-72.6081 StartZ=0 EndX=-300 EndY=-72.6081 EndZ=0
    g17: LineSegment [constr] StartX=-300 StartY=-72.6081 StartZ=0 EndX=-300 EndY=-82.6081 EndZ=0
    g18: LineSegment [constr] StartX=-300 StartY=-82.6081 StartZ=0 EndX=-290 EndY=-82.6081 EndZ=0
    g19: LineSegment [constr] StartX=-290 StartY=89.2285 StartZ=0 EndX=-290 EndY=99.2285 EndZ=0
    g20: LineSegment [constr] StartX=-290 StartY=99.2285 StartZ=0 EndX=-300 EndY=99.2285 EndZ=0
    g21: LineSegment [constr] StartX=-300 StartY=99.2285 StartZ=0 EndX=-300 EndY=89.2285 EndZ=0
    g22: LineSegment [constr] StartX=-300 StartY=89.2285 StartZ=0 EndX=-290 EndY=89.2285 EndZ=0
    g23: Circle CenterX=-290 CenterY=167.647 CenterZ=0 NormalX=0 NormalY=0 NormalZ=1 AngleXU=0 Radius=1.5
    g24: Circle CenterX=-290 CenterY=89.2285 CenterZ=0 NormalX=0 NormalY=0 NormalZ=1 AngleXU=0 Radius=1.5
    g25: Circle CenterX=-290 CenterY=0.810216 CenterZ=0 NormalX=0 NormalY=0 NormalZ=1 AngleXU=0 Radius=1.5
    g26: Circle CenterX=-290 CenterY=-82.6081 CenterZ=0 NormalX=0 NormalY=0 NormalZ=1 AngleXU=0 Radius=1.5
    g27: Circle CenterX=-290 CenterY=-166.026 CenterZ=0 NormalX=0 NormalY=0 NormalZ=1 AngleXU=0 Radius=1.5
  constraints (62):
    c: Coincident(g0,g-3)
    c: Coincident(g0,g-4)
    c: Coincident(g1,g2)
    c: Coincident(g2,g3)
    c: Coincident(g3,g4)
    c: Coincident(g4,g1)
    c: Horizontal(g1)
    c: Horizontal(g3)
    c: Vertical(g2)
    c: Vertical(g4)
    c: Distance(g2,g4) = 10
    c: Distance(g1,g3) = 10
    c: Coincident(g1,g0)
    c: Coincident(g5,g6)
    c: Coincident(g6,g7)
    c: Coincident(g7,g8)
    c: Coincident(g8,g5)
    c: Vertical(g5)
    c: Vertical(g7)
    c: Horizontal(g6)
    c: Horizontal(g8)
    c: Distance(g5,g7) = 10
    c: Distance(g6,g8) = 10
    c: Coincident(g5,g0)
    c: Coincident(g9,g10)
    c: Coincident(g10,g11)
    c: Coincident(g11,g12)
    c: Coincident(g12,g9)
    c: Horizontal(g9)
    c: Horizontal(g11)
    c: Vertical(g10)
    c: Vertical(g12)
    c: Distance(g10,g12) = 10
    c: Distance(g9,g11) = 10
    c: Symmetric(g0,g0,g9)
    c: Coincident(g13,g6)
    c: Coincident(g13,g10)
    c: Coincident(g14,g9)
    c: Coincident(g14,g2)
    c: Coincident(g15,g16)
    c: Coincident(g16,g17)
    c: Coincident(g17,g18)
    c: Coincident(g18,g15)
    c: Vertical(g15)
    c: Vertical(g17)
    c: Horizontal(g16)
    c: Horizontal(g18)
    c: Distance(g16,g18) = 10
    c: Symmetric(g14,g14,g15)
    c: PointOnObject(g16,g0)
    c: Coincident(g19,g20)
    c: Coincident(g20,g21)
    c: Coincident(g21,g22)
    c: Coincident(g22,g19)
    c: Vertical(g19)
    c: Vertical(g21)
    c: Horizontal(g20)
    c: Horizontal(g22)
    c: Distance(g20,g22) = 10
    c: Symmetric(g13,g13,g19)
    c: PointOnObject(g20,g0)
    c: Coincident(g23,g6)
FEATURE [PartDesign::Pocket] Pocket033
  BaseFeature = -> Pocket032
  Direction = (4.6e-15,0.866025,-0.5)
  Length = 5
  Length2 = 5
  Profile = -> Sketch073
  ReferenceAxis = -> Sketch073 [N_Axis]
  Refine = true
  Suppressed = false
  Type = 0
FEATURE [Sketcher::SketchObject] Sketch074
  ArcFitTolerance = 1e-06
  AttachmentSupport = -> [Pocket033]
  ExternalGeometry = -> [Binder012]
  FullyConstrained = true
  MakeInternals = false
  MapMode = 5
  Placement = pos=(0,1.9,0) rot=(0,0.707107,0.707107;3.14159rad)
  sketch-geometry (3):
    g0: Circle CenterX=290 CenterY=-213.2 CenterZ=0 NormalX=0 NormalY=0 NormalZ=1 AngleXU=0 Radius=1.5
    g1: Circle CenterX=290 CenterY=-273.2 CenterZ=0 NormalX=0 NormalY=0 NormalZ=1 AngleXU=0 Radius=1.5
    g2: Circle CenterX=290 CenterY=-333.2 CenterZ=0 NormalX=0 NormalY=0 NormalZ=1 AngleXU=0 Radius=1.5
  constraints (6):
    c: Coincident(g0,g-3)
    c: Equal(g0,g-3)
    c: Coincident(g1,g-4)
    c: Equal(g1,g-4)
    c: Coincident(g2,g-5)
    c: Equal(g2,g-5)
FEATURE [PartDesign::Pocket] Pocket034
  BaseFeature = -> Pocket033
  Direction = (0,-1,2e-16)
  Length = 5
  Length2 = 5
  Profile = -> Sketch074
  ReferenceAxis = -> Sketch074 [N_Axis]
  Refine = true
  Suppressed = false
  Type = 0
FEATURE [Sketcher::SketchObject] Sketch075
  ArcFitTolerance = 1e-06
  AttachmentSupport = -> [Pad036]
  ExternalGeometry = -> [Pad036]
  FullyConstrained = false
  MakeInternals = false
  MapMode = 5
  Placement = pos=(-2.406e-13,87.9132,-50.7567) rot=(1,0,0;1.0472rad)
  sketch-geometry (28):
    g0: LineSegment [constr] StartX=-100 StartY=-176.026 StartZ=0 EndX=-100 EndY=200.567 EndZ=0
    g1: LineSegment [constr] StartX=-100 StartY=-176.026 StartZ=0 EndX=-100 EndY=-166.026 EndZ=0
    g2: LineSegment [constr] StartX=-100 StartY=-166.026 StartZ=0 EndX=-110 EndY=-166.026 EndZ=0
    g3: LineSegment [constr] StartX=-110 StartY=-166.026 StartZ=0 EndX=-110 EndY=-176.026 EndZ=0
    g4: LineSegment [constr] StartX=-110 StartY=-176.026 StartZ=0 EndX=-100 EndY=-176.026 EndZ=0
    g5: LineSegment [constr] StartX=-100 StartY=12.2705 StartZ=0 EndX=-100 EndY=22.2705 EndZ=0
    g6: LineSegment [constr] StartX=-100 StartY=22.2705 StartZ=0 EndX=-110 EndY=22.2705 EndZ=0
    g7: LineSegment [constr] StartX=-110 StartY=22.2705 StartZ=0 EndX=-110 EndY=12.2705 EndZ=0
    g8: LineSegment [constr] StartX=-110 StartY=12.2705 StartZ=0 EndX=-100 EndY=12.2705 EndZ=0
    g9: LineSegment [constr] StartX=-100 StartY=200.567 StartZ=0 EndX=-110 EndY=200.567 EndZ=0
    g10: LineSegment [constr] StartX=-110 StartY=200.567 StartZ=0 EndX=-110 EndY=190.567 EndZ=0
    g11: LineSegment [constr] StartX=-110 StartY=190.567 StartZ=0 EndX=-100 EndY=190.567 EndZ=0
    g12: LineSegment [constr] StartX=-100 StartY=190.567 StartZ=0 EndX=-100 EndY=200.567 EndZ=0
    g13: LineSegment [constr] StartX=-110 StartY=190.567 StartZ=0 EndX=-110 EndY=22.2705 EndZ=0
    g14: LineSegment [constr] StartX=-110 StartY=12.2705 StartZ=0 EndX=-110 EndY=-166.026 EndZ=0
    g15: LineSegment [constr] StartX=-110 StartY=-76.8779 StartZ=0 EndX=-100 EndY=-76.8779 EndZ=0
    g16: LineSegment [constr] StartX=-100 StartY=-76.8779 StartZ=0 EndX=-100 EndY=-66.8779 EndZ=0
    g17: LineSegment [constr] StartX=-100 StartY=-66.8779 StartZ=0 EndX=-110 EndY=-66.8779 EndZ=0
    g18: LineSegment [constr] StartX=-110 StartY=-66.8779 StartZ=0 EndX=-110 EndY=-76.8779 EndZ=0
    g19: LineSegment [constr] StartX=-110 StartY=106.419 StartZ=0 EndX=-100 EndY=106.419 EndZ=0
    g20: LineSegment [constr] StartX=-100 StartY=106.419 StartZ=0 EndX=-100 EndY=116.419 EndZ=0
    g21: LineSegment [constr] StartX=-100 StartY=116.419 StartZ=0 EndX=-110 EndY=116.419 EndZ=0
    g22: LineSegment [constr] StartX=-110 StartY=116.419 StartZ=0 EndX=-110 EndY=106.419 EndZ=0
    g23: Circle CenterX=-110 CenterY=190.567 CenterZ=0 NormalX=0 NormalY=0 NormalZ=1 AngleXU=0 Radius=1.5
    g24: Circle CenterX=-110 CenterY=106.419 CenterZ=0 NormalX=0 NormalY=0 NormalZ=1 AngleXU=0 Radius=1.5
    g25: Circle CenterX=-110 CenterY=12.2705 CenterZ=0 NormalX=0 NormalY=0 NormalZ=1 AngleXU=0 Radius=1.5
    g26: Circle CenterX=-110 CenterY=-76.8779 CenterZ=0 NormalX=0 NormalY=0 NormalZ=1 AngleXU=0 Radius=1.5
    g27: Circle CenterX=-110 CenterY=-166.026 CenterZ=0 NormalX=0 NormalY=0 NormalZ=1 AngleXU=0 Radius=1.5
  constraints (64):
    c: Coincident(g0,g-4)
    c: Coincident(g0,g-3)
    c: Coincident(g1,g2)
    c: Coincident(g2,g3)
    c: Coincident(g3,g4)
    c: Coincident(g4,g1)
    c: Vertical(g1)
    c: Vertical(g3)
    c: Horizontal(g2)
    c: Horizontal(g4)
    c: Distance(g1,g3) = 10
    c: Distance(g2,g4) = 10
    c: Coincident(g1,g0)
    c: Coincident(g5,g6)
    c: Coincident(g6,g7)
    c: Coincident(g7,g8)
    c: Coincident(g8,g5)
    c: Vertical(g5)
    c: Vertical(g7)
    c: Horizontal(g6)
    c: Horizontal(g8)
    c: Distance(g5,g7) = 10
    c: Distance(g6,g8) = 10
    c: Symmetric(g0,g0,g5)
    c: Coincident(g9,g10)
    c: Coincident(g10,g11)
    c: Coincident(g11,g12)
    c: Coincident(g12,g9)
    c: Horizontal(g9)
    c: Horizontal(g11)
    c: Vertical(g10)
    c: Vertical(g12)
    c: Distance(g10,g12) = 10
    c: Distance(g9,g11) = 10
    c: Coincident(g9,g0)
    c: Coincident(g13,g10)
    c: Coincident(g13,g6)
    c: Coincident(g14,g7)
    c: Coincident(g14,g2)
    c: Coincident(g15,g16)
    c: Coincident(g16,g17)
    c: Coincident(g17,g18)
    c: Coincident(g18,g15)
    c: Horizontal(g15)
    c: Horizontal(g17)
    c: Vertical(g16)
    c: Vertical(g18)
    c: Distance(g15,g17) = 10
    c: Symmetric(g14,g14,g15)
    c: PointOnObject(g16,g0)
    c: Coincident(g19,g20)
    c: Coincident(g20,g21)
    c: Coincident(g21,g22)
    c: Coincident(g22,g19)
    c: Horizontal(g19)
    c: Horizontal(g21)
    c: Vertical(g20)
    c: Vertical(g22)
    c: Distance(g19,g21) = 10
    c: Symmetric(g13,g13,g19)
    c: PointOnObject(g20,g0)
    c: Coincident(g23,g10)
    c: Coincident(g25,g7)
    c: Coincident(g27,g2)
FEATURE [PartDesign::Pocket] Pocket035
  BaseFeature = -> Pad036
  Direction = (-2.4e-15,0.866025,-0.5)
  Length = 5
  Length2 = 5
  Profile = -> Sketch075
  ReferenceAxis = -> Sketch075 [N_Axis]
  Refine = true
  Suppressed = false
  Type = 0
FEATURE [Sketcher::SketchObject] Sketch076
  ArcFitTolerance = 1e-06
  AttachmentSupport = -> [Pocket035]
  ExternalGeometry = -> [Binder013]
  FullyConstrained = true
  MakeInternals = false
  MapMode = 5
  Placement = pos=(7e-16,-0.1,1e-16) rot=(1,0,0;1.5708rad)
  sketch-geometry (3):
    g0: Circle CenterX=-110 CenterY=-333.2 CenterZ=0 NormalX=0 NormalY=0 NormalZ=1 AngleXU=0 Radius=1.5
    g1: Circle CenterX=-110 CenterY=-273.2 CenterZ=0 NormalX=0 NormalY=0 NormalZ=1 AngleXU=0 Radius=1.5
    g2: Circle CenterX=-110 CenterY=-213.2 CenterZ=0 NormalX=0 NormalY=0 NormalZ=1 AngleXU=0 Radius=1.5
  constraints (6):
    c: Coincident(g0,g-5)
    c: Equal(g0,g-5)
    c: Coincident(g1,g-4)
    c: Equal(g1,g-4)
    c: Coincident(g2,g-3)
    c: Equal(g2,g-3)
FEATURE [PartDesign::Pocket] Pocket036
  BaseFeature = -> Pocket035
  Direction = (-7.4e-15,1,-2e-16)
  Length = 5
  Length2 = 5
  Profile = -> Sketch076
  ReferenceAxis = -> Sketch076 [N_Axis]
  Refine = true
  Suppressed = false
  Type = 0
FEATURE [Sketcher::SketchObject] Sketch077
  ArcFitTolerance = 1e-06
  AttachmentSupport = -> [Pocket036]
  ExternalGeometry = -> [Pocket036]
  FullyConstrained = false
  MakeInternals = false
  MapMode = 5
  Placement = pos=(0,-7.51e-14,-341.2) rot=(0,0,1;0rad)
  sketch-geometry (28):
    g0: LineSegment [constr] StartX=-100 StartY=349.9 StartZ=0 EndX=-100 EndY=1.9 EndZ=0
    g1: LineSegment [constr] StartX=-100 StartY=1.9 StartZ=0 EndX=-100 EndY=11.9 EndZ=0
    g2: LineSegment [constr] StartX=-100 StartY=11.9 StartZ=0 EndX=-110 EndY=11.9 EndZ=0
    g3: LineSegment [constr] StartX=-110 StartY=11.9 StartZ=0 EndX=-110 EndY=1.9 EndZ=0
    g4: LineSegment [constr] StartX=-110 StartY=1.9 StartZ=0 EndX=-100 EndY=1.9 EndZ=0
    g5: LineSegment [constr] StartX=-100 StartY=349.9 StartZ=0 EndX=-110 EndY=349.9 EndZ=0
    g6: LineSegment [constr] StartX=-110 StartY=349.9 StartZ=0 EndX=-110 EndY=339.9 EndZ=0
    g7: LineSegment [constr] StartX=-110 StartY=339.9 StartZ=0 EndX=-100 EndY=339.9 EndZ=0
    g8: LineSegment [constr] StartX=-100 StartY=339.9 StartZ=0 EndX=-100 EndY=349.9 EndZ=0
    g9: LineSegment [constr] StartX=-100 StartY=175.9 StartZ=0 EndX=-100 EndY=185.9 EndZ=0
    g10: LineSegment [constr] StartX=-100 StartY=185.9 StartZ=0 EndX=-110 EndY=185.9 EndZ=0
    g11: LineSegment [constr] StartX=-110 StartY=185.9 StartZ=0 EndX=-110 EndY=175.9 EndZ=0
    g12: LineSegment [constr] StartX=-110 StartY=175.9 StartZ=0 EndX=-100 EndY=175.9 EndZ=0
    g13: LineSegment [constr] StartX=-110 StartY=175.9 StartZ=0 EndX=-110 EndY=11.9 EndZ=0
    g14: LineSegment [constr] StartX=-110 StartY=93.9 StartZ=0 EndX=-100 EndY=93.9 EndZ=0
    g15: LineSegment [constr] StartX=-100 StartY=93.9 StartZ=0 EndX=-100 EndY=103.9 EndZ=0
    g16: LineSegment [constr] StartX=-100 StartY=103.9 StartZ=0 EndX=-110 EndY=103.9 EndZ=0
    g17: LineSegment [constr] StartX=-110 StartY=103.9 StartZ=0 EndX=-110 EndY=93.9 EndZ=0
    g18: Circle CenterX=-110 CenterY=339.9 CenterZ=0 NormalX=0 NormalY=0 NormalZ=1 AngleXU=0 Radius=1.5
    g19: Circle CenterX=-110 CenterY=175.9 CenterZ=0 NormalX=0 NormalY=0 NormalZ=1 AngleXU=0 Radius=1.5
    g20: Circle CenterX=-110 CenterY=93.9 CenterZ=0 NormalX=0 NormalY=0 NormalZ=1 AngleXU=0 Radius=1.5
    g21: Circle CenterX=-110 CenterY=11.9 CenterZ=0 NormalX=0 NormalY=0 NormalZ=1 AngleXU=0 Radius=1.5
    g22: LineSegment [constr] StartX=-110 StartY=339.9 StartZ=0 EndX=-110 EndY=175.9 EndZ=0
    g23: LineSegment [constr] StartX=-110 StartY=257.9 StartZ=0 EndX=-100 EndY=257.9 EndZ=0
    g24: LineSegment [constr] StartX=-100 StartY=257.9 StartZ=0 EndX=-100 EndY=267.9 EndZ=0
    g25: LineSegment [constr] StartX=-100 StartY=267.9 StartZ=0 EndX=-110 EndY=267.9 EndZ=0
    g26: LineSegment [constr] StartX=-110 StartY=267.9 StartZ=0 EndX=-110 EndY=257.9 EndZ=0
    g27: Circle CenterX=-110 CenterY=257.9 CenterZ=0 NormalX=0 NormalY=0 NormalZ=1 AngleXU=0 Radius=1.5
  constraints (61):
    c: Coincident(g0,g-4)
    c: Coincident(g0,g-3)
    c: Coincident(g1,g2)
    c: Coincident(g2,g3)
    c: Coincident(g3,g4)
    c: Coincident(g4,g1)
    c: Vertical(g1)
    c: Vertical(g3)
    c: Horizontal(g2)
    c: Horizontal(g4)
    c: Distance(g1,g3) = 10
    c: Distance(g2,g4) = 10
    c: Coincident(g1,g0)
    c: Coincident(g5,g6)
    c: Coincident(g6,g7)
    c: Coincident(g7,g8)
    c: Coincident(g8,g5)
    c: Horizontal(g5)
    c: Horizontal(g7)
    c: Vertical(g6)
    c: Vertical(g8)
    c: Distance(g6,g8) = 10
    c: Distance(g5,g7) = 10
    c: Coincident(g5,g0)
    c: Coincident(g9,g10)
    c: Coincident(g10,g11)
    c: Coincident(g11,g12)
    c: Coincident(g12,g9)
    c: Vertical(g9)
    c: Vertical(g11)
    c: Horizontal(g10)
    c: Horizontal(g12)
    c: Distance(g9,g11) = 10
    c: Distance(g10,g12) = 10
    c: Symmetric(g0,g0,g9)
    c: Coincident(g13,g11)
    c: Coincident(g13,g2)
    c: Coincident(g14,g15)
    c: Coincident(g15,g16)
    c: Coincident(g16,g17)
    c: Coincident(g17,g14)
    c: Horizontal(g14)
    c: Horizontal(g16)
    c: Vertical(g15)
    c: Vertical(g17)
    c: Distance(g14,g16) = 10
    c: Symmetric(g13,g13,g14)
    c: PointOnObject(g15,g0)
    c: Coincident(g18,g6)
    c: Coincident(g22,g6)
    c: Coincident(g22,g19)
    c: Vertical(g22)
    c: Coincident(g23,g24)
    c: Coincident(g24,g25)
    c: Coincident(g25,g26)
    c: Coincident(g26,g23)
    c: Horizontal(g23)
    c: Horizontal(g25)
    c: Vertical(g24)
    c: Vertical(g26)
    c: Distance(g24,g26) = 10
FEATURE [PartDesign::Pocket] Pocket037
  BaseFeature = -> Pocket036
  Direction = (0,0,-1)
  Length = 5
  Length2 = 5
  Profile = -> Sketch077
  ReferenceAxis = -> Sketch077 [N_Axis]
  Refine = true
  Suppressed = false
  Type = 0
FEATURE [Sketcher::SketchObject] Sketch078
  ArcFitTolerance = 1e-06
  AttachmentSupport = -> [Pocket037]
  ExternalGeometry = -> [Pocket037]
  FullyConstrained = false
  MakeInternals = false
  MapMode = 5
  Placement = pos=(-12.0542,2.98e-14,134.773) rot=(0,-1,0;0.089203rad)
  sketch-geometry (15):
    g0: LineSegment [constr] StartX=-88.2969 StartY=349.9 StartZ=0 EndX=-98.2969 EndY=349.9 EndZ=0
    g1: LineSegment [constr] StartX=-98.2969 StartY=349.9 StartZ=0 EndX=-98.2969 EndY=339.9 EndZ=0
    g2: LineSegment [constr] StartX=-98.2969 StartY=339.9 StartZ=0 EndX=-88.2969 EndY=339.9 EndZ=0
    g3: LineSegment [constr] StartX=-88.2969 StartY=339.9 StartZ=0 EndX=-88.2969 EndY=349.9 EndZ=0
    g4: LineSegment [constr] StartX=-88.2969 StartY=190.488 StartZ=0 EndX=-88.2969 EndY=200.488 EndZ=0
    g5: LineSegment [constr] StartX=-88.2969 StartY=200.488 StartZ=0 EndX=-98.2969 EndY=200.488 EndZ=0
    g6: LineSegment [constr] StartX=-98.2969 StartY=200.488 StartZ=0 EndX=-98.2969 EndY=190.488 EndZ=0
    g7: LineSegment [constr] StartX=-98.2969 StartY=190.488 StartZ=0 EndX=-88.2969 EndY=190.488 EndZ=0
    g8: LineSegment [constr] StartX=-88.2969 StartY=270.194 StartZ=0 EndX=-88.2969 EndY=280.194 EndZ=0
    g9: LineSegment [constr] StartX=-88.2969 StartY=280.194 StartZ=0 EndX=-98.2969 EndY=280.194 EndZ=0
    g10: LineSegment [constr] StartX=-98.2969 StartY=280.194 StartZ=0 EndX=-98.2969 EndY=270.194 EndZ=0
    g11: LineSegment [constr] StartX=-98.2969 StartY=270.194 StartZ=0 EndX=-88.2969 EndY=270.194 EndZ=0
    g12: Circle CenterX=-98.2969 CenterY=200.488 CenterZ=0 NormalX=0 NormalY=0 NormalZ=1 AngleXU=0 Radius=1.5
    g13: Circle CenterX=-98.2969 CenterY=270.194 CenterZ=0 NormalX=0 NormalY=0 NormalZ=1 AngleXU=0 Radius=1.5
    g14: Circle CenterX=-98.2969 CenterY=339.9 CenterZ=0 NormalX=0 NormalY=0 NormalZ=1 AngleXU=0 Radius=1.5
  constraints (30):
    c: Coincident(g0,g1)
    c: Coincident(g1,g2)
    c: Coincident(g2,g3)
    c: Coincident(g3,g0)
    c: Horizontal(g0)
    c: Horizontal(g2)
    c: Vertical(g1)
    c: Vertical(g3)
    c: Distance(g1,g3) = 10
    c: Distance(g0,g2) = 10
    c: Coincident(g4,g5)
    c: Coincident(g5,g6)
    c: Coincident(g6,g7)
    c: Coincident(g7,g4)
    c: Vertical(g4)
    c: Vertical(g6)
    c: Horizontal(g5)
    c: Horizontal(g7)
    c: Distance(g4,g6) = 10
    c: Distance(g5,g7) = 10
    c: Coincident(g8,g9)
    c: Coincident(g9,g10)
    c: Coincident(g10,g11)
    c: Coincident(g11,g8)
    c: Vertical(g8)
    c: Vertical(g10)
    c: Horizontal(g9)
    c: Horizontal(g11)
    c: Distance(g8,g10) = 10
    c: Distance(g9,g11) = 10
FEATURE [PartDesign::Pocket] Pocket038
  BaseFeature = -> Pocket037
  Direction = (0.0890849,0,-0.996024)
  Length = 5
  Length2 = 5
  Profile = -> Sketch078
  ReferenceAxis = -> Sketch078 [N_Axis]
  Refine = true
  Suppressed = false
  Type = 0
FEATURE [Sketcher::SketchObject] Sketch079
  ArcFitTolerance = 1e-06
  AttachmentSupport = -> [Pocket037]
  ExternalGeometry = -> [Pocket037]
  FullyConstrained = false
  MakeInternals = false
  MapMode = 5
  Placement = pos=(-12.0542,2.98e-14,134.773) rot=(0,-1,0;0.089203rad)
  sketch-geometry (18):
    g0: LineSegment [constr] StartX=-88.2969 StartY=349.9 StartZ=0 EndX=-88.2969 EndY=190.488 EndZ=0
    g1: LineSegment [constr] StartX=-88.2969 StartY=190.488 StartZ=0 EndX=-88.2969 EndY=200.488 EndZ=0
    g2: LineSegment [constr] StartX=-88.2969 StartY=200.488 StartZ=0 EndX=-98.2969 EndY=200.488 EndZ=0
    g3: LineSegment [constr] StartX=-98.2969 StartY=200.488 StartZ=0 EndX=-98.2969 EndY=190.488 EndZ=0
    g4: LineSegment [constr] StartX=-98.2969 StartY=190.488 StartZ=0 EndX=-88.2969 EndY=190.488 EndZ=0
    g5: LineSegment [constr] StartX=-88.2969 StartY=349.9 StartZ=0 EndX=-98.2969 EndY=349.9 EndZ=0
    g6: LineSegment [constr] StartX=-98.2969 StartY=349.9 StartZ=0 EndX=-98.2969 EndY=339.9 EndZ=0
    g7: LineSegment [constr] StartX=-98.2969 StartY=339.9 StartZ=0 EndX=-88.2969 EndY=339.9 EndZ=0
    g8: LineSegment [constr] StartX=-88.2969 StartY=339.9 StartZ=0 EndX=-88.2969 EndY=349.9 EndZ=0
    g9: LineSegment [constr] StartX=-88.2969 StartY=270.194 StartZ=0 EndX=-88.2969 EndY=280.194 EndZ=0
    g10: LineSegment [constr] StartX=-88.2969 StartY=280.194 StartZ=0 EndX=-98.2969 EndY=280.194 EndZ=0
    g11: LineSegment [constr] StartX=-98.2969 StartY=280.194 StartZ=0 EndX=-98.2969 EndY=270.194 EndZ=0
    g12: LineSegment [constr] StartX=-98.2969 StartY=270.194 StartZ=0 EndX=-88.2969 EndY=270.194 EndZ=0
    g13: LineSegment [constr] StartX=-98.2969 StartY=270.194 StartZ=0 EndX=-98.2969 EndY=339.9 EndZ=0
    g14: LineSegment [constr] StartX=-98.2969 StartY=270.194 StartZ=0 EndX=-98.2969 EndY=200.488 EndZ=0
    g15: Circle CenterX=-98.2969 CenterY=200.488 CenterZ=0 NormalX=0 NormalY=0 NormalZ=1 AngleXU=0 Radius=1.5
    g16: Circle CenterX=-98.2969 CenterY=339.9 CenterZ=0 NormalX=0 NormalY=0 NormalZ=1 AngleXU=0 Radius=1.5
    g17: Circle CenterX=-98.2969 CenterY=270.194 CenterZ=0 NormalX=0 NormalY=0 NormalZ=1 AngleXU=0 Radius=1.5
  constraints (40):
    c: Coincident(g0,g-4)
    c: Coincident(g0,g-3)
    c: Coincident(g1,g2)
    c: Coincident(g2,g3)
    c: Coincident(g3,g4)
    c: Coincident(g4,g1)
    c: Vertical(g1)
    c: Vertical(g3)
    c: Horizontal(g2)
    c: Horizontal(g4)
    c: Distance(g1,g3) = 10
    c: Distance(g2,g4) = 10
    c: Coincident(g1,g0)
    c: Coincident(g5,g6)
    c: Coincident(g6,g7)
    c: Coincident(g7,g8)
    c: Coincident(g8,g5)
    c: Horizontal(g5)
    c: Horizontal(g7)
    c: Vertical(g6)
    c: Vertical(g8)
    c: Distance(g6,g8) = 10
    c: Distance(g5,g7) = 10
    c: Coincident(g5,g0)
    c: Coincident(g9,g10)
    c: Coincident(g10,g11)
    c: Coincident(g11,g12)
    c: Coincident(g12,g9)
    c: Vertical(g9)
    c: Vertical(g11)
    c: Horizontal(g10)
    c: Horizontal(g12)
    c: Distance(g9,g11) = 10
    c: Distance(g10,g12) = 10
    c: Symmetric(g0,g0,g9)
    c: Coincident(g13,g11)
    c: Coincident(g13,g6)
    c: Coincident(g14,g11)
    c: Coincident(g14,g2)
    c: Coincident(g15,g2)
FEATURE [PartDesign::Pocket] Pocket039
  BaseFeature = -> Pocket038
  Direction = (0.0890849,0,-0.996024)
  Length = 5
  Length2 = 5
  Profile = -> Sketch079
  ReferenceAxis = -> Sketch079 [N_Axis]
  Refine = true
  Suppressed = false
  Type = 0
FEATURE [Sketcher::SketchObject] Sketch080
  ArcFitTolerance = 1e-06
  AttachmentSupport = -> [Binder014]
  ExternalGeometry = -> [Binder014]
  FullyConstrained = true
  MakeInternals = false
  MapMode = 5
  Placement = pos=(0,3.73205,0) rot=(0,0.707107,0.707107;3.14159rad)
  sketch-geometry (10):
    g0: Circle CenterX=290 CenterY=-190 CenterZ=0 NormalX=0 NormalY=0 NormalZ=1 AngleXU=0 Radius=1.5
    g1: Circle CenterX=110 CenterY=-190 CenterZ=0 NormalX=0 NormalY=0 NormalZ=1 AngleXU=0 Radius=1.5
    g2: Circle CenterX=110 CenterY=-100.852 CenterZ=0 NormalX=0 NormalY=0 NormalZ=1 AngleXU=0 Radius=1.5
    g3: Circle CenterX=110 CenterY=-11.7032 CenterZ=0 NormalX=0 NormalY=0 NormalZ=1 AngleXU=0 Radius=1.5
    g4: Circle CenterX=110 CenterY=82.4453 CenterZ=0 NormalX=0 NormalY=0 NormalZ=1 AngleXU=0 Radius=1.5
    g5: Circle CenterX=110 CenterY=166.594 CenterZ=0 NormalX=0 NormalY=0 NormalZ=1 AngleXU=0 Radius=1.5
    g6: Circle CenterX=290 CenterY=143.673 CenterZ=0 NormalX=0 NormalY=0 NormalZ=1 AngleXU=0 Radius=1.5
    g7: Circle CenterX=290 CenterY=65.2549 CenterZ=0 NormalX=0 NormalY=0 NormalZ=1 AngleXU=0 Radius=1.5
    g8: Circle CenterX=290 CenterY=-23.1634 CenterZ=0 NormalX=0 NormalY=0 NormalZ=1 AngleXU=0 Radius=1.5
    g9: Circle CenterX=290 CenterY=-106.582 CenterZ=0 NormalX=0 NormalY=0 NormalZ=1 AngleXU=0 Radius=1.5
  constraints (20):
    c: Coincident(g0,g-10)
    c: Equal(g0,g-10)
    c: Coincident(g1,g-11)
    c: Equal(g1,g-11)
    c: Coincident(g2,g-12)
    c: Equal(g2,g-12)
    c: Coincident(g3,g-7)
    c: Equal(g3,g-7)
    c: Coincident(g4,g-4)
    c: Equal(g4,g-4)
    c: Coincident(g5,g-3)
    c: Equal(g5,g-3)
    c: Coincident(g6,g-6)
    c: Equal(g6,g-6)
    c: Coincident(g7,g-5)
    c: Equal(g7,g-5)
    c: Coincident(g8,g-8)
    c: Equal(g8,g-8)
    c: Coincident(g9,g-9)
    c: Equal(g9,g-9)
FEATURE [PartDesign::Pocket] Pocket040
  BaseFeature = -> Pad003
  Direction = (0,-1,2e-16)
  Length = 5
  Length2 = 5
  Placement = pos=(0,0,0) rot=(1,0,0;1.5708rad)
  Profile = -> Sketch080
  ReferenceAxis = -> Sketch080 [N_Axis]
  Refine = true
  Suppressed = false
  Type = 0
FEATURE [Sketcher::SketchObject] Sketch081
  ArcFitTolerance = 1e-06
  AttachmentSupport = -> [Binder015]
  ExternalGeometry = -> [Binder015]
  FullyConstrained = true
  MakeInternals = false
  MapMode = 5
  Placement = pos=(0,-0.1,0) rot=(0,0.707107,0.707107;3.14159rad)
  sketch-geometry (5):
    g0: LineSegment StartX=122 StartY=-223.2 StartZ=0 EndX=278 EndY=-223.2 EndZ=0
    g1: LineSegment StartX=278 StartY=-223.2 StartZ=0 EndX=278 EndY=-183.2 EndZ=0
    g2: LineSegment StartX=278 StartY=-183.2 StartZ=0 EndX=122 EndY=-183.2 EndZ=0
    g3: LineSegment StartX=122 StartY=-183.2 StartZ=0 EndX=122 EndY=-223.2 EndZ=0
    g4: GeomPoint [constr] X=200 Y=-203.2 Z=0
  constraints (12):
    c: Coincident(g0,g1)
    c: Coincident(g1,g2)
    c: Coincident(g2,g3)
    c: Coincident(g3,g0)
    c: Horizontal(g0)
    c: Horizontal(g2)
    c: Vertical(g1)
    c: Vertical(g3)
    c: Symmetric(g2,g0,g4)
    c: Distance(g0,g2) = 40
    c: Symmetric(g-5,g-5,g4)
    c: PointOnObject(g1,g-4)
FEATURE [PartDesign::Pad] Pad037
  Direction = (0,1,-2e-16)
  Length = 350
  Length2 = 10
  Profile = -> Sketch081
  ReferenceAxis = -> Sketch081 [N_Axis]
  Refine = true
  Suppressed = false
  Type = 0
FEATURE [Sketcher::SketchObject] Sketch082
  ArcFitTolerance = 1e-06
  AttachmentSupport = -> [Binder015]
  ExternalGeometry = -> [Binder015,Pad037]
  FullyConstrained = false
  MakeInternals = false
  MapMode = 5
  Placement = pos=(-122,0,0) rot=(0.57735,-0.57735,-0.57735;2.0944rad)
  sketch-geometry (9):
    g0: LineSegment [constr] StartX=0.1 StartY=-203.2 StartZ=0 EndX=-1.9 EndY=-203.2 EndZ=0
    g1: LineSegment StartX=-13.447 StartY=-183.2 StartZ=0 EndX=-1.9 EndY=-203.2 EndZ=0
    g2: LineSegment StartX=-1.9 StartY=-203.2 StartZ=0 EndX=-1.9 EndY=-221.2 EndZ=0
    g3: LineSegment StartX=-1.9 StartY=-221.2 StartZ=0 EndX=-349.9 EndY=-221.2 EndZ=0
    g4: LineSegment StartX=-13.447 StartY=-183.2 StartZ=0 EndX=-349.9 EndY=-183.2 EndZ=0
    g5: LineSegment StartX=-349.9 StartY=-221.2 StartZ=0 EndX=-349.9 EndY=-183.2 EndZ=0
    g6: LineSegment StartX=0.1 StartY=-183.2 StartZ=0 EndX=-11.447 EndY=-183.2 EndZ=0
    g7: LineSegment StartX=0.1 StartY=-183.2 StartZ=0 EndX=0.1 EndY=-203.2 EndZ=0
    g8: LineSegment StartX=0.1 StartY=-203.2 StartZ=0 EndX=-11.447 EndY=-183.2 EndZ=0
  constraints (22):
    c: PointOnObject(g6,g-3)
    c: Distance(g0) = 2
    c: Coincident(g0,g-3)
    c: Horizontal(g0)
    c: Coincident(g1,g0)
    c: Coincident(g2,g0)
    c: Vertical(g2)
    c: Coincident(g3,g2)
    c: Horizontal(g3)
    c: Horizontal(g4)
    c: Coincident(g5,g3)
    c: Vertical(g5)
    c: Coincident(g5,g4)
    c: Coincident(g6,g-4)
    c: Horizontal(g6)
    c: Coincident(g7,g6)
    c: Coincident(g7,g0)
    c: Coincident(g8,g0)
    c: Coincident(g4,g1)
    c: PointOnObject(g1,g-5)
    c: DistanceX(g1,g6) = 2
    c: Coincident(g8,g6)
FEATURE [PartDesign::Pocket] Pocket041
  BaseFeature = -> Pad037
  Direction = (1,0,0)
  Length = 5
  Length2 = 5
  Profile = -> Sketch082
  ReferenceAxis = -> Sketch082 [N_Axis]
  Refine = true
  Reversed = true
  Suppressed = false
  Type = 1
FEATURE [Sketcher::SketchObject] Sketch083
  ArcFitTolerance = 1e-06
  AttachmentSupport = -> [Pocket041]
  ExternalGeometry = -> [Pocket041]
  FullyConstrained = false
  MakeInternals = false
  MapMode = 5
  Placement = pos=(0,87.9132,-50.7567) rot=(1,0,0;1.0472rad)
  sketch-geometry (16):
    g0: LineSegment [constr] StartX=-278 StartY=-176.026 StartZ=0 EndX=-268 EndY=-176.026 EndZ=0
    g1: LineSegment [constr] StartX=-268 StartY=-176.026 StartZ=0 EndX=-268 EndY=-166.026 EndZ=0
    g2: LineSegment [constr] StartX=-268 StartY=-166.026 StartZ=0 EndX=-278 EndY=-166.026 EndZ=0
    g3: LineSegment [constr] StartX=-278 StartY=-166.026 StartZ=0 EndX=-278 EndY=-176.026 EndZ=0
    g4: LineSegment [constr] StartX=-122 StartY=-176.026 StartZ=0 EndX=-122 EndY=-166.026 EndZ=0
    g5: LineSegment [constr] StartX=-122 StartY=-166.026 StartZ=0 EndX=-132 EndY=-166.026 EndZ=0
    g6: LineSegment [constr] StartX=-132 StartY=-166.026 StartZ=0 EndX=-132 EndY=-176.026 EndZ=0
    g7: LineSegment [constr] StartX=-132 StartY=-176.026 StartZ=0 EndX=-122 EndY=-176.026 EndZ=0
    g8: LineSegment [constr] StartX=-268 StartY=-176.026 StartZ=0 EndX=-132 EndY=-176.026 EndZ=0
    g9: LineSegment [constr] StartX=-200 StartY=-176.026 StartZ=0 EndX=-190 EndY=-176.026 EndZ=0
    g10: LineSegment [constr] StartX=-190 StartY=-176.026 StartZ=0 EndX=-190 EndY=-166.026 EndZ=0
    g11: LineSegment [constr] StartX=-190 StartY=-166.026 StartZ=0 EndX=-200 EndY=-166.026 EndZ=0
    g12: LineSegment [constr] StartX=-200 StartY=-166.026 StartZ=0 EndX=-200 EndY=-176.026 EndZ=0
    g13: Circle CenterX=-200 CenterY=-166.026 CenterZ=0 NormalX=0 NormalY=0 NormalZ=1 AngleXU=0 Radius=1.5
    g14: Circle CenterX=-268 CenterY=-166.026 CenterZ=0 NormalX=0 NormalY=0 NormalZ=1 AngleXU=0 Radius=1.5
    g15: Circle CenterX=-132 CenterY=-166.026 CenterZ=0 NormalX=0 NormalY=0 NormalZ=1 AngleXU=0 Radius=1.5
  constraints (35):
    c: Coincident(g0,g1)
    c: Coincident(g1,g2)
    c: Coincident(g2,g3)
    c: Coincident(g3,g0)
    c: Horizontal(g0)
    c: Horizontal(g2)
    c: Vertical(g1)
    c: Vertical(g3)
    c: Distance(g1,g3) = 10
    c: Distance(g0,g2) = 10
    c: Coincident(g0,g-3)
    c: Coincident(g4,g5)
    c: Coincident(g5,g6)
    c: Coincident(g6,g7)
    c: Coincident(g7,g4)
    c: Vertical(g4)
    c: Vertical(g6)
    c: Horizontal(g5)
    c: Horizontal(g7)
    c: Distance(g4,g6) = 10
    c: Distance(g5,g7) = 10
    c: Coincident(g4,g-4)
    c: Coincident(g8,g0)
    c: Coincident(g8,g6)
    c: Coincident(g9,g10)
    c: Coincident(g10,g11)
    c: Coincident(g11,g12)
    c: Coincident(g12,g9)
    c: Horizontal(g9)
    c: Horizontal(g11)
    c: Vertical(g10)
    c: Vertical(g12)
    c: Distance(g10,g12) = 10
    c: Distance(g9,g11) = 10
    c: Symmetric(g8,g8,g9)
FEATURE [PartDesign::Pocket] Pocket042
  BaseFeature = -> Pocket041
  Direction = (0,0.866025,-0.5)
  Length = 5
  Length2 = 5
  Profile = -> Sketch083
  ReferenceAxis = -> Sketch083 [N_Axis]
  Refine = true
  Suppressed = false
  Type = 0
FEATURE [Sketcher::SketchObject] Sketch084
  ArcFitTolerance = 1e-06
  AttachmentSupport = -> [Pocket042]
  ExternalGeometry = -> [Pocket042]
  FullyConstrained = false
  MakeInternals = false
  MapMode = 5
  Placement = pos=(0,-0.1,0) rot=(1,0,0;1.5708rad)
  sketch-geometry (16):
    g0: LineSegment [constr] StartX=-122 StartY=-223.2 StartZ=0 EndX=-122 EndY=-213.2 EndZ=0
    g1: LineSegment [constr] StartX=-122 StartY=-213.2 StartZ=0 EndX=-132 EndY=-213.2 EndZ=0
    g2: LineSegment [constr] StartX=-132 StartY=-213.2 StartZ=0 EndX=-132 EndY=-223.2 EndZ=0
    g3: LineSegment [constr] StartX=-132 StartY=-223.2 StartZ=0 EndX=-122 EndY=-223.2 EndZ=0
    g4: LineSegment [constr] StartX=-278 StartY=-223.2 StartZ=0 EndX=-268 EndY=-223.2 EndZ=0
    g5: LineSegment [constr] StartX=-268 StartY=-223.2 StartZ=0 EndX=-268 EndY=-213.2 EndZ=0
    g6: LineSegment [constr] StartX=-268 StartY=-213.2 StartZ=0 EndX=-278 EndY=-213.2 EndZ=0
    g7: LineSegment [constr] StartX=-278 StartY=-213.2 StartZ=0 EndX=-278 EndY=-223.2 EndZ=0
    g8: LineSegment [constr] StartX=-268 StartY=-223.2 StartZ=0 EndX=-132 EndY=-223.2 EndZ=0
    g9: LineSegment [constr] StartX=-200 StartY=-223.2 StartZ=0 EndX=-190 EndY=-223.2 EndZ=0
    g10: LineSegment [constr] StartX=-190 StartY=-223.2 StartZ=0 EndX=-190 EndY=-213.2 EndZ=0
    g11: LineSegment [constr] StartX=-190 StartY=-213.2 StartZ=0 EndX=-200 EndY=-213.2 EndZ=0
    g12: LineSegment [constr] StartX=-200 StartY=-213.2 StartZ=0 EndX=-200 EndY=-223.2 EndZ=0
    g13: Circle CenterX=-200 CenterY=-213.2 CenterZ=0 NormalX=0 NormalY=0 NormalZ=1 AngleXU=0 Radius=1.5
    g14: Circle CenterX=-268 CenterY=-213.2 CenterZ=0 NormalX=0 NormalY=0 NormalZ=1 AngleXU=0 Radius=1.5
    g15: Circle CenterX=-132 CenterY=-213.2 CenterZ=0 NormalX=0 NormalY=0 NormalZ=1 AngleXU=0 Radius=1.5
  constraints (36):
    c: Coincident(g0,g1)
    c: Coincident(g1,g2)
    c: Coincident(g2,g3)
    c: Coincident(g3,g0)
    c: Vertical(g0)
    c: Vertical(g2)
    c: Horizontal(g1)
    c: Horizontal(g3)
    c: Distance(g0,g2) = 10
    c: Distance(g1,g3) = 10
    c: Coincident(g0,g-4)
    c: Coincident(g4,g5)
    c: Coincident(g5,g6)
    c: Coincident(g6,g7)
    c: Coincident(g7,g4)
    c: Horizontal(g4)
    c: Horizontal(g6)
    c: Vertical(g5)
    c: Vertical(g7)
    c: Distance(g5,g7) = 10
    c: Distance(g4,g6) = 10
    c: Coincident(g4,g-3)
    c: Coincident(g8,g4)
    c: Coincident(g8,g2)
    c: Coincident(g9,g10)
    c: Coincident(g10,g11)
    c: Coincident(g11,g12)
    c: Coincident(g12,g9)
    c: Horizontal(g9)
    c: Horizontal(g11)
    c: Vertical(g10)
    c: Vertical(g12)
    c: Distance(g10,g12) = 10
    c: Distance(g9,g11) = 10
    c: Symmetric(g8,g8,g9)
    c: Coincident(g13,g11)
FEATURE [PartDesign::Pocket] Pocket043
  BaseFeature = -> Pocket042
  Direction = (0,1,-2e-16)
  Length = 5
  Length2 = 5
  Profile = -> Sketch084
  ReferenceAxis = -> Sketch084 [N_Axis]
  Refine = true
  Suppressed = false
  Type = 0
FEATURE [Sketcher::SketchObject] Sketch085
  ArcFitTolerance = 1e-06
  AttachmentSupport = -> [Pocket043]
  ExternalGeometry = -> [Pocket043]
  FullyConstrained = true
  MakeInternals = false
  MapMode = 5
  Placement = pos=(0,1.9,0) rot=(0,0.707107,0.707107;3.14159rad)
  sketch-geometry (8):
    g0: LineSegment StartX=278 StartY=-203.2 StartZ=0 EndX=278 EndY=-221.2 EndZ=0
    g1: LineSegment StartX=278 StartY=-221.2 StartZ=0 EndX=276 EndY=-221.2 EndZ=0
    g2: LineSegment StartX=276 StartY=-221.2 StartZ=0 EndX=276 EndY=-203.2 EndZ=0
    g3: LineSegment StartX=278 StartY=-203.2 StartZ=0 EndX=276 EndY=-203.2 EndZ=0
    g4: LineSegment StartX=122 StartY=-203.2 StartZ=0 EndX=122 EndY=-221.2 EndZ=0
    g5: LineSegment StartX=122 StartY=-221.2 StartZ=0 EndX=124 EndY=-221.2 EndZ=0
    g6: LineSegment StartX=124 StartY=-221.2 StartZ=0 EndX=124 EndY=-203.2 EndZ=0
    g7: LineSegment StartX=124 StartY=-203.2 StartZ=0 EndX=122 EndY=-203.2 EndZ=0
  constraints (20):
    c: Coincident(g0,g-4)
    c: Coincident(g0,g-4)
    c: Distance(g1) = 2
    c: Coincident(g1,g0)
    c: Horizontal(g1)
    c: Coincident(g2,g1)
    c: Vertical(g2)
    c: Coincident(g3,g0)
    c: Horizontal(g3)
    c: Coincident(g3,g2)
    c: Coincident(g4,g-3)
    c: Coincident(g4,g-3)
    c: Distance(g5) = 2
    c: Horizontal(g5)
    c: Coincident(g6,g5)
    c: Vertical(g6)
    c: Coincident(g7,g6)
    c: Horizontal(g7)
    c: Coincident(g7,g4)
    c: Coincident(g5,g4)
FEATURE [PartDesign::Pad] Pad018
  BaseFeature = -> Pocket043
  Direction = (0,1,-2e-16)
  Length = 348
  Length2 = 10
  Profile = -> Sketch085
  ReferenceAxis = -> Sketch085 [N_Axis]
  Refine = true
  Suppressed = false
  Type = 0
FEATURE [Sketcher::SketchObject] Sketch086
  ArcFitTolerance = 1e-06
  AttachmentSupport = -> [Pad018]
  ExternalGeometry = -> [Pad018]
  FullyConstrained = false
  MakeInternals = false
  MapMode = 5
  Placement = pos=(-122,0,8.467e-13) rot=(0.57735,0.57735,0.57735;2.0944rad)
  sketch-geometry (28):
    g0: LineSegment [constr] StartX=349.9 StartY=-203.2 StartZ=0 EndX=339.9 EndY=-203.2 EndZ=0
    g1: LineSegment [constr] StartX=339.9 StartY=-203.2 StartZ=0 EndX=339.9 EndY=-213.2 EndZ=0
    g2: LineSegment [constr] StartX=339.9 StartY=-213.2 StartZ=0 EndX=349.9 EndY=-213.2 EndZ=0
    g3: LineSegment [constr] StartX=349.9 StartY=-213.2 StartZ=0 EndX=349.9 EndY=-203.2 EndZ=0
    g4: LineSegment [constr] StartX=1.9 StartY=-203.2 StartZ=0 EndX=1.9 EndY=-213.2 EndZ=0
    g5: LineSegment [constr] StartX=1.9 StartY=-213.2 StartZ=0 EndX=11.9 EndY=-213.2 EndZ=0
    g6: LineSegment [constr] StartX=11.9 StartY=-213.2 StartZ=0 EndX=11.9 EndY=-203.2 EndZ=0
    g7: LineSegment [constr] StartX=11.9 StartY=-203.2 StartZ=0 EndX=1.9 EndY=-203.2 EndZ=0
    g8: LineSegment [constr] StartX=11.9 StartY=-213.2 StartZ=0 EndX=339.9 EndY=-213.2 EndZ=0
    g9: LineSegment [constr] StartX=175.9 StartY=-213.2 StartZ=0 EndX=185.9 EndY=-213.2 EndZ=0
    g10: LineSegment [constr] StartX=185.9 StartY=-213.2 StartZ=0 EndX=185.9 EndY=-203.2 EndZ=0
    g11: LineSegment [constr] StartX=185.9 StartY=-203.2 StartZ=0 EndX=175.9 EndY=-203.2 EndZ=0
    g12: LineSegment [constr] StartX=175.9 StartY=-203.2 StartZ=0 EndX=175.9 EndY=-213.2 EndZ=0
    g13: LineSegment [constr] StartX=175.9 StartY=-203.2 StartZ=0 EndX=339.9 EndY=-203.2 EndZ=0
    g14: LineSegment [constr] StartX=175.9 StartY=-203.2 StartZ=0 EndX=11.9 EndY=-203.2 EndZ=0
    g15: LineSegment [constr] StartX=257.9 StartY=-203.2 StartZ=0 EndX=257.9 EndY=-213.2 EndZ=0
    g16: LineSegment [constr] StartX=257.9 StartY=-213.2 StartZ=0 EndX=267.9 EndY=-213.2 EndZ=0
    g17: LineSegment [constr] StartX=267.9 StartY=-213.2 StartZ=0 EndX=267.9 EndY=-203.2 EndZ=0
    g18: LineSegment [constr] StartX=267.9 StartY=-203.2 StartZ=0 EndX=257.9 EndY=-203.2 EndZ=0
    g19: LineSegment [constr] StartX=93.9 StartY=-203.2 StartZ=0 EndX=83.9 EndY=-203.2 EndZ=0
    g20: LineSegment [constr] StartX=83.9 StartY=-203.2 StartZ=0 EndX=83.9 EndY=-213.2 EndZ=0
    g21: LineSegment [constr] StartX=83.9 StartY=-213.2 StartZ=0 EndX=93.9 EndY=-213.2 EndZ=0
    g22: LineSegment [constr] StartX=93.9 StartY=-213.2 StartZ=0 EndX=93.9 EndY=-203.2 EndZ=0
    g23: Circle CenterX=257.9 CenterY=-213.2 CenterZ=0 NormalX=0 NormalY=0 NormalZ=1 AngleXU=0 Radius=1.5
    g24: Circle CenterX=339.9 CenterY=-213.2 CenterZ=0 NormalX=0 NormalY=0 NormalZ=1 AngleXU=0 Radius=1.5
    g25: Circle CenterX=175.9 CenterY=-213.2 CenterZ=0 NormalX=0 NormalY=0 NormalZ=1 AngleXU=0 Radius=1.5
    g26: Circle CenterX=93.9 CenterY=-213.2 CenterZ=0 NormalX=0 NormalY=0 NormalZ=1 AngleXU=0 Radius=1.5
    g27: Circle CenterX=11.9 CenterY=-213.2 CenterZ=0 NormalX=0 NormalY=0 NormalZ=1 AngleXU=0 Radius=1.5
  constraints (60):
    c: Coincident(g0,g1)
    c: Coincident(g1,g2)
    c: Coincident(g2,g3)
    c: Coincident(g3,g0)
    c: Horizontal(g0)
    c: Horizontal(g2)
    c: Vertical(g1)
    c: Vertical(g3)
    c: Distance(g1,g3) = 10
    c: Distance(g0,g2) = 10
    c: Coincident(g0,g-4)
    c: Coincident(g4,g5)
    c: Coincident(g5,g6)
    c: Coincident(g6,g7)
    c: Coincident(g7,g4)
    c: Vertical(g4)
    c: Vertical(g6)
    c: Horizontal(g5)
    c: Horizontal(g7)
    c: Distance(g4,g6) = 10
    c: Distance(g5,g7) = 10
    c: Coincident(g4,g-3)
    c: Coincident(g8,g5)
    c: Coincident(g8,g1)
    c: Coincident(g9,g10)
    c: Coincident(g10,g11)
    c: Coincident(g11,g12)
    c: Coincident(g12,g9)
    c: Horizontal(g9)
    c: Horizontal(g11)
    c: Vertical(g10)
    c: Vertical(g12)
    c: Distance(g10,g12) = 10
    c: Distance(g9,g11) = 10
    c: Symmetric(g8,g8,g9)
    c: Coincident(g13,g11)
    c: Coincident(g13,g0)
    c: Coincident(g14,g11)
    c: Coincident(g14,g6)
    c: Coincident(g15,g16)
    c: Coincident(g16,g17)
    c: Coincident(g17,g18)
    c: Coincident(g18,g15)
    c: Vertical(g15)
    c: Vertical(g17)
    c: Horizontal(g16)
    c: Horizontal(g18)
    c: Distance(g15,g17) = 10
    c: Symmetric(g13,g13,g15)
    c: PointOnObject(g16,g8)
    c: Coincident(g19,g20)
    c: Coincident(g20,g21)
    c: Coincident(g21,g22)
    c: Coincident(g22,g19)
    c: Horizontal(g19)
    c: Horizontal(g21)
    c: Vertical(g20)
    c: Vertical(g22)
    c: Distance(g20,g22) = 10
    c: Symmetric(g14,g14,g19)
FEATURE [PartDesign::Pocket] Pocket044
  BaseFeature = -> Pad018
  Direction = (-1,-1e-16,6.8e-15)
  Length = 5
  Length2 = 5
  Profile = -> Sketch086
  ReferenceAxis = -> Sketch086 [N_Axis]
  Refine = true
  Suppressed = false
  Type = 1
FEATURE [PartDesign::Body] Body011  label="SpHr2"
  AllowCompound = false
  Group = -> [Binder015,Sketch081,Pad037,Sketch082,Pocket041,Sketch083,Pocket042,Sketch084,Pocket043,Sketch085,Pad018,Sketch086,Pocket044]
  Origin = -> Origin012
  Tip = -> Pocket044
FEATURE [Sketcher::SketchObject] Sketch087
  ArcFitTolerance = 1e-06
  AttachmentSupport = -> [Pocket040]
  ExternalGeometry = -> [Binder016]
  FullyConstrained = true
  MakeInternals = false
  MapMode = 5
  Placement = pos=(0,2,0) rot=(-1,0,0;1.5708rad)
  sketch-geometry (3):
    g0: Circle CenterX=-132 CenterY=190 CenterZ=0 NormalX=0 NormalY=0 NormalZ=1 AngleXU=0 Radius=1.5
    g1: Circle CenterX=-200 CenterY=190 CenterZ=0 NormalX=0 NormalY=0 NormalZ=1 AngleXU=0 Radius=1.5
    g2: Circle CenterX=-268 CenterY=190 CenterZ=0 NormalX=0 NormalY=0 NormalZ=1 AngleXU=0 Radius=1.5
  constraints (6):
    c: Coincident(g0,g-5)
    c: Equal(g0,g-5)
    c: Coincident(g1,g-4)
    c: Equal(g1,g-4)
    c: Coincident(g2,g-3)
    c: Equal(g2,g-3)
FEATURE [PartDesign::Pocket] Pocket045
  BaseFeature = -> Pocket040
  Direction = (0,-1,-2e-16)
  Length = 5
  Length2 = 5
  Placement = pos=(0,0,0) rot=(1,0,0;1.5708rad)
  Profile = -> Sketch087
  ReferenceAxis = -> Sketch087 [N_Axis]
  Refine = true
  Suppressed = false
  Type = 0
FEATURE [PartDesign::Body] Body002  label="MainPt1"
  AllowCompound = false
  Group = -> [Sketch052,Pad003,Binder014,Sketch080,Pocket040,Binder016,Sketch087,Pocket045]
  Origin = -> Origin003
  Placement = pos=(0,98.1679,-28.9949) rot=(1,0,0;5.75959rad)
  Tip = -> Pocket045
FEATURE [Sketcher::SketchObject] Sketch088
  ArcFitTolerance = 1e-06
  AttachmentSupport = -> [Pocket016]
  ExternalGeometry = -> [Binder017]
  FullyConstrained = true
  MakeInternals = false
  MapMode = 5
  Placement = pos=(0,0,0) rot=(0.57735,0.57735,-0.57735;2.0944rad)
  sketch-geometry (3):
    g0: Circle CenterX=-130 CenterY=32 CenterZ=0 NormalX=0 NormalY=0 NormalZ=1 AngleXU=0 Radius=1.5
    g1: Circle CenterX=-130 CenterY=100 CenterZ=0 NormalX=0 NormalY=0 NormalZ=1 AngleXU=0 Radius=1.5
    g2: Circle CenterX=-130 CenterY=168 CenterZ=0 NormalX=0 NormalY=0 NormalZ=1 AngleXU=0 Radius=1.5
  constraints (6):
    c: Coincident(g0,g-5)
    c: Equal(g0,g-5)
    c: Coincident(g1,g-4)
    c: Equal(g1,g-4)
    c: Coincident(g2,g-3)
    c: Equal(g2,g-3)
FEATURE [PartDesign::Pocket] Pocket046
  BaseFeature = -> Pocket016
  Direction = (0,1,0)
  Length = 5
  Length2 = 5
  Placement = pos=(0,0,0) rot=(1,1,1;2.0944rad)
  Profile = -> Sketch088
  ReferenceAxis = -> Sketch088 [N_Axis]
  Refine = true
  Suppressed = false
  Type = 0
FEATURE [PartDesign::Body] Body031  label="PzDelantera2"
  AllowCompound = false
  Group = -> [Sketch051,Pad031,Sketch040,Pocket016,Binder017,Sketch088,Pocket046]
  Origin = -> Origin033
  Placement = pos=(-300,-2.1,-343.2) rot=(0,0,1;0rad)
  Tip = -> Pocket046
FEATURE [Sketcher::SketchObject] Sketch089
  ArcFitTolerance = 1e-06
  AttachmentSupport = -> [Binder033]
  ExternalGeometry = -> [Binder033]
  FullyConstrained = true
  MakeInternals = false
  MapMode = 5
  Placement = pos=(-124,0,0) rot=(0.57735,-0.57735,-0.57735;2.0944rad)
  sketch-geometry (5):
    g0: Circle CenterX=-339.9 CenterY=-213.2 CenterZ=0 NormalX=0 NormalY=0 NormalZ=1 AngleXU=0 Radius=1.5
    g1: Circle CenterX=-257.9 CenterY=-213.2 CenterZ=0 NormalX=0 NormalY=0 NormalZ=1 AngleXU=0 Radius=1.5
    g2: Circle CenterX=-175.9 CenterY=-213.2 CenterZ=0 NormalX=0 NormalY=0 NormalZ=1 AngleXU=0 Radius=1.5
    g3: Circle CenterX=-93.9 CenterY=-213.2 CenterZ=0 NormalX=0 NormalY=0 NormalZ=1 AngleXU=0 Radius=1.5
    g4: Circle CenterX=-11.9 CenterY=-213.2 CenterZ=0 NormalX=0 NormalY=0 NormalZ=1 AngleXU=0 Radius=1.5
  constraints (10):
    c: Coincident(g0,g-3)
    c: Equal(g0,g-3)
    c: Coincident(g1,g-4)
    c: Equal(g1,g-4)
    c: Coincident(g2,g-5)
    c: Equal(g2,g-5)
    c: Coincident(g3,g-6)
    c: Equal(g3,g-6)
    c: Coincident(g4,g-7)
    c: Equal(g4,g-7)
FEATURE [PartDesign::Pocket] Pocket047
  BaseFeature = -> Pocket039
  Direction = (1,0,0)
  Length = 5
  Length2 = 5
  Profile = -> Sketch089
  ReferenceAxis = -> Sketch089 [N_Axis]
  Refine = true
  Suppressed = false
  Type = 1
FEATURE [PartDesign::Body] Body010  label="SpVr4"
  AllowCompound = false
  Group = -> [Binder013,Sketch068,Pad015,Sketch069,Pocket030,Sketch070,Pad036,Sketch075,Pocket035,Sketch076,Pocket036,Sketch077,Pocket037,Sketch078,Pocket038,Sketch079,Pocket039,Binder033,Sketch089,Pocket047]
  Origin = -> Origin011
  Tip = -> Pocket047
FEATURE [Sketcher::SketchObject] Sketch090
  ArcFitTolerance = 1e-06
  AttachmentSupport = -> [Binder019]
  ExternalGeometry = -> [Binder019]
  FullyConstrained = true
  MakeInternals = false
  MapMode = 5
  Placement = pos=(-276,0,0) rot=(0.57735,0.57735,0.57735;2.0944rad)
  sketch-geometry (5):
    g0: Circle CenterX=339.9 CenterY=-213.2 CenterZ=0 NormalX=0 NormalY=0 NormalZ=1 AngleXU=0 Radius=1.5
    g1: Circle CenterX=257.9 CenterY=-213.2 CenterZ=0 NormalX=0 NormalY=0 NormalZ=1 AngleXU=0 Radius=1.5
    g2: Circle CenterX=175.9 CenterY=-213.2 CenterZ=0 NormalX=0 NormalY=0 NormalZ=1 AngleXU=0 Radius=1.5
    g3: Circle CenterX=93.9 CenterY=-213.2 CenterZ=0 NormalX=0 NormalY=0 NormalZ=1 AngleXU=0 Radius=1.5
    g4: Circle CenterX=11.9 CenterY=-213.2 CenterZ=0 NormalX=0 NormalY=0 NormalZ=1 AngleXU=0 Radius=1.5
  constraints (10):
    c: Coincident(g0,g-7)
    c: Equal(g0,g-7)
    c: Coincident(g1,g-6)
    c: Equal(g1,g-6)
    c: Coincident(g2,g-5)
    c: Equal(g2,g-5)
    c: Coincident(g3,g-4)
    c: Equal(g3,g-4)
    c: Coincident(g4,g-3)
    c: Equal(g4,g-3)
FEATURE [PartDesign::Pocket] Pocket048
  BaseFeature = -> Pocket034
  Direction = (-1,0,0)
  Length = 5
  Length2 = 5
  Profile = -> Sketch090
  ReferenceAxis = -> Sketch090 [N_Axis]
  Refine = true
  Suppressed = false
  Type = 0
FEATURE [PartDesign::Body] Body009  label="SpVr3"
  AllowCompound = false
  Group = -> [Binder012,Sketch065,Pad013,Sketch066,Pocket029,Sketch067,Pad035,Sketch071,Pocket031,Sketch072,Pocket032,Sketch073,Pocket033,Sketch074,Pocket034,Binder019,Sketch090,Pocket048]
  Origin = -> Origin010
  Tip = -> Pocket048
FEATURE [App::DocumentObjectGroup] Group013  label="LEFT"
  Group = -> [Body031,Body002,Body032,Body009,Body010,Body011]
FEATURE [Sketcher::SketchObject] Sketch091
  ArcFitTolerance = 1e-06
  AttachmentSupport = -> [Pad034]
  ExternalGeometry = -> [Pad034]
  FullyConstrained = false
  MakeInternals = false
  MapMode = 5
  Placement = pos=(0,87.9131,-50.7566) rot=(1,0,0;1.0472rad)
  sketch-geometry (28):
    g0: LineSegment [constr] StartX=627 StartY=-176.026 StartZ=0 EndX=637 EndY=-176.026 EndZ=0
    g1: LineSegment [constr] StartX=637 StartY=-176.026 StartZ=0 EndX=637 EndY=-166.026 EndZ=0
    g2: LineSegment [constr] StartX=637 StartY=-166.026 StartZ=0 EndX=627 EndY=-166.026 EndZ=0
    g3: LineSegment [constr] StartX=627 StartY=-166.026 StartZ=0 EndX=627 EndY=-176.026 EndZ=0
    g4: LineSegment [constr] StartX=878 StartY=-176.026 StartZ=0 EndX=878 EndY=-166.026 EndZ=0
    g5: LineSegment [constr] StartX=878 StartY=-166.026 StartZ=0 EndX=868 EndY=-166.026 EndZ=0
    g6: LineSegment [constr] StartX=868 StartY=-166.026 StartZ=0 EndX=868 EndY=-176.026 EndZ=0
    g7: LineSegment [constr] StartX=868 StartY=-176.026 StartZ=0 EndX=878 EndY=-176.026 EndZ=0
    g8: LineSegment [constr] StartX=868 StartY=-176.026 StartZ=0 EndX=637 EndY=-176.026 EndZ=0
    g9: LineSegment [constr] StartX=752.5 StartY=-176.026 StartZ=0 EndX=762.5 EndY=-176.026 EndZ=0
    g10: LineSegment [constr] StartX=762.5 StartY=-176.026 StartZ=0 EndX=762.5 EndY=-166.026 EndZ=0
    g11: LineSegment [constr] StartX=762.5 StartY=-166.026 StartZ=0 EndX=752.5 EndY=-166.026 EndZ=0
    g12: LineSegment [constr] StartX=752.5 StartY=-166.026 StartZ=0 EndX=752.5 EndY=-176.026 EndZ=0
    g13: LineSegment [constr] StartX=752.5 StartY=-166.026 StartZ=0 EndX=868 EndY=-166.026 EndZ=0
    g14: LineSegment [constr] StartX=752.5 StartY=-166.026 StartZ=0 EndX=637 EndY=-166.026 EndZ=0
    g15: LineSegment [constr] StartX=810.25 StartY=-166.026 StartZ=0 EndX=810.25 EndY=-176.026 EndZ=0
    g16: LineSegment [constr] StartX=810.25 StartY=-176.026 StartZ=0 EndX=820.25 EndY=-176.026 EndZ=0
    g17: LineSegment [constr] StartX=820.25 StartY=-176.026 StartZ=0 EndX=820.25 EndY=-166.026 EndZ=0
    g18: LineSegment [constr] StartX=820.25 StartY=-166.026 StartZ=0 EndX=810.25 EndY=-166.026 EndZ=0
    g19: LineSegment [constr] StartX=694.75 StartY=-166.026 StartZ=0 EndX=694.75 EndY=-176.026 EndZ=0
    g20: LineSegment [constr] StartX=694.75 StartY=-176.026 StartZ=0 EndX=704.75 EndY=-176.026 EndZ=0
    g21: LineSegment [constr] StartX=704.75 StartY=-176.026 StartZ=0 EndX=704.75 EndY=-166.026 EndZ=0
    g22: LineSegment [constr] StartX=704.75 StartY=-166.026 StartZ=0 EndX=694.75 EndY=-166.026 EndZ=0
    g23: Circle CenterX=868 CenterY=-166.026 CenterZ=0 NormalX=0 NormalY=0 NormalZ=1 AngleXU=0 Radius=1.5
    g24: Circle CenterX=810.25 CenterY=-166.026 CenterZ=0 NormalX=0 NormalY=0 NormalZ=1 AngleXU=0 Radius=1.5
    g25: Circle CenterX=752.5 CenterY=-166.026 CenterZ=0 NormalX=0 NormalY=0 NormalZ=1 AngleXU=0 Radius=1.5
    g26: Circle CenterX=694.75 CenterY=-166.026 CenterZ=0 NormalX=0 NormalY=0 NormalZ=1 AngleXU=0 Radius=1.5
    g27: Circle CenterX=637 CenterY=-166.026 CenterZ=0 NormalX=0 NormalY=0 NormalZ=1 AngleXU=0 Radius=1.5
  constraints (62):
    c: Coincident(g0,g1)
    c: Coincident(g1,g2)
    c: Coincident(g2,g3)
    c: Coincident(g3,g0)
    c: Horizontal(g0)
    c: Horizontal(g2)
    c: Vertical(g1)
    c: Vertical(g3)
    c: Distance(g1,g3) = 10
    c: Distance(g0,g2) = 10
    c: Coincident(g0,g-3)
    c: Coincident(g4,g5)
    c: Coincident(g5,g6)
    c: Coincident(g6,g7)
    c: Coincident(g7,g4)
    c: Vertical(g4)
    c: Vertical(g6)
    c: Horizontal(g5)
    c: Horizontal(g7)
    c: Distance(g4,g6) = 10
    c: Distance(g5,g7) = 10
    c: Coincident(g4,g-4)
    c: Coincident(g8,g6)
    c: Coincident(g8,g0)
    c: Coincident(g9,g10)
    c: Coincident(g10,g11)
    c: Coincident(g11,g12)
    c: Coincident(g12,g9)
    c: Horizontal(g9)
    c: Horizontal(g11)
    c: Vertical(g10)
    c: Vertical(g12)
    c: Distance(g10,g12) = 10
    c: Distance(g9,g11) = 10
    c: Symmetric(g8,g8,g9)
    c: Coincident(g13,g11)
    c: Coincident(g13,g5)
    c: Coincident(g14,g11)
    c: Coincident(g14,g1)
    c: Coincident(g15,g16)
    c: Coincident(g16,g17)
    c: Coincident(g17,g18)
    c: Coincident(g18,g15)
    c: Vertical(g15)
    c: Vertical(g17)
    c: Horizontal(g16)
    c: Horizontal(g18)
    c: Distance(g15,g17) = 10
    c: Symmetric(g13,g13,g15)
    c: PointOnObject(g16,g8)
    c: Coincident(g19,g20)
    c: Coincident(g20,g21)
    c: Coincident(g21,g22)
    c: Coincident(g22,g19)
    c: Vertical(g19)
    c: Vertical(g21)
    c: Horizontal(g20)
    c: Horizontal(g22)
    c: Distance(g19,g21) = 10
    c: Symmetric(g14,g14,g19)
    c: PointOnObject(g20,g8)
    c: Coincident(g23,g5)
FEATURE [PartDesign::Pocket] Pocket049
  BaseFeature = -> Pad034
  Direction = (0,0.866026,-0.5)
  Length = 5
  Length2 = 5
  Profile = -> Sketch091
  ReferenceAxis = -> Sketch091 [N_Axis]
  Refine = true
  Suppressed = false
  Type = 0
FEATURE [Sketcher::SketchObject] Sketch092
  ArcFitTolerance = 1e-06
  AttachmentSupport = -> [Pocket049]
  ExternalGeometry = -> [Pocket049]
  FullyConstrained = false
  MakeInternals = false
  MapMode = 5
  Placement = pos=(0,-0.1,0) rot=(1,0,0;1.5708rad)
  sketch-geometry (28):
    g0: LineSegment [constr] StartX=627 StartY=-225.17 StartZ=0 EndX=637 EndY=-225.17 EndZ=0
    g1: LineSegment [constr] StartX=637 StartY=-225.17 StartZ=0 EndX=637 EndY=-215.17 EndZ=0
    g2: LineSegment [constr] StartX=637 StartY=-215.17 StartZ=0 EndX=627 EndY=-215.17 EndZ=0
    g3: LineSegment [constr] StartX=627 StartY=-215.17 StartZ=0 EndX=627 EndY=-225.17 EndZ=0
    g4: LineSegment [constr] StartX=878 StartY=-225.17 StartZ=0 EndX=878 EndY=-215.17 EndZ=0
    g5: LineSegment [constr] StartX=878 StartY=-215.17 StartZ=0 EndX=868 EndY=-215.17 EndZ=0
    g6: LineSegment [constr] StartX=868 StartY=-215.17 StartZ=0 EndX=868 EndY=-225.17 EndZ=0
    g7: LineSegment [constr] StartX=868 StartY=-225.17 StartZ=0 EndX=878 EndY=-225.17 EndZ=0
    g8: LineSegment [constr] StartX=637 StartY=-225.17 StartZ=0 EndX=868 EndY=-225.17 EndZ=0
    g9: LineSegment [constr] StartX=752.5 StartY=-225.17 StartZ=0 EndX=762.5 EndY=-225.17 EndZ=0
    g10: LineSegment [constr] StartX=762.5 StartY=-225.17 StartZ=0 EndX=762.5 EndY=-215.17 EndZ=0
    g11: LineSegment [constr] StartX=762.5 StartY=-215.17 StartZ=0 EndX=752.5 EndY=-215.17 EndZ=0
    g12: LineSegment [constr] StartX=752.5 StartY=-215.17 StartZ=0 EndX=752.5 EndY=-225.17 EndZ=0
    g13: LineSegment [constr] StartX=752.5 StartY=-215.17 StartZ=0 EndX=868 EndY=-215.17 EndZ=0
    g14: LineSegment [constr] StartX=752.5 StartY=-215.17 StartZ=0 EndX=637 EndY=-215.17 EndZ=0
    g15: LineSegment [constr] StartX=810.25 StartY=-215.17 StartZ=0 EndX=800.25 EndY=-215.17 EndZ=0
    g16: LineSegment [constr] StartX=800.25 StartY=-215.17 StartZ=0 EndX=800.25 EndY=-225.17 EndZ=0
    g17: LineSegment [constr] StartX=800.25 StartY=-225.17 StartZ=0 EndX=810.25 EndY=-225.17 EndZ=0
    g18: LineSegment [constr] StartX=810.25 StartY=-225.17 StartZ=0 EndX=810.25 EndY=-215.17 EndZ=0
    g19: LineSegment [constr] StartX=694.75 StartY=-215.17 StartZ=0 EndX=684.75 EndY=-215.17 EndZ=0
    g20: LineSegment [constr] StartX=684.75 StartY=-215.17 StartZ=0 EndX=684.75 EndY=-225.17 EndZ=0
    g21: LineSegment [constr] StartX=684.75 StartY=-225.17 StartZ=0 EndX=694.75 EndY=-225.17 EndZ=0
    g22: LineSegment [constr] StartX=694.75 StartY=-225.17 StartZ=0 EndX=694.75 EndY=-215.17 EndZ=0
    g23: Circle CenterX=868 CenterY=-215.17 CenterZ=0 NormalX=0 NormalY=0 NormalZ=1 AngleXU=0 Radius=1.5
    g24: Circle CenterX=810.25 CenterY=-215.17 CenterZ=0 NormalX=0 NormalY=0 NormalZ=1 AngleXU=0 Radius=1.5
    g25: Circle CenterX=752.5 CenterY=-215.17 CenterZ=0 NormalX=0 NormalY=0 NormalZ=1 AngleXU=0 Radius=1.5
    g26: Circle CenterX=694.75 CenterY=-215.17 CenterZ=0 NormalX=0 NormalY=0 NormalZ=1 AngleXU=0 Radius=1.5
    g27: Circle CenterX=637 CenterY=-215.17 CenterZ=0 NormalX=0 NormalY=0 NormalZ=1 AngleXU=0 Radius=1.5
  constraints (60):
    c: Coincident(g0,g1)
    c: Coincident(g1,g2)
    c: Coincident(g2,g3)
    c: Coincident(g3,g0)
    c: Horizontal(g0)
    c: Horizontal(g2)
    c: Vertical(g1)
    c: Vertical(g3)
    c: Distance(g1,g3) = 10
    c: Distance(g0,g2) = 10
    c: Coincident(g0,g-3)
    c: Coincident(g4,g5)
    c: Coincident(g5,g6)
    c: Coincident(g6,g7)
    c: Coincident(g7,g4)
    c: Vertical(g4)
    c: Vertical(g6)
    c: Horizontal(g5)
    c: Horizontal(g7)
    c: Distance(g4,g6) = 10
    c: Distance(g5,g7) = 10
    c: Coincident(g4,g-4)
    c: Coincident(g8,g0)
    c: Coincident(g8,g6)
    c: Coincident(g9,g10)
    c: Coincident(g10,g11)
    c: Coincident(g11,g12)
    c: Coincident(g12,g9)
    c: Horizontal(g9)
    c: Horizontal(g11)
    c: Vertical(g10)
    c: Vertical(g12)
    c: Distance(g10,g12) = 10
    c: Distance(g9,g11) = 10
    c: Symmetric(g8,g8,g9)
    c: Coincident(g13,g11)
    c: Coincident(g13,g5)
    c: Coincident(g14,g11)
    c: Coincident(g14,g1)
    c: Coincident(g15,g16)
    c: Coincident(g16,g17)
    c: Coincident(g17,g18)
    c: Coincident(g18,g15)
    c: Horizontal(g15)
    c: Horizontal(g17)
    c: Vertical(g16)
    c: Vertical(g18)
    c: Distance(g16,g18) = 10
    c: Symmetric(g13,g13,g15)
    c: PointOnObject(g16,g8)
    c: Coincident(g19,g20)
    c: Coincident(g20,g21)
    c: Coincident(g21,g22)
    c: Coincident(g22,g19)
    c: Horizontal(g19)
    c: Horizontal(g21)
    c: Vertical(g20)
    c: Vertical(g22)
    c: Distance(g20,g22) = 10
    c: Symmetric(g14,g14,g19)
FEATURE [PartDesign::Pocket] Pocket050
  BaseFeature = -> Pocket049
  Direction = (0,1,-2e-16)
  Length = 5
  Length2 = 5
  Profile = -> Sketch092
  ReferenceAxis = -> Sketch092 [N_Axis]
  Refine = true
  Suppressed = false
  Type = 0
FEATURE [Sketcher::SketchObject] Sketch093
  ArcFitTolerance = 1e-06
  AttachmentSupport = -> [Pocket050]
  ExternalGeometry = -> [Pocket050]
  FullyConstrained = false
  MakeInternals = false
  MapMode = 5
  Placement = pos=(627,0,0) rot=(0.57735,-0.57735,-0.57735;2.0944rad)
  sketch-geometry (28):
    g0: LineSegment [constr] StartX=-1.91705 StartY=-203.17 StartZ=0 EndX=-11.917 EndY=-203.17 EndZ=0
    g1: LineSegment [constr] StartX=-11.917 StartY=-203.17 StartZ=0 EndX=-11.917 EndY=-213.17 EndZ=0
    g2: LineSegment [constr] StartX=-11.917 StartY=-213.17 StartZ=0 EndX=-1.91705 EndY=-213.17 EndZ=0
    g3: LineSegment [constr] StartX=-1.91705 StartY=-213.17 StartZ=0 EndX=-1.91705 EndY=-203.17 EndZ=0
    g4: LineSegment [constr] StartX=-349.9 StartY=-203.17 StartZ=0 EndX=-349.9 EndY=-213.17 EndZ=0
    g5: LineSegment [constr] StartX=-349.9 StartY=-213.17 StartZ=0 EndX=-339.9 EndY=-213.17 EndZ=0
    g6: LineSegment [constr] StartX=-339.9 StartY=-213.17 StartZ=0 EndX=-339.9 EndY=-203.17 EndZ=0
    g7: LineSegment [constr] StartX=-339.9 StartY=-203.17 StartZ=0 EndX=-349.9 EndY=-203.17 EndZ=0
    g8: LineSegment [constr] StartX=-339.9 StartY=-203.17 StartZ=0 EndX=-11.917 EndY=-203.17 EndZ=0
    g9: LineSegment [constr] StartX=-175.909 StartY=-203.17 StartZ=0 EndX=-175.909 EndY=-213.17 EndZ=0
    g10: LineSegment [constr] StartX=-175.909 StartY=-213.17 StartZ=0 EndX=-165.909 EndY=-213.17 EndZ=0
    g11: LineSegment [constr] StartX=-165.909 StartY=-213.17 StartZ=0 EndX=-165.909 EndY=-203.17 EndZ=0
    g12: LineSegment [constr] StartX=-165.909 StartY=-203.17 StartZ=0 EndX=-175.909 EndY=-203.17 EndZ=0
    g13: LineSegment [constr] StartX=-175.909 StartY=-213.17 StartZ=0 EndX=-339.9 EndY=-213.17 EndZ=0
    g14: LineSegment [constr] StartX=-175.909 StartY=-213.17 StartZ=0 EndX=-11.917 EndY=-213.17 EndZ=0
    g15: LineSegment [constr] StartX=-93.9128 StartY=-213.17 StartZ=0 EndX=-83.9128 EndY=-213.17 EndZ=0
    g16: LineSegment [constr] StartX=-83.9128 StartY=-213.17 StartZ=0 EndX=-83.9128 EndY=-203.17 EndZ=0
    g17: LineSegment [constr] StartX=-83.9128 StartY=-203.17 StartZ=0 EndX=-93.9128 EndY=-203.17 EndZ=0
    g18: LineSegment [constr] StartX=-93.9128 StartY=-203.17 StartZ=0 EndX=-93.9128 EndY=-213.17 EndZ=0
    g19: LineSegment [constr] StartX=-257.904 StartY=-213.17 StartZ=0 EndX=-247.904 EndY=-213.17 EndZ=0
    g20: LineSegment [constr] StartX=-247.904 StartY=-213.17 StartZ=0 EndX=-247.904 EndY=-203.17 EndZ=0
    g21: LineSegment [constr] StartX=-247.904 StartY=-203.17 StartZ=0 EndX=-257.904 EndY=-203.17 EndZ=0
    g22: LineSegment [constr] StartX=-257.904 StartY=-203.17 StartZ=0 EndX=-257.904 EndY=-213.17 EndZ=0
    g23: Circle CenterX=-11.917 CenterY=-213.17 CenterZ=0 NormalX=0 NormalY=0 NormalZ=1 AngleXU=0 Radius=1.5
    g24: Circle CenterX=-93.9128 CenterY=-213.17 CenterZ=0 NormalX=0 NormalY=0 NormalZ=1 AngleXU=0 Radius=1.5
    g25: Circle CenterX=-175.909 CenterY=-213.17 CenterZ=0 NormalX=0 NormalY=0 NormalZ=1 AngleXU=0 Radius=1.5
    g26: Circle CenterX=-257.904 CenterY=-213.17 CenterZ=0 NormalX=0 NormalY=0 NormalZ=1 AngleXU=0 Radius=1.5
    g27: Circle CenterX=-339.9 CenterY=-213.17 CenterZ=0 NormalX=0 NormalY=0 NormalZ=1 AngleXU=0 Radius=1.5
  constraints (61):
    c: Coincident(g0,g1)
    c: Coincident(g1,g2)
    c: Coincident(g2,g3)
    c: Coincident(g3,g0)
    c: Horizontal(g0)
    c: Horizontal(g2)
    c: Vertical(g1)
    c: Vertical(g3)
    c: Distance(g1,g3) = 10
    c: Distance(g0,g2) = 10
    c: Coincident(g0,g-3)
    c: Coincident(g4,g5)
    c: Coincident(g5,g6)
    c: Coincident(g6,g7)
    c: Coincident(g7,g4)
    c: Vertical(g4)
    c: Vertical(g6)
    c: Horizontal(g5)
    c: Horizontal(g7)
    c: Distance(g4,g6) = 10
    c: Distance(g5,g7) = 10
    c: Coincident(g4,g-4)
    c: Coincident(g8,g6)
    c: Coincident(g8,g0)
    c: Coincident(g9,g10)
    c: Coincident(g10,g11)
    c: Coincident(g11,g12)
    c: Coincident(g12,g9)
    c: Vertical(g9)
    c: Vertical(g11)
    c: Horizontal(g10)
    c: Horizontal(g12)
    c: Distance(g9,g11) = 10
    c: Distance(g10,g12) = 10
    c: Symmetric(g8,g8,g9)
    c: Coincident(g13,g9)
    c: Coincident(g13,g5)
    c: Coincident(g14,g9)
    c: Coincident(g14,g1)
    c: Coincident(g15,g16)
    c: Coincident(g16,g17)
    c: Coincident(g17,g18)
    c: Coincident(g18,g15)
    c: Horizontal(g15)
    c: Horizontal(g17)
    c: Vertical(g16)
    c: Vertical(g18)
    c: Distance(g16,g18) = 10
    c: Symmetric(g14,g14,g15)
    c: PointOnObject(g16,g8)
    c: Coincident(g19,g20)
    c: Coincident(g20,g21)
    c: Coincident(g21,g22)
    c: Coincident(g22,g19)
    c: Horizontal(g19)
    c: Horizontal(g21)
    c: Vertical(g20)
    c: Vertical(g22)
    c: Distance(g20,g22) = 10
    c: Symmetric(g13,g13,g19)
    c: PointOnObject(g20,g8)
FEATURE [PartDesign::Pocket] Pocket051
  BaseFeature = -> Pocket050
  Direction = (1,0,0)
  Length = 5
  Length2 = 5
  Profile = -> Sketch093
  ReferenceAxis = -> Sketch093 [N_Axis]
  Refine = true
  Suppressed = false
  Type = 1
FEATURE [PartDesign::Body] Body033  label="SpHr1"
  AllowCompound = false
  Group = -> [Binder032,Sketch063,Pad011,Sketch064,Pocket027,Sketch038,Pocket028,Sketch039,Pad034,Sketch091,Pocket049,Sketch092,Pocket050,Sketch093,Pocket051]
  Origin = -> Origin035
  Tip = -> Pocket051
FEATURE [Sketcher::SketchObject] Sketch094
  ArcFitTolerance = 1e-06
  AttachmentSupport = -> [Binder034]
  ExternalGeometry = -> [Binder034]
  FullyConstrained = true
  MakeInternals = false
  MapMode = 5
  Placement = pos=(1156,0,0) rot=(0.57735,-0.57735,-0.57735;2.0944rad)
  sketch-geometry (5):
    g0: Circle CenterX=-7.91705 CenterY=-213.17 CenterZ=0 NormalX=0 NormalY=0 NormalZ=1 AngleXU=0 Radius=1.5
    g1: Circle CenterX=-89.9128 CenterY=-213.17 CenterZ=0 NormalX=0 NormalY=0 NormalZ=1 AngleXU=0 Radius=1.5
    g2: Circle CenterX=-171.909 CenterY=-213.17 CenterZ=0 NormalX=0 NormalY=0 NormalZ=1 AngleXU=0 Radius=1.5
    g3: Circle CenterX=-253.904 CenterY=-213.17 CenterZ=0 NormalX=0 NormalY=0 NormalZ=1 AngleXU=0 Radius=1.5
    g4: Circle CenterX=-335.9 CenterY=-213.17 CenterZ=0 NormalX=0 NormalY=0 NormalZ=1 AngleXU=0 Radius=1.5
  constraints (10):
    c: Coincident(g0,g-7)
    c: Equal(g0,g-7)
    c: Coincident(g1,g-6)
    c: Equal(g1,g-6)
    c: Coincident(g2,g-5)
    c: Equal(g2,g-5)
    c: Coincident(g3,g-4)
    c: Equal(g3,g-4)
    c: Coincident(g4,g-3)
    c: Equal(g4,g-3)
FEATURE [PartDesign::Pocket] Pocket052
  BaseFeature = -> Pocket013
  Direction = (1,0,0)
  Length = 5
  Length2 = 5
  Profile = -> Sketch094
  ReferenceAxis = -> Sketch094 [N_Axis]
  Refine = true
  Suppressed = false
  Type = 0
FEATURE [PartDesign::Body] Body004  label="SpVr1"
  AllowCompound = false
  Group = -> [Binder004,Sketch020,Pad007,Sketch021,Pocket017,Sketch022,Pad033,Sketch023,Pocket018,Sketch055,Pocket019,Sketch056,Pocket012,Sketch026,Pocket013,Binder034,Sketch094,Pocket052]
  Origin = -> Origin005
  Placement = pos=(-280,4,0) rot=(0,0,1;0rad)
  Tip = -> Pocket052
FEATURE [Sketcher::SketchObject] Sketch095
  ArcFitTolerance = 1e-06
  AttachmentSupport = -> [Binder035]
  ExternalGeometry = -> [Binder035]
  FullyConstrained = true
  MakeInternals = false
  MapMode = 5
  Placement = pos=(629,0,0) rot=(0.57735,0.57735,0.57735;2.0944rad)
  sketch-geometry (5):
    g0: Circle CenterX=339.9 CenterY=-213.17 CenterZ=0 NormalX=0 NormalY=0 NormalZ=1 AngleXU=0 Radius=1.5
    g1: Circle CenterX=257.904 CenterY=-213.17 CenterZ=0 NormalX=0 NormalY=0 NormalZ=1 AngleXU=0 Radius=1.5
    g2: Circle CenterX=175.909 CenterY=-213.17 CenterZ=0 NormalX=0 NormalY=0 NormalZ=1 AngleXU=0 Radius=1.5
    g3: Circle CenterX=93.9128 CenterY=-213.17 CenterZ=0 NormalX=0 NormalY=0 NormalZ=1 AngleXU=0 Radius=1.5
    g4: Circle CenterX=11.917 CenterY=-213.17 CenterZ=0 NormalX=0 NormalY=0 NormalZ=1 AngleXU=0 Radius=1.5
  constraints (10):
    c: Coincident(g0,g-7)
    c: Equal(g0,g-7)
    c: Coincident(g1,g-6)
    c: Equal(g1,g-6)
    c: Coincident(g2,g-5)
    c: Equal(g2,g-5)
    c: Coincident(g3,g-4)
    c: Equal(g3,g-4)
    c: Coincident(g4,g-3)
    c: Equal(g4,g-3)
FEATURE [PartDesign::Pocket] Pocket053
  BaseFeature = -> Pocket026
  Direction = (-1,0,0)
  Length = 5
  Length2 = 5
  Profile = -> Sketch095
  ReferenceAxis = -> Sketch095 [N_Axis]
  Refine = true
  Suppressed = false
  Type = 0
FEATURE [PartDesign::Body] Body007  label="SpVr2"
  AllowCompound = false
  Group = -> [Binder006,Sketch057,Pad009,Sketch058,Pocket021,Sketch059,Pad010,Sketch031,Pocket022,Sketch032,Pocket023,Sketch060,Pocket024,Sketch062,Pocket026,Binder035,Sketch095,Pocket053]
  Origin = -> Origin008
  Tip = -> Pocket053
FEATURE [Sketcher::SketchObject] Sketch096
  ArcFitTolerance = 1e-06
  AttachmentSupport = -> [Binder036]
  ExternalGeometry = -> [Binder036]
  FullyConstrained = true
  MakeInternals = false
  MapMode = 5
  Placement = pos=(0,87.9015,-50.7499) rot=(1,0,0;1.0472rad)
  sketch-geometry (5):
    g0: Circle CenterX=868 CenterY=-166 CenterZ=0 NormalX=0 NormalY=0 NormalZ=1 AngleXU=0 Radius=1.5
    g1: Circle CenterX=810.25 CenterY=-166 CenterZ=0 NormalX=0 NormalY=0 NormalZ=1 AngleXU=0 Radius=1.5
    g2: Circle CenterX=752.5 CenterY=-166 CenterZ=0 NormalX=0 NormalY=0 NormalZ=1 AngleXU=0 Radius=1.5
    g3: Circle CenterX=694.75 CenterY=-166 CenterZ=0 NormalX=0 NormalY=0 NormalZ=1 AngleXU=0 Radius=1.5
    g4: Circle CenterX=637 CenterY=-166 CenterZ=0 NormalX=0 NormalY=0 NormalZ=1 AngleXU=0 Radius=1.5
  constraints (10):
    c: Coincident(g0,g-7)
    c: Equal(g0,g-7)
    c: Coincident(g1,g-6)
    c: Equal(g1,g-6)
    c: Coincident(g2,g-5)
    c: Equal(g2,g-5)
    c: Coincident(g3,g-4)
    c: Equal(g3,g-4)
    c: Coincident(g4,g-3)
    c: Equal(g4,g-3)
FEATURE [PartDesign::Pocket] Pocket054
  BaseFeature = -> Pocket025
  Direction = (0,0.866026,-0.5)
  Length = 5
  Length2 = 5
  Profile = -> Sketch096
  ReferenceAxis = -> Sketch096 [N_Axis]
  Refine = true
  Reversed = true
  Suppressed = false
  Type = 0
FEATURE [PartDesign::Body] Body003  label="MainPt2"
  AllowCompound = false
  Group = -> [Binder029,Sketch012,Pad004,Binder030,Sketch027,Pocket020,Binder031,Sketch061,Pocket025,Binder036,Sketch096,Pocket054]
  Origin = -> Origin004
  Placement = pos=(0,-0.00157848,-0.0295289) rot=(0,0,1;0rad)
  Tip = -> Pocket054
FEATURE [Sketcher::SketchObject] Sketch097
  ArcFitTolerance = 1e-06
  AttachmentSupport = -> [Binder037]
  ExternalGeometry = -> [Binder037]
  FullyConstrained = true
  MakeInternals = false
  MapMode = 5
  Placement = pos=(0,4,0) rot=(0,0.707107,0.707107;3.14159rad)
  sketch-geometry (5):
    g0: Circle CenterX=-32 CenterY=128.03 CenterZ=0 NormalX=0 NormalY=0 NormalZ=1 AngleXU=0 Radius=1.5
    g1: Circle CenterX=-89.75 CenterY=128.03 CenterZ=0 NormalX=0 NormalY=0 NormalZ=1 AngleXU=0 Radius=1.5
    g2: Circle CenterX=-147.5 CenterY=128.03 CenterZ=0 NormalX=0 NormalY=0 NormalZ=1 AngleXU=0 Radius=1.5
    g3: Circle CenterX=-205.25 CenterY=128.03 CenterZ=0 NormalX=0 NormalY=0 NormalZ=1 AngleXU=0 Radius=1.5
    g4: Circle CenterX=-263 CenterY=128.03 CenterZ=0 NormalX=0 NormalY=0 NormalZ=1 AngleXU=0 Radius=1.5
  constraints (10):
    c: Coincident(g0,g-7)
    c: Equal(g0,g-7)
    c: Coincident(g1,g-6)
    c: Equal(g1,g-6)
    c: Coincident(g2,g-5)
    c: Equal(g2,g-5)
    c: Coincident(g3,g-4)
    c: Equal(g3,g-4)
    c: Coincident(g4,g-3)
    c: Equal(g4,g-3)
FEATURE [PartDesign::Pocket] Pocket055
  BaseFeature = -> Pocket008
  Direction = (0,-1,2e-16)
  Length = 5
  Length2 = 5
  Placement = pos=(0,0,0) rot=(1,1,1;2.0944rad)
  Profile = -> Sketch097
  ReferenceAxis = -> Sketch097 [N_Axis]
  Refine = true
  Suppressed = false
  Type = 0
FEATURE [PartDesign::Body] Body001  label="PzDelantera"
  AllowCompound = false
  Group = -> [Sketch005,Pad002,Sketch019,Pocket008,Binder037,Sketch097,Pocket055]
  Origin = -> Origin002
  Placement = pos=(605,-2.1,-343.2) rot=(0,0,1;0rad)
  Tip = -> Pocket055
FEATURE [App::DocumentObjectGroup] Group012  label="RIGHT"
  Group = -> [Body006,Body003,Body001,Body004,Body007,Body033]
FEATURE [App::Part] Part001  label="Recubrimiento"
  Group = -> [Body001,Body006,Body003,Body004,Group012,Body002,Body031,Body032,Group013,Body007,Body033,Body009,Body010,Body011,Group014]
  Origin = -> Origin032
  Placement = pos=(1463.99,900,981.3) rot=(0,0,1;4.71243rad)
FEATURE [PartDesign::SubShapeBinder] Binder039  label="Binder040"
  BindCopyOnChange = 0
  BindMode = 2
  ClaimChildren = false
  Context = -> Part002 [Body035.Binder039.]
  Fuse = false
  MakeFace = true
  OffsetFill = false
  OffsetIntersection = false
  OffsetJoinType = 0
  OffsetOpenResult = false
  PartialLoad = false
  Refine = true
  Relative = true
  _Version = 2
FEATURE [Sketcher::SketchObject] Sketch099
  ArcFitTolerance = 1e-06
  AttachmentSupport = -> [Binder039]
  ExternalGeometry = -> [Binder039]
  FullyConstrained = false
  MakeInternals = false
  MapMode = 5
  Placement = pos=(0,-38.1,0) rot=(1,0,0;1.5708rad)
  sketch-geometry (37):
    g0: LineSegment [constr] StartX=538.071 StartY=1038.1 StartZ=0 EndX=999.985 EndY=1038.1 EndZ=0
    g1: LineSegment [constr] StartX=999.985 StartY=2038.1 StartZ=0 EndX=999.985 EndY=1038.1 EndZ=0
    g2: LineSegment [constr] StartX=538.071 StartY=1038.1 StartZ=0 EndX=499.971 EndY=1038.1 EndZ=0
    g3: LineSegment [constr] StartX=999.985 StartY=2038.1 StartZ=0 EndX=999.985 EndY=2076.2 EndZ=0
    g4: LineSegment StartX=999.985 StartY=1038.1 StartZ=0 EndX=999.985 EndY=2076.2 EndZ=0
    g5: LineSegment StartX=999.985 StartY=2076.2 StartZ=0 EndX=499.971 EndY=2076.2 EndZ=0
    g6: LineSegment StartX=499.971 StartY=2076.2 StartZ=0 EndX=499.971 EndY=1038.1 EndZ=0
    g7: LineSegment StartX=499.971 StartY=1038.1 StartZ=0 EndX=999.985 EndY=1038.1 EndZ=0
    g8: LineSegment [constr] StartX=999.985 StartY=1038.1 StartZ=0 EndX=980.935 EndY=1057.15 EndZ=0
    g9: Circle CenterX=988.253 CenterY=1047.62 CenterZ=0 NormalX=0 NormalY=0 NormalZ=1 AngleXU=0 Radius=5
    g10: LineSegment [constr] StartX=749.978 StartY=2076.2 StartZ=0 EndX=749.978 EndY=1057.15 EndZ=0
    g11: Circle CenterX=509.496 CenterY=1047.63 CenterZ=0 NormalX=0 NormalY=0 NormalZ=1 AngleXU=0 Radius=5
    g12: LineSegment [constr] StartX=499.971 StartY=1557.15 StartZ=0 EndX=999.985 EndY=1557.15 EndZ=0
    g13: LineSegment [constr] StartX=509.496 StartY=1047.63 StartZ=0 EndX=990.46 EndY=1047.63 EndZ=0
    g14: LineSegment [constr] StartX=749.978 StartY=1047.63 StartZ=0 EndX=749.978 EndY=1038.1 EndZ=0
    g15: LineSegment [constr] StartX=990.46 StartY=1047.63 StartZ=0 EndX=990.46 EndY=1038.1 EndZ=0
    g16: LineSegment [constr] StartX=990.46 StartY=1042.86 StartZ=0 EndX=749.978 EndY=1043.57 EndZ=0
    g17: LineSegment [constr] StartX=509.496 StartY=1047.63 StartZ=0 EndX=509.496 EndY=1038.1 EndZ=0
    g18: LineSegment [constr] StartX=749.978 StartY=1043.57 StartZ=0 EndX=509.496 EndY=1043.57 EndZ=0
    g19: LineSegment [constr] StartX=870.219 StartY=1043.22 StartZ=0 EndX=870.219 EndY=1047.62 EndZ=0
    g20: LineSegment [constr] StartX=629.737 StartY=1043.57 StartZ=0 EndX=629.737 EndY=1047.62 EndZ=0
    g21: Circle CenterX=749.978 CenterY=1047.63 CenterZ=0 NormalX=0 NormalY=0 NormalZ=1 AngleXU=0 Radius=5
    g22: Circle CenterX=870.219 CenterY=1047.62 CenterZ=0 NormalX=0 NormalY=0 NormalZ=1 AngleXU=0 Radius=5
    g23: Circle CenterX=629.737 CenterY=1047.62 CenterZ=0 NormalX=0 NormalY=0 NormalZ=1 AngleXU=0 Radius=5
    g24: LineSegment [constr] StartX=988.253 StartY=1047.62 StartZ=0 EndX=988.253 EndY=1557.15 EndZ=0
    g25: Circle CenterX=988.253 CenterY=1302.39 CenterZ=0 NormalX=0 NormalY=0 NormalZ=1 AngleXU=0 Radius=5
    g26: Circle CenterX=988.253 CenterY=1557.15 CenterZ=0 NormalX=0 NormalY=0 NormalZ=1 AngleXU=0 Radius=5
    g27: Circle CenterX=988.253 CenterY=1557.15 CenterZ=0 NormalX=0 NormalY=0 NormalZ=1 AngleXU=0 Radius=5
    g28: Circle CenterX=988.253 CenterY=2066.67 CenterZ=0 NormalX=0 NormalY=0 NormalZ=1 AngleXU=0 Radius=5
    g29: Circle CenterX=988.253 CenterY=1811.91 CenterZ=0 NormalX=0 NormalY=0 NormalZ=1 AngleXU=0 Radius=5
    g30: Circle CenterX=511.703 CenterY=2066.67 CenterZ=0 NormalX=0 NormalY=0 NormalZ=1 AngleXU=0 Radius=5
    g31: Circle CenterX=511.703 CenterY=1811.91 CenterZ=0 NormalX=0 NormalY=0 NormalZ=1 AngleXU=0 Radius=5
    g32: Circle CenterX=511.703 CenterY=1557.15 CenterZ=0 NormalX=0 NormalY=0 NormalZ=1 AngleXU=0 Radius=5
    g33: Circle CenterX=511.703 CenterY=1302.39 CenterZ=0 NormalX=0 NormalY=0 NormalZ=1 AngleXU=0 Radius=5
    g34: Circle CenterX=629.737 CenterY=2066.67 CenterZ=0 NormalX=0 NormalY=0 NormalZ=1 AngleXU=0 Radius=5
    g35: Circle CenterX=749.978 CenterY=2066.67 CenterZ=0 NormalX=0 NormalY=0 NormalZ=1 AngleXU=0 Radius=5
    g36: Circle CenterX=870.219 CenterY=2066.67 CenterZ=0 NormalX=0 NormalY=0 NormalZ=1 AngleXU=0 Radius=5
  constraints (69):
    c: Symmetric(g-3,g-3,g0)
    c: Horizontal(g0)
    c: Symmetric(g-6,g-6,g1)
    c: Vertical(g1)
    c: Coincident(g1,g0)
    c: Coincident(g2,g0)
    c: Symmetric(g-9,g-9,g2)
    c: Coincident(g3,g1)
    c: Symmetric(g-10,g-10,g3)
    c: Coincident(g4,g5)
    c: Coincident(g5,g6)
    c: Coincident(g6,g7)
    c: Coincident(g7,g4)
    c: Vertical(g4)
    c: Vertical(g6)
    c: Horizontal(g5)
    c: Horizontal(g7)
    c: Coincident(g4,g0)
    c: Coincident(g5,g-10)
    c: Coincident(g8,g0)
    c: Coincident(g8,g-7)
    c: Diameter(g9) = 10
    c: Symmetric(g5,g5,g10)
    c: PointOnObject(g10,g-4)
    c: Vertical(g10)
    c: Diameter(g11) = 10
    c: Symmetric(g6,g6,g12)
    c: Symmetric(g4,g4,g12)
    c: Coincident(g13,g11)
    c: Horizontal(g13)
    c: Symmetric(g13,g13,g14)
    c: Symmetric(g7,g7,g14)
    c: Vertical(g14)
    c: PointOnObject(g15,g7)
    c: Vertical(g15)
    c: Coincident(g17,g11)
    c: PointOnObject(g17,g7)
    c: Vertical(g17)
    c: Horizontal(g18)
    c: PointOnObject(g18,g17)
    c: Symmetric(g16,g16,g19)
    c: PointOnObject(g19,g13)
    c: Vertical(g19)
    c: Symmetric(g18,g18,g20)
    c: PointOnObject(g20,g13)
    c: Vertical(g20)
    c: Coincident(g21,g14)
    c: Coincident(g22,g19)
    c: Coincident(g23,g20)
    c: Diameter(g23) = 10
    c: Diameter(g21) = 10
    c: Diameter(g22) = 10
    c: Coincident(g24,g9)
    c: PointOnObject(g24,g12)
    c: Vertical(g24)
    c: Symmetric(g24,g24,g25)
    c: Coincident(g26,g24)
    c: Diameter(g26) = 10
    c: Diameter(g25) = 10
    c: Diameter(g28) = 10
    c: Diameter(g27) = 10
    c: Diameter(g29) = 10
    c: Diameter(g32) = 10
    c: Diameter(g33) = 10
    c: Diameter(g30) = 10
    c: Diameter(g31) = 10
    c: Diameter(g34) = 10
    c: Diameter(g35) = 10
    c: Diameter(g36) = 10
FEATURE [PartDesign::Pad] Pad039
  Direction = (0,-1,2e-16)
  Length = 5
  Length2 = 10
  Profile = -> Sketch099
  ReferenceAxis = -> Sketch099 [N_Axis]
  Refine = true
  Suppressed = false
  Type = 0
FEATURE [PartDesign::Body] Body035  label="Cuerpo061"
  AllowCompound = false
  Group = -> [Binder039,Sketch099,Pad039]
  Origin = -> Origin038
  Placement = pos=(0,-2.345e-13,-1038.1) rot=(0,0,1;0rad)
  Tip = -> Pad039
FEATURE [PartDesign::SubShapeBinder] Binder043  label="Binder044"
  BindCopyOnChange = 0
  BindMode = 2
  ClaimChildren = false
  Context = -> Body039 [Binder043.]
  Fuse = false
  MakeFace = true
  OffsetFill = false
  OffsetIntersection = false
  OffsetJoinType = 0
  OffsetOpenResult = false
  PartialLoad = false
  Refine = true
  Relative = true
  _Version = 2
FEATURE [Sketcher::SketchObject] Sketch103
  ArcFitTolerance = 1e-06
  AttachmentSupport = -> [Binder043]
  ExternalGeometry = -> [Binder043]
  FullyConstrained = false
  MakeInternals = false
  MapMode = 5
  Placement = pos=(0,0,2076.2) rot=(0,0,1;0rad)
  sketch-geometry (28):
    g0: LineSegment [constr] StartX=1500 StartY=750 StartZ=0 EndX=980.935 EndY=750 EndZ=0
    g1: LineSegment [constr] StartX=999.985 StartY=-38.1 StartZ=0 EndX=999.985 EndY=750 EndZ=0
    g2: LineSegment StartX=999.985 StartY=750 StartZ=0 EndX=999.985 EndY=-38.1 EndZ=0
    g3: LineSegment StartX=999.985 StartY=-38.1 StartZ=0 EndX=1500 EndY=-38.1 EndZ=0
    g4: LineSegment StartX=1500 StartY=-38.1 StartZ=0 EndX=1500 EndY=750 EndZ=0
    g5: LineSegment StartX=1500 StartY=750 StartZ=0 EndX=999.985 EndY=750 EndZ=0
    g6: LineSegment [constr] StartX=1019.04 StartY=730.95 StartZ=0 EndX=999.985 EndY=750 EndZ=0
    g7: LineSegment [constr] StartX=1249.99 StartY=750 StartZ=0 EndX=1249.99 EndY=-38.1 EndZ=0
    g8: LineSegment [constr] StartX=999.985 StartY=355.95 StartZ=0 EndX=1500 EndY=355.95 EndZ=0
    g9: Circle CenterX=1009.51 CenterY=740.475 CenterZ=0 NormalX=0 NormalY=0 NormalZ=1 AngleXU=0 Radius=5
    g10: LineSegment [constr] StartX=1009.51 StartY=740.475 StartZ=0 EndX=1009.51 EndY=355.95 EndZ=0
    g11: Circle CenterX=1009.51 CenterY=355.95 CenterZ=0 NormalX=0 NormalY=0 NormalZ=1 AngleXU=0 Radius=5
    g12: Circle CenterX=1009.51 CenterY=548.212 CenterZ=0 NormalX=0 NormalY=0 NormalZ=1 AngleXU=0 Radius=5
    g13: Circle CenterX=1009.51 CenterY=163.688 CenterZ=0 NormalX=0 NormalY=0 NormalZ=1 AngleXU=0 Radius=5
    g14: Circle CenterX=1009.51 CenterY=-28.575 CenterZ=0 NormalX=0 NormalY=0 NormalZ=1 AngleXU=0 Radius=5
    g15: Circle CenterX=1490.47 CenterY=740.475 CenterZ=0 NormalX=0 NormalY=0 NormalZ=1 AngleXU=0 Radius=5
    g16: Circle CenterX=1490.48 CenterY=355.95 CenterZ=0 NormalX=0 NormalY=0 NormalZ=1 AngleXU=0 Radius=5
    g17: Circle CenterX=1490.48 CenterY=548.212 CenterZ=0 NormalX=0 NormalY=0 NormalZ=1 AngleXU=0 Radius=5
    g18: Circle CenterX=1490.48 CenterY=163.688 CenterZ=0 NormalX=0 NormalY=0 NormalZ=1 AngleXU=0 Radius=5
    g19: Circle CenterX=1490.48 CenterY=-28.575 CenterZ=0 NormalX=0 NormalY=0 NormalZ=1 AngleXU=0 Radius=5
    g20: LineSegment [constr] StartX=1009.51 StartY=740.475 StartZ=0 EndX=1249.99 EndY=740.475 EndZ=0
    g21: LineSegment [constr] StartX=1249.99 StartY=740.475 StartZ=0 EndX=1490.47 EndY=740.475 EndZ=0
    g22: Circle CenterX=1370.23 CenterY=740.475 CenterZ=0 NormalX=0 NormalY=0 NormalZ=1 AngleXU=0 Radius=5
    g23: Circle CenterX=1249.99 CenterY=740.475 CenterZ=0 NormalX=0 NormalY=0 NormalZ=1 AngleXU=0 Radius=5
    g24: Circle CenterX=1129.75 CenterY=740.475 CenterZ=0 NormalX=0 NormalY=0 NormalZ=1 AngleXU=0 Radius=5
    g25: Circle CenterX=1129.75 CenterY=-28.575 CenterZ=0 NormalX=0 NormalY=0 NormalZ=1 AngleXU=0 Radius=5
    g26: Circle CenterX=1249.99 CenterY=-28.575 CenterZ=0 NormalX=0 NormalY=0 NormalZ=1 AngleXU=0 Radius=5
    g27: Circle CenterX=1370.23 CenterY=-28.575 CenterZ=0 NormalX=0 NormalY=0 NormalZ=1 AngleXU=0 Radius=5
  constraints (52):
    c: Symmetric(g-5,g-5,g0)
    c: Symmetric(g-3,g-3,g0)
    c: Symmetric(g-4,g-4,g1)
    c: PointOnObject(g1,g0)
    c: Vertical(g1)
    c: Coincident(g2,g3)
    c: Coincident(g3,g4)
    c: Coincident(g4,g5)
    c: Coincident(g5,g2)
    c: Vertical(g2)
    c: Vertical(g4)
    c: Horizontal(g3)
    c: Horizontal(g5)
    c: Coincident(g2,g1)
    c: Coincident(g3,g-4)
    c: Coincident(g6,g-8)
    c: Coincident(g6,g1)
    c: Symmetric(g5,g5,g7)
    c: Symmetric(g3,g3,g7)
    c: Symmetric(g2,g2,g8)
    c: Symmetric(g4,g4,g8)
    c: Symmetric(g6,g6,g9)
    c: Coincident(g10,g9)
    c: PointOnObject(g10,g8)
    c: Vertical(g10)
    c: Coincident(g11,g10)
    c: Symmetric(g10,g10,g12)
    c: Diameter(g12) = 10
    c: Diameter(g9) = 10
    c: Diameter(g11) = 10
    c: Diameter(g13) = 10
    c: Diameter(g14) = 10
    c: Diameter(g17) = 10
    c: Diameter(g15) = 10
    c: Diameter(g16) = 10
    c: Diameter(g18) = 10
    c: Diameter(g19) = 10
    c: Coincident(g20,g9)
    c: PointOnObject(g20,g7)
    c: Horizontal(g20)
    c: Coincident(g21,g20)
    c: Coincident(g21,g15)
    c: Horizontal(g21)
    c: Symmetric(g21,g21,g22)
    c: Coincident(g23,g20)
    c: Symmetric(g20,g20,g24)
    c: Diameter(g22) = 10
    c: Diameter(g23) = 10
    c: Diameter(g24) = 10
    c: Diameter(g27) = 10
    c: Diameter(g26) = 10
    c: Diameter(g25) = 10
FEATURE [PartDesign::Pad] Pad043
  Direction = (0,0,1)
  Length = 5
  Length2 = 10
  Profile = -> Sketch103
  ReferenceAxis = -> Sketch103 [N_Axis]
  Refine = true
  Suppressed = false
  Type = 0
FEATURE [PartDesign::Body] Body039  label="Cuerpo065"
  AllowCompound = false
  Group = -> [Binder043,Sketch103,Pad043]
  Origin = -> Origin042
  Placement = pos=(-500.015,-7.1e-15,0) rot=(0,0,1;0rad)
  Tip = -> Pad043
FEATURE [PartDesign::SubShapeBinder] Binder044  label="Binder045"
  BindCopyOnChange = 0
  BindMode = 2
  ClaimChildren = false
  Context = -> Body040 [Binder044.]
  Fuse = false
  MakeFace = true
  OffsetFill = false
  OffsetIntersection = false
  OffsetJoinType = 0
  OffsetOpenResult = false
  PartialLoad = false
  Refine = true
  Relative = true
  _Version = 2
FEATURE [Sketcher::SketchObject] Sketch104
  ArcFitTolerance = 1e-06
  AttachmentSupport = -> [Binder044]
  ExternalGeometry = -> [Binder044]
  FullyConstrained = false
  MakeInternals = false
  MapMode = 5
  Placement = pos=(0,0,2076.2) rot=(0,0,1;0rad)
  sketch-geometry (28):
    g0: LineSegment [constr] StartX=1500 StartY=750 StartZ=0 EndX=980.935 EndY=750 EndZ=0
    g1: LineSegment [constr] StartX=999.985 StartY=-38.1 StartZ=0 EndX=999.985 EndY=750 EndZ=0
    g2: LineSegment StartX=999.985 StartY=750 StartZ=0 EndX=999.985 EndY=-38.1 EndZ=0
    g3: LineSegment StartX=999.985 StartY=-38.1 StartZ=0 EndX=1500 EndY=-38.1 EndZ=0
    g4: LineSegment StartX=1500 StartY=-38.1 StartZ=0 EndX=1500 EndY=750 EndZ=0
    g5: LineSegment StartX=1500 StartY=750 StartZ=0 EndX=999.985 EndY=750 EndZ=0
    g6: LineSegment [constr] StartX=1019.04 StartY=730.95 StartZ=0 EndX=999.985 EndY=750 EndZ=0
    g7: LineSegment [constr] StartX=1249.99 StartY=750 StartZ=0 EndX=1249.99 EndY=-38.1 EndZ=0
    g8: LineSegment [constr] StartX=999.985 StartY=355.95 StartZ=0 EndX=1500 EndY=355.95 EndZ=0
    g9: Circle CenterX=1009.51 CenterY=740.475 CenterZ=0 NormalX=0 NormalY=0 NormalZ=1 AngleXU=0 Radius=5
    g10: LineSegment [constr] StartX=1009.51 StartY=740.475 StartZ=0 EndX=1009.51 EndY=355.95 EndZ=0
    g11: Circle CenterX=1009.51 CenterY=355.95 CenterZ=0 NormalX=0 NormalY=0 NormalZ=1 AngleXU=0 Radius=5
    g12: Circle CenterX=1009.51 CenterY=548.212 CenterZ=0 NormalX=0 NormalY=0 NormalZ=1 AngleXU=0 Radius=5
    g13: Circle CenterX=1009.51 CenterY=163.688 CenterZ=0 NormalX=0 NormalY=0 NormalZ=1 AngleXU=0 Radius=5
    g14: Circle CenterX=1009.51 CenterY=-28.575 CenterZ=0 NormalX=0 NormalY=0 NormalZ=1 AngleXU=0 Radius=5
    g15: Circle CenterX=1490.47 CenterY=740.475 CenterZ=0 NormalX=0 NormalY=0 NormalZ=1 AngleXU=0 Radius=5
    g16: Circle CenterX=1490.48 CenterY=355.95 CenterZ=0 NormalX=0 NormalY=0 NormalZ=1 AngleXU=0 Radius=5
    g17: Circle CenterX=1490.48 CenterY=548.212 CenterZ=0 NormalX=0 NormalY=0 NormalZ=1 AngleXU=0 Radius=5
    g18: Circle CenterX=1490.48 CenterY=163.688 CenterZ=0 NormalX=0 NormalY=0 NormalZ=1 AngleXU=0 Radius=5
    g19: Circle CenterX=1490.48 CenterY=-28.575 CenterZ=0 NormalX=0 NormalY=0 NormalZ=1 AngleXU=0 Radius=5
    g20: LineSegment [constr] StartX=1009.51 StartY=740.475 StartZ=0 EndX=1249.99 EndY=740.475 EndZ=0
    g21: LineSegment [constr] StartX=1249.99 StartY=740.475 StartZ=0 EndX=1490.47 EndY=740.475 EndZ=0
    g22: Circle CenterX=1370.23 CenterY=740.475 CenterZ=0 NormalX=0 NormalY=0 NormalZ=1 AngleXU=0 Radius=5
    g23: Circle CenterX=1249.99 CenterY=740.475 CenterZ=0 NormalX=0 NormalY=0 NormalZ=1 AngleXU=0 Radius=5
    g24: Circle CenterX=1129.75 CenterY=740.475 CenterZ=0 NormalX=0 NormalY=0 NormalZ=1 AngleXU=0 Radius=5
    g25: Circle CenterX=1129.75 CenterY=-28.575 CenterZ=0 NormalX=0 NormalY=0 NormalZ=1 AngleXU=0 Radius=5
    g26: Circle CenterX=1249.99 CenterY=-28.575 CenterZ=0 NormalX=0 NormalY=0 NormalZ=1 AngleXU=0 Radius=5
    g27: Circle CenterX=1370.23 CenterY=-28.575 CenterZ=0 NormalX=0 NormalY=0 NormalZ=1 AngleXU=0 Radius=5
  constraints (52):
    c: Symmetric(g-5,g-5,g0)
    c: Symmetric(g-3,g-3,g0)
    c: Symmetric(g-4,g-4,g1)
    c: PointOnObject(g1,g0)
    c: Vertical(g1)
    c: Coincident(g2,g3)
    c: Coincident(g3,g4)
    c: Coincident(g4,g5)
    c: Coincident(g5,g2)
    c: Vertical(g2)
    c: Vertical(g4)
    c: Horizontal(g3)
    c: Horizontal(g5)
    c: Coincident(g2,g1)
    c: Coincident(g3,g-4)
    c: Coincident(g6,g-8)
    c: Coincident(g6,g1)
    c: Symmetric(g5,g5,g7)
    c: Symmetric(g3,g3,g7)
    c: Symmetric(g2,g2,g8)
    c: Symmetric(g4,g4,g8)
    c: Symmetric(g6,g6,g9)
    c: Coincident(g10,g9)
    c: PointOnObject(g10,g8)
    c: Vertical(g10)
    c: Coincident(g11,g10)
    c: Symmetric(g10,g10,g12)
    c: Diameter(g12) = 10
    c: Diameter(g9) = 10
    c: Diameter(g11) = 10
    c: Diameter(g13) = 10
    c: Diameter(g14) = 10
    c: Diameter(g17) = 10
    c: Diameter(g15) = 10
    c: Diameter(g16) = 10
    c: Diameter(g18) = 10
    c: Diameter(g19) = 10
    c: Coincident(g20,g9)
    c: PointOnObject(g20,g7)
    c: Horizontal(g20)
    c: Coincident(g21,g20)
    c: Coincident(g21,g15)
    c: Horizontal(g21)
    c: Symmetric(g21,g21,g22)
    c: Coincident(g23,g20)
    c: Symmetric(g20,g20,g24)
    c: Diameter(g22) = 10
    c: Diameter(g23) = 10
    c: Diameter(g24) = 10
    c: Diameter(g27) = 10
    c: Diameter(g26) = 10
    c: Diameter(g25) = 10
FEATURE [PartDesign::Pad] Pad044
  Direction = (0,0,1)
  Length = 5
  Length2 = 10
  Profile = -> Sketch104
  ReferenceAxis = -> Sketch104 [N_Axis]
  Refine = true
  Suppressed = false
  Type = 0
FEATURE [PartDesign::Body] Body040  label="Cuerpo066"
  AllowCompound = false
  Group = -> [Binder044,Sketch104,Pad044]
  Origin = -> Origin043
  Placement = pos=(-500.015,788.1,0) rot=(0,0,1;0rad)
  Tip = -> Pad044
FEATURE [PartDesign::SubShapeBinder] Binder045  label="Binder046"
  BindCopyOnChange = 0
  BindMode = 2
  ClaimChildren = false
  Context = -> Body041 [Binder045.]
  Fuse = false
  MakeFace = true
  OffsetFill = false
  OffsetIntersection = false
  OffsetJoinType = 0
  OffsetOpenResult = false
  PartialLoad = false
  Refine = true
  Relative = true
  _Version = 2
FEATURE [Sketcher::SketchObject] Sketch105
  ArcFitTolerance = 1e-06
  AttachmentSupport = -> [Binder045]
  ExternalGeometry = -> [Binder045]
  FullyConstrained = false
  MakeInternals = false
  MapMode = 5
  Placement = pos=(0,0,2076.2) rot=(0,0,1;0rad)
  sketch-geometry (36):
    g0: LineSegment [constr] StartX=1500 StartY=750 StartZ=0 EndX=980.935 EndY=750 EndZ=0
    g1: LineSegment [constr] StartX=999.985 StartY=-38.1 StartZ=0 EndX=999.985 EndY=750 EndZ=0
    g2: LineSegment StartX=999.985 StartY=750 StartZ=0 EndX=999.985 EndY=-38.1 EndZ=0
    g3: LineSegment StartX=999.985 StartY=-38.1 StartZ=0 EndX=1480.95 EndY=-38.1 EndZ=0
    g4: LineSegment StartX=1480.95 StartY=750 StartZ=0 EndX=999.985 EndY=750 EndZ=0
    g5: LineSegment [constr] StartX=1019.04 StartY=730.95 StartZ=0 EndX=999.985 EndY=750 EndZ=0
    g6: LineSegment [constr] StartX=1240.47 StartY=750 StartZ=0 EndX=1249.99 EndY=-38.1 EndZ=0
    g7: LineSegment [constr] StartX=999.985 StartY=355.95 StartZ=0 EndX=1490.47 EndY=355.95 EndZ=0
    g8: Circle CenterX=1009.51 CenterY=740.475 CenterZ=0 NormalX=0 NormalY=0 NormalZ=1 AngleXU=0 Radius=5
    g9: LineSegment [constr] StartX=1009.51 StartY=740.475 StartZ=0 EndX=1009.51 EndY=355.95 EndZ=0
    g10: Circle CenterX=1009.51 CenterY=355.95 CenterZ=0 NormalX=0 NormalY=0 NormalZ=1 AngleXU=0 Radius=5
    g11: Circle CenterX=1009.51 CenterY=548.212 CenterZ=0 NormalX=0 NormalY=0 NormalZ=1 AngleXU=0 Radius=5
    g12: Circle CenterX=1009.51 CenterY=163.688 CenterZ=0 NormalX=0 NormalY=0 NormalZ=1 AngleXU=0 Radius=5
    g13: Circle CenterX=1009.51 CenterY=-28.575 CenterZ=0 NormalX=0 NormalY=0 NormalZ=1 AngleXU=0 Radius=5
    g14: LineSegment [constr] StartX=1009.51 StartY=740.475 StartZ=0 EndX=1240.58 EndY=740.475 EndZ=0
    g15: LineSegment [constr] StartX=1240.58 StartY=740.475 StartZ=0 EndX=1491.87 EndY=740.475 EndZ=0
    g16: Circle CenterX=1366.23 CenterY=740.475 CenterZ=0 NormalX=0 NormalY=0 NormalZ=1 AngleXU=0 Radius=5
    g17: Circle CenterX=1240.58 CenterY=740.475 CenterZ=0 NormalX=0 NormalY=0 NormalZ=1 AngleXU=0 Radius=5
    g18: Circle CenterX=1125.05 CenterY=740.475 CenterZ=0 NormalX=0 NormalY=0 NormalZ=1 AngleXU=0 Radius=5
    g19: Circle CenterX=1129.75 CenterY=-28.575 CenterZ=0 NormalX=0 NormalY=0 NormalZ=1 AngleXU=0 Radius=5
    g20: Circle CenterX=1249.99 CenterY=-28.575 CenterZ=0 NormalX=0 NormalY=0 NormalZ=1 AngleXU=0 Radius=5
    g21: Circle CenterX=1370.23 CenterY=-28.575 CenterZ=0 NormalX=0 NormalY=0 NormalZ=1 AngleXU=0 Radius=5
    g22: LineSegment [constr] StartX=1461.9 StartY=730.95 StartZ=0 EndX=1500 EndY=730.95 EndZ=0
    g23: LineSegment [constr] StartX=1480.95 StartY=730.95 StartZ=0 EndX=1480.95 EndY=-38.1 EndZ=0
    g24: LineSegment [constr] StartX=1480.95 StartY=730.95 StartZ=0 EndX=1461.9 EndY=730.95 EndZ=0
    g25: LineSegment [constr] StartX=1461.9 StartY=4.547e-13 StartZ=0 EndX=1461.9 EndY=-38.1 EndZ=0
    g26: LineSegment [constr] StartX=1480.95 StartY=-38.1 StartZ=0 EndX=1461.9 EndY=-38.1 EndZ=0
    g27: LineSegment [constr] StartX=1480.95 StartY=-35.2074 StartZ=0 EndX=1461.9 EndY=-35.2074 EndZ=0
    g28: LineSegment [constr] StartX=1471.42 StartY=-35.2074 StartZ=0 EndX=1471.42 EndY=750 EndZ=0
    g29: Circle CenterX=1471.42 CenterY=740.475 CenterZ=0 NormalX=0 NormalY=0 NormalZ=1 AngleXU=0 Radius=5
    g30: Circle CenterX=1471.42 CenterY=548.212 CenterZ=0 NormalX=0 NormalY=0 NormalZ=1 AngleXU=0 Radius=5
    g31: Circle CenterX=1471.42 CenterY=355.95 CenterZ=0 NormalX=0 NormalY=0 NormalZ=1 AngleXU=0 Radius=5
    g32: Circle CenterX=1471.42 CenterY=163.688 CenterZ=0 NormalX=0 NormalY=0 NormalZ=1 AngleXU=0 Radius=5
    g33: Circle CenterX=1471.42 CenterY=-28.575 CenterZ=0 NormalX=0 NormalY=0 NormalZ=1 AngleXU=0 Radius=5
    g34: LineSegment [constr] StartX=1480.95 StartY=730.95 StartZ=0 EndX=1480.95 EndY=750 EndZ=0
    g35: LineSegment StartX=1480.95 StartY=750 StartZ=0 EndX=1480.95 EndY=-38.1 EndZ=0
  constraints (71):
    c: Symmetric(g-5,g-5,g0)
    c: Symmetric(g-3,g-3,g0)
    c: Symmetric(g-4,g-4,g1)
    c: PointOnObject(g1,g0)
    c: Vertical(g1)
    c: Coincident(g2,g3)
    c: Coincident(g4,g2)
    c: Vertical(g2)
    c: Horizontal(g3)
    c: Horizontal(g4)
    c: Coincident(g2,g1)
    c: Coincident(g5,g-8)
    c: Coincident(g5,g1)
    c: Symmetric(g4,g4,g6)
    c: Symmetric(g2,g2,g7)
    c: Symmetric(g5,g5,g8)
    c: Coincident(g9,g8)
    c: PointOnObject(g9,g7)
    c: Vertical(g9)
    c: Coincident(g10,g9)
    c: Symmetric(g9,g9,g11)
    c: Diameter(g11) = 10
    c: Diameter(g8) = 10
    c: Diameter(g10) = 10
    c: Diameter(g12) = 10
    c: Diameter(g13) = 10
    c: Coincident(g14,g8)
    c: PointOnObject(g14,g6)
    c: Horizontal(g14)
    c: Coincident(g15,g14)
    c: Horizontal(g15)
    c: Symmetric(g15,g15,g16)
    c: Coincident(g17,g14)
    c: Symmetric(g14,g14,g18)
    c: Diameter(g16) = 10
    c: Diameter(g17) = 10
    c: Diameter(g18) = 10
    c: Diameter(g21) = 10
    c: Diameter(g20) = 10
    c: Diameter(g19) = 10
    c: Coincident(g22,g-9)
    c: Horizontal(g22)
    c: Symmetric(g22,g22,g23)
    c: PointOnObject(g23,g3)
    c: Vertical(g23)
    c: Coincident(g24,g23)
    c: Coincident(g24,g22)
    c: Coincident(g25,g-12)
    c: Vertical(g25)
    c: Coincident(g26,g23)
    c: PointOnObject(g26,g25)
    c: Horizontal(g26)
    c: PointOnObject(g25,g3)
    c: PointOnObject(g27,g23)
    c: PointOnObject(g27,g25)
    c: Horizontal(g27)
    c: Symmetric(g27,g27,g28)
    c: PointOnObject(g28,g4)
    c: Vertical(g28)
    c: Diameter(g30) = 10
    c: Diameter(g29) = 10
    c: Diameter(g31) = 10
    c: Diameter(g32) = 10
    c: Diameter(g33) = 10
    c: Coincident(g34,g23)
    c: Vertical(g34)
    c: PointOnObject(g22,g-5)
    c: Coincident(g4,g34)
    c: Coincident(g35,g4)
    c: Coincident(g35,g23)
    c: PointOnObject(g3,g35)
FEATURE [PartDesign::Pad] Pad045
  Direction = (0,0,1)
  Length = 5
  Length2 = 10
  Profile = -> Sketch105
  ReferenceAxis = -> Sketch105 [N_Axis]
  Refine = true
  Suppressed = false
  Type = 0
FEATURE [PartDesign::Body] Body041  label="Cuerpo067"
  AllowCompound = false
  Group = -> [Binder045,Sketch105,Pad045]
  Origin = -> Origin044
  Placement = pos=(0,788.1,0) rot=(0,0,1;0rad)
  Tip = -> Pad045
FEATURE [PartDesign::SubShapeBinder] Binder046  label="Binder047"
  BindCopyOnChange = 0
  BindMode = 2
  ClaimChildren = false
  Context = -> Body042 [Binder046.]
  Fuse = false
  MakeFace = true
  OffsetFill = false
  OffsetIntersection = false
  OffsetJoinType = 0
  OffsetOpenResult = false
  PartialLoad = false
  Refine = true
  Relative = true
  _Version = 2
FEATURE [PartDesign::SubShapeBinder] Binder047  label="Binder048"
  BindCopyOnChange = 0
  BindMode = 2
  ClaimChildren = false
  Context = -> Body042 [Binder047.]
  Fuse = false
  MakeFace = true
  OffsetFill = false
  OffsetIntersection = false
  OffsetJoinType = 0
  OffsetOpenResult = false
  PartialLoad = false
  Refine = true
  Relative = true
  _Version = 2
FEATURE [Sketcher::SketchObject] Sketch106
  ArcFitTolerance = 1e-06
  AttachmentSupport = -> [Binder046]
  ExternalGeometry = -> [Binder047,Binder046]
  FullyConstrained = false
  MakeInternals = false
  MapMode = 5
  Placement = pos=(0,-38.1,8.4e-15) rot=(1,0,0;1.5708rad)
  sketch-geometry (31):
    g0: LineSegment [constr] StartX=1500 StartY=38.1 StartZ=0 EndX=1500 EndY=7.461e-13 EndZ=0
    g1: LineSegment [constr] StartX=1500 StartY=38.1 StartZ=0 EndX=1461.9 EndY=38.1 EndZ=0
    g2: LineSegment [constr] StartX=1480.95 StartY=38.1 StartZ=0 EndX=1480.95 EndY=6.821e-13 EndZ=0
    g3: LineSegment [constr] StartX=1480.95 StartY=38.1 StartZ=0 EndX=1480.95 EndY=1038.1 EndZ=0
    g4: LineSegment StartX=999.985 StartY=1038.1 StartZ=0 EndX=999.985 EndY=6.821e-13 EndZ=0
    g5: LineSegment StartX=999.985 StartY=6.821e-13 StartZ=0 EndX=1480.95 EndY=6.821e-13 EndZ=0
    g6: LineSegment StartX=1480.95 StartY=6.821e-13 StartZ=0 EndX=1480.95 EndY=1038.1 EndZ=0
    g7: LineSegment StartX=1480.95 StartY=1038.1 StartZ=0 EndX=999.985 EndY=1038.1 EndZ=0
    g8: LineSegment [constr] StartX=1019.04 StartY=1019.05 StartZ=0 EndX=999.985 EndY=1038.1 EndZ=0
    g9: LineSegment [constr] StartX=1461.9 StartY=1019.05 StartZ=0 EndX=1480.95 EndY=1038.1 EndZ=0
    g10: LineSegment [constr] StartX=1240.47 StartY=1038.1 StartZ=0 EndX=1240.47 EndY=6.821e-13 EndZ=0
    g11: LineSegment [constr] StartX=999.985 StartY=519.05 StartZ=0 EndX=1480.95 EndY=519.05 EndZ=0
    g12: LineSegment [constr] StartX=1009.51 StartY=1028.57 StartZ=0 EndX=1009.51 EndY=519.05 EndZ=0
    g13: Circle CenterX=1009.51 CenterY=1028.57 CenterZ=0 NormalX=0 NormalY=0 NormalZ=1 AngleXU=0 Radius=5
    g14: Circle CenterX=1009.51 CenterY=773.812 CenterZ=0 NormalX=0 NormalY=0 NormalZ=1 AngleXU=0 Radius=5
    g15: Circle CenterX=1009.51 CenterY=519.05 CenterZ=0 NormalX=0 NormalY=0 NormalZ=1 AngleXU=0 Radius=5
    g16: Circle CenterX=1009.51 CenterY=264.288 CenterZ=0 NormalX=0 NormalY=0 NormalZ=1 AngleXU=0 Radius=5
    g17: Circle CenterX=1009.51 CenterY=9.525 CenterZ=0 NormalX=0 NormalY=0 NormalZ=1 AngleXU=0 Radius=5
    g18: Circle CenterX=1471.42 CenterY=1028.58 CenterZ=0 NormalX=0 NormalY=0 NormalZ=1 AngleXU=0 Radius=5
    g19: Circle CenterX=1471.43 CenterY=773.812 CenterZ=0 NormalX=0 NormalY=0 NormalZ=1 AngleXU=0 Radius=5
    g20: Circle CenterX=1471.43 CenterY=519.05 CenterZ=0 NormalX=0 NormalY=0 NormalZ=1 AngleXU=0 Radius=5
    g21: Circle CenterX=1471.43 CenterY=264.288 CenterZ=0 NormalX=0 NormalY=0 NormalZ=1 AngleXU=0 Radius=5
    g22: Circle CenterX=1471.43 CenterY=9.525 CenterZ=0 NormalX=0 NormalY=0 NormalZ=1 AngleXU=0 Radius=5
    g23: LineSegment [constr] StartX=1471.42 StartY=1028.58 StartZ=0 EndX=1240.47 EndY=1028.58 EndZ=0
    g24: LineSegment [constr] StartX=1240.47 StartY=1028.57 StartZ=0 EndX=1009.51 EndY=1028.57 EndZ=0
    g25: Circle CenterX=1240.47 CenterY=1028.58 CenterZ=0 NormalX=0 NormalY=0 NormalZ=1 AngleXU=0 Radius=5
    g26: Circle CenterX=1355.95 CenterY=1028.58 CenterZ=0 NormalX=0 NormalY=0 NormalZ=1 AngleXU=0 Radius=5
    g27: Circle CenterX=1124.99 CenterY=1028.57 CenterZ=0 NormalX=0 NormalY=0 NormalZ=1 AngleXU=0 Radius=5
    g28: Circle CenterX=1355.95 CenterY=9.525 CenterZ=0 NormalX=0 NormalY=0 NormalZ=1 AngleXU=0 Radius=5
    g29: Circle CenterX=1240.47 CenterY=9.525 CenterZ=0 NormalX=0 NormalY=0 NormalZ=1 AngleXU=0 Radius=5
    g30: Circle CenterX=1124.99 CenterY=9.525 CenterZ=0 NormalX=0 NormalY=0 NormalZ=1 AngleXU=0 Radius=5
  constraints (57):
    c: Coincident(g0,g-5)
    c: PointOnObject(g0,g-6)
    c: Vertical(g0)
    c: Coincident(g1,g0)
    c: Coincident(g1,g-7)
    c: Symmetric(g1,g1,g2)
    c: PointOnObject(g2,g-6)
    c: Vertical(g2)
    c: Coincident(g3,g2)
    c: PointOnObject(g3,g-4)
    c: Vertical(g3)
    c: Coincident(g4,g5)
    c: Coincident(g5,g6)
    c: Coincident(g6,g7)
    c: Coincident(g7,g4)
    c: Vertical(g4)
    c: Vertical(g6)
    c: Horizontal(g5)
    c: Horizontal(g7)
    c: Coincident(g4,g-4)
    c: Coincident(g5,g2)
    c: Coincident(g8,g-8)
    c: Coincident(g8,g4)
    c: Coincident(g9,g-9)
    c: Coincident(g9,g3)
    c: Symmetric(g7,g7,g10)
    c: Symmetric(g5,g5,g10)
    c: Symmetric(g4,g4,g11)
    c: Symmetric(g6,g6,g11)
    c: Symmetric(g8,g8,g12)
    c: PointOnObject(g12,g11)
    c: Vertical(g12)
    c: Coincident(g13,g12)
    c: Symmetric(g12,g12,g14)
    c: Coincident(g15,g12)
    c: Diameter(g13) = 10
    c: Diameter(g14) = 10
    c: Diameter(g15) = 10
    c: Diameter(g17) = 10
    c: Diameter(g16) = 10
    c: Diameter(g18) = 10
    c: Diameter(g19) = 10
    c: Diameter(g20) = 10
    c: Diameter(g22) = 10
    c: Diameter(g21) = 10
    c: Coincident(g23,g18)
    c: PointOnObject(g23,g10)
    c: Horizontal(g23)
    c: Coincident(g25,g23)
    c: Symmetric(g23,g23,g26)
    c: Symmetric(g24,g24,g27)
    c: Diameter(g27) = 10
    c: Diameter(g25) = 10
    c: Diameter(g26) = 10
    c: Diameter(g30) = 10
    c: Diameter(g29) = 10
    c: Diameter(g28) = 10
FEATURE [PartDesign::Pad] Pad046
  Direction = (0,-1,2e-16)
  Length = 5
  Length2 = 10
  Profile = -> Sketch106
  ReferenceAxis = -> Sketch106 [N_Axis]
  Refine = true
  Suppressed = false
  Type = 0
FEATURE [PartDesign::Body] Body042  label="Cuerpo068"
  AllowCompound = false
  Group = -> [Binder046,Binder047,Sketch106,Pad046]
  Origin = -> Origin045
  Tip = -> Pad046
FEATURE [PartDesign::SubShapeBinder] Binder048  label="Binder049"
  BindCopyOnChange = 0
  BindMode = 2
  ClaimChildren = false
  Context = -> Part002 [Body035.Binder039.]
  Fuse = false
  MakeFace = true
  OffsetFill = false
  OffsetIntersection = false
  OffsetJoinType = 0
  OffsetOpenResult = false
  PartialLoad = false
  Refine = true
  Relative = true
  _Version = 2
FEATURE [Sketcher::SketchObject] Sketch107
  ArcFitTolerance = 1e-06
  AttachmentSupport = -> [Binder048]
  ExternalGeometry = -> [Binder048]
  FullyConstrained = false
  MakeInternals = false
  MapMode = 5
  Placement = pos=(0,-38.1,0) rot=(1,0,0;1.5708rad)
  sketch-geometry (37):
    g0: LineSegment [constr] StartX=538.071 StartY=1038.1 StartZ=0 EndX=999.985 EndY=1038.1 EndZ=0
    g1: LineSegment [constr] StartX=999.985 StartY=2038.1 StartZ=0 EndX=999.985 EndY=1038.1 EndZ=0
    g2: LineSegment [constr] StartX=538.071 StartY=1038.1 StartZ=0 EndX=499.971 EndY=1038.1 EndZ=0
    g3: LineSegment [constr] StartX=999.985 StartY=2038.1 StartZ=0 EndX=999.985 EndY=2076.2 EndZ=0
    g4: LineSegment StartX=999.985 StartY=1038.1 StartZ=0 EndX=999.985 EndY=2076.2 EndZ=0
    g5: LineSegment StartX=999.985 StartY=2076.2 StartZ=0 EndX=499.971 EndY=2076.2 EndZ=0
    g6: LineSegment StartX=499.971 StartY=2076.2 StartZ=0 EndX=499.971 EndY=1038.1 EndZ=0
    g7: LineSegment StartX=499.971 StartY=1038.1 StartZ=0 EndX=999.985 EndY=1038.1 EndZ=0
    g8: LineSegment [constr] StartX=999.985 StartY=1038.1 StartZ=0 EndX=980.935 EndY=1057.15 EndZ=0
    g9: Circle CenterX=988.253 CenterY=1047.62 CenterZ=0 NormalX=0 NormalY=0 NormalZ=1 AngleXU=0 Radius=5
    g10: LineSegment [constr] StartX=749.978 StartY=2076.2 StartZ=0 EndX=749.978 EndY=1057.15 EndZ=0
    g11: Circle CenterX=509.496 CenterY=1047.63 CenterZ=0 NormalX=0 NormalY=0 NormalZ=1 AngleXU=0 Radius=5
    g12: LineSegment [constr] StartX=499.971 StartY=1557.15 StartZ=0 EndX=999.985 EndY=1557.15 EndZ=0
    g13: LineSegment [constr] StartX=509.496 StartY=1047.63 StartZ=0 EndX=990.46 EndY=1047.63 EndZ=0
    g14: LineSegment [constr] StartX=749.978 StartY=1047.63 StartZ=0 EndX=749.978 EndY=1038.1 EndZ=0
    g15: LineSegment [constr] StartX=990.46 StartY=1047.63 StartZ=0 EndX=990.46 EndY=1038.1 EndZ=0
    g16: LineSegment [constr] StartX=990.46 StartY=1042.86 StartZ=0 EndX=749.978 EndY=1043.57 EndZ=0
    g17: LineSegment [constr] StartX=509.496 StartY=1047.63 StartZ=0 EndX=509.496 EndY=1038.1 EndZ=0
    g18: LineSegment [constr] StartX=749.978 StartY=1043.57 StartZ=0 EndX=509.496 EndY=1043.57 EndZ=0
    g19: LineSegment [constr] StartX=870.219 StartY=1043.22 StartZ=0 EndX=870.219 EndY=1047.62 EndZ=0
    g20: LineSegment [constr] StartX=629.737 StartY=1043.57 StartZ=0 EndX=629.737 EndY=1047.62 EndZ=0
    g21: Circle CenterX=749.978 CenterY=1047.63 CenterZ=0 NormalX=0 NormalY=0 NormalZ=1 AngleXU=0 Radius=5
    g22: Circle CenterX=870.219 CenterY=1047.62 CenterZ=0 NormalX=0 NormalY=0 NormalZ=1 AngleXU=0 Radius=5
    g23: Circle CenterX=629.737 CenterY=1047.62 CenterZ=0 NormalX=0 NormalY=0 NormalZ=1 AngleXU=0 Radius=5
    g24: LineSegment [constr] StartX=988.253 StartY=1047.62 StartZ=0 EndX=988.253 EndY=1557.15 EndZ=0
    g25: Circle CenterX=988.253 CenterY=1302.39 CenterZ=0 NormalX=0 NormalY=0 NormalZ=1 AngleXU=0 Radius=5
    g26: Circle CenterX=988.253 CenterY=1557.15 CenterZ=0 NormalX=0 NormalY=0 NormalZ=1 AngleXU=0 Radius=5
    g27: Circle CenterX=988.253 CenterY=1557.15 CenterZ=0 NormalX=0 NormalY=0 NormalZ=1 AngleXU=0 Radius=5
    g28: Circle CenterX=988.253 CenterY=2066.67 CenterZ=0 NormalX=0 NormalY=0 NormalZ=1 AngleXU=0 Radius=5
    g29: Circle CenterX=988.253 CenterY=1811.91 CenterZ=0 NormalX=0 NormalY=0 NormalZ=1 AngleXU=0 Radius=5
    g30: Circle CenterX=511.703 CenterY=2066.67 CenterZ=0 NormalX=0 NormalY=0 NormalZ=1 AngleXU=0 Radius=5
    g31: Circle CenterX=511.703 CenterY=1811.91 CenterZ=0 NormalX=0 NormalY=0 NormalZ=1 AngleXU=0 Radius=5
    g32: Circle CenterX=511.703 CenterY=1557.15 CenterZ=0 NormalX=0 NormalY=0 NormalZ=1 AngleXU=0 Radius=5
    g33: Circle CenterX=511.703 CenterY=1302.39 CenterZ=0 NormalX=0 NormalY=0 NormalZ=1 AngleXU=0 Radius=5
    g34: Circle CenterX=629.737 CenterY=2066.67 CenterZ=0 NormalX=0 NormalY=0 NormalZ=1 AngleXU=0 Radius=5
    g35: Circle CenterX=749.978 CenterY=2066.67 CenterZ=0 NormalX=0 NormalY=0 NormalZ=1 AngleXU=0 Radius=5
    g36: Circle CenterX=870.219 CenterY=2066.67 CenterZ=0 NormalX=0 NormalY=0 NormalZ=1 AngleXU=0 Radius=5
  constraints (69):
    c: Symmetric(g-3,g-3,g0)
    c: Horizontal(g0)
    c: Symmetric(g-6,g-6,g1)
    c: Vertical(g1)
    c: Coincident(g1,g0)
    c: Coincident(g2,g0)
    c: Symmetric(g-9,g-9,g2)
    c: Coincident(g3,g1)
    c: Symmetric(g-10,g-10,g3)
    c: Coincident(g4,g5)
    c: Coincident(g5,g6)
    c: Coincident(g6,g7)
    c: Coincident(g7,g4)
    c: Vertical(g4)
    c: Vertical(g6)
    c: Horizontal(g5)
    c: Horizontal(g7)
    c: Coincident(g4,g0)
    c: Coincident(g5,g-10)
    c: Coincident(g8,g0)
    c: Coincident(g8,g-7)
    c: Diameter(g9) = 10
    c: Symmetric(g5,g5,g10)
    c: PointOnObject(g10,g-4)
    c: Vertical(g10)
    c: Diameter(g11) = 10
    c: Symmetric(g6,g6,g12)
    c: Symmetric(g4,g4,g12)
    c: Coincident(g13,g11)
    c: Horizontal(g13)
    c: Symmetric(g13,g13,g14)
    c: Symmetric(g7,g7,g14)
    c: Vertical(g14)
    c: PointOnObject(g15,g7)
    c: Vertical(g15)
    c: Coincident(g17,g11)
    c: PointOnObject(g17,g7)
    c: Vertical(g17)
    c: Horizontal(g18)
    c: PointOnObject(g18,g17)
    c: Symmetric(g16,g16,g19)
    c: PointOnObject(g19,g13)
    c: Vertical(g19)
    c: Symmetric(g18,g18,g20)
    c: PointOnObject(g20,g13)
    c: Vertical(g20)
    c: Coincident(g21,g14)
    c: Coincident(g22,g19)
    c: Coincident(g23,g20)
    c: Diameter(g23) = 10
    c: Diameter(g21) = 10
    c: Diameter(g22) = 10
    c: Coincident(g24,g9)
    c: PointOnObject(g24,g12)
    c: Vertical(g24)
    c: Symmetric(g24,g24,g25)
    c: Coincident(g26,g24)
    c: Diameter(g26) = 10
    c: Diameter(g25) = 10
    c: Diameter(g28) = 10
    c: Diameter(g27) = 10
    c: Diameter(g29) = 10
    c: Diameter(g32) = 10
    c: Diameter(g33) = 10
    c: Diameter(g30) = 10
    c: Diameter(g31) = 10
    c: Diameter(g34) = 10
    c: Diameter(g35) = 10
    c: Diameter(g36) = 10
FEATURE [PartDesign::Pad] Pad047
  Direction = (0,-1,2e-16)
  Length = 5
  Length2 = 10
  Profile = -> Sketch107
  ReferenceAxis = -> Sketch107 [N_Axis]
  Refine = true
  Suppressed = false
  Type = 0
FEATURE [PartDesign::Body] Body043  label="Cuerpo069"
  AllowCompound = false
  Group = -> [Binder048,Sketch107,Pad047]
  Origin = -> Origin046
  Placement = pos=(0,-4.548e-13,-1.1369e-12) rot=(0,0,1;0rad)
  Tip = -> Pad047
FEATURE [PartDesign::SubShapeBinder] Binder049  label="Binder050"
  BindCopyOnChange = 0
  BindMode = 2
  ClaimChildren = false
  Context = -> Part002 [Body044.Binder049.]
  Fuse = false
  MakeFace = true
  OffsetFill = false
  OffsetIntersection = false
  OffsetJoinType = 0
  OffsetOpenResult = false
  PartialLoad = false
  Refine = true
  Relative = true
  _Version = 2
FEATURE [PartDesign::SubShapeBinder] Binder050  label="Binder051"
  BindCopyOnChange = 0
  BindMode = 2
  ClaimChildren = false
  Context = -> Part002 [Body044.Binder050.]
  Fuse = false
  MakeFace = true
  OffsetFill = false
  OffsetIntersection = false
  OffsetJoinType = 0
  OffsetOpenResult = false
  PartialLoad = false
  Refine = true
  Relative = true
  _Version = 2
FEATURE [Sketcher::SketchObject] Sketch108
  ArcFitTolerance = 1e-06
  AttachmentSupport = -> [Binder050]
  ExternalGeometry = -> [Binder049,Binder050]
  FullyConstrained = false
  MakeInternals = false
  MapMode = 5
  Placement = pos=(0,-38.1,8.4e-15) rot=(1,0,0;1.5708rad)
  sketch-geometry (31):
    g0: LineSegment [constr] StartX=1500 StartY=38.1 StartZ=0 EndX=1500 EndY=7.461e-13 EndZ=0
    g1: LineSegment [constr] StartX=1500 StartY=38.1 StartZ=0 EndX=1461.9 EndY=38.1 EndZ=0
    g2: LineSegment [constr] StartX=1480.95 StartY=38.1 StartZ=0 EndX=1480.95 EndY=6.821e-13 EndZ=0
    g3: LineSegment [constr] StartX=1480.95 StartY=38.1 StartZ=0 EndX=1480.95 EndY=1038.1 EndZ=0
    g4: LineSegment StartX=999.985 StartY=1038.1 StartZ=0 EndX=999.985 EndY=6.821e-13 EndZ=0
    g5: LineSegment StartX=999.985 StartY=6.821e-13 StartZ=0 EndX=1480.95 EndY=6.821e-13 EndZ=0
    g6: LineSegment StartX=1480.95 StartY=6.821e-13 StartZ=0 EndX=1480.95 EndY=1038.1 EndZ=0
    g7: LineSegment StartX=1480.95 StartY=1038.1 StartZ=0 EndX=999.985 EndY=1038.1 EndZ=0
    g8: LineSegment [constr] StartX=1019.04 StartY=1019.05 StartZ=0 EndX=999.985 EndY=1038.1 EndZ=0
    g9: LineSegment [constr] StartX=1461.9 StartY=1019.05 StartZ=0 EndX=1480.95 EndY=1038.1 EndZ=0
    g10: LineSegment [constr] StartX=1240.47 StartY=1038.1 StartZ=0 EndX=1240.47 EndY=6.821e-13 EndZ=0
    g11: LineSegment [constr] StartX=999.985 StartY=519.05 StartZ=0 EndX=1480.95 EndY=519.05 EndZ=0
    g12: LineSegment [constr] StartX=1009.51 StartY=1028.57 StartZ=0 EndX=1009.51 EndY=519.05 EndZ=0
    g13: Circle CenterX=1009.51 CenterY=1028.57 CenterZ=0 NormalX=0 NormalY=0 NormalZ=1 AngleXU=0 Radius=5
    g14: Circle CenterX=1009.51 CenterY=773.812 CenterZ=0 NormalX=0 NormalY=0 NormalZ=1 AngleXU=0 Radius=5
    g15: Circle CenterX=1009.51 CenterY=519.05 CenterZ=0 NormalX=0 NormalY=0 NormalZ=1 AngleXU=0 Radius=5
    g16: Circle CenterX=1009.51 CenterY=264.288 CenterZ=0 NormalX=0 NormalY=0 NormalZ=1 AngleXU=0 Radius=5
    g17: Circle CenterX=1009.51 CenterY=9.525 CenterZ=0 NormalX=0 NormalY=0 NormalZ=1 AngleXU=0 Radius=5
    g18: Circle CenterX=1471.42 CenterY=1028.58 CenterZ=0 NormalX=0 NormalY=0 NormalZ=1 AngleXU=0 Radius=5
    g19: Circle CenterX=1471.43 CenterY=773.812 CenterZ=0 NormalX=0 NormalY=0 NormalZ=1 AngleXU=0 Radius=5
    g20: Circle CenterX=1471.43 CenterY=519.05 CenterZ=0 NormalX=0 NormalY=0 NormalZ=1 AngleXU=0 Radius=5
    g21: Circle CenterX=1471.43 CenterY=264.288 CenterZ=0 NormalX=0 NormalY=0 NormalZ=1 AngleXU=0 Radius=5
    g22: Circle CenterX=1471.43 CenterY=9.525 CenterZ=0 NormalX=0 NormalY=0 NormalZ=1 AngleXU=0 Radius=5
    g23: LineSegment [constr] StartX=1471.42 StartY=1028.58 StartZ=0 EndX=1240.47 EndY=1028.58 EndZ=0
    g24: LineSegment [constr] StartX=1240.47 StartY=1028.57 StartZ=0 EndX=1009.51 EndY=1028.57 EndZ=0
    g25: Circle CenterX=1240.47 CenterY=1028.58 CenterZ=0 NormalX=0 NormalY=0 NormalZ=1 AngleXU=0 Radius=5
    g26: Circle CenterX=1355.95 CenterY=1028.58 CenterZ=0 NormalX=0 NormalY=0 NormalZ=1 AngleXU=0 Radius=5
    g27: Circle CenterX=1124.99 CenterY=1028.57 CenterZ=0 NormalX=0 NormalY=0 NormalZ=1 AngleXU=0 Radius=5
    g28: Circle CenterX=1355.95 CenterY=9.525 CenterZ=0 NormalX=0 NormalY=0 NormalZ=1 AngleXU=0 Radius=5
    g29: Circle CenterX=1240.47 CenterY=9.525 CenterZ=0 NormalX=0 NormalY=0 NormalZ=1 AngleXU=0 Radius=5
    g30: Circle CenterX=1124.99 CenterY=9.525 CenterZ=0 NormalX=0 NormalY=0 NormalZ=1 AngleXU=0 Radius=5
  constraints (57):
    c: Coincident(g0,g-5)
    c: PointOnObject(g0,g-6)
    c: Vertical(g0)
    c: Coincident(g1,g0)
    c: Coincident(g1,g-7)
    c: Symmetric(g1,g1,g2)
    c: PointOnObject(g2,g-6)
    c: Vertical(g2)
    c: Coincident(g3,g2)
    c: PointOnObject(g3,g-4)
    c: Vertical(g3)
    c: Coincident(g4,g5)
    c: Coincident(g5,g6)
    c: Coincident(g6,g7)
    c: Coincident(g7,g4)
    c: Vertical(g4)
    c: Vertical(g6)
    c: Horizontal(g5)
    c: Horizontal(g7)
    c: Coincident(g4,g-4)
    c: Coincident(g5,g2)
    c: Coincident(g8,g-8)
    c: Coincident(g8,g4)
    c: Coincident(g9,g-9)
    c: Coincident(g9,g3)
    c: Symmetric(g7,g7,g10)
    c: Symmetric(g5,g5,g10)
    c: Symmetric(g4,g4,g11)
    c: Symmetric(g6,g6,g11)
    c: Symmetric(g8,g8,g12)
    c: PointOnObject(g12,g11)
    c: Vertical(g12)
    c: Coincident(g13,g12)
    c: Symmetric(g12,g12,g14)
    c: Coincident(g15,g12)
    c: Diameter(g13) = 10
    c: Diameter(g14) = 10
    c: Diameter(g15) = 10
    c: Diameter(g17) = 10
    c: Diameter(g16) = 10
    c: Diameter(g18) = 10
    c: Diameter(g19) = 10
    c: Diameter(g20) = 10
    c: Diameter(g22) = 10
    c: Diameter(g21) = 10
    c: Coincident(g23,g18)
    c: PointOnObject(g23,g10)
    c: Horizontal(g23)
    c: Coincident(g25,g23)
    c: Symmetric(g23,g23,g26)
    c: Symmetric(g24,g24,g27)
    c: Diameter(g27) = 10
    c: Diameter(g25) = 10
    c: Diameter(g26) = 10
    c: Diameter(g30) = 10
    c: Diameter(g29) = 10
    c: Diameter(g28) = 10
FEATURE [PartDesign::Pad] Pad048
  Direction = (0,-1,2e-16)
  Length = 5
  Length2 = 10
  Profile = -> Sketch108
  ReferenceAxis = -> Sketch108 [N_Axis]
  Refine = true
  Suppressed = false
  Type = 0
FEATURE [PartDesign::Body] Body044  label="Cuerpo070"
  AllowCompound = false
  Group = -> [Binder050,Binder049,Sketch108,Pad048]
  Origin = -> Origin047
  Placement = pos=(0,2.345e-13,1038.1) rot=(0,0,1;0rad)
  Tip = -> Pad048
FEATURE [PartDesign::SubShapeBinder] Binder051  label="Binder052"
  BindCopyOnChange = 0
  BindMode = 2
  ClaimChildren = false
  Context = -> Body045 [Binder051.]
  Fuse = false
  MakeFace = true
  OffsetFill = false
  OffsetIntersection = false
  OffsetJoinType = 0
  OffsetOpenResult = false
  PartialLoad = false
  Refine = true
  Relative = true
  _Version = 2
FEATURE [Sketcher::SketchObject] Sketch109
  ArcFitTolerance = 1e-06
  AttachmentSupport = -> [Binder051]
  ExternalGeometry = -> [Binder051]
  FullyConstrained = false
  MakeInternals = false
  MapMode = 5
  Placement = pos=(0,1538.1,0) rot=(0,0.707107,0.707107;3.14159rad)
  sketch-geometry (12):
    g0: LineSegment [constr] StartX=-1999.95 StartY=1600.33 StartZ=0 EndX=-1999.97 EndY=1638.1 EndZ=0
    g1: LineSegment [constr] StartX=-1500 StartY=2076.2 StartZ=0 EndX=-1480.95 EndY=2076.2 EndZ=0
    g2: LineSegment StartX=-1480.95 StartY=2076.2 StartZ=0 EndX=-1480.95 EndY=2081.2 EndZ=0
    g3: LineSegment StartX=-1480.95 StartY=2081.2 StartZ=0 EndX=-1500 EndY=2081.2 EndZ=0
    g4: LineSegment StartX=-2004.97 StartY=1619.21 StartZ=0 EndX=-2004.97 EndY=1638.1 EndZ=0
    g5: LineSegment [constr] StartX=-1999.97 StartY=1638.1 StartZ=0 EndX=-2004.97 EndY=1638.1 EndZ=0
    g6: LineSegment StartX=-2004.97 StartY=1638.1 StartZ=0 EndX=-1500 EndY=2081.2 EndZ=0
    g7: LineSegment StartX=-1480.95 StartY=2076.2 StartZ=0 EndX=-1500 EndY=2076.2 EndZ=0
    g8: LineSegment StartX=-1500 StartY=2076.2 StartZ=0 EndX=-1999.97 EndY=1638.1 EndZ=0
    g9: LineSegment StartX=-1999.97 StartY=1638.1 StartZ=0 EndX=-1999.96 EndY=1619.21 EndZ=0
    g10: LineSegment [constr] StartX=-1999.96 StartY=1619.21 StartZ=0 EndX=-2017.02 EndY=1619.21 EndZ=0
    g11: LineSegment StartX=-2004.97 StartY=1619.21 StartZ=0 EndX=-1999.96 EndY=1619.21 EndZ=0
  constraints (25):
    c: Coincident(g0,g-3)
    c: Coincident(g1,g-3)
    c: Coincident(g1,g-4)
    c: Coincident(g2,g1)
    c: Coincident(g2,g-5)
    c: Coincident(g3,g2)
    c: Coincident(g3,g-6)
    c: Vertical(g4)
    c: Coincident(g5,g0)
    c: Coincident(g5,g4)
    c: Coincident(g6,g4)
    c: Coincident(g6,g3)
    c: Horizontal(g5)
    c: Distance(g5) = 5
    c: Coincident(g7,g1)
    c: Coincident(g7,g1)
    c: Coincident(g8,g1)
    c: Coincident(g8,g0)
    c: Coincident(g9,g0)
    c: Symmetric(g0,g0,g10)
    c: Horizontal(g10)
    c: Coincident(g10,g9)
    c: PointOnObject(g4,g10)
    c: Coincident(g11,g4)
    c: Coincident(g11,g9)
FEATURE [PartDesign::Pad] Pad049
  Direction = (0,1,-2e-16)
  Length = 10
  Length2 = 10
  Profile = -> Sketch109
  ReferenceAxis = -> Sketch109 [N_Axis]
  Refine = true
  Suppressed = false
  Type = 3
  UpToFace = -> Binder051 [Face11]
FEATURE [Sketcher::SketchObject] Sketch110
  ArcFitTolerance = 1e-06
  AttachmentSupport = -> [Pad049]
  ExternalGeometry = -> [Pad049,Binder051]
  FullyConstrained = false
  MakeInternals = false
  MapMode = 5
  Placement = pos=(0,4.579e-13,2081.2) rot=(0,0,1;0rad)
  sketch-geometry (10):
    g0: LineSegment [constr] StartX=1480.95 StartY=750 StartZ=0 EndX=1480.95 EndY=769.05 EndZ=0
    g1: LineSegment [constr] StartX=1499.99 StartY=769.05 StartZ=0 EndX=1480.95 EndY=769.05 EndZ=0
    g2: LineSegment [constr] StartX=1499.99 StartY=769.05 StartZ=0 EndX=1480.95 EndY=750 EndZ=0
    g3: Circle CenterX=1490.47 CenterY=759.525 CenterZ=0 NormalX=0 NormalY=0 NormalZ=1 AngleXU=0 Radius=5
    g4: LineSegment [constr] StartX=1480.95 StartY=1144.05 StartZ=0 EndX=1500 EndY=1144.05 EndZ=0
    g5: LineSegment [constr] StartX=1490.47 StartY=759.525 StartZ=0 EndX=1490.47 EndY=1144.05 EndZ=0
    g6: Circle CenterX=1490.47 CenterY=951.788 CenterZ=0 NormalX=0 NormalY=0 NormalZ=1 AngleXU=0 Radius=5
    g7: Circle CenterX=1490.47 CenterY=1144.05 CenterZ=0 NormalX=0 NormalY=0 NormalZ=1 AngleXU=0 Radius=5
    g8: Circle CenterX=1490.47 CenterY=1336.31 CenterZ=0 NormalX=0 NormalY=0 NormalZ=1 AngleXU=0 Radius=5
    g9: Circle CenterX=1490.47 CenterY=1528.58 CenterZ=0 NormalX=0 NormalY=0 NormalZ=1 AngleXU=0 Radius=5
  constraints (17):
    c: Coincident(g0,g-4)
    c: Vertical(g0)
    c: Coincident(g1,g-5)
    c: Horizontal(g1)
    c: Coincident(g1,g0)
    c: Coincident(g2,g1)
    c: Coincident(g2,g0)
    c: Symmetric(g2,g2,g3)
    c: Symmetric(g-6,g-6,g4)
    c: Symmetric(g-7,g-7,g4)
    c: Symmetric(g5,g5,g6)
    c: Coincident(g7,g5)
    c: Diameter(g7) = 10
    c: Diameter(g6) = 10
    c: Diameter(g3) = 10
    c: Diameter(g8) = 10
    c: Diameter(g9) = 10
FEATURE [PartDesign::Pocket] Pocket056
  BaseFeature = -> Pad049
  Direction = (0,0,-1)
  Length = 5
  Length2 = 5
  Profile = -> Sketch110
  ReferenceAxis = -> Sketch110 [N_Axis]
  Refine = true
  Suppressed = false
  Type = 0
FEATURE [Sketcher::SketchObject] Sketch111
  ArcFitTolerance = 1e-06
  AttachmentSupport = -> [Pocket056]
  ExternalGeometry = -> [Pocket056]
  FullyConstrained = false
  MakeInternals = false
  MapMode = 5
  Placement = pos=(1684.3,4.341e-13,1919.48) rot=(0,1,0;0.720231rad)
  sketch-geometry (11):
    g0: LineSegment [constr] StartX=426.62 StartY=1144.05 StartZ=0 EndX=-245.193 EndY=1144.05 EndZ=0
    g1: LineSegment [constr] StartX=90.7134 StartY=1538.1 StartZ=0 EndX=90.7134 EndY=750 EndZ=0
    g2: LineSegment [constr] StartX=-245.193 StartY=1528.58 StartZ=0 EndX=-252.358 EndY=1528.58 EndZ=0
    g3: LineSegment [constr] StartX=-245.193 StartY=1528.58 StartZ=0 EndX=90.7134 EndY=1528.58 EndZ=0
    g4: LineSegment [constr] StartX=90.7134 StartY=1528.58 StartZ=0 EndX=426.62 EndY=1528.58 EndZ=0
    g5: Circle CenterX=-77.2398 CenterY=1528.58 CenterZ=0 NormalX=0 NormalY=0 NormalZ=1 AngleXU=0 Radius=5
    g6: Circle CenterX=90.7134 CenterY=1528.58 CenterZ=0 NormalX=0 NormalY=0 NormalZ=1 AngleXU=0 Radius=5
    g7: Circle CenterX=320.484 CenterY=1528.58 CenterZ=0 NormalX=0 NormalY=0 NormalZ=1 AngleXU=0 Radius=5
    g8: Circle CenterX=320.484 CenterY=759.525 CenterZ=0 NormalX=0 NormalY=0 NormalZ=1 AngleXU=0 Radius=5
    g9: Circle CenterX=90.7134 CenterY=759.525 CenterZ=0 NormalX=0 NormalY=0 NormalZ=1 AngleXU=0 Radius=5
    g10: Circle CenterX=-77.2398 CenterY=759.525 CenterZ=0 NormalX=0 NormalY=0 NormalZ=1 AngleXU=0 Radius=5
  constraints (22):
    c: Symmetric(g-6,g-6,g0)
    c: Symmetric(g-5,g-5,g0)
    c: Symmetric(g-3,g-3,g1)
    c: Symmetric(g-7,g-7,g1)
    c: PointOnObject(g2,g-5)
    c: Coincident(g2,g-4)
    c: Horizontal(g2)
    c: Coincident(g3,g2)
    c: PointOnObject(g3,g1)
    c: Horizontal(g3)
    c: Coincident(g4,g3)
    c: PointOnObject(g4,g-6)
    c: Horizontal(g4)
    c: Symmetric(g3,g3,g5)
    c: Coincident(g6,g3)
    c: PointOnObject(g7,g4)
    c: Equal(g7,g6)
    c: Equal(g7,g5)
    c: Diameter(g7) = 10
    c: Equal(g8,g9)
    c: Equal(g8,g10)
    c: Diameter(g8) = 10
FEATURE [PartDesign::Pocket] Pocket057
  BaseFeature = -> Pocket056
  Direction = (-0.659558,0,-0.751653)
  Length = 5
  Length2 = 5
  Profile = -> Sketch111
  ReferenceAxis = -> Sketch111 [N_Axis]
  Refine = true
  Suppressed = false
  Type = 0
FEATURE [Sketcher::SketchObject] Sketch112
  ArcFitTolerance = 1e-06
  AttachmentSupport = -> [Pocket057]
  ExternalGeometry = -> [Pocket057]
  FullyConstrained = false
  MakeInternals = false
  MapMode = 5
  Placement = pos=(2004.97,0,0) rot=(0.57735,0.57735,0.57735;2.0944rad)
  sketch-geometry (9):
    g0: LineSegment [constr] StartX=1144.05 StartY=1638.1 StartZ=0 EndX=1144.05 EndY=1619.21 EndZ=0
    g1: LineSegment [constr] StartX=750 StartY=1628.66 StartZ=0 EndX=1144.05 EndY=1628.66 EndZ=0
    g2: LineSegment [constr] StartX=1528.58 StartY=1704.81 StartZ=0 EndX=1528.58 EndY=1628.66 EndZ=0
    g3: Circle CenterX=1528.58 CenterY=1628.66 CenterZ=0 NormalX=0 NormalY=0 NormalZ=1 AngleXU=0 Radius=5
    g4: Circle CenterX=1144.05 CenterY=1628.66 CenterZ=0 NormalX=0 NormalY=0 NormalZ=1 AngleXU=0 Radius=5
    g5: LineSegment [constr] StartX=1528.58 StartY=1628.66 StartZ=0 EndX=1144.05 EndY=1628.66 EndZ=0
    g6: Circle CenterX=1336.31 CenterY=1628.66 CenterZ=0 NormalX=0 NormalY=0 NormalZ=1 AngleXU=0 Radius=5
    g7: Circle CenterX=951.788 CenterY=1628.66 CenterZ=0 NormalX=0 NormalY=0 NormalZ=1 AngleXU=0 Radius=5
    g8: Circle CenterX=759.525 CenterY=1628.66 CenterZ=0 NormalX=0 NormalY=0 NormalZ=1 AngleXU=0 Radius=5
  constraints (17):
    c: Symmetric(g-6,g-6,g0)
    c: Symmetric(g-5,g-5,g0)
    c: Symmetric(g-7,g-7,g1)
    c: Symmetric(g0,g0,g1)
    c: Coincident(g2,g-9)
    c: Vertical(g2)
    c: Coincident(g3,g2)
    c: Coincident(g4,g1)
    c: Coincident(g5,g2)
    c: Coincident(g5,g1)
    c: Horizontal(g5)
    c: Symmetric(g5,g5,g6)
    c: Diameter(g4) = 10
    c: Diameter(g6) = 10
    c: Diameter(g3) = 10
    c: Diameter(g7) = 10
    c: Diameter(g8) = 10
FEATURE [PartDesign::Pocket] Pocket058
  BaseFeature = -> Pocket057
  Direction = (-1,0,0)
  Length = 5
  Length2 = 5
  Profile = -> Sketch112
  ReferenceAxis = -> Sketch112 [N_Axis]
  Refine = true
  Suppressed = false
  Type = 1
FEATURE [PartDesign::Body] Body045  label="Cuerpo071"
  AllowCompound = false
  Group = -> [Binder051,Sketch109,Pad049,Sketch110,Pocket056,Sketch111,Pocket057,Sketch112,Pocket058]
  Origin = -> Origin048
  Tip = -> Pocket058
FEATURE [PartDesign::SubShapeBinder] Binder052  label="Binder053"
  BindCopyOnChange = 0
  BindMode = 2
  ClaimChildren = false
  Context = -> Body046 [Binder052.]
  Fuse = false
  MakeFace = true
  OffsetFill = false
  OffsetIntersection = false
  OffsetJoinType = 0
  OffsetOpenResult = false
  PartialLoad = false
  Refine = true
  Relative = true
  _Version = 2
FEATURE [Sketcher::SketchObject] Sketch113
  ArcFitTolerance = 1e-06
  AttachmentSupport = -> [Binder052]
  ExternalGeometry = -> [Binder052]
  FullyConstrained = false
  MakeInternals = false
  MapMode = 5
  Placement = pos=(0,0,2076.2) rot=(0,0,1;0rad)
  sketch-geometry (36):
    g0: LineSegment [constr] StartX=1500 StartY=750 StartZ=0 EndX=980.935 EndY=750 EndZ=0
    g1: LineSegment [constr] StartX=999.985 StartY=-38.1 StartZ=0 EndX=999.985 EndY=750 EndZ=0
    g2: LineSegment StartX=999.985 StartY=750 StartZ=0 EndX=999.985 EndY=-38.1 EndZ=0
    g3: LineSegment StartX=999.985 StartY=-38.1 StartZ=0 EndX=1480.95 EndY=-38.1 EndZ=0
    g4: LineSegment StartX=1480.95 StartY=750 StartZ=0 EndX=999.985 EndY=750 EndZ=0
    g5: LineSegment [constr] StartX=1019.04 StartY=730.95 StartZ=0 EndX=999.985 EndY=750 EndZ=0
    g6: LineSegment [constr] StartX=1240.47 StartY=750 StartZ=0 EndX=1249.99 EndY=-38.1 EndZ=0
    g7: LineSegment [constr] StartX=999.985 StartY=355.95 StartZ=0 EndX=1490.47 EndY=355.95 EndZ=0
    g8: Circle CenterX=1009.51 CenterY=740.475 CenterZ=0 NormalX=0 NormalY=0 NormalZ=1 AngleXU=0 Radius=5
    g9: LineSegment [constr] StartX=1009.51 StartY=740.475 StartZ=0 EndX=1009.51 EndY=355.95 EndZ=0
    g10: Circle CenterX=1009.51 CenterY=355.95 CenterZ=0 NormalX=0 NormalY=0 NormalZ=1 AngleXU=0 Radius=5
    g11: Circle CenterX=1009.51 CenterY=548.212 CenterZ=0 NormalX=0 NormalY=0 NormalZ=1 AngleXU=0 Radius=5
    g12: Circle CenterX=1009.51 CenterY=163.688 CenterZ=0 NormalX=0 NormalY=0 NormalZ=1 AngleXU=0 Radius=5
    g13: Circle CenterX=1009.51 CenterY=-28.575 CenterZ=0 NormalX=0 NormalY=0 NormalZ=1 AngleXU=0 Radius=5
    g14: LineSegment [constr] StartX=1009.51 StartY=740.475 StartZ=0 EndX=1240.58 EndY=740.475 EndZ=0
    g15: LineSegment [constr] StartX=1240.58 StartY=740.475 StartZ=0 EndX=1491.87 EndY=740.475 EndZ=0
    g16: Circle CenterX=1366.23 CenterY=740.475 CenterZ=0 NormalX=0 NormalY=0 NormalZ=1 AngleXU=0 Radius=5
    g17: Circle CenterX=1240.58 CenterY=740.475 CenterZ=0 NormalX=0 NormalY=0 NormalZ=1 AngleXU=0 Radius=5
    g18: Circle CenterX=1125.05 CenterY=740.475 CenterZ=0 NormalX=0 NormalY=0 NormalZ=1 AngleXU=0 Radius=5
    g19: Circle CenterX=1129.75 CenterY=-28.575 CenterZ=0 NormalX=0 NormalY=0 NormalZ=1 AngleXU=0 Radius=5
    g20: Circle CenterX=1249.99 CenterY=-28.575 CenterZ=0 NormalX=0 NormalY=0 NormalZ=1 AngleXU=0 Radius=5
    g21: Circle CenterX=1370.23 CenterY=-28.575 CenterZ=0 NormalX=0 NormalY=0 NormalZ=1 AngleXU=0 Radius=5
    g22: LineSegment [constr] StartX=1461.9 StartY=730.95 StartZ=0 EndX=1500 EndY=730.95 EndZ=0
    g23: LineSegment [constr] StartX=1480.95 StartY=730.95 StartZ=0 EndX=1480.95 EndY=-38.1 EndZ=0
    g24: LineSegment [constr] StartX=1480.95 StartY=730.95 StartZ=0 EndX=1461.9 EndY=730.95 EndZ=0
    g25: LineSegment [constr] StartX=1461.9 StartY=4.547e-13 StartZ=0 EndX=1461.9 EndY=-38.1 EndZ=0
    g26: LineSegment [constr] StartX=1480.95 StartY=-38.1 StartZ=0 EndX=1461.9 EndY=-38.1 EndZ=0
    g27: LineSegment [constr] StartX=1480.95 StartY=-35.2074 StartZ=0 EndX=1461.9 EndY=-35.2074 EndZ=0
    g28: LineSegment [constr] StartX=1471.42 StartY=-35.2074 StartZ=0 EndX=1471.42 EndY=750 EndZ=0
    g29: Circle CenterX=1471.42 CenterY=740.475 CenterZ=0 NormalX=0 NormalY=0 NormalZ=1 AngleXU=0 Radius=5
    g30: Circle CenterX=1471.42 CenterY=548.212 CenterZ=0 NormalX=0 NormalY=0 NormalZ=1 AngleXU=0 Radius=5
    g31: Circle CenterX=1471.42 CenterY=355.95 CenterZ=0 NormalX=0 NormalY=0 NormalZ=1 AngleXU=0 Radius=5
    g32: Circle CenterX=1471.42 CenterY=163.688 CenterZ=0 NormalX=0 NormalY=0 NormalZ=1 AngleXU=0 Radius=5
    g33: Circle CenterX=1471.42 CenterY=-28.575 CenterZ=0 NormalX=0 NormalY=0 NormalZ=1 AngleXU=0 Radius=5
    g34: LineSegment [constr] StartX=1480.95 StartY=730.95 StartZ=0 EndX=1480.95 EndY=750 EndZ=0
    g35: LineSegment StartX=1480.95 StartY=750 StartZ=0 EndX=1480.95 EndY=-38.1 EndZ=0
  constraints (71):
    c: Symmetric(g-5,g-5,g0)
    c: Symmetric(g-3,g-3,g0)
    c: Symmetric(g-4,g-4,g1)
    c: PointOnObject(g1,g0)
    c: Vertical(g1)
    c: Coincident(g2,g3)
    c: Coincident(g4,g2)
    c: Vertical(g2)
    c: Horizontal(g3)
    c: Horizontal(g4)
    c: Coincident(g2,g1)
    c: Coincident(g5,g-8)
    c: Coincident(g5,g1)
    c: Symmetric(g4,g4,g6)
    c: Symmetric(g2,g2,g7)
    c: Symmetric(g5,g5,g8)
    c: Coincident(g9,g8)
    c: PointOnObject(g9,g7)
    c: Vertical(g9)
    c: Coincident(g10,g9)
    c: Symmetric(g9,g9,g11)
    c: Diameter(g11) = 10
    c: Diameter(g8) = 10
    c: Diameter(g10) = 10
    c: Diameter(g12) = 10
    c: Diameter(g13) = 10
    c: Coincident(g14,g8)
    c: PointOnObject(g14,g6)
    c: Horizontal(g14)
    c: Coincident(g15,g14)
    c: Horizontal(g15)
    c: Symmetric(g15,g15,g16)
    c: Coincident(g17,g14)
    c: Symmetric(g14,g14,g18)
    c: Diameter(g16) = 10
    c: Diameter(g17) = 10
    c: Diameter(g18) = 10
    c: Diameter(g21) = 10
    c: Diameter(g20) = 10
    c: Diameter(g19) = 10
    c: Coincident(g22,g-9)
    c: Horizontal(g22)
    c: Symmetric(g22,g22,g23)
    c: PointOnObject(g23,g3)
    c: Vertical(g23)
    c: Coincident(g24,g23)
    c: Coincident(g24,g22)
    c: Coincident(g25,g-12)
    c: Vertical(g25)
    c: Coincident(g26,g23)
    c: PointOnObject(g26,g25)
    c: Horizontal(g26)
    c: PointOnObject(g25,g3)
    c: PointOnObject(g27,g23)
    c: PointOnObject(g27,g25)
    c: Horizontal(g27)
    c: Symmetric(g27,g27,g28)
    c: PointOnObject(g28,g4)
    c: Vertical(g28)
    c: Diameter(g30) = 10
    c: Diameter(g29) = 10
    c: Diameter(g31) = 10
    c: Diameter(g32) = 10
    c: Diameter(g33) = 10
    c: Coincident(g34,g23)
    c: Vertical(g34)
    c: PointOnObject(g22,g-5)
    c: Coincident(g4,g34)
    c: Coincident(g35,g4)
    c: Coincident(g35,g23)
    c: PointOnObject(g3,g35)
FEATURE [PartDesign::Pad] Pad050
  Direction = (0,0,1)
  Length = 5
  Length2 = 10
  Profile = -> Sketch113
  ReferenceAxis = -> Sketch113 [N_Axis]
  Refine = true
  Suppressed = false
  Type = 0
FEATURE [PartDesign::Body] Body046  label="Cuerpo072"
  AllowCompound = false
  Group = -> [Binder052,Sketch113,Pad050]
  Origin = -> Origin049
  Tip = -> Pad050
FEATURE [PartDesign::SubShapeBinder] Binder053  label="Binder054"
  BindCopyOnChange = 0
  BindMode = 2
  ClaimChildren = false
  Context = -> Body047 [Binder053.]
  Fuse = false
  MakeFace = true
  OffsetFill = false
  OffsetIntersection = false
  OffsetJoinType = 0
  OffsetOpenResult = false
  PartialLoad = false
  Refine = true
  Relative = true
  _Version = 2
FEATURE [Sketcher::SketchObject] Sketch114
  ArcFitTolerance = 1e-06
  AttachmentSupport = -> [Binder053]
  ExternalGeometry = -> [Binder053]
  FullyConstrained = false
  MakeInternals = false
  MapMode = 5
  Placement = pos=(0,1538.1,0) rot=(0,0.707107,0.707107;3.14159rad)
  sketch-geometry (12):
    g0: LineSegment [constr] StartX=-1999.95 StartY=1600.33 StartZ=0 EndX=-1999.97 EndY=1638.1 EndZ=0
    g1: LineSegment [constr] StartX=-1500 StartY=2076.2 StartZ=0 EndX=-1480.95 EndY=2076.2 EndZ=0
    g2: LineSegment StartX=-1480.95 StartY=2076.2 StartZ=0 EndX=-1480.95 EndY=2081.2 EndZ=0
    g3: LineSegment StartX=-1480.95 StartY=2081.2 StartZ=0 EndX=-1500 EndY=2081.2 EndZ=0
    g4: LineSegment StartX=-2004.97 StartY=1619.21 StartZ=0 EndX=-2004.97 EndY=1638.1 EndZ=0
    g5: LineSegment [constr] StartX=-1999.97 StartY=1638.1 StartZ=0 EndX=-2004.97 EndY=1638.1 EndZ=0
    g6: LineSegment StartX=-2004.97 StartY=1638.1 StartZ=0 EndX=-1500 EndY=2081.2 EndZ=0
    g7: LineSegment StartX=-1480.95 StartY=2076.2 StartZ=0 EndX=-1500 EndY=2076.2 EndZ=0
    g8: LineSegment StartX=-1500 StartY=2076.2 StartZ=0 EndX=-1999.97 EndY=1638.1 EndZ=0
    g9: LineSegment StartX=-1999.97 StartY=1638.1 StartZ=0 EndX=-1999.96 EndY=1619.21 EndZ=0
    g10: LineSegment [constr] StartX=-1999.96 StartY=1619.21 StartZ=0 EndX=-2017.02 EndY=1619.21 EndZ=0
    g11: LineSegment StartX=-2004.97 StartY=1619.21 StartZ=0 EndX=-1999.96 EndY=1619.21 EndZ=0
  constraints (25):
    c: Coincident(g0,g-3)
    c: Coincident(g1,g-3)
    c: Coincident(g1,g-4)
    c: Coincident(g2,g1)
    c: Coincident(g2,g-5)
    c: Coincident(g3,g2)
    c: Coincident(g3,g-6)
    c: Vertical(g4)
    c: Coincident(g5,g0)
    c: Coincident(g5,g4)
    c: Coincident(g6,g4)
    c: Coincident(g6,g3)
    c: Horizontal(g5)
    c: Distance(g5) = 5
    c: Coincident(g7,g1)
    c: Coincident(g7,g1)
    c: Coincident(g8,g1)
    c: Coincident(g8,g0)
    c: Coincident(g9,g0)
    c: Symmetric(g0,g0,g10)
    c: Horizontal(g10)
    c: Coincident(g10,g9)
    c: PointOnObject(g4,g10)
    c: Coincident(g11,g4)
    c: Coincident(g11,g9)
FEATURE [PartDesign::Pad] Pad051
  Direction = (0,1,-2e-16)
  Length = 10
  Length2 = 10
  Profile = -> Sketch114
  ReferenceAxis = -> Sketch114 [N_Axis]
  Refine = true
  Suppressed = false
  Type = 3
  UpToFace = -> Binder053 [Face11]
FEATURE [Sketcher::SketchObject] Sketch115
  ArcFitTolerance = 1e-06
  AttachmentSupport = -> [Pad051]
  ExternalGeometry = -> [Pad051,Binder053]
  FullyConstrained = false
  MakeInternals = false
  MapMode = 5
  Placement = pos=(0,4.579e-13,2081.2) rot=(0,0,1;0rad)
  sketch-geometry (10):
    g0: LineSegment [constr] StartX=1480.95 StartY=750 StartZ=0 EndX=1480.95 EndY=769.05 EndZ=0
    g1: LineSegment [constr] StartX=1499.99 StartY=769.05 StartZ=0 EndX=1480.95 EndY=769.05 EndZ=0
    g2: LineSegment [constr] StartX=1499.99 StartY=769.05 StartZ=0 EndX=1480.95 EndY=750 EndZ=0
    g3: Circle CenterX=1490.47 CenterY=759.525 CenterZ=0 NormalX=0 NormalY=0 NormalZ=1 AngleXU=0 Radius=5
    g4: LineSegment [constr] StartX=1480.95 StartY=1144.05 StartZ=0 EndX=1500 EndY=1144.05 EndZ=0
    g5: LineSegment [constr] StartX=1490.47 StartY=759.525 StartZ=0 EndX=1490.47 EndY=1144.05 EndZ=0
    g6: Circle CenterX=1490.47 CenterY=951.788 CenterZ=0 NormalX=0 NormalY=0 NormalZ=1 AngleXU=0 Radius=5
    g7: Circle CenterX=1490.47 CenterY=1144.05 CenterZ=0 NormalX=0 NormalY=0 NormalZ=1 AngleXU=0 Radius=5
    g8: Circle CenterX=1490.47 CenterY=1336.31 CenterZ=0 NormalX=0 NormalY=0 NormalZ=1 AngleXU=0 Radius=5
    g9: Circle CenterX=1490.47 CenterY=1528.58 CenterZ=0 NormalX=0 NormalY=0 NormalZ=1 AngleXU=0 Radius=5
  constraints (17):
    c: Coincident(g0,g-4)
    c: Vertical(g0)
    c: Coincident(g1,g-5)
    c: Horizontal(g1)
    c: Coincident(g1,g0)
    c: Coincident(g2,g1)
    c: Coincident(g2,g0)
    c: Symmetric(g2,g2,g3)
    c: Symmetric(g-6,g-6,g4)
    c: Symmetric(g-7,g-7,g4)
    c: Symmetric(g5,g5,g6)
    c: Coincident(g7,g5)
    c: Diameter(g7) = 10
    c: Diameter(g6) = 10
    c: Diameter(g3) = 10
    c: Diameter(g8) = 10
    c: Diameter(g9) = 10
FEATURE [PartDesign::Pocket] Pocket059
  BaseFeature = -> Pad051
  Direction = (0,0,-1)
  Length = 5
  Length2 = 5
  Profile = -> Sketch115
  ReferenceAxis = -> Sketch115 [N_Axis]
  Refine = true
  Suppressed = false
  Type = 0
FEATURE [Sketcher::SketchObject] Sketch116
  ArcFitTolerance = 1e-06
  AttachmentSupport = -> [Pocket059]
  ExternalGeometry = -> [Pocket059]
  FullyConstrained = false
  MakeInternals = false
  MapMode = 5
  Placement = pos=(1684.3,4.341e-13,1919.48) rot=(0,1,0;0.720231rad)
  sketch-geometry (11):
    g0: LineSegment [constr] StartX=426.62 StartY=1144.05 StartZ=0 EndX=-245.193 EndY=1144.05 EndZ=0
    g1: LineSegment [constr] StartX=90.7134 StartY=1538.1 StartZ=0 EndX=90.7134 EndY=750 EndZ=0
    g2: LineSegment [constr] StartX=-245.193 StartY=1528.58 StartZ=0 EndX=-252.358 EndY=1528.58 EndZ=0
    g3: LineSegment [constr] StartX=-245.193 StartY=1528.58 StartZ=0 EndX=90.7134 EndY=1528.58 EndZ=0
    g4: LineSegment [constr] StartX=90.7134 StartY=1528.58 StartZ=0 EndX=426.62 EndY=1528.58 EndZ=0
    g5: Circle CenterX=-77.2398 CenterY=1528.58 CenterZ=0 NormalX=0 NormalY=0 NormalZ=1 AngleXU=0 Radius=5
    g6: Circle CenterX=90.7134 CenterY=1528.58 CenterZ=0 NormalX=0 NormalY=0 NormalZ=1 AngleXU=0 Radius=5
    g7: Circle CenterX=320.484 CenterY=1528.58 CenterZ=0 NormalX=0 NormalY=0 NormalZ=1 AngleXU=0 Radius=5
    g8: Circle CenterX=320.484 CenterY=759.525 CenterZ=0 NormalX=0 NormalY=0 NormalZ=1 AngleXU=0 Radius=5
    g9: Circle CenterX=90.7134 CenterY=759.525 CenterZ=0 NormalX=0 NormalY=0 NormalZ=1 AngleXU=0 Radius=5
    g10: Circle CenterX=-77.2398 CenterY=759.525 CenterZ=0 NormalX=0 NormalY=0 NormalZ=1 AngleXU=0 Radius=5
  constraints (22):
    c: Symmetric(g-6,g-6,g0)
    c: Symmetric(g-5,g-5,g0)
    c: Symmetric(g-3,g-3,g1)
    c: Symmetric(g-7,g-7,g1)
    c: PointOnObject(g2,g-5)
    c: Coincident(g2,g-4)
    c: Horizontal(g2)
    c: Coincident(g3,g2)
    c: PointOnObject(g3,g1)
    c: Horizontal(g3)
    c: Coincident(g4,g3)
    c: PointOnObject(g4,g-6)
    c: Horizontal(g4)
    c: Symmetric(g3,g3,g5)
    c: Coincident(g6,g3)
    c: PointOnObject(g7,g4)
    c: Equal(g7,g6)
    c: Equal(g7,g5)
    c: Diameter(g7) = 10
    c: Equal(g8,g9)
    c: Equal(g8,g10)
    c: Diameter(g8) = 10
FEATURE [PartDesign::Pocket] Pocket060
  BaseFeature = -> Pocket059
  Direction = (-0.659558,0,-0.751653)
  Length = 5
  Length2 = 5
  Profile = -> Sketch116
  ReferenceAxis = -> Sketch116 [N_Axis]
  Refine = true
  Suppressed = false
  Type = 0
FEATURE [Sketcher::SketchObject] Sketch117
  ArcFitTolerance = 1e-06
  AttachmentSupport = -> [Pocket060]
  ExternalGeometry = -> [Pocket060]
  FullyConstrained = false
  MakeInternals = false
  MapMode = 5
  Placement = pos=(2004.97,0,0) rot=(0.57735,0.57735,0.57735;2.0944rad)
  sketch-geometry (9):
    g0: LineSegment [constr] StartX=1144.05 StartY=1638.1 StartZ=0 EndX=1144.05 EndY=1619.21 EndZ=0
    g1: LineSegment [constr] StartX=750 StartY=1628.66 StartZ=0 EndX=1144.05 EndY=1628.66 EndZ=0
    g2: LineSegment [constr] StartX=1528.58 StartY=1704.81 StartZ=0 EndX=1528.58 EndY=1628.66 EndZ=0
    g3: Circle CenterX=1528.58 CenterY=1628.66 CenterZ=0 NormalX=0 NormalY=0 NormalZ=1 AngleXU=0 Radius=5
    g4: Circle CenterX=1144.05 CenterY=1628.66 CenterZ=0 NormalX=0 NormalY=0 NormalZ=1 AngleXU=0 Radius=5
    g5: LineSegment [constr] StartX=1528.58 StartY=1628.66 StartZ=0 EndX=1144.05 EndY=1628.66 EndZ=0
    g6: Circle CenterX=1336.31 CenterY=1628.66 CenterZ=0 NormalX=0 NormalY=0 NormalZ=1 AngleXU=0 Radius=5
    g7: Circle CenterX=951.788 CenterY=1628.66 CenterZ=0 NormalX=0 NormalY=0 NormalZ=1 AngleXU=0 Radius=5
    g8: Circle CenterX=759.525 CenterY=1628.66 CenterZ=0 NormalX=0 NormalY=0 NormalZ=1 AngleXU=0 Radius=5
  constraints (17):
    c: Symmetric(g-6,g-6,g0)
    c: Symmetric(g-5,g-5,g0)
    c: Symmetric(g-7,g-7,g1)
    c: Symmetric(g0,g0,g1)
    c: Coincident(g2,g-9)
    c: Vertical(g2)
    c: Coincident(g3,g2)
    c: Coincident(g4,g1)
    c: Coincident(g5,g2)
    c: Coincident(g5,g1)
    c: Horizontal(g5)
    c: Symmetric(g5,g5,g6)
    c: Diameter(g4) = 10
    c: Diameter(g6) = 10
    c: Diameter(g3) = 10
    c: Diameter(g7) = 10
    c: Diameter(g8) = 10
FEATURE [PartDesign::Pocket] Pocket061
  BaseFeature = -> Pocket060
  Direction = (-1,0,0)
  Length = 5
  Length2 = 5
  Profile = -> Sketch117
  ReferenceAxis = -> Sketch117 [N_Axis]
  Refine = true
  Suppressed = false
  Type = 1
FEATURE [PartDesign::Body] Body047  label="Cuerpo073"
  AllowCompound = false
  Group = -> [Binder053,Sketch114,Pad051,Sketch115,Pocket059,Sketch116,Pocket060,Sketch117,Pocket061]
  Origin = -> Origin050
  Placement = pos=(0,-788.1,-4.547e-13) rot=(0,0,1;0rad)
  Tip = -> Pocket061
FEATURE [App::DocumentObjectGroup] Group016  label="superior"
  Group = -> [Body039,Body040,Body041,Body045,Body046,Body047]
FEATURE [PartDesign::SubShapeBinder] Binder054  label="Binder055"
  BindCopyOnChange = 0
  BindMode = 2
  ClaimChildren = false
  Context = -> Body048 [Binder054.]
  Fuse = false
  MakeFace = true
  OffsetFill = false
  OffsetIntersection = false
  OffsetJoinType = 0
  OffsetOpenResult = false
  PartialLoad = false
  Refine = true
  Relative = true
  _Version = 2
FEATURE [Sketcher::SketchObject] Sketch118
  ArcFitTolerance = 1e-06
  AttachmentSupport = -> [Binder054]
  ExternalGeometry = -> [Binder054]
  FullyConstrained = false
  MakeInternals = false
  MapMode = 5
  Placement = pos=(0,-38.1,0) rot=(1,0,0;1.5708rad)
  sketch-geometry (30):
    g0: LineSegment [constr] StartX=1500 StartY=638.1 StartZ=0 EndX=1480.95 EndY=638.1 EndZ=0
    g1: LineSegment [constr] StartX=1500 StartY=600 StartZ=0 EndX=1480.95 EndY=600 EndZ=0
    g2: LineSegment [constr] StartX=1480.95 StartY=638.1 StartZ=0 EndX=1480.95 EndY=600 EndZ=0
    g3: LineSegment [constr] StartX=1480.95 StartY=619.05 StartZ=0 EndX=1999.97 EndY=619.05 EndZ=0
    g4: LineSegment StartX=1480.95 StartY=619.05 StartZ=0 EndX=1480.95 EndY=7.958e-13 EndZ=0
    g5: LineSegment StartX=1480.95 StartY=7.958e-13 StartZ=0 EndX=1999.97 EndY=7.958e-13 EndZ=0
    g6: LineSegment StartX=1999.97 StartY=7.958e-13 StartZ=0 EndX=1999.97 EndY=619.05 EndZ=0
    g7: LineSegment StartX=1999.97 StartY=619.05 StartZ=0 EndX=1480.95 EndY=619.05 EndZ=0
    g8: LineSegment [constr] StartX=1480.95 StartY=619.05 StartZ=0 EndX=1500 EndY=600 EndZ=0
    g9: Circle CenterX=1490.47 CenterY=609.525 CenterZ=0 NormalX=0 NormalY=0 NormalZ=1 AngleXU=0 Radius=4.44505
    g10: LineSegment [constr] StartX=1480.95 StartY=309.525 StartZ=0 EndX=1999.97 EndY=309.525 EndZ=0
    g11: LineSegment [constr] StartX=1490.47 StartY=609.525 StartZ=0 EndX=1490.47 EndY=309.525 EndZ=0
    g12: Circle CenterX=1490.47 CenterY=459.525 CenterZ=0 NormalX=0 NormalY=0 NormalZ=1 AngleXU=0 Radius=5
    g13: Circle CenterX=1490.47 CenterY=309.525 CenterZ=0 NormalX=0 NormalY=0 NormalZ=1 AngleXU=0 Radius=5
    g14: Circle CenterX=1490.47 CenterY=159.525 CenterZ=0 NormalX=0 NormalY=0 NormalZ=1 AngleXU=0 Radius=5
    g15: Circle CenterX=1490.47 CenterY=9.525 CenterZ=0 NormalX=0 NormalY=0 NormalZ=1 AngleXU=0 Radius=4.44505
    g16: LineSegment [constr] StartX=1740.46 StartY=7.53e-13 StartZ=0 EndX=1740.46 EndY=619.05 EndZ=0
    g17: Circle CenterX=1990.45 CenterY=609.525 CenterZ=0 NormalX=0 NormalY=0 NormalZ=1 AngleXU=0 Radius=4.44505
    g18: Circle CenterX=1990.45 CenterY=459.525 CenterZ=0 NormalX=0 NormalY=0 NormalZ=1 AngleXU=0 Radius=5
    g19: Circle CenterX=1990.45 CenterY=309.525 CenterZ=0 NormalX=0 NormalY=0 NormalZ=1 AngleXU=0 Radius=5
    g20: Circle CenterX=1990.45 CenterY=159.525 CenterZ=0 NormalX=0 NormalY=0 NormalZ=1 AngleXU=0 Radius=5
    g21: Circle CenterX=1990.45 CenterY=9.525 CenterZ=0 NormalX=0 NormalY=0 NormalZ=1 AngleXU=0 Radius=4.44505
    g22: LineSegment [constr] StartX=1990.45 StartY=609.525 StartZ=0 EndX=1740.46 EndY=609.525 EndZ=0
    g23: LineSegment [constr] StartX=1740.46 StartY=609.525 StartZ=0 EndX=1490.47 EndY=609.525 EndZ=0
    g24: Circle CenterX=1865.45 CenterY=609.525 CenterZ=0 NormalX=0 NormalY=0 NormalZ=1 AngleXU=0 Radius=5
    g25: Circle CenterX=1740.46 CenterY=609.525 CenterZ=0 NormalX=0 NormalY=0 NormalZ=1 AngleXU=0 Radius=5
    g26: Circle CenterX=1615.47 CenterY=609.525 CenterZ=0 NormalX=0 NormalY=0 NormalZ=1 AngleXU=0 Radius=5
    g27: Circle CenterX=1865.45 CenterY=9.525 CenterZ=0 NormalX=0 NormalY=0 NormalZ=1 AngleXU=0 Radius=5
    g28: Circle CenterX=1740.46 CenterY=9.525 CenterZ=0 NormalX=0 NormalY=0 NormalZ=1 AngleXU=0 Radius=5
    g29: Circle CenterX=1615.47 CenterY=9.525 CenterZ=0 NormalX=0 NormalY=0 NormalZ=1 AngleXU=0 Radius=5
  constraints (53):
    c: Coincident(g0,g-3)
    c: PointOnObject(g0,g-7)
    c: Horizontal(g0)
    c: Coincident(g1,g-8)
    c: PointOnObject(g1,g-7)
    c: Horizontal(g1)
    c: Coincident(g2,g0)
    c: Coincident(g2,g1)
    c: Symmetric(g2,g2,g3)
    c: PointOnObject(g3,g-4)
    c: Horizontal(g3)
    c: Coincident(g4,g5)
    c: Coincident(g5,g6)
    c: Coincident(g6,g7)
    c: Coincident(g7,g4)
    c: Vertical(g4)
    c: Vertical(g6)
    c: Horizontal(g5)
    c: Horizontal(g7)
    c: Coincident(g4,g3)
    c: Coincident(g5,g-5)
    c: Coincident(g8,g3)
    c: Coincident(g8,g1)
    c: Symmetric(g8,g8,g9)
    c: Symmetric(g4,g4,g10)
    c: Symmetric(g6,g6,g10)
    c: Coincident(g11,g9)
    c: PointOnObject(g11,g10)
    c: Vertical(g11)
    c: Symmetric(g11,g11,g12)
    c: Coincident(g13,g11)
    c: Diameter(g12) = 10
    c: Diameter(g13) = 10
    c: Diameter(g14) = 10
    c: Symmetric(g5,g5,g16)
    c: Symmetric(g7,g7,g16)
    c: Diameter(g18) = 10
    c: Diameter(g19) = 10
    c: Diameter(g20) = 10
    c: Coincident(g22,g17)
    c: PointOnObject(g22,g16)
    c: Horizontal(g22)
    c: Coincident(g23,g22)
    c: Coincident(g23,g9)
    c: Horizontal(g23)
    c: Symmetric(g22,g22,g24)
    c: Coincident(g25,g22)
    c: Diameter(g26) = 10
    c: Diameter(g25) = 10
    c: Diameter(g24) = 10
    c: Diameter(g29) = 10
    c: Diameter(g28) = 10
    c: Diameter(g27) = 10
FEATURE [PartDesign::Pad] Pad052
  Direction = (0,-1,2e-16)
  Length = 5
  Length2 = 10
  Profile = -> Sketch118
  ReferenceAxis = -> Sketch118 [N_Axis]
  Refine = true
  Suppressed = false
  Type = 0
FEATURE [PartDesign::Body] Body048  label="Cuerpo074"
  AllowCompound = false
  Group = -> [Binder054,Sketch118,Pad052]
  Origin = -> Origin051
  Tip = -> Pad052
FEATURE [PartDesign::SubShapeBinder] Binder055  label="Binder056"
  BindCopyOnChange = 0
  BindMode = 2
  ClaimChildren = false
  Context = -> Part002 [Body049.Binder055.]
  Fuse = false
  MakeFace = true
  OffsetFill = false
  OffsetIntersection = false
  OffsetJoinType = 0
  OffsetOpenResult = false
  PartialLoad = false
  Refine = true
  Relative = true
  _Version = 2
FEATURE [Sketcher::SketchObject] Sketch119
  ArcFitTolerance = 1e-06
  AttachmentSupport = -> [Binder055]
  ExternalGeometry = -> [Binder055]
  FullyConstrained = false
  MakeInternals = false
  MapMode = 5
  Placement = pos=(0,-38.1,0) rot=(1,0,0;1.5708rad)
  sketch-geometry (35):
    g0: LineSegment StartX=1999.97 StartY=619.05 StartZ=0 EndX=1480.95 EndY=619.05 EndZ=0
    g1: LineSegment StartX=1480.95 StartY=619.05 StartZ=0 EndX=1480.95 EndY=2076.2 EndZ=0
    g2: LineSegment StartX=1480.95 StartY=2076.2 StartZ=0 EndX=1500 EndY=2076.2 EndZ=0
    g3: LineSegment StartX=1500 StartY=2076.2 StartZ=0 EndX=1999.97 EndY=1638.1 EndZ=0
    g4: LineSegment StartX=1999.97 StartY=1638.1 StartZ=0 EndX=1999.97 EndY=619.05 EndZ=0
    g5: LineSegment [constr] StartX=1961.9 StartY=1620.8 StartZ=0 EndX=1999.97 EndY=1638.1 EndZ=0
    g6: LineSegment [constr] StartX=1500 StartY=2025.54 StartZ=0 EndX=1500 EndY=2076.2 EndZ=0
    g7: LineSegment [constr] StartX=1500 StartY=638.1 StartZ=0 EndX=1480.95 EndY=619.05 EndZ=0
    g8: Circle CenterX=1490.47 CenterY=628.575 CenterZ=0 NormalX=0 NormalY=0 NormalZ=1 AngleXU=0 Radius=5
    g9: LineSegment [constr] StartX=1480.95 StartY=1347.62 StartZ=0 EndX=1999.97 EndY=1347.62 EndZ=0
    g10: LineSegment [constr] StartX=1740.46 StartY=619.05 StartZ=0 EndX=1740.46 EndY=1840.17 EndZ=0
    g11: Circle CenterX=1980.94 CenterY=628.575 CenterZ=0 NormalX=0 NormalY=0 NormalZ=1 AngleXU=0 Radius=5
    g12: Circle CenterX=1490.47 CenterY=2066.68 CenterZ=0 NormalX=0 NormalY=0 NormalZ=1 AngleXU=0 Radius=5
    g13: LineSegment [constr] StartX=1980.94 StartY=628.575 StartZ=0 EndX=1740.46 EndY=628.575 EndZ=0
    g14: LineSegment [constr] StartX=1740.46 StartY=628.575 StartZ=0 EndX=1490.47 EndY=628.575 EndZ=0
    g15: LineSegment [constr] StartX=1490.47 StartY=628.575 StartZ=0 EndX=1490.47 EndY=1347.62 EndZ=0
    g16: LineSegment [constr] StartX=1490.47 StartY=1347.62 StartZ=0 EndX=1490.47 EndY=2066.68 EndZ=0
    g17: Circle CenterX=1490.47 CenterY=1347.62 CenterZ=0 NormalX=0 NormalY=0 NormalZ=1 AngleXU=0 Radius=5
    g18: Circle CenterX=1490.47 CenterY=1707.15 CenterZ=0 NormalX=0 NormalY=0 NormalZ=1 AngleXU=0 Radius=5
    g19: Circle CenterX=1490.47 CenterY=988.1 CenterZ=0 NormalX=0 NormalY=0 NormalZ=1 AngleXU=0 Radius=5
    g20: Circle CenterX=1740.46 CenterY=628.575 CenterZ=0 NormalX=0 NormalY=0 NormalZ=1 AngleXU=0 Radius=5
    g21: Circle CenterX=1860.7 CenterY=628.575 CenterZ=0 NormalX=0 NormalY=0 NormalZ=1 AngleXU=0 Radius=5
    g22: Circle CenterX=1615.47 CenterY=628.575 CenterZ=0 NormalX=0 NormalY=0 NormalZ=1 AngleXU=0 Radius=5
    g23: Circle CenterX=1980.94 CenterY=1629.45 CenterZ=0 NormalX=0 NormalY=0 NormalZ=1 AngleXU=0 Radius=5
    g24: Circle CenterX=1740.46 CenterY=1840.17 CenterZ=0 NormalX=0 NormalY=0 NormalZ=1 AngleXU=0 Radius=5
    g25: LineSegment [constr] StartX=1980.94 StartY=1629.45 StartZ=0 EndX=1740.46 EndY=1840.17 EndZ=0
    g26: LineSegment [constr] StartX=1740.46 StartY=1840.17 StartZ=0 EndX=1490.47 EndY=2066.68 EndZ=0
    g27: Circle CenterX=1615.47 CenterY=1953.42 CenterZ=0 NormalX=0 NormalY=0 NormalZ=1 AngleXU=0 Radius=5
    g28: Circle CenterX=1860.7 CenterY=1734.81 CenterZ=0 NormalX=0 NormalY=0 NormalZ=1 AngleXU=0 Radius=5
    g29: LineSegment [constr] StartX=1999.97 StartY=1128.57 StartZ=0 EndX=1480.95 EndY=1128.57 EndZ=0
    g30: LineSegment [constr] StartX=1980.94 StartY=628.575 StartZ=0 EndX=1980.94 EndY=1128.57 EndZ=0
    g31: LineSegment [constr] StartX=1980.94 StartY=1128.57 StartZ=0 EndX=1980.94 EndY=1629.45 EndZ=0
    g32: Circle CenterX=1980.94 CenterY=1379.01 CenterZ=0 NormalX=0 NormalY=0 NormalZ=1 AngleXU=0 Radius=5
    g33: Circle CenterX=1980.94 CenterY=878.575 CenterZ=0 NormalX=0 NormalY=0 NormalZ=1 AngleXU=0 Radius=5
    g34: Circle CenterX=1980.94 CenterY=1128.57 CenterZ=0 NormalX=0 NormalY=0 NormalZ=1 AngleXU=0 Radius=5
  constraints (75):
    c: Coincident(g0,g-3)
    c: Coincident(g0,g-3)
    c: Coincident(g1,g0)
    c: Coincident(g1,g-7)
    c: Coincident(g2,g1)
    c: Coincident(g2,g-8)
    c: Coincident(g3,g2)
    c: Coincident(g3,g-6)
    c: Coincident(g4,g3)
    c: Coincident(g4,g0)
    c: Coincident(g5,g-10)
    c: Coincident(g5,g3)
    c: Coincident(g6,g-9)
    c: Coincident(g6,g2)
    c: Coincident(g7,g-11)
    c: Coincident(g7,g0)
    c: Symmetric(g7,g7,g8)
    c: Symmetric(g1,g1,g9)
    c: PointOnObject(g9,g4)
    c: Horizontal(g9)
    c: Diameter(g8) = 10
    c: Symmetric(g0,g0,g10)
    c: Vertical(g10)
    c: Diameter(g11) = 10
    c: Diameter(g12) = 10
    c: Coincident(g13,g11)
    c: PointOnObject(g13,g10)
    c: Horizontal(g13)
    c: Coincident(g14,g13)
    c: Coincident(g14,g8)
    c: Horizontal(g14)
    c: Coincident(g15,g8)
    c: PointOnObject(g15,g9)
    c: Vertical(g15)
    c: Coincident(g16,g15)
    c: Coincident(g16,g12)
    c: Vertical(g16)
    c: Coincident(g17,g15)
    c: Symmetric(g16,g16,g18)
    c: Symmetric(g15,g15,g19)
    c: Diameter(g19) = 10
    c: Diameter(g17) = 10
    c: Diameter(g18) = 10
    c: Coincident(g20,g13)
    c: Symmetric(g13,g13,g21)
    c: Symmetric(g14,g14,g22)
    c: Diameter(g23) = 10
    c: Coincident(g24,g10)
    c: Coincident(g25,g23)
    c: Coincident(g25,g10)
    c: Coincident(g26,g10)
    c: Coincident(g26,g12)
    c: Symmetric(g26,g26,g27)
    c: Symmetric(g25,g25,g28)
    c: Diameter(g28) = 10
    c: Diameter(g24) = 10
    c: Diameter(g27) = 10
    c: Diameter(g21) = 10
    c: Diameter(g20) = 10
    c: Diameter(g22) = 10
    c: Symmetric(g4,g4,g29)
    c: PointOnObject(g29,g1)
    c: Horizontal(g29)
    c: Coincident(g30,g11)
    c: PointOnObject(g30,g29)
    c: Vertical(g30)
    c: Coincident(g31,g30)
    c: Coincident(g31,g23)
    c: Vertical(g31)
    c: Symmetric(g31,g31,g32)
    c: Symmetric(g30,g30,g33)
    c: Coincident(g34,g30)
    c: Diameter(g33) = 10
    c: Diameter(g34) = 10
    c: Diameter(g32) = 10
FEATURE [PartDesign::Pad] Pad053
  Direction = (0,-1,2e-16)
  Length = 5
  Length2 = 10
  Profile = -> Sketch119
  ReferenceAxis = -> Sketch119 [N_Axis]
  Refine = true
  Suppressed = false
  Type = 0
FEATURE [PartDesign::Body] Body049  label="Cuerpo075"
  AllowCompound = false
  Group = -> [Binder055,Sketch119,Pad053]
  Origin = -> Origin052
  Tip = -> Pad053
FEATURE [App::DocumentObjectGroup] Group015  label="lados"
  Group = -> [Body035,Body043,Body042,Body044,Body048,Body049]
FEATURE [PartDesign::SubShapeBinder] Binder056  label="Binder057"
  BindCopyOnChange = 0
  BindMode = 2
  ClaimChildren = false
  Context = -> Part002 [Body050.Binder056.]
  Fuse = false
  MakeFace = true
  OffsetFill = false
  OffsetIntersection = false
  OffsetJoinType = 0
  OffsetOpenResult = false
  PartialLoad = false
  Refine = true
  Relative = true
  _Version = 2
FEATURE [Sketcher::SketchObject] Sketch120
  ArcFitTolerance = 1e-06
  AttachmentSupport = -> [Binder056]
  ExternalGeometry = -> [Binder056]
  FullyConstrained = false
  MakeInternals = false
  MapMode = 5
  Placement = pos=(0,-38.1,0) rot=(1,0,0;1.5708rad)
  sketch-geometry (37):
    g0: LineSegment [constr] StartX=538.071 StartY=1038.1 StartZ=0 EndX=999.985 EndY=1038.1 EndZ=0
    g1: LineSegment [constr] StartX=999.985 StartY=2038.1 StartZ=0 EndX=999.985 EndY=1038.1 EndZ=0
    g2: LineSegment [constr] StartX=538.071 StartY=1038.1 StartZ=0 EndX=499.971 EndY=1038.1 EndZ=0
    g3: LineSegment [constr] StartX=999.985 StartY=2038.1 StartZ=0 EndX=999.985 EndY=2076.2 EndZ=0
    g4: LineSegment StartX=999.985 StartY=1038.1 StartZ=0 EndX=999.985 EndY=2076.2 EndZ=0
    g5: LineSegment StartX=999.985 StartY=2076.2 StartZ=0 EndX=499.971 EndY=2076.2 EndZ=0
    g6: LineSegment StartX=499.971 StartY=2076.2 StartZ=0 EndX=499.971 EndY=1038.1 EndZ=0
    g7: LineSegment StartX=499.971 StartY=1038.1 StartZ=0 EndX=999.985 EndY=1038.1 EndZ=0
    g8: LineSegment [constr] StartX=999.985 StartY=1038.1 StartZ=0 EndX=980.935 EndY=1057.15 EndZ=0
    g9: Circle CenterX=988.253 CenterY=1047.62 CenterZ=0 NormalX=0 NormalY=0 NormalZ=1 AngleXU=0 Radius=5
    g10: LineSegment [constr] StartX=749.978 StartY=2076.2 StartZ=0 EndX=749.978 EndY=1057.15 EndZ=0
    g11: Circle CenterX=509.496 CenterY=1047.63 CenterZ=0 NormalX=0 NormalY=0 NormalZ=1 AngleXU=0 Radius=5
    g12: LineSegment [constr] StartX=499.971 StartY=1557.15 StartZ=0 EndX=999.985 EndY=1557.15 EndZ=0
    g13: LineSegment [constr] StartX=509.496 StartY=1047.63 StartZ=0 EndX=990.46 EndY=1047.63 EndZ=0
    g14: LineSegment [constr] StartX=749.978 StartY=1047.63 StartZ=0 EndX=749.978 EndY=1038.1 EndZ=0
    g15: LineSegment [constr] StartX=990.46 StartY=1047.63 StartZ=0 EndX=990.46 EndY=1038.1 EndZ=0
    g16: LineSegment [constr] StartX=990.46 StartY=1042.86 StartZ=0 EndX=749.978 EndY=1043.57 EndZ=0
    g17: LineSegment [constr] StartX=509.496 StartY=1047.63 StartZ=0 EndX=509.496 EndY=1038.1 EndZ=0
    g18: LineSegment [constr] StartX=749.978 StartY=1043.57 StartZ=0 EndX=509.496 EndY=1043.57 EndZ=0
    g19: LineSegment [constr] StartX=870.219 StartY=1043.22 StartZ=0 EndX=870.219 EndY=1047.62 EndZ=0
    g20: LineSegment [constr] StartX=629.737 StartY=1043.57 StartZ=0 EndX=629.737 EndY=1047.62 EndZ=0
    g21: Circle CenterX=749.978 CenterY=1047.63 CenterZ=0 NormalX=0 NormalY=0 NormalZ=1 AngleXU=0 Radius=5
    g22: Circle CenterX=870.219 CenterY=1047.62 CenterZ=0 NormalX=0 NormalY=0 NormalZ=1 AngleXU=0 Radius=5
    g23: Circle CenterX=629.737 CenterY=1047.62 CenterZ=0 NormalX=0 NormalY=0 NormalZ=1 AngleXU=0 Radius=5
    g24: LineSegment [constr] StartX=988.253 StartY=1047.62 StartZ=0 EndX=988.253 EndY=1557.15 EndZ=0
    g25: Circle CenterX=988.253 CenterY=1302.39 CenterZ=0 NormalX=0 NormalY=0 NormalZ=1 AngleXU=0 Radius=5
    g26: Circle CenterX=988.253 CenterY=1557.15 CenterZ=0 NormalX=0 NormalY=0 NormalZ=1 AngleXU=0 Radius=5
    g27: Circle CenterX=988.253 CenterY=1557.15 CenterZ=0 NormalX=0 NormalY=0 NormalZ=1 AngleXU=0 Radius=5
    g28: Circle CenterX=988.253 CenterY=2066.67 CenterZ=0 NormalX=0 NormalY=0 NormalZ=1 AngleXU=0 Radius=5
    g29: Circle CenterX=988.253 CenterY=1811.91 CenterZ=0 NormalX=0 NormalY=0 NormalZ=1 AngleXU=0 Radius=5
    g30: Circle CenterX=511.703 CenterY=2066.67 CenterZ=0 NormalX=0 NormalY=0 NormalZ=1 AngleXU=0 Radius=5
    g31: Circle CenterX=511.703 CenterY=1811.91 CenterZ=0 NormalX=0 NormalY=0 NormalZ=1 AngleXU=0 Radius=5
    g32: Circle CenterX=511.703 CenterY=1557.15 CenterZ=0 NormalX=0 NormalY=0 NormalZ=1 AngleXU=0 Radius=5
    g33: Circle CenterX=511.703 CenterY=1302.39 CenterZ=0 NormalX=0 NormalY=0 NormalZ=1 AngleXU=0 Radius=5
    g34: Circle CenterX=629.737 CenterY=2066.67 CenterZ=0 NormalX=0 NormalY=0 NormalZ=1 AngleXU=0 Radius=5
    g35: Circle CenterX=749.978 CenterY=2066.67 CenterZ=0 NormalX=0 NormalY=0 NormalZ=1 AngleXU=0 Radius=5
    g36: Circle CenterX=870.219 CenterY=2066.67 CenterZ=0 NormalX=0 NormalY=0 NormalZ=1 AngleXU=0 Radius=5
  constraints (69):
    c: Symmetric(g-3,g-3,g0)
    c: Horizontal(g0)
    c: Symmetric(g-6,g-6,g1)
    c: Vertical(g1)
    c: Coincident(g1,g0)
    c: Coincident(g2,g0)
    c: Symmetric(g-9,g-9,g2)
    c: Coincident(g3,g1)
    c: Symmetric(g-10,g-10,g3)
    c: Coincident(g4,g5)
    c: Coincident(g5,g6)
    c: Coincident(g6,g7)
    c: Coincident(g7,g4)
    c: Vertical(g4)
    c: Vertical(g6)
    c: Horizontal(g5)
    c: Horizontal(g7)
    c: Coincident(g4,g0)
    c: Coincident(g5,g-10)
    c: Coincident(g8,g0)
    c: Coincident(g8,g-7)
    c: Diameter(g9) = 10
    c: Symmetric(g5,g5,g10)
    c: PointOnObject(g10,g-4)
    c: Vertical(g10)
    c: Diameter(g11) = 10
    c: Symmetric(g6,g6,g12)
    c: Symmetric(g4,g4,g12)
    c: Coincident(g13,g11)
    c: Horizontal(g13)
    c: Symmetric(g13,g13,g14)
    c: Symmetric(g7,g7,g14)
    c: Vertical(g14)
    c: PointOnObject(g15,g7)
    c: Vertical(g15)
    c: Coincident(g17,g11)
    c: PointOnObject(g17,g7)
    c: Vertical(g17)
    c: Horizontal(g18)
    c: PointOnObject(g18,g17)
    c: Symmetric(g16,g16,g19)
    c: PointOnObject(g19,g13)
    c: Vertical(g19)
    c: Symmetric(g18,g18,g20)
    c: PointOnObject(g20,g13)
    c: Vertical(g20)
    c: Coincident(g21,g14)
    c: Coincident(g22,g19)
    c: Coincident(g23,g20)
    c: Diameter(g23) = 10
    c: Diameter(g21) = 10
    c: Diameter(g22) = 10
    c: Coincident(g24,g9)
    c: PointOnObject(g24,g12)
    c: Vertical(g24)
    c: Symmetric(g24,g24,g25)
    c: Coincident(g26,g24)
    c: Diameter(g26) = 10
    c: Diameter(g25) = 10
    c: Diameter(g28) = 10
    c: Diameter(g27) = 10
    c: Diameter(g29) = 10
    c: Diameter(g32) = 10
    c: Diameter(g33) = 10
    c: Diameter(g30) = 10
    c: Diameter(g31) = 10
    c: Diameter(g34) = 10
    c: Diameter(g35) = 10
    c: Diameter(g36) = 10
FEATURE [PartDesign::Pad] Pad054
  Direction = (0,-1,2e-16)
  Length = 5
  Length2 = 10
  Profile = -> Sketch120
  ReferenceAxis = -> Sketch120 [N_Axis]
  Refine = true
  Suppressed = false
  Type = 0
FEATURE [PartDesign::Body] Body050  label="Cuerpo076"
  AllowCompound = false
  Group = -> [Binder056,Sketch120,Pad054]
  Origin = -> Origin053
  Placement = pos=(0,1581.2,-1038.1) rot=(0,0,1;0rad)
  Tip = -> Pad054
FEATURE [PartDesign::SubShapeBinder] Binder057  label="Binder058"
  BindCopyOnChange = 0
  BindMode = 2
  ClaimChildren = false
  Context = -> Part002 [Body035.Binder039.]
  Fuse = false
  MakeFace = true
  OffsetFill = false
  OffsetIntersection = false
  OffsetJoinType = 0
  OffsetOpenResult = false
  PartialLoad = false
  Refine = true
  Relative = true
  _Version = 2
FEATURE [Sketcher::SketchObject] Sketch121
  ArcFitTolerance = 1e-06
  AttachmentSupport = -> [Binder057]
  ExternalGeometry = -> [Binder057]
  FullyConstrained = false
  MakeInternals = false
  MapMode = 5
  Placement = pos=(0,-38.1,0) rot=(1,0,0;1.5708rad)
  sketch-geometry (37):
    g0: LineSegment [constr] StartX=538.071 StartY=1038.1 StartZ=0 EndX=999.985 EndY=1038.1 EndZ=0
    g1: LineSegment [constr] StartX=999.985 StartY=2038.1 StartZ=0 EndX=999.985 EndY=1038.1 EndZ=0
    g2: LineSegment [constr] StartX=538.071 StartY=1038.1 StartZ=0 EndX=499.971 EndY=1038.1 EndZ=0
    g3: LineSegment [constr] StartX=999.985 StartY=2038.1 StartZ=0 EndX=999.985 EndY=2076.2 EndZ=0
    g4: LineSegment StartX=999.985 StartY=1038.1 StartZ=0 EndX=999.985 EndY=2076.2 EndZ=0
    g5: LineSegment StartX=999.985 StartY=2076.2 StartZ=0 EndX=499.971 EndY=2076.2 EndZ=0
    g6: LineSegment StartX=499.971 StartY=2076.2 StartZ=0 EndX=499.971 EndY=1038.1 EndZ=0
    g7: LineSegment StartX=499.971 StartY=1038.1 StartZ=0 EndX=999.985 EndY=1038.1 EndZ=0
    g8: LineSegment [constr] StartX=999.985 StartY=1038.1 StartZ=0 EndX=980.935 EndY=1057.15 EndZ=0
    g9: Circle CenterX=988.253 CenterY=1047.62 CenterZ=0 NormalX=0 NormalY=0 NormalZ=1 AngleXU=0 Radius=5
    g10: LineSegment [constr] StartX=749.978 StartY=2076.2 StartZ=0 EndX=749.978 EndY=1057.15 EndZ=0
    g11: Circle CenterX=509.496 CenterY=1047.63 CenterZ=0 NormalX=0 NormalY=0 NormalZ=1 AngleXU=0 Radius=5
    g12: LineSegment [constr] StartX=499.971 StartY=1557.15 StartZ=0 EndX=999.985 EndY=1557.15 EndZ=0
    g13: LineSegment [constr] StartX=509.496 StartY=1047.63 StartZ=0 EndX=990.46 EndY=1047.63 EndZ=0
    g14: LineSegment [constr] StartX=749.978 StartY=1047.63 StartZ=0 EndX=749.978 EndY=1038.1 EndZ=0
    g15: LineSegment [constr] StartX=990.46 StartY=1047.63 StartZ=0 EndX=990.46 EndY=1038.1 EndZ=0
    g16: LineSegment [constr] StartX=990.46 StartY=1042.86 StartZ=0 EndX=749.978 EndY=1043.57 EndZ=0
    g17: LineSegment [constr] StartX=509.496 StartY=1047.63 StartZ=0 EndX=509.496 EndY=1038.1 EndZ=0
    g18: LineSegment [constr] StartX=749.978 StartY=1043.57 StartZ=0 EndX=509.496 EndY=1043.57 EndZ=0
    g19: LineSegment [constr] StartX=870.219 StartY=1043.22 StartZ=0 EndX=870.219 EndY=1047.62 EndZ=0
    g20: LineSegment [constr] StartX=629.737 StartY=1043.57 StartZ=0 EndX=629.737 EndY=1047.62 EndZ=0
    g21: Circle CenterX=749.978 CenterY=1047.63 CenterZ=0 NormalX=0 NormalY=0 NormalZ=1 AngleXU=0 Radius=5
    g22: Circle CenterX=870.219 CenterY=1047.62 CenterZ=0 NormalX=0 NormalY=0 NormalZ=1 AngleXU=0 Radius=5
    g23: Circle CenterX=629.737 CenterY=1047.62 CenterZ=0 NormalX=0 NormalY=0 NormalZ=1 AngleXU=0 Radius=5
    g24: LineSegment [constr] StartX=988.253 StartY=1047.62 StartZ=0 EndX=988.253 EndY=1557.15 EndZ=0
    g25: Circle CenterX=988.253 CenterY=1302.39 CenterZ=0 NormalX=0 NormalY=0 NormalZ=1 AngleXU=0 Radius=5
    g26: Circle CenterX=988.253 CenterY=1557.15 CenterZ=0 NormalX=0 NormalY=0 NormalZ=1 AngleXU=0 Radius=5
    g27: Circle CenterX=988.253 CenterY=1557.15 CenterZ=0 NormalX=0 NormalY=0 NormalZ=1 AngleXU=0 Radius=5
    g28: Circle CenterX=988.253 CenterY=2066.67 CenterZ=0 NormalX=0 NormalY=0 NormalZ=1 AngleXU=0 Radius=5
    g29: Circle CenterX=988.253 CenterY=1811.91 CenterZ=0 NormalX=0 NormalY=0 NormalZ=1 AngleXU=0 Radius=5
    g30: Circle CenterX=511.703 CenterY=2066.67 CenterZ=0 NormalX=0 NormalY=0 NormalZ=1 AngleXU=0 Radius=5
    g31: Circle CenterX=511.703 CenterY=1811.91 CenterZ=0 NormalX=0 NormalY=0 NormalZ=1 AngleXU=0 Radius=5
    g32: Circle CenterX=511.703 CenterY=1557.15 CenterZ=0 NormalX=0 NormalY=0 NormalZ=1 AngleXU=0 Radius=5
    g33: Circle CenterX=511.703 CenterY=1302.39 CenterZ=0 NormalX=0 NormalY=0 NormalZ=1 AngleXU=0 Radius=5
    g34: Circle CenterX=629.737 CenterY=2066.67 CenterZ=0 NormalX=0 NormalY=0 NormalZ=1 AngleXU=0 Radius=5
    g35: Circle CenterX=749.978 CenterY=2066.67 CenterZ=0 NormalX=0 NormalY=0 NormalZ=1 AngleXU=0 Radius=5
    g36: Circle CenterX=870.219 CenterY=2066.67 CenterZ=0 NormalX=0 NormalY=0 NormalZ=1 AngleXU=0 Radius=5
  constraints (69):
    c: Symmetric(g-3,g-3,g0)
    c: Horizontal(g0)
    c: Symmetric(g-6,g-6,g1)
    c: Vertical(g1)
    c: Coincident(g1,g0)
    c: Coincident(g2,g0)
    c: Symmetric(g-9,g-9,g2)
    c: Coincident(g3,g1)
    c: Symmetric(g-10,g-10,g3)
    c: Coincident(g4,g5)
    c: Coincident(g5,g6)
    c: Coincident(g6,g7)
    c: Coincident(g7,g4)
    c: Vertical(g4)
    c: Vertical(g6)
    c: Horizontal(g5)
    c: Horizontal(g7)
    c: Coincident(g4,g0)
    c: Coincident(g5,g-10)
    c: Coincident(g8,g0)
    c: Coincident(g8,g-7)
    c: Diameter(g9) = 10
    c: Symmetric(g5,g5,g10)
    c: PointOnObject(g10,g-4)
    c: Vertical(g10)
    c: Diameter(g11) = 10
    c: Symmetric(g6,g6,g12)
    c: Symmetric(g4,g4,g12)
    c: Coincident(g13,g11)
    c: Horizontal(g13)
    c: Symmetric(g13,g13,g14)
    c: Symmetric(g7,g7,g14)
    c: Vertical(g14)
    c: PointOnObject(g15,g7)
    c: Vertical(g15)
    c: Coincident(g17,g11)
    c: PointOnObject(g17,g7)
    c: Vertical(g17)
    c: Horizontal(g18)
    c: PointOnObject(g18,g17)
    c: Symmetric(g16,g16,g19)
    c: PointOnObject(g19,g13)
    c: Vertical(g19)
    c: Symmetric(g18,g18,g20)
    c: PointOnObject(g20,g13)
    c: Vertical(g20)
    c: Coincident(g21,g14)
    c: Coincident(g22,g19)
    c: Coincident(g23,g20)
    c: Diameter(g23) = 10
    c: Diameter(g21) = 10
    c: Diameter(g22) = 10
    c: Coincident(g24,g9)
    c: PointOnObject(g24,g12)
    c: Vertical(g24)
    c: Symmetric(g24,g24,g25)
    c: Coincident(g26,g24)
    c: Diameter(g26) = 10
    c: Diameter(g25) = 10
    c: Diameter(g28) = 10
    c: Diameter(g27) = 10
    c: Diameter(g29) = 10
    c: Diameter(g32) = 10
    c: Diameter(g33) = 10
    c: Diameter(g30) = 10
    c: Diameter(g31) = 10
    c: Diameter(g34) = 10
    c: Diameter(g35) = 10
    c: Diameter(g36) = 10
FEATURE [PartDesign::Pad] Pad055
  Direction = (0,-1,2e-16)
  Length = 5
  Length2 = 10
  Profile = -> Sketch121
  ReferenceAxis = -> Sketch121 [N_Axis]
  Refine = true
  Suppressed = false
  Type = 0
FEATURE [PartDesign::Body] Body051  label="Cuerpo077"
  AllowCompound = false
  Group = -> [Binder057,Sketch121,Pad055]
  Origin = -> Origin054
  Placement = pos=(0,1581.2,-6.822e-13) rot=(0,0,1;0rad)
  Tip = -> Pad055
FEATURE [PartDesign::SubShapeBinder] Binder058  label="Binder059"
  BindCopyOnChange = 0
  BindMode = 2
  ClaimChildren = false
  Context = -> Body052 [Binder058.]
  Fuse = false
  MakeFace = true
  OffsetFill = false
  OffsetIntersection = false
  OffsetJoinType = 0
  OffsetOpenResult = false
  PartialLoad = false
  Refine = true
  Relative = true
  _Version = 2
FEATURE [PartDesign::SubShapeBinder] Binder059  label="Binder060"
  BindCopyOnChange = 0
  BindMode = 2
  ClaimChildren = false
  Context = -> Body052 [Binder059.]
  Fuse = false
  MakeFace = true
  OffsetFill = false
  OffsetIntersection = false
  OffsetJoinType = 0
  OffsetOpenResult = false
  PartialLoad = false
  Refine = true
  Relative = true
  _Version = 2
FEATURE [Sketcher::SketchObject] Sketch122
  ArcFitTolerance = 1e-06
  AttachmentSupport = -> [Binder059]
  ExternalGeometry = -> [Binder058,Binder059]
  FullyConstrained = false
  MakeInternals = false
  MapMode = 5
  Placement = pos=(0,-38.1,8.4e-15) rot=(1,0,0;1.5708rad)
  sketch-geometry (31):
    g0: LineSegment [constr] StartX=1500 StartY=38.1 StartZ=0 EndX=1500 EndY=7.461e-13 EndZ=0
    g1: LineSegment [constr] StartX=1500 StartY=38.1 StartZ=0 EndX=1461.9 EndY=38.1 EndZ=0
    g2: LineSegment [constr] StartX=1480.95 StartY=38.1 StartZ=0 EndX=1480.95 EndY=6.821e-13 EndZ=0
    g3: LineSegment [constr] StartX=1480.95 StartY=38.1 StartZ=0 EndX=1480.95 EndY=1038.1 EndZ=0
    g4: LineSegment StartX=999.985 StartY=1038.1 StartZ=0 EndX=999.985 EndY=6.821e-13 EndZ=0
    g5: LineSegment StartX=999.985 StartY=6.821e-13 StartZ=0 EndX=1480.95 EndY=6.821e-13 EndZ=0
    g6: LineSegment StartX=1480.95 StartY=6.821e-13 StartZ=0 EndX=1480.95 EndY=1038.1 EndZ=0
    g7: LineSegment StartX=1480.95 StartY=1038.1 StartZ=0 EndX=999.985 EndY=1038.1 EndZ=0
    g8: LineSegment [constr] StartX=1019.04 StartY=1019.05 StartZ=0 EndX=999.985 EndY=1038.1 EndZ=0
    g9: LineSegment [constr] StartX=1461.9 StartY=1019.05 StartZ=0 EndX=1480.95 EndY=1038.1 EndZ=0
    g10: LineSegment [constr] StartX=1240.47 StartY=1038.1 StartZ=0 EndX=1240.47 EndY=6.821e-13 EndZ=0
    g11: LineSegment [constr] StartX=999.985 StartY=519.05 StartZ=0 EndX=1480.95 EndY=519.05 EndZ=0
    g12: LineSegment [constr] StartX=1009.51 StartY=1028.57 StartZ=0 EndX=1009.51 EndY=519.05 EndZ=0
    g13: Circle CenterX=1009.51 CenterY=1028.57 CenterZ=0 NormalX=0 NormalY=0 NormalZ=1 AngleXU=0 Radius=5
    g14: Circle CenterX=1009.51 CenterY=773.812 CenterZ=0 NormalX=0 NormalY=0 NormalZ=1 AngleXU=0 Radius=5
    g15: Circle CenterX=1009.51 CenterY=519.05 CenterZ=0 NormalX=0 NormalY=0 NormalZ=1 AngleXU=0 Radius=5
    g16: Circle CenterX=1009.51 CenterY=264.288 CenterZ=0 NormalX=0 NormalY=0 NormalZ=1 AngleXU=0 Radius=5
    g17: Circle CenterX=1009.51 CenterY=9.525 CenterZ=0 NormalX=0 NormalY=0 NormalZ=1 AngleXU=0 Radius=5
    g18: Circle CenterX=1471.42 CenterY=1028.58 CenterZ=0 NormalX=0 NormalY=0 NormalZ=1 AngleXU=0 Radius=5
    g19: Circle CenterX=1471.43 CenterY=773.812 CenterZ=0 NormalX=0 NormalY=0 NormalZ=1 AngleXU=0 Radius=5
    g20: Circle CenterX=1471.43 CenterY=519.05 CenterZ=0 NormalX=0 NormalY=0 NormalZ=1 AngleXU=0 Radius=5
    g21: Circle CenterX=1471.43 CenterY=264.288 CenterZ=0 NormalX=0 NormalY=0 NormalZ=1 AngleXU=0 Radius=5
    g22: Circle CenterX=1471.43 CenterY=9.525 CenterZ=0 NormalX=0 NormalY=0 NormalZ=1 AngleXU=0 Radius=5
    g23: LineSegment [constr] StartX=1471.42 StartY=1028.58 StartZ=0 EndX=1240.47 EndY=1028.58 EndZ=0
    g24: LineSegment [constr] StartX=1240.47 StartY=1028.57 StartZ=0 EndX=1009.51 EndY=1028.57 EndZ=0
    g25: Circle CenterX=1240.47 CenterY=1028.58 CenterZ=0 NormalX=0 NormalY=0 NormalZ=1 AngleXU=0 Radius=5
    g26: Circle CenterX=1355.95 CenterY=1028.58 CenterZ=0 NormalX=0 NormalY=0 NormalZ=1 AngleXU=0 Radius=5
    g27: Circle CenterX=1124.99 CenterY=1028.57 CenterZ=0 NormalX=0 NormalY=0 NormalZ=1 AngleXU=0 Radius=5
    g28: Circle CenterX=1355.95 CenterY=9.525 CenterZ=0 NormalX=0 NormalY=0 NormalZ=1 AngleXU=0 Radius=5
    g29: Circle CenterX=1240.47 CenterY=9.525 CenterZ=0 NormalX=0 NormalY=0 NormalZ=1 AngleXU=0 Radius=5
    g30: Circle CenterX=1124.99 CenterY=9.525 CenterZ=0 NormalX=0 NormalY=0 NormalZ=1 AngleXU=0 Radius=5
  constraints (57):
    c: Coincident(g0,g-5)
    c: PointOnObject(g0,g-6)
    c: Vertical(g0)
    c: Coincident(g1,g0)
    c: Coincident(g1,g-7)
    c: Symmetric(g1,g1,g2)
    c: PointOnObject(g2,g-6)
    c: Vertical(g2)
    c: Coincident(g3,g2)
    c: PointOnObject(g3,g-4)
    c: Vertical(g3)
    c: Coincident(g4,g5)
    c: Coincident(g5,g6)
    c: Coincident(g6,g7)
    c: Coincident(g7,g4)
    c: Vertical(g4)
    c: Vertical(g6)
    c: Horizontal(g5)
    c: Horizontal(g7)
    c: Coincident(g4,g-4)
    c: Coincident(g5,g2)
    c: Coincident(g8,g-8)
    c: Coincident(g8,g4)
    c: Coincident(g9,g-9)
    c: Coincident(g9,g3)
    c: Symmetric(g7,g7,g10)
    c: Symmetric(g5,g5,g10)
    c: Symmetric(g4,g4,g11)
    c: Symmetric(g6,g6,g11)
    c: Symmetric(g8,g8,g12)
    c: PointOnObject(g12,g11)
    c: Vertical(g12)
    c: Coincident(g13,g12)
    c: Symmetric(g12,g12,g14)
    c: Coincident(g15,g12)
    c: Diameter(g13) = 10
    c: Diameter(g14) = 10
    c: Diameter(g15) = 10
    c: Diameter(g17) = 10
    c: Diameter(g16) = 10
    c: Diameter(g18) = 10
    c: Diameter(g19) = 10
    c: Diameter(g20) = 10
    c: Diameter(g22) = 10
    c: Diameter(g21) = 10
    c: Coincident(g23,g18)
    c: PointOnObject(g23,g10)
    c: Horizontal(g23)
    c: Coincident(g25,g23)
    c: Symmetric(g23,g23,g26)
    c: Symmetric(g24,g24,g27)
    c: Diameter(g27) = 10
    c: Diameter(g25) = 10
    c: Diameter(g26) = 10
    c: Diameter(g30) = 10
    c: Diameter(g29) = 10
    c: Diameter(g28) = 10
FEATURE [PartDesign::Pad] Pad056
  Direction = (0,-1,2e-16)
  Length = 5
  Length2 = 10
  Profile = -> Sketch122
  ReferenceAxis = -> Sketch122 [N_Axis]
  Refine = true
  Suppressed = false
  Type = 0
FEATURE [PartDesign::Body] Body052  label="Cuerpo078"
  AllowCompound = false
  Group = -> [Binder059,Binder058,Sketch122,Pad056]
  Origin = -> Origin055
  Placement = pos=(0,1581.2,4.547e-13) rot=(0,0,1;0rad)
  Tip = -> Pad056
FEATURE [PartDesign::SubShapeBinder] Binder060  label="Binder061"
  BindCopyOnChange = 0
  BindMode = 2
  ClaimChildren = false
  Context = -> Part002 [Body053.Binder060.]
  Fuse = false
  MakeFace = true
  OffsetFill = false
  OffsetIntersection = false
  OffsetJoinType = 0
  OffsetOpenResult = false
  PartialLoad = false
  Refine = true
  Relative = true
  _Version = 2
FEATURE [PartDesign::SubShapeBinder] Binder061  label="Binder062"
  BindCopyOnChange = 0
  BindMode = 2
  ClaimChildren = false
  Context = -> Part002 [Body053.Binder061.]
  Fuse = false
  MakeFace = true
  OffsetFill = false
  OffsetIntersection = false
  OffsetJoinType = 0
  OffsetOpenResult = false
  PartialLoad = false
  Refine = true
  Relative = true
  _Version = 2
FEATURE [Sketcher::SketchObject] Sketch123
  ArcFitTolerance = 1e-06
  AttachmentSupport = -> [Binder061]
  ExternalGeometry = -> [Binder060,Binder061]
  FullyConstrained = false
  MakeInternals = false
  MapMode = 5
  Placement = pos=(0,-38.1,8.4e-15) rot=(1,0,0;1.5708rad)
  sketch-geometry (31):
    g0: LineSegment [constr] StartX=1500 StartY=38.1 StartZ=0 EndX=1500 EndY=7.461e-13 EndZ=0
    g1: LineSegment [constr] StartX=1500 StartY=38.1 StartZ=0 EndX=1461.9 EndY=38.1 EndZ=0
    g2: LineSegment [constr] StartX=1480.95 StartY=38.1 StartZ=0 EndX=1480.95 EndY=6.821e-13 EndZ=0
    g3: LineSegment [constr] StartX=1480.95 StartY=38.1 StartZ=0 EndX=1480.95 EndY=1038.1 EndZ=0
    g4: LineSegment StartX=999.985 StartY=1038.1 StartZ=0 EndX=999.985 EndY=6.821e-13 EndZ=0
    g5: LineSegment StartX=999.985 StartY=6.821e-13 StartZ=0 EndX=1480.95 EndY=6.821e-13 EndZ=0
    g6: LineSegment StartX=1480.95 StartY=6.821e-13 StartZ=0 EndX=1480.95 EndY=1038.1 EndZ=0
    g7: LineSegment StartX=1480.95 StartY=1038.1 StartZ=0 EndX=999.985 EndY=1038.1 EndZ=0
    g8: LineSegment [constr] StartX=1019.04 StartY=1019.05 StartZ=0 EndX=999.985 EndY=1038.1 EndZ=0
    g9: LineSegment [constr] StartX=1461.9 StartY=1019.05 StartZ=0 EndX=1480.95 EndY=1038.1 EndZ=0
    g10: LineSegment [constr] StartX=1240.47 StartY=1038.1 StartZ=0 EndX=1240.47 EndY=6.821e-13 EndZ=0
    g11: LineSegment [constr] StartX=999.985 StartY=519.05 StartZ=0 EndX=1480.95 EndY=519.05 EndZ=0
    g12: LineSegment [constr] StartX=1009.51 StartY=1028.57 StartZ=0 EndX=1009.51 EndY=519.05 EndZ=0
    g13: Circle CenterX=1009.51 CenterY=1028.57 CenterZ=0 NormalX=0 NormalY=0 NormalZ=1 AngleXU=0 Radius=5
    g14: Circle CenterX=1009.51 CenterY=773.812 CenterZ=0 NormalX=0 NormalY=0 NormalZ=1 AngleXU=0 Radius=5
    g15: Circle CenterX=1009.51 CenterY=519.05 CenterZ=0 NormalX=0 NormalY=0 NormalZ=1 AngleXU=0 Radius=5
    g16: Circle CenterX=1009.51 CenterY=264.288 CenterZ=0 NormalX=0 NormalY=0 NormalZ=1 AngleXU=0 Radius=5
    g17: Circle CenterX=1009.51 CenterY=9.525 CenterZ=0 NormalX=0 NormalY=0 NormalZ=1 AngleXU=0 Radius=5
    g18: Circle CenterX=1471.42 CenterY=1028.58 CenterZ=0 NormalX=0 NormalY=0 NormalZ=1 AngleXU=0 Radius=5
    g19: Circle CenterX=1471.43 CenterY=773.812 CenterZ=0 NormalX=0 NormalY=0 NormalZ=1 AngleXU=0 Radius=5
    g20: Circle CenterX=1471.43 CenterY=519.05 CenterZ=0 NormalX=0 NormalY=0 NormalZ=1 AngleXU=0 Radius=5
    g21: Circle CenterX=1471.43 CenterY=264.288 CenterZ=0 NormalX=0 NormalY=0 NormalZ=1 AngleXU=0 Radius=5
    g22: Circle CenterX=1471.43 CenterY=9.525 CenterZ=0 NormalX=0 NormalY=0 NormalZ=1 AngleXU=0 Radius=5
    g23: LineSegment [constr] StartX=1471.42 StartY=1028.58 StartZ=0 EndX=1240.47 EndY=1028.58 EndZ=0
    g24: LineSegment [constr] StartX=1240.47 StartY=1028.57 StartZ=0 EndX=1009.51 EndY=1028.57 EndZ=0
    g25: Circle CenterX=1240.47 CenterY=1028.58 CenterZ=0 NormalX=0 NormalY=0 NormalZ=1 AngleXU=0 Radius=5
    g26: Circle CenterX=1355.95 CenterY=1028.58 CenterZ=0 NormalX=0 NormalY=0 NormalZ=1 AngleXU=0 Radius=5
    g27: Circle CenterX=1124.99 CenterY=1028.57 CenterZ=0 NormalX=0 NormalY=0 NormalZ=1 AngleXU=0 Radius=5
    g28: Circle CenterX=1355.95 CenterY=9.525 CenterZ=0 NormalX=0 NormalY=0 NormalZ=1 AngleXU=0 Radius=5
    g29: Circle CenterX=1240.47 CenterY=9.525 CenterZ=0 NormalX=0 NormalY=0 NormalZ=1 AngleXU=0 Radius=5
    g30: Circle CenterX=1124.99 CenterY=9.525 CenterZ=0 NormalX=0 NormalY=0 NormalZ=1 AngleXU=0 Radius=5
  constraints (57):
    c: Coincident(g0,g-5)
    c: PointOnObject(g0,g-6)
    c: Vertical(g0)
    c: Coincident(g1,g0)
    c: Coincident(g1,g-7)
    c: Symmetric(g1,g1,g2)
    c: PointOnObject(g2,g-6)
    c: Vertical(g2)
    c: Coincident(g3,g2)
    c: PointOnObject(g3,g-4)
    c: Vertical(g3)
    c: Coincident(g4,g5)
    c: Coincident(g5,g6)
    c: Coincident(g6,g7)
    c: Coincident(g7,g4)
    c: Vertical(g4)
    c: Vertical(g6)
    c: Horizontal(g5)
    c: Horizontal(g7)
    c: Coincident(g4,g-4)
    c: Coincident(g5,g2)
    c: Coincident(g8,g-8)
    c: Coincident(g8,g4)
    c: Coincident(g9,g-9)
    c: Coincident(g9,g3)
    c: Symmetric(g7,g7,g10)
    c: Symmetric(g5,g5,g10)
    c: Symmetric(g4,g4,g11)
    c: Symmetric(g6,g6,g11)
    c: Symmetric(g8,g8,g12)
    c: PointOnObject(g12,g11)
    c: Vertical(g12)
    c: Coincident(g13,g12)
    c: Symmetric(g12,g12,g14)
    c: Coincident(g15,g12)
    c: Diameter(g13) = 10
    c: Diameter(g14) = 10
    c: Diameter(g15) = 10
    c: Diameter(g17) = 10
    c: Diameter(g16) = 10
    c: Diameter(g18) = 10
    c: Diameter(g19) = 10
    c: Diameter(g20) = 10
    c: Diameter(g22) = 10
    c: Diameter(g21) = 10
    c: Coincident(g23,g18)
    c: PointOnObject(g23,g10)
    c: Horizontal(g23)
    c: Coincident(g25,g23)
    c: Symmetric(g23,g23,g26)
    c: Symmetric(g24,g24,g27)
    c: Diameter(g27) = 10
    c: Diameter(g25) = 10
    c: Diameter(g26) = 10
    c: Diameter(g30) = 10
    c: Diameter(g29) = 10
    c: Diameter(g28) = 10
FEATURE [PartDesign::Pad] Pad057
  Direction = (0,-1,2e-16)
  Length = 5
  Length2 = 10
  Profile = -> Sketch123
  ReferenceAxis = -> Sketch123 [N_Axis]
  Refine = true
  Suppressed = false
  Type = 0
FEATURE [PartDesign::Body] Body053  label="Cuerpo079"
  AllowCompound = false
  Group = -> [Binder061,Binder060,Sketch123,Pad057]
  Origin = -> Origin056
  Placement = pos=(0,1581.2,1038.1) rot=(0,0,1;0rad)
  Tip = -> Pad057
FEATURE [PartDesign::SubShapeBinder] Binder062  label="Binder063"
  BindCopyOnChange = 0
  BindMode = 2
  ClaimChildren = false
  Context = -> Body054 [Binder062.]
  Fuse = false
  MakeFace = true
  OffsetFill = false
  OffsetIntersection = false
  OffsetJoinType = 0
  OffsetOpenResult = false
  PartialLoad = false
  Refine = true
  Relative = true
  _Version = 2
FEATURE [Sketcher::SketchObject] Sketch124
  ArcFitTolerance = 1e-06
  AttachmentSupport = -> [Binder062]
  ExternalGeometry = -> [Binder062]
  FullyConstrained = false
  MakeInternals = false
  MapMode = 5
  Placement = pos=(0,-38.1,0) rot=(1,0,0;1.5708rad)
  sketch-geometry (30):
    g0: LineSegment [constr] StartX=1500 StartY=638.1 StartZ=0 EndX=1480.95 EndY=638.1 EndZ=0
    g1: LineSegment [constr] StartX=1500 StartY=600 StartZ=0 EndX=1480.95 EndY=600 EndZ=0
    g2: LineSegment [constr] StartX=1480.95 StartY=638.1 StartZ=0 EndX=1480.95 EndY=600 EndZ=0
    g3: LineSegment [constr] StartX=1480.95 StartY=619.05 StartZ=0 EndX=1999.97 EndY=619.05 EndZ=0
    g4: LineSegment StartX=1480.95 StartY=619.05 StartZ=0 EndX=1480.95 EndY=7.958e-13 EndZ=0
    g5: LineSegment StartX=1480.95 StartY=7.958e-13 StartZ=0 EndX=1999.97 EndY=7.958e-13 EndZ=0
    g6: LineSegment StartX=1999.97 StartY=7.958e-13 StartZ=0 EndX=1999.97 EndY=619.05 EndZ=0
    g7: LineSegment StartX=1999.97 StartY=619.05 StartZ=0 EndX=1480.95 EndY=619.05 EndZ=0
    g8: LineSegment [constr] StartX=1480.95 StartY=619.05 StartZ=0 EndX=1500 EndY=600 EndZ=0
    g9: Circle CenterX=1490.47 CenterY=609.525 CenterZ=0 NormalX=0 NormalY=0 NormalZ=1 AngleXU=0 Radius=4.44505
    g10: LineSegment [constr] StartX=1480.95 StartY=309.525 StartZ=0 EndX=1999.97 EndY=309.525 EndZ=0
    g11: LineSegment [constr] StartX=1490.47 StartY=609.525 StartZ=0 EndX=1490.47 EndY=309.525 EndZ=0
    g12: Circle CenterX=1490.47 CenterY=459.525 CenterZ=0 NormalX=0 NormalY=0 NormalZ=1 AngleXU=0 Radius=5
    g13: Circle CenterX=1490.47 CenterY=309.525 CenterZ=0 NormalX=0 NormalY=0 NormalZ=1 AngleXU=0 Radius=5
    g14: Circle CenterX=1490.47 CenterY=159.525 CenterZ=0 NormalX=0 NormalY=0 NormalZ=1 AngleXU=0 Radius=5
    g15: Circle CenterX=1490.47 CenterY=9.525 CenterZ=0 NormalX=0 NormalY=0 NormalZ=1 AngleXU=0 Radius=4.44505
    g16: LineSegment [constr] StartX=1740.46 StartY=7.53e-13 StartZ=0 EndX=1740.46 EndY=619.05 EndZ=0
    g17: Circle CenterX=1990.45 CenterY=609.525 CenterZ=0 NormalX=0 NormalY=0 NormalZ=1 AngleXU=0 Radius=4.44505
    g18: Circle CenterX=1990.45 CenterY=459.525 CenterZ=0 NormalX=0 NormalY=0 NormalZ=1 AngleXU=0 Radius=5
    g19: Circle CenterX=1990.45 CenterY=309.525 CenterZ=0 NormalX=0 NormalY=0 NormalZ=1 AngleXU=0 Radius=5
    g20: Circle CenterX=1990.45 CenterY=159.525 CenterZ=0 NormalX=0 NormalY=0 NormalZ=1 AngleXU=0 Radius=5
    g21: Circle CenterX=1990.45 CenterY=9.525 CenterZ=0 NormalX=0 NormalY=0 NormalZ=1 AngleXU=0 Radius=4.44505
    g22: LineSegment [constr] StartX=1990.45 StartY=609.525 StartZ=0 EndX=1740.46 EndY=609.525 EndZ=0
    g23: LineSegment [constr] StartX=1740.46 StartY=609.525 StartZ=0 EndX=1490.47 EndY=609.525 EndZ=0
    g24: Circle CenterX=1865.45 CenterY=609.525 CenterZ=0 NormalX=0 NormalY=0 NormalZ=1 AngleXU=0 Radius=5
    g25: Circle CenterX=1740.46 CenterY=609.525 CenterZ=0 NormalX=0 NormalY=0 NormalZ=1 AngleXU=0 Radius=5
    g26: Circle CenterX=1615.47 CenterY=609.525 CenterZ=0 NormalX=0 NormalY=0 NormalZ=1 AngleXU=0 Radius=5
    g27: Circle CenterX=1865.45 CenterY=9.525 CenterZ=0 NormalX=0 NormalY=0 NormalZ=1 AngleXU=0 Radius=5
    g28: Circle CenterX=1740.46 CenterY=9.525 CenterZ=0 NormalX=0 NormalY=0 NormalZ=1 AngleXU=0 Radius=5
    g29: Circle CenterX=1615.47 CenterY=9.525 CenterZ=0 NormalX=0 NormalY=0 NormalZ=1 AngleXU=0 Radius=5
  constraints (53):
    c: Coincident(g0,g-3)
    c: PointOnObject(g0,g-7)
    c: Horizontal(g0)
    c: Coincident(g1,g-8)
    c: PointOnObject(g1,g-7)
    c: Horizontal(g1)
    c: Coincident(g2,g0)
    c: Coincident(g2,g1)
    c: Symmetric(g2,g2,g3)
    c: PointOnObject(g3,g-4)
    c: Horizontal(g3)
    c: Coincident(g4,g5)
    c: Coincident(g5,g6)
    c: Coincident(g6,g7)
    c: Coincident(g7,g4)
    c: Vertical(g4)
    c: Vertical(g6)
    c: Horizontal(g5)
    c: Horizontal(g7)
    c: Coincident(g4,g3)
    c: Coincident(g5,g-5)
    c: Coincident(g8,g3)
    c: Coincident(g8,g1)
    c: Symmetric(g8,g8,g9)
    c: Symmetric(g4,g4,g10)
    c: Symmetric(g6,g6,g10)
    c: Coincident(g11,g9)
    c: PointOnObject(g11,g10)
    c: Vertical(g11)
    c: Symmetric(g11,g11,g12)
    c: Coincident(g13,g11)
    c: Diameter(g12) = 10
    c: Diameter(g13) = 10
    c: Diameter(g14) = 10
    c: Symmetric(g5,g5,g16)
    c: Symmetric(g7,g7,g16)
    c: Diameter(g18) = 10
    c: Diameter(g19) = 10
    c: Diameter(g20) = 10
    c: Coincident(g22,g17)
    c: PointOnObject(g22,g16)
    c: Horizontal(g22)
    c: Coincident(g23,g22)
    c: Coincident(g23,g9)
    c: Horizontal(g23)
    c: Symmetric(g22,g22,g24)
    c: Coincident(g25,g22)
    c: Diameter(g26) = 10
    c: Diameter(g25) = 10
    c: Diameter(g24) = 10
    c: Diameter(g29) = 10
    c: Diameter(g28) = 10
    c: Diameter(g27) = 10
FEATURE [PartDesign::Pad] Pad058
  Direction = (0,-1,2e-16)
  Length = 5
  Length2 = 10
  Profile = -> Sketch124
  ReferenceAxis = -> Sketch124 [N_Axis]
  Refine = true
  Suppressed = false
  Type = 0
FEATURE [PartDesign::Body] Body054  label="Cuerpo080"
  AllowCompound = false
  Group = -> [Binder062,Sketch124,Pad058]
  Origin = -> Origin057
  Placement = pos=(0,1581.2,4.547e-13) rot=(0,0,1;0rad)
  Tip = -> Pad058
FEATURE [PartDesign::SubShapeBinder] Binder063  label="Binder064"
  BindCopyOnChange = 0
  BindMode = 2
  ClaimChildren = false
  Context = -> Body055 [Binder063.]
  Fuse = false
  MakeFace = true
  OffsetFill = false
  OffsetIntersection = false
  OffsetJoinType = 0
  OffsetOpenResult = false
  PartialLoad = false
  Refine = true
  Relative = true
  _Version = 2
FEATURE [Sketcher::SketchObject] Sketch125
  ArcFitTolerance = 1e-06
  AttachmentSupport = -> [Binder063]
  ExternalGeometry = -> [Binder063]
  FullyConstrained = false
  MakeInternals = false
  MapMode = 5
  Placement = pos=(0,-38.1,0) rot=(1,0,0;1.5708rad)
  sketch-geometry (30):
    g0: LineSegment [constr] StartX=1500 StartY=638.1 StartZ=0 EndX=1480.95 EndY=638.1 EndZ=0
    g1: LineSegment [constr] StartX=1500 StartY=600 StartZ=0 EndX=1480.95 EndY=600 EndZ=0
    g2: LineSegment [constr] StartX=1480.95 StartY=638.1 StartZ=0 EndX=1480.95 EndY=600 EndZ=0
    g3: LineSegment [constr] StartX=1480.95 StartY=619.05 StartZ=0 EndX=1999.97 EndY=619.05 EndZ=0
    g4: LineSegment StartX=1480.95 StartY=619.05 StartZ=0 EndX=1480.95 EndY=7.958e-13 EndZ=0
    g5: LineSegment StartX=1480.95 StartY=7.958e-13 StartZ=0 EndX=1999.97 EndY=7.958e-13 EndZ=0
    g6: LineSegment StartX=1999.97 StartY=7.958e-13 StartZ=0 EndX=1999.97 EndY=619.05 EndZ=0
    g7: LineSegment StartX=1999.97 StartY=619.05 StartZ=0 EndX=1480.95 EndY=619.05 EndZ=0
    g8: LineSegment [constr] StartX=1480.95 StartY=619.05 StartZ=0 EndX=1500 EndY=600 EndZ=0
    g9: Circle CenterX=1490.47 CenterY=609.525 CenterZ=0 NormalX=0 NormalY=0 NormalZ=1 AngleXU=0 Radius=4.44505
    g10: LineSegment [constr] StartX=1480.95 StartY=309.525 StartZ=0 EndX=1999.97 EndY=309.525 EndZ=0
    g11: LineSegment [constr] StartX=1490.47 StartY=609.525 StartZ=0 EndX=1490.47 EndY=309.525 EndZ=0
    g12: Circle CenterX=1490.47 CenterY=459.525 CenterZ=0 NormalX=0 NormalY=0 NormalZ=1 AngleXU=0 Radius=5
    g13: Circle CenterX=1490.47 CenterY=309.525 CenterZ=0 NormalX=0 NormalY=0 NormalZ=1 AngleXU=0 Radius=5
    g14: Circle CenterX=1490.47 CenterY=159.525 CenterZ=0 NormalX=0 NormalY=0 NormalZ=1 AngleXU=0 Radius=5
    g15: Circle CenterX=1490.47 CenterY=9.525 CenterZ=0 NormalX=0 NormalY=0 NormalZ=1 AngleXU=0 Radius=4.44505
    g16: LineSegment [constr] StartX=1740.46 StartY=7.53e-13 StartZ=0 EndX=1740.46 EndY=619.05 EndZ=0
    g17: Circle CenterX=1990.45 CenterY=609.525 CenterZ=0 NormalX=0 NormalY=0 NormalZ=1 AngleXU=0 Radius=4.44505
    g18: Circle CenterX=1990.45 CenterY=459.525 CenterZ=0 NormalX=0 NormalY=0 NormalZ=1 AngleXU=0 Radius=5
    g19: Circle CenterX=1990.45 CenterY=309.525 CenterZ=0 NormalX=0 NormalY=0 NormalZ=1 AngleXU=0 Radius=5
    g20: Circle CenterX=1990.45 CenterY=159.525 CenterZ=0 NormalX=0 NormalY=0 NormalZ=1 AngleXU=0 Radius=5
    g21: Circle CenterX=1990.45 CenterY=9.525 CenterZ=0 NormalX=0 NormalY=0 NormalZ=1 AngleXU=0 Radius=4.44505
    g22: LineSegment [constr] StartX=1990.45 StartY=609.525 StartZ=0 EndX=1740.46 EndY=609.525 EndZ=0
    g23: LineSegment [constr] StartX=1740.46 StartY=609.525 StartZ=0 EndX=1490.47 EndY=609.525 EndZ=0
    g24: Circle CenterX=1865.45 CenterY=609.525 CenterZ=0 NormalX=0 NormalY=0 NormalZ=1 AngleXU=0 Radius=5
    g25: Circle CenterX=1740.46 CenterY=609.525 CenterZ=0 NormalX=0 NormalY=0 NormalZ=1 AngleXU=0 Radius=5
    g26: Circle CenterX=1615.47 CenterY=609.525 CenterZ=0 NormalX=0 NormalY=0 NormalZ=1 AngleXU=0 Radius=5
    g27: Circle CenterX=1865.45 CenterY=9.525 CenterZ=0 NormalX=0 NormalY=0 NormalZ=1 AngleXU=0 Radius=5
    g28: Circle CenterX=1740.46 CenterY=9.525 CenterZ=0 NormalX=0 NormalY=0 NormalZ=1 AngleXU=0 Radius=5
    g29: Circle CenterX=1615.47 CenterY=9.525 CenterZ=0 NormalX=0 NormalY=0 NormalZ=1 AngleXU=0 Radius=5
  constraints (53):
    c: Coincident(g0,g-3)
    c: PointOnObject(g0,g-7)
    c: Horizontal(g0)
    c: Coincident(g1,g-8)
    c: PointOnObject(g1,g-7)
    c: Horizontal(g1)
    c: Coincident(g2,g0)
    c: Coincident(g2,g1)
    c: Symmetric(g2,g2,g3)
    c: PointOnObject(g3,g-4)
    c: Horizontal(g3)
    c: Coincident(g4,g5)
    c: Coincident(g5,g6)
    c: Coincident(g6,g7)
    c: Coincident(g7,g4)
    c: Vertical(g4)
    c: Vertical(g6)
    c: Horizontal(g5)
    c: Horizontal(g7)
    c: Coincident(g4,g3)
    c: Coincident(g5,g-5)
    c: Coincident(g8,g3)
    c: Coincident(g8,g1)
    c: Symmetric(g8,g8,g9)
    c: Symmetric(g4,g4,g10)
    c: Symmetric(g6,g6,g10)
    c: Coincident(g11,g9)
    c: PointOnObject(g11,g10)
    c: Vertical(g11)
    c: Symmetric(g11,g11,g12)
    c: Coincident(g13,g11)
    c: Diameter(g12) = 10
    c: Diameter(g13) = 10
    c: Diameter(g14) = 10
    c: Symmetric(g5,g5,g16)
    c: Symmetric(g7,g7,g16)
    c: Diameter(g18) = 10
    c: Diameter(g19) = 10
    c: Diameter(g20) = 10
    c: Coincident(g22,g17)
    c: PointOnObject(g22,g16)
    c: Horizontal(g22)
    c: Coincident(g23,g22)
    c: Coincident(g23,g9)
    c: Horizontal(g23)
    c: Symmetric(g22,g22,g24)
    c: Coincident(g25,g22)
    c: Diameter(g26) = 10
    c: Diameter(g25) = 10
    c: Diameter(g24) = 10
    c: Diameter(g29) = 10
    c: Diameter(g28) = 10
    c: Diameter(g27) = 10
FEATURE [PartDesign::Pad] Pad059
  Direction = (0,-1,2e-16)
  Length = 5
  Length2 = 10
  Profile = -> Sketch125
  ReferenceAxis = -> Sketch125 [N_Axis]
  Refine = true
  Suppressed = false
  Type = 0
FEATURE [PartDesign::Body] Body055  label="Cuerpo081"
  AllowCompound = false
  Group = -> [Binder063,Sketch125,Pad059]
  Origin = -> Origin058
  Tip = -> Pad059
FEATURE [PartDesign::SubShapeBinder] Binder081  label="Binder082"
  BindCopyOnChange = 0
  BindMode = 2
  ClaimChildren = false
  Context = -> Body073 [Binder081.]
  Fuse = false
  MakeFace = true
  OffsetFill = false
  OffsetIntersection = false
  OffsetJoinType = 0
  OffsetOpenResult = false
  PartialLoad = false
  Refine = true
  Relative = true
  _Version = 2
FEATURE [PartDesign::SubShapeBinder] Binder082  label="Binder083"
  BindCopyOnChange = 0
  BindMode = 2
  ClaimChildren = false
  Context = -> Body073 [Binder082.]
  Fuse = false
  MakeFace = true
  OffsetFill = false
  OffsetIntersection = false
  OffsetJoinType = 0
  OffsetOpenResult = false
  PartialLoad = false
  Refine = true
  Relative = true
  _Version = 2
FEATURE [Sketcher::SketchObject] Sketch151
  ArcFitTolerance = 1e-06
  AttachmentSupport = -> [Binder082]
  ExternalGeometry = -> [Binder081,Binder082]
  FullyConstrained = false
  MakeInternals = false
  MapMode = 5
  Placement = pos=(0,-38.1,8.4e-15) rot=(1,0,0;1.5708rad)
  sketch-geometry (31):
    g0: LineSegment [constr] StartX=1500 StartY=38.1 StartZ=0 EndX=1500 EndY=7.461e-13 EndZ=0
    g1: LineSegment [constr] StartX=1500 StartY=38.1 StartZ=0 EndX=1461.9 EndY=38.1 EndZ=0
    g2: LineSegment [constr] StartX=1480.95 StartY=38.1 StartZ=0 EndX=1480.95 EndY=6.821e-13 EndZ=0
    g3: LineSegment [constr] StartX=1480.95 StartY=38.1 StartZ=0 EndX=1480.95 EndY=1038.1 EndZ=0
    g4: LineSegment StartX=999.985 StartY=1038.1 StartZ=0 EndX=999.985 EndY=6.821e-13 EndZ=0
    g5: LineSegment StartX=999.985 StartY=6.821e-13 StartZ=0 EndX=1480.95 EndY=6.821e-13 EndZ=0
    g6: LineSegment StartX=1480.95 StartY=6.821e-13 StartZ=0 EndX=1480.95 EndY=1038.1 EndZ=0
    g7: LineSegment StartX=1480.95 StartY=1038.1 StartZ=0 EndX=999.985 EndY=1038.1 EndZ=0
    g8: LineSegment [constr] StartX=1019.04 StartY=1019.05 StartZ=0 EndX=999.985 EndY=1038.1 EndZ=0
    g9: LineSegment [constr] StartX=1461.9 StartY=1019.05 StartZ=0 EndX=1480.95 EndY=1038.1 EndZ=0
    g10: LineSegment [constr] StartX=1240.47 StartY=1038.1 StartZ=0 EndX=1240.47 EndY=6.821e-13 EndZ=0
    g11: LineSegment [constr] StartX=999.985 StartY=519.05 StartZ=0 EndX=1480.95 EndY=519.05 EndZ=0
    g12: LineSegment [constr] StartX=1009.51 StartY=1028.57 StartZ=0 EndX=1009.51 EndY=519.05 EndZ=0
    g13: Circle CenterX=1009.51 CenterY=1028.57 CenterZ=0 NormalX=0 NormalY=0 NormalZ=1 AngleXU=0 Radius=5
    g14: Circle CenterX=1009.51 CenterY=773.812 CenterZ=0 NormalX=0 NormalY=0 NormalZ=1 AngleXU=0 Radius=5
    g15: Circle CenterX=1009.51 CenterY=519.05 CenterZ=0 NormalX=0 NormalY=0 NormalZ=1 AngleXU=0 Radius=5
    g16: Circle CenterX=1009.51 CenterY=264.288 CenterZ=0 NormalX=0 NormalY=0 NormalZ=1 AngleXU=0 Radius=5
    g17: Circle CenterX=1009.51 CenterY=9.525 CenterZ=0 NormalX=0 NormalY=0 NormalZ=1 AngleXU=0 Radius=5
    g18: Circle CenterX=1471.42 CenterY=1028.58 CenterZ=0 NormalX=0 NormalY=0 NormalZ=1 AngleXU=0 Radius=5
    g19: Circle CenterX=1471.43 CenterY=773.812 CenterZ=0 NormalX=0 NormalY=0 NormalZ=1 AngleXU=0 Radius=5
    g20: Circle CenterX=1471.43 CenterY=519.05 CenterZ=0 NormalX=0 NormalY=0 NormalZ=1 AngleXU=0 Radius=5
    g21: Circle CenterX=1471.43 CenterY=264.288 CenterZ=0 NormalX=0 NormalY=0 NormalZ=1 AngleXU=0 Radius=5
    g22: Circle CenterX=1471.43 CenterY=9.525 CenterZ=0 NormalX=0 NormalY=0 NormalZ=1 AngleXU=0 Radius=5
    g23: LineSegment [constr] StartX=1471.42 StartY=1028.58 StartZ=0 EndX=1240.47 EndY=1028.58 EndZ=0
    g24: LineSegment [constr] StartX=1240.47 StartY=1028.57 StartZ=0 EndX=1009.51 EndY=1028.57 EndZ=0
    g25: Circle CenterX=1240.47 CenterY=1028.58 CenterZ=0 NormalX=0 NormalY=0 NormalZ=1 AngleXU=0 Radius=5
    g26: Circle CenterX=1355.95 CenterY=1028.58 CenterZ=0 NormalX=0 NormalY=0 NormalZ=1 AngleXU=0 Radius=5
    g27: Circle CenterX=1124.99 CenterY=1028.57 CenterZ=0 NormalX=0 NormalY=0 NormalZ=1 AngleXU=0 Radius=5
    g28: Circle CenterX=1355.95 CenterY=9.525 CenterZ=0 NormalX=0 NormalY=0 NormalZ=1 AngleXU=0 Radius=5
    g29: Circle CenterX=1240.47 CenterY=9.525 CenterZ=0 NormalX=0 NormalY=0 NormalZ=1 AngleXU=0 Radius=5
    g30: Circle CenterX=1124.99 CenterY=9.525 CenterZ=0 NormalX=0 NormalY=0 NormalZ=1 AngleXU=0 Radius=5
  constraints (57):
    c: Coincident(g0,g-5)
    c: PointOnObject(g0,g-6)
    c: Vertical(g0)
    c: Coincident(g1,g0)
    c: Coincident(g1,g-7)
    c: Symmetric(g1,g1,g2)
    c: PointOnObject(g2,g-6)
    c: Vertical(g2)
    c: Coincident(g3,g2)
    c: PointOnObject(g3,g-4)
    c: Vertical(g3)
    c: Coincident(g4,g5)
    c: Coincident(g5,g6)
    c: Coincident(g6,g7)
    c: Coincident(g7,g4)
    c: Vertical(g4)
    c: Vertical(g6)
    c: Horizontal(g5)
    c: Horizontal(g7)
    c: Coincident(g4,g-4)
    c: Coincident(g5,g2)
    c: Coincident(g8,g-8)
    c: Coincident(g8,g4)
    c: Coincident(g9,g-9)
    c: Coincident(g9,g3)
    c: Symmetric(g7,g7,g10)
    c: Symmetric(g5,g5,g10)
    c: Symmetric(g4,g4,g11)
    c: Symmetric(g6,g6,g11)
    c: Symmetric(g8,g8,g12)
    c: PointOnObject(g12,g11)
    c: Vertical(g12)
    c: Coincident(g13,g12)
    c: Symmetric(g12,g12,g14)
    c: Coincident(g15,g12)
    c: Diameter(g13) = 10
    c: Diameter(g14) = 10
    c: Diameter(g15) = 10
    c: Diameter(g17) = 10
    c: Diameter(g16) = 10
    c: Diameter(g18) = 10
    c: Diameter(g19) = 10
    c: Diameter(g20) = 10
    c: Diameter(g22) = 10
    c: Diameter(g21) = 10
    c: Coincident(g23,g18)
    c: PointOnObject(g23,g10)
    c: Horizontal(g23)
    c: Coincident(g25,g23)
    c: Symmetric(g23,g23,g26)
    c: Symmetric(g24,g24,g27)
    c: Diameter(g27) = 10
    c: Diameter(g25) = 10
    c: Diameter(g26) = 10
    c: Diameter(g30) = 10
    c: Diameter(g29) = 10
    c: Diameter(g28) = 10
FEATURE [PartDesign::Pad] Pad077
  Direction = (0,-1,2e-16)
  Length = 5
  Length2 = 10
  Profile = -> Sketch151
  ReferenceAxis = -> Sketch151 [N_Axis]
  Refine = true
  Suppressed = false
  Type = 0
FEATURE [PartDesign::Body] Body073  label="Cuerpo118"
  AllowCompound = false
  Group = -> [Binder082,Binder081,Sketch151,Pad077]
  Origin = -> Origin077
  Tip = -> Pad077
FEATURE [PartDesign::SubShapeBinder] Binder083  label="Binder084"
  BindCopyOnChange = 0
  BindMode = 2
  ClaimChildren = false
  Context = -> Part002 [Body074.Binder083.]
  Fuse = false
  MakeFace = true
  OffsetFill = false
  OffsetIntersection = false
  OffsetJoinType = 0
  OffsetOpenResult = false
  PartialLoad = false
  Refine = true
  Relative = true
  _Version = 2
FEATURE [PartDesign::SubShapeBinder] Binder084  label="Binder085"
  BindCopyOnChange = 0
  BindMode = 2
  ClaimChildren = false
  Context = -> Part002 [Body074.Binder084.]
  Fuse = false
  MakeFace = true
  OffsetFill = false
  OffsetIntersection = false
  OffsetJoinType = 0
  OffsetOpenResult = false
  PartialLoad = false
  Refine = true
  Relative = true
  _Version = 2
FEATURE [Sketcher::SketchObject] Sketch152
  ArcFitTolerance = 1e-06
  AttachmentSupport = -> [Binder084]
  ExternalGeometry = -> [Binder083,Binder084]
  FullyConstrained = false
  MakeInternals = false
  MapMode = 5
  Placement = pos=(0,-38.1,8.4e-15) rot=(1,0,0;1.5708rad)
  sketch-geometry (31):
    g0: LineSegment [constr] StartX=1500 StartY=38.1 StartZ=0 EndX=1500 EndY=7.461e-13 EndZ=0
    g1: LineSegment [constr] StartX=1500 StartY=38.1 StartZ=0 EndX=1461.9 EndY=38.1 EndZ=0
    g2: LineSegment [constr] StartX=1480.95 StartY=38.1 StartZ=0 EndX=1480.95 EndY=6.821e-13 EndZ=0
    g3: LineSegment [constr] StartX=1480.95 StartY=38.1 StartZ=0 EndX=1480.95 EndY=1038.1 EndZ=0
    g4: LineSegment StartX=999.985 StartY=1038.1 StartZ=0 EndX=999.985 EndY=6.821e-13 EndZ=0
    g5: LineSegment StartX=999.985 StartY=6.821e-13 StartZ=0 EndX=1480.95 EndY=6.821e-13 EndZ=0
    g6: LineSegment StartX=1480.95 StartY=6.821e-13 StartZ=0 EndX=1480.95 EndY=1038.1 EndZ=0
    g7: LineSegment StartX=1480.95 StartY=1038.1 StartZ=0 EndX=999.985 EndY=1038.1 EndZ=0
    g8: LineSegment [constr] StartX=1019.04 StartY=1019.05 StartZ=0 EndX=999.985 EndY=1038.1 EndZ=0
    g9: LineSegment [constr] StartX=1461.9 StartY=1019.05 StartZ=0 EndX=1480.95 EndY=1038.1 EndZ=0
    g10: LineSegment [constr] StartX=1240.47 StartY=1038.1 StartZ=0 EndX=1240.47 EndY=6.821e-13 EndZ=0
    g11: LineSegment [constr] StartX=999.985 StartY=519.05 StartZ=0 EndX=1480.95 EndY=519.05 EndZ=0
    g12: LineSegment [constr] StartX=1009.51 StartY=1028.57 StartZ=0 EndX=1009.51 EndY=519.05 EndZ=0
    g13: Circle CenterX=1009.51 CenterY=1028.57 CenterZ=0 NormalX=0 NormalY=0 NormalZ=1 AngleXU=0 Radius=5
    g14: Circle CenterX=1009.51 CenterY=773.812 CenterZ=0 NormalX=0 NormalY=0 NormalZ=1 AngleXU=0 Radius=5
    g15: Circle CenterX=1009.51 CenterY=519.05 CenterZ=0 NormalX=0 NormalY=0 NormalZ=1 AngleXU=0 Radius=5
    g16: Circle CenterX=1009.51 CenterY=264.288 CenterZ=0 NormalX=0 NormalY=0 NormalZ=1 AngleXU=0 Radius=5
    g17: Circle CenterX=1009.51 CenterY=9.525 CenterZ=0 NormalX=0 NormalY=0 NormalZ=1 AngleXU=0 Radius=5
    g18: Circle CenterX=1471.42 CenterY=1028.58 CenterZ=0 NormalX=0 NormalY=0 NormalZ=1 AngleXU=0 Radius=5
    g19: Circle CenterX=1471.43 CenterY=773.812 CenterZ=0 NormalX=0 NormalY=0 NormalZ=1 AngleXU=0 Radius=5
    g20: Circle CenterX=1471.43 CenterY=519.05 CenterZ=0 NormalX=0 NormalY=0 NormalZ=1 AngleXU=0 Radius=5
    g21: Circle CenterX=1471.43 CenterY=264.288 CenterZ=0 NormalX=0 NormalY=0 NormalZ=1 AngleXU=0 Radius=5
    g22: Circle CenterX=1471.43 CenterY=9.525 CenterZ=0 NormalX=0 NormalY=0 NormalZ=1 AngleXU=0 Radius=5
    g23: LineSegment [constr] StartX=1471.42 StartY=1028.58 StartZ=0 EndX=1240.47 EndY=1028.58 EndZ=0
    g24: LineSegment [constr] StartX=1240.47 StartY=1028.57 StartZ=0 EndX=1009.51 EndY=1028.57 EndZ=0
    g25: Circle CenterX=1240.47 CenterY=1028.58 CenterZ=0 NormalX=0 NormalY=0 NormalZ=1 AngleXU=0 Radius=5
    g26: Circle CenterX=1355.95 CenterY=1028.58 CenterZ=0 NormalX=0 NormalY=0 NormalZ=1 AngleXU=0 Radius=5
    g27: Circle CenterX=1124.99 CenterY=1028.57 CenterZ=0 NormalX=0 NormalY=0 NormalZ=1 AngleXU=0 Radius=5
    g28: Circle CenterX=1355.95 CenterY=9.525 CenterZ=0 NormalX=0 NormalY=0 NormalZ=1 AngleXU=0 Radius=5
    g29: Circle CenterX=1240.47 CenterY=9.525 CenterZ=0 NormalX=0 NormalY=0 NormalZ=1 AngleXU=0 Radius=5
    g30: Circle CenterX=1124.99 CenterY=9.525 CenterZ=0 NormalX=0 NormalY=0 NormalZ=1 AngleXU=0 Radius=5
  constraints (57):
    c: Coincident(g0,g-5)
    c: PointOnObject(g0,g-6)
    c: Vertical(g0)
    c: Coincident(g1,g0)
    c: Coincident(g1,g-7)
    c: Symmetric(g1,g1,g2)
    c: PointOnObject(g2,g-6)
    c: Vertical(g2)
    c: Coincident(g3,g2)
    c: PointOnObject(g3,g-4)
    c: Vertical(g3)
    c: Coincident(g4,g5)
    c: Coincident(g5,g6)
    c: Coincident(g6,g7)
    c: Coincident(g7,g4)
    c: Vertical(g4)
    c: Vertical(g6)
    c: Horizontal(g5)
    c: Horizontal(g7)
    c: Coincident(g4,g-4)
    c: Coincident(g5,g2)
    c: Coincident(g8,g-8)
    c: Coincident(g8,g4)
    c: Coincident(g9,g-9)
    c: Coincident(g9,g3)
    c: Symmetric(g7,g7,g10)
    c: Symmetric(g5,g5,g10)
    c: Symmetric(g4,g4,g11)
    c: Symmetric(g6,g6,g11)
    c: Symmetric(g8,g8,g12)
    c: PointOnObject(g12,g11)
    c: Vertical(g12)
    c: Coincident(g13,g12)
    c: Symmetric(g12,g12,g14)
    c: Coincident(g15,g12)
    c: Diameter(g13) = 10
    c: Diameter(g14) = 10
    c: Diameter(g15) = 10
    c: Diameter(g17) = 10
    c: Diameter(g16) = 10
    c: Diameter(g18) = 10
    c: Diameter(g19) = 10
    c: Diameter(g20) = 10
    c: Diameter(g22) = 10
    c: Diameter(g21) = 10
    c: Coincident(g23,g18)
    c: PointOnObject(g23,g10)
    c: Horizontal(g23)
    c: Coincident(g25,g23)
    c: Symmetric(g23,g23,g26)
    c: Symmetric(g24,g24,g27)
    c: Diameter(g27) = 10
    c: Diameter(g25) = 10
    c: Diameter(g26) = 10
    c: Diameter(g30) = 10
    c: Diameter(g29) = 10
    c: Diameter(g28) = 10
FEATURE [PartDesign::Pad] Pad078
  Direction = (0,-1,2e-16)
  Length = 5
  Length2 = 10
  Profile = -> Sketch152
  ReferenceAxis = -> Sketch152 [N_Axis]
  Refine = true
  Suppressed = false
  Type = 0
FEATURE [PartDesign::Body] Body074  label="Cuerpo119"
  AllowCompound = false
  Group = -> [Binder084,Binder083,Sketch152,Pad078]
  Origin = -> Origin078
  Placement = pos=(0,2.345e-13,1038.1) rot=(0,0,1;0rad)
  Tip = -> Pad078
FEATURE [PartDesign::SubShapeBinder] Binder085  label="Binder086"
  BindCopyOnChange = 0
  BindMode = 2
  ClaimChildren = false
  Context = -> Part002 [Body075.Binder085.]
  Fuse = false
  MakeFace = true
  OffsetFill = false
  OffsetIntersection = false
  OffsetJoinType = 0
  OffsetOpenResult = false
  PartialLoad = false
  Refine = true
  Relative = true
  _Version = 2
FEATURE [Sketcher::SketchObject] Sketch153
  ArcFitTolerance = 1e-06
  AttachmentSupport = -> [Binder085]
  ExternalGeometry = -> [Binder085]
  FullyConstrained = false
  MakeInternals = false
  MapMode = 5
  Placement = pos=(0,-38.1,0) rot=(1,0,0;1.5708rad)
  sketch-geometry (35):
    g0: LineSegment StartX=1999.97 StartY=619.05 StartZ=0 EndX=1480.95 EndY=619.05 EndZ=0
    g1: LineSegment StartX=1480.95 StartY=619.05 StartZ=0 EndX=1480.95 EndY=2076.2 EndZ=0
    g2: LineSegment StartX=1480.95 StartY=2076.2 StartZ=0 EndX=1500 EndY=2076.2 EndZ=0
    g3: LineSegment StartX=1500 StartY=2076.2 StartZ=0 EndX=1999.97 EndY=1638.1 EndZ=0
    g4: LineSegment StartX=1999.97 StartY=1638.1 StartZ=0 EndX=1999.97 EndY=619.05 EndZ=0
    g5: LineSegment [constr] StartX=1961.9 StartY=1620.8 StartZ=0 EndX=1999.97 EndY=1638.1 EndZ=0
    g6: LineSegment [constr] StartX=1500 StartY=2025.54 StartZ=0 EndX=1500 EndY=2076.2 EndZ=0
    g7: LineSegment [constr] StartX=1500 StartY=638.1 StartZ=0 EndX=1480.95 EndY=619.05 EndZ=0
    g8: Circle CenterX=1490.47 CenterY=628.575 CenterZ=0 NormalX=0 NormalY=0 NormalZ=1 AngleXU=0 Radius=5
    g9: LineSegment [constr] StartX=1480.95 StartY=1347.62 StartZ=0 EndX=1999.97 EndY=1347.62 EndZ=0
    g10: LineSegment [constr] StartX=1740.46 StartY=619.05 StartZ=0 EndX=1740.46 EndY=1840.17 EndZ=0
    g11: Circle CenterX=1980.94 CenterY=628.575 CenterZ=0 NormalX=0 NormalY=0 NormalZ=1 AngleXU=0 Radius=5
    g12: Circle CenterX=1490.47 CenterY=2066.68 CenterZ=0 NormalX=0 NormalY=0 NormalZ=1 AngleXU=0 Radius=5
    g13: LineSegment [constr] StartX=1980.94 StartY=628.575 StartZ=0 EndX=1740.46 EndY=628.575 EndZ=0
    g14: LineSegment [constr] StartX=1740.46 StartY=628.575 StartZ=0 EndX=1490.47 EndY=628.575 EndZ=0
    g15: LineSegment [constr] StartX=1490.47 StartY=628.575 StartZ=0 EndX=1490.47 EndY=1347.62 EndZ=0
    g16: LineSegment [constr] StartX=1490.47 StartY=1347.62 StartZ=0 EndX=1490.47 EndY=2066.68 EndZ=0
    g17: Circle CenterX=1490.47 CenterY=1347.62 CenterZ=0 NormalX=0 NormalY=0 NormalZ=1 AngleXU=0 Radius=5
    g18: Circle CenterX=1490.47 CenterY=1707.15 CenterZ=0 NormalX=0 NormalY=0 NormalZ=1 AngleXU=0 Radius=5
    g19: Circle CenterX=1490.47 CenterY=988.1 CenterZ=0 NormalX=0 NormalY=0 NormalZ=1 AngleXU=0 Radius=5
    g20: Circle CenterX=1740.46 CenterY=628.575 CenterZ=0 NormalX=0 NormalY=0 NormalZ=1 AngleXU=0 Radius=5
    g21: Circle CenterX=1860.7 CenterY=628.575 CenterZ=0 NormalX=0 NormalY=0 NormalZ=1 AngleXU=0 Radius=5
    g22: Circle CenterX=1615.47 CenterY=628.575 CenterZ=0 NormalX=0 NormalY=0 NormalZ=1 AngleXU=0 Radius=5
    g23: Circle CenterX=1980.94 CenterY=1629.45 CenterZ=0 NormalX=0 NormalY=0 NormalZ=1 AngleXU=0 Radius=5
    g24: Circle CenterX=1740.46 CenterY=1840.17 CenterZ=0 NormalX=0 NormalY=0 NormalZ=1 AngleXU=0 Radius=5
    g25: LineSegment [constr] StartX=1980.94 StartY=1629.45 StartZ=0 EndX=1740.46 EndY=1840.17 EndZ=0
    g26: LineSegment [constr] StartX=1740.46 StartY=1840.17 StartZ=0 EndX=1490.47 EndY=2066.68 EndZ=0
    g27: Circle CenterX=1615.47 CenterY=1953.42 CenterZ=0 NormalX=0 NormalY=0 NormalZ=1 AngleXU=0 Radius=5
    g28: Circle CenterX=1860.7 CenterY=1734.81 CenterZ=0 NormalX=0 NormalY=0 NormalZ=1 AngleXU=0 Radius=5
    g29: LineSegment [constr] StartX=1999.97 StartY=1128.57 StartZ=0 EndX=1480.95 EndY=1128.57 EndZ=0
    g30: LineSegment [constr] StartX=1980.94 StartY=628.575 StartZ=0 EndX=1980.94 EndY=1128.57 EndZ=0
    g31: LineSegment [constr] StartX=1980.94 StartY=1128.57 StartZ=0 EndX=1980.94 EndY=1629.45 EndZ=0
    g32: Circle CenterX=1980.94 CenterY=1379.01 CenterZ=0 NormalX=0 NormalY=0 NormalZ=1 AngleXU=0 Radius=5
    g33: Circle CenterX=1980.94 CenterY=878.575 CenterZ=0 NormalX=0 NormalY=0 NormalZ=1 AngleXU=0 Radius=5
    g34: Circle CenterX=1980.94 CenterY=1128.57 CenterZ=0 NormalX=0 NormalY=0 NormalZ=1 AngleXU=0 Radius=5
  constraints (75):
    c: Coincident(g0,g-3)
    c: Coincident(g0,g-3)
    c: Coincident(g1,g0)
    c: Coincident(g1,g-7)
    c: Coincident(g2,g1)
    c: Coincident(g2,g-8)
    c: Coincident(g3,g2)
    c: Coincident(g3,g-6)
    c: Coincident(g4,g3)
    c: Coincident(g4,g0)
    c: Coincident(g5,g-10)
    c: Coincident(g5,g3)
    c: Coincident(g6,g-9)
    c: Coincident(g6,g2)
    c: Coincident(g7,g-11)
    c: Coincident(g7,g0)
    c: Symmetric(g7,g7,g8)
    c: Symmetric(g1,g1,g9)
    c: PointOnObject(g9,g4)
    c: Horizontal(g9)
    c: Diameter(g8) = 10
    c: Symmetric(g0,g0,g10)
    c: Vertical(g10)
    c: Diameter(g11) = 10
    c: Diameter(g12) = 10
    c: Coincident(g13,g11)
    c: PointOnObject(g13,g10)
    c: Horizontal(g13)
    c: Coincident(g14,g13)
    c: Coincident(g14,g8)
    c: Horizontal(g14)
    c: Coincident(g15,g8)
    c: PointOnObject(g15,g9)
    c: Vertical(g15)
    c: Coincident(g16,g15)
    c: Coincident(g16,g12)
    c: Vertical(g16)
    c: Coincident(g17,g15)
    c: Symmetric(g16,g16,g18)
    c: Symmetric(g15,g15,g19)
    c: Diameter(g19) = 10
    c: Diameter(g17) = 10
    c: Diameter(g18) = 10
    c: Coincident(g20,g13)
    c: Symmetric(g13,g13,g21)
    c: Symmetric(g14,g14,g22)
    c: Diameter(g23) = 10
    c: Coincident(g24,g10)
    c: Coincident(g25,g23)
    c: Coincident(g25,g10)
    c: Coincident(g26,g10)
    c: Coincident(g26,g12)
    c: Symmetric(g26,g26,g27)
    c: Symmetric(g25,g25,g28)
    c: Diameter(g28) = 10
    c: Diameter(g24) = 10
    c: Diameter(g27) = 10
    c: Diameter(g21) = 10
    c: Diameter(g20) = 10
    c: Diameter(g22) = 10
    c: Symmetric(g4,g4,g29)
    c: PointOnObject(g29,g1)
    c: Horizontal(g29)
    c: Coincident(g30,g11)
    c: PointOnObject(g30,g29)
    c: Vertical(g30)
    c: Coincident(g31,g30)
    c: Coincident(g31,g23)
    c: Vertical(g31)
    c: Symmetric(g31,g31,g32)
    c: Symmetric(g30,g30,g33)
    c: Coincident(g34,g30)
    c: Diameter(g33) = 10
    c: Diameter(g34) = 10
    c: Diameter(g32) = 10
FEATURE [PartDesign::Pad] Pad079
  Direction = (0,-1,2e-16)
  Length = 5
  Length2 = 10
  Profile = -> Sketch153
  ReferenceAxis = -> Sketch153 [N_Axis]
  Refine = true
  Suppressed = false
  Type = 0
FEATURE [PartDesign::Body] Body075  label="Cuerpo120"
  AllowCompound = false
  Group = -> [Binder085,Sketch153,Pad079]
  Origin = -> Origin079
  Placement = pos=(0,1581.2,4.547e-13) rot=(0,0,1;0rad)
  Tip = -> Pad079
FEATURE [PartDesign::SubShapeBinder] Binder086  label="Binder087"
  BindCopyOnChange = 0
  BindMode = 2
  ClaimChildren = false
  Context = -> Part002 [Body076.Binder086.]
  Fuse = false
  MakeFace = true
  OffsetFill = false
  OffsetIntersection = false
  OffsetJoinType = 0
  OffsetOpenResult = false
  PartialLoad = false
  Refine = true
  Relative = true
  _Version = 2
FEATURE [Sketcher::SketchObject] Sketch154
  ArcFitTolerance = 1e-06
  AttachmentSupport = -> [Binder086]
  ExternalGeometry = -> [Binder086]
  FullyConstrained = false
  MakeInternals = false
  MapMode = 5
  Placement = pos=(1999.97,0,0) rot=(0.57735,0.57735,0.57735;2.0944rad)
  sketch-geometry (28):
    g0: LineSegment [constr] StartX=749.964 StartY=1619.21 StartZ=0 EndX=730.754 EndY=1619.21 EndZ=0
    g1: LineSegment [constr] StartX=730.754 StartY=1619.21 StartZ=0 EndX=730.754 EndY=1599.2 EndZ=0
    g2: LineSegment [constr] StartX=730.754 StartY=1599.2 StartZ=0 EndX=749.964 EndY=1599.2 EndZ=0
    g3: LineSegment [constr] StartX=749.964 StartY=1599.2 StartZ=0 EndX=749.964 EndY=1619.21 EndZ=0
    g4: LineSegment [constr] StartX=748.701 StartY=1618.81 StartZ=0 EndX=730.754 EndY=1599.2 EndZ=0
    g5: Circle CenterX=739.728 CenterY=1609.01 CenterZ=0 NormalX=0 NormalY=0 NormalZ=1 AngleXU=0 Radius=5
    g6: LineSegment StartX=-38.1 StartY=1619.21 StartZ=0 EndX=750 EndY=1619.21 EndZ=0
    g7: LineSegment [constr] StartX=739.728 StartY=1609.01 StartZ=0 EndX=357.147 EndY=1609.01 EndZ=0
    g8: Circle CenterX=548.438 CenterY=1609.01 CenterZ=0 NormalX=0 NormalY=0 NormalZ=1 AngleXU=0 Radius=5
    g9: Circle CenterX=357.147 CenterY=1609.01 CenterZ=0 NormalX=0 NormalY=0 NormalZ=1 AngleXU=0 Radius=5
    g10: Circle CenterX=164.325 CenterY=1609.61 CenterZ=0 NormalX=0 NormalY=0 NormalZ=1 AngleXU=0 Radius=5
    g11: Circle CenterX=-27.6984 CenterY=1609.61 CenterZ=0 NormalX=0 NormalY=0 NormalZ=1 AngleXU=0 Radius=5
    g12: LineSegment [constr] StartX=1500 StartY=619.05 StartZ=0 EndX=0 EndY=619.05 EndZ=0
    g13: LineSegment StartX=750 StartY=1619.21 StartZ=0 EndX=750 EndY=619.05 EndZ=0
    g14: LineSegment StartX=750 StartY=619.05 StartZ=0 EndX=-38.1 EndY=619.05 EndZ=0
    g15: LineSegment StartX=-38.1 StartY=619.05 StartZ=0 EndX=-38.1 EndY=1619.21 EndZ=0
    g16: LineSegment [constr] StartX=355.95 StartY=1619.21 StartZ=0 EndX=355.95 EndY=619.05 EndZ=0
    g17: LineSegment [constr] StartX=750 StartY=1119.13 StartZ=0 EndX=-38.1 EndY=1119.13 EndZ=0
    g18: Circle CenterX=739.728 CenterY=628.656 CenterZ=0 NormalX=0 NormalY=0 NormalZ=1 AngleXU=0 Radius=5
    g19: Circle CenterX=548.372 CenterY=628.656 CenterZ=0 NormalX=0 NormalY=0 NormalZ=1 AngleXU=0 Radius=5
    g20: Circle CenterX=356.348 CenterY=628.656 CenterZ=0 NormalX=0 NormalY=0 NormalZ=1 AngleXU=0 Radius=5
    g21: Circle CenterX=164.325 CenterY=628.656 CenterZ=0 NormalX=0 NormalY=0 NormalZ=1 AngleXU=0 Radius=5
    g22: Circle CenterX=-27.6984 CenterY=628.656 CenterZ=0 NormalX=0 NormalY=0 NormalZ=1 AngleXU=0 Radius=5
    g23: LineSegment [constr] StartX=739.728 StartY=628.656 StartZ=0 EndX=739.728 EndY=1119.13 EndZ=0
    g24: LineSegment [constr] StartX=739.728 StartY=1119.13 StartZ=0 EndX=739.728 EndY=1609.01 EndZ=0
    g25: Circle CenterX=-27.8276 CenterY=873.894 CenterZ=0 NormalX=0 NormalY=0 NormalZ=1 AngleXU=0 Radius=5
    g26: Circle CenterX=-27.8276 CenterY=1119.13 CenterZ=0 NormalX=0 NormalY=0 NormalZ=1 AngleXU=0 Radius=5
    g27: Circle CenterX=-27.8276 CenterY=1364.07 CenterZ=0 NormalX=0 NormalY=0 NormalZ=1 AngleXU=0 Radius=5
  constraints (51):
    c: Coincident(g0,g1)
    c: Coincident(g1,g2)
    c: Coincident(g2,g3)
    c: Coincident(g3,g0)
    c: Horizontal(g0)
    c: Horizontal(g2)
    c: Vertical(g1)
    c: Vertical(g3)
    c: Distance(g1,g3) = 19.21
    c: Coincident(g4,g1)
    c: Symmetric(g4,g4,g5)
    c: PointOnObject(g6,g-3)
    c: PointOnObject(g6,g-4)
    c: Coincident(g7,g5)
    c: Horizontal(g7)
    c: Symmetric(g7,g7,g8)
    c: Coincident(g9,g7)
    c: Diameter(g9) = 10
    c: Diameter(g8) = 10
    c: Diameter(g5) = 10
    c: Diameter(g10) = 10
    c: Diameter(g11) = 10
    c: Symmetric(g-7,g-7,g12)
    c: PointOnObject(g12,g-2)
    c: Horizontal(g12)
    c: Coincident(g13,g6)
    c: Symmetric(g12,g12,g13)
    c: Vertical(g13)
    c: Coincident(g14,g13)
    c: PointOnObject(g14,g-8)
    c: Horizontal(g14)
    c: Coincident(g15,g14)
    c: Coincident(g15,g6)
    c: Vertical(g15)
    c: Symmetric(g6,g6,g16)
    c: Symmetric(g14,g14,g16)
    c: Symmetric(g13,g13,g17)
    c: Symmetric(g15,g15,g17)
    c: Diameter(g20) = 10
    c: Diameter(g19) = 10
    c: Diameter(g18) = 10
    c: Diameter(g21) = 10
    c: Diameter(g22) = 10
    c: Coincident(g23,g18)
    c: PointOnObject(g23,g17)
    c: Vertical(g23)
    c: Coincident(g24,g5)
    c: Vertical(g24)
    c: Diameter(g25) = 10
    c: Diameter(g26) = 10
    c: Diameter(g27) = 10
FEATURE [PartDesign::Pad] Pad080
  Direction = (1,0,0)
  Length = 5
  Length2 = 10
  Profile = -> Sketch154
  ReferenceAxis = -> Sketch154 [N_Axis]
  Refine = true
  Suppressed = false
  Type = 0
FEATURE [PartDesign::Body] Body076  label="Cuerpo121"
  AllowCompound = false
  Group = -> [Binder086,Sketch154,Pad080]
  Origin = -> Origin080
  Tip = -> Pad080
FEATURE [PartDesign::SubShapeBinder] Binder087  label="Binder088"
  BindCopyOnChange = 0
  BindMode = 2
  ClaimChildren = false
  Context = -> Part002 [Body077.Binder087.]
  Fuse = false
  MakeFace = true
  OffsetFill = false
  OffsetIntersection = false
  OffsetJoinType = 0
  OffsetOpenResult = false
  PartialLoad = false
  Refine = true
  Relative = true
  _Version = 2
FEATURE [Sketcher::SketchObject] Sketch155
  ArcFitTolerance = 1e-06
  AttachmentSupport = -> [Binder087]
  ExternalGeometry = -> [Binder087]
  FullyConstrained = false
  MakeInternals = false
  MapMode = 5
  Placement = pos=(1999.97,0,0) rot=(0.57735,0.57735,0.57735;2.0944rad)
  sketch-geometry (28):
    g0: LineSegment [constr] StartX=749.964 StartY=1619.21 StartZ=0 EndX=730.754 EndY=1619.21 EndZ=0
    g1: LineSegment [constr] StartX=730.754 StartY=1619.21 StartZ=0 EndX=730.754 EndY=1599.2 EndZ=0
    g2: LineSegment [constr] StartX=730.754 StartY=1599.2 StartZ=0 EndX=749.964 EndY=1599.2 EndZ=0
    g3: LineSegment [constr] StartX=749.964 StartY=1599.2 StartZ=0 EndX=749.964 EndY=1619.21 EndZ=0
    g4: LineSegment [constr] StartX=748.701 StartY=1618.81 StartZ=0 EndX=730.754 EndY=1599.2 EndZ=0
    g5: Circle CenterX=739.728 CenterY=1609.01 CenterZ=0 NormalX=0 NormalY=0 NormalZ=1 AngleXU=0 Radius=5
    g6: LineSegment StartX=-38.1 StartY=1619.21 StartZ=0 EndX=750 EndY=1619.21 EndZ=0
    g7: LineSegment [constr] StartX=739.728 StartY=1609.01 StartZ=0 EndX=357.147 EndY=1609.01 EndZ=0
    g8: Circle CenterX=548.438 CenterY=1609.01 CenterZ=0 NormalX=0 NormalY=0 NormalZ=1 AngleXU=0 Radius=5
    g9: Circle CenterX=357.147 CenterY=1609.01 CenterZ=0 NormalX=0 NormalY=0 NormalZ=1 AngleXU=0 Radius=5
    g10: Circle CenterX=164.325 CenterY=1609.61 CenterZ=0 NormalX=0 NormalY=0 NormalZ=1 AngleXU=0 Radius=5
    g11: Circle CenterX=-27.6984 CenterY=1609.61 CenterZ=0 NormalX=0 NormalY=0 NormalZ=1 AngleXU=0 Radius=5
    g12: LineSegment [constr] StartX=1500 StartY=619.05 StartZ=0 EndX=0 EndY=619.05 EndZ=0
    g13: LineSegment StartX=750 StartY=1619.21 StartZ=0 EndX=750 EndY=619.05 EndZ=0
    g14: LineSegment StartX=750 StartY=619.05 StartZ=0 EndX=-38.1 EndY=619.05 EndZ=0
    g15: LineSegment StartX=-38.1 StartY=619.05 StartZ=0 EndX=-38.1 EndY=1619.21 EndZ=0
    g16: LineSegment [constr] StartX=355.95 StartY=1619.21 StartZ=0 EndX=355.95 EndY=619.05 EndZ=0
    g17: LineSegment [constr] StartX=750 StartY=1119.13 StartZ=0 EndX=-38.1 EndY=1119.13 EndZ=0
    g18: Circle CenterX=739.728 CenterY=628.656 CenterZ=0 NormalX=0 NormalY=0 NormalZ=1 AngleXU=0 Radius=5
    g19: Circle CenterX=548.372 CenterY=628.656 CenterZ=0 NormalX=0 NormalY=0 NormalZ=1 AngleXU=0 Radius=5
    g20: Circle CenterX=356.348 CenterY=628.656 CenterZ=0 NormalX=0 NormalY=0 NormalZ=1 AngleXU=0 Radius=5
    g21: Circle CenterX=164.325 CenterY=628.656 CenterZ=0 NormalX=0 NormalY=0 NormalZ=1 AngleXU=0 Radius=5
    g22: Circle CenterX=-27.6984 CenterY=628.656 CenterZ=0 NormalX=0 NormalY=0 NormalZ=1 AngleXU=0 Radius=5
    g23: LineSegment [constr] StartX=739.728 StartY=628.656 StartZ=0 EndX=739.728 EndY=1119.13 EndZ=0
    g24: Circle CenterX=739.728 CenterY=873.894 CenterZ=0 NormalX=0 NormalY=0 NormalZ=1 AngleXU=0 Radius=5
    g25: Circle CenterX=739.728 CenterY=1119.13 CenterZ=0 NormalX=0 NormalY=0 NormalZ=1 AngleXU=0 Radius=5
    g26: LineSegment [constr] StartX=739.728 StartY=1119.13 StartZ=0 EndX=739.728 EndY=1609.01 EndZ=0
    g27: Circle CenterX=739.728 CenterY=1364.07 CenterZ=0 NormalX=0 NormalY=0 NormalZ=1 AngleXU=0 Radius=5
  constraints (55):
    c: Coincident(g0,g1)
    c: Coincident(g1,g2)
    c: Coincident(g2,g3)
    c: Coincident(g3,g0)
    c: Horizontal(g0)
    c: Horizontal(g2)
    c: Vertical(g1)
    c: Vertical(g3)
    c: Distance(g1,g3) = 19.21
    c: Coincident(g4,g1)
    c: Symmetric(g4,g4,g5)
    c: PointOnObject(g6,g-3)
    c: PointOnObject(g6,g-4)
    c: Coincident(g7,g5)
    c: Horizontal(g7)
    c: Symmetric(g7,g7,g8)
    c: Coincident(g9,g7)
    c: Diameter(g9) = 10
    c: Diameter(g8) = 10
    c: Diameter(g5) = 10
    c: Diameter(g10) = 10
    c: Diameter(g11) = 10
    c: Symmetric(g-7,g-7,g12)
    c: PointOnObject(g12,g-2)
    c: Horizontal(g12)
    c: Coincident(g13,g6)
    c: Symmetric(g12,g12,g13)
    c: Vertical(g13)
    c: Coincident(g14,g13)
    c: PointOnObject(g14,g-8)
    c: Horizontal(g14)
    c: Coincident(g15,g14)
    c: Coincident(g15,g6)
    c: Vertical(g15)
    c: Symmetric(g6,g6,g16)
    c: Symmetric(g14,g14,g16)
    c: Symmetric(g13,g13,g17)
    c: Symmetric(g15,g15,g17)
    c: Diameter(g20) = 10
    c: Diameter(g19) = 10
    c: Diameter(g18) = 10
    c: Diameter(g21) = 10
    c: Diameter(g22) = 10
    c: Coincident(g23,g18)
    c: PointOnObject(g23,g17)
    c: Vertical(g23)
    c: Symmetric(g23,g23,g24)
    c: Coincident(g25,g23)
    c: Coincident(g26,g23)
    c: Coincident(g26,g5)
    c: Vertical(g26)
    c: Symmetric(g26,g26,g27)
    c: Diameter(g24) = 10
    c: Diameter(g25) = 10
    c: Diameter(g27) = 10
FEATURE [PartDesign::Pad] Pad081
  Direction = (1,0,0)
  Length = 5
  Length2 = 10
  Profile = -> Sketch155
  ReferenceAxis = -> Sketch155 [N_Axis]
  Refine = true
  Suppressed = false
  Type = 0
FEATURE [PartDesign::Body] Body077  label="Cuerpo122"
  AllowCompound = false
  Group = -> [Binder087,Sketch155,Pad081]
  Origin = -> Origin081
  Placement = pos=(2.274e-13,788.1,-2.274e-13) rot=(0,0,1;0rad)
  Tip = -> Pad081
FEATURE [PartDesign::SubShapeBinder] Binder088  label="Binder089"
  BindCopyOnChange = 0
  BindMode = 2
  ClaimChildren = false
  Context = -> Body078 [Binder088.]
  Fuse = false
  MakeFace = true
  OffsetFill = false
  OffsetIntersection = false
  OffsetJoinType = 0
  OffsetOpenResult = false
  PartialLoad = false
  Refine = true
  Relative = true
  _Version = 2
FEATURE [Sketcher::SketchObject] Sketch156
  ArcFitTolerance = 1e-06
  AttachmentSupport = -> [Binder088]
  ExternalGeometry = -> [Binder088]
  FullyConstrained = false
  MakeInternals = false
  MapMode = 5
  Placement = pos=(2000,-1.54762,0) rot=(0.577648,0.577201,0.577201;2.09395rad)
  sketch-geometry (28):
    g0: LineSegment [constr] StartX=-36.5524 StartY=38.1 StartZ=0 EndX=-36.5524 EndY=-0.366907 EndZ=0
    g1: LineSegment [constr] StartX=0 StartY=0 StartZ=0 EndX=-36.5524 EndY=-0.366907 EndZ=0
    g2: LineSegment StartX=751.551 StartY=619.05 StartZ=0 EndX=-36.5524 EndY=619.05 EndZ=0
    g3: LineSegment StartX=-36.5524 StartY=619.05 StartZ=0 EndX=-36.5524 EndY=-0.366907 EndZ=0
    g4: LineSegment StartX=-36.5524 StartY=-0.366907 StartZ=0 EndX=751.551 EndY=-0.366907 EndZ=0
    g5: LineSegment StartX=751.551 StartY=-0.366907 StartZ=0 EndX=751.551 EndY=619.05 EndZ=0
    g6: LineSegment [constr] StartX=751.551 StartY=600 StartZ=0 EndX=751.551 EndY=619.05 EndZ=0
    g7: LineSegment [constr] StartX=751.551 StartY=619.05 StartZ=0 EndX=732.501 EndY=619.05 EndZ=0
    g8: LineSegment [constr] StartX=732.501 StartY=619.05 StartZ=0 EndX=732.501 EndY=600 EndZ=0
    g9: LineSegment [constr] StartX=732.501 StartY=600 StartZ=0 EndX=751.551 EndY=600 EndZ=0
    g10: LineSegment [constr] StartX=732.501 StartY=600 StartZ=0 EndX=751.551 EndY=619.05 EndZ=0
    g11: Circle CenterX=742.026 CenterY=609.525 CenterZ=0 NormalX=0 NormalY=0 NormalZ=1 AngleXU=0 Radius=5.27408
    g12: LineSegment [constr] StartX=357.499 StartY=619.05 StartZ=0 EndX=357.499 EndY=-0.366907 EndZ=0
    g13: LineSegment [constr] StartX=751.551 StartY=309.342 StartZ=0 EndX=-36.5524 EndY=309.342 EndZ=0
    g14: LineSegment [constr] StartX=742.026 StartY=609.525 StartZ=0 EndX=357.499 EndY=609.525 EndZ=0
    g15: Circle CenterX=-27.0274 CenterY=609.525 CenterZ=0 NormalX=0 NormalY=0 NormalZ=1 AngleXU=0 Radius=5.27408
    g16: Circle CenterX=549.763 CenterY=609.525 CenterZ=0 NormalX=0 NormalY=0 NormalZ=1 AngleXU=0 Radius=5
    g17: Circle CenterX=357.499 CenterY=609.525 CenterZ=0 NormalX=0 NormalY=0 NormalZ=1 AngleXU=0 Radius=5
    g18: Circle CenterX=165.236 CenterY=609.525 CenterZ=0 NormalX=0 NormalY=0 NormalZ=1 AngleXU=0 Radius=5
    g19: Circle CenterX=165.236 CenterY=9.15809 CenterZ=0 NormalX=0 NormalY=0 NormalZ=1 AngleXU=0 Radius=5
    g20: Circle CenterX=357.499 CenterY=9.15809 CenterZ=0 NormalX=0 NormalY=0 NormalZ=1 AngleXU=0 Radius=5
    g21: Circle CenterX=549.763 CenterY=9.15809 CenterZ=0 NormalX=0 NormalY=0 NormalZ=1 AngleXU=0 Radius=5
    g22: Circle CenterX=742.026 CenterY=9.15809 CenterZ=0 NormalX=0 NormalY=0 NormalZ=1 AngleXU=0 Radius=5.27408
    g23: LineSegment [constr] StartX=742.026 StartY=609.525 StartZ=0 EndX=742.026 EndY=309.342 EndZ=0
    g24: LineSegment [constr] StartX=742.026 StartY=309.342 StartZ=0 EndX=742.026 EndY=9.15809 EndZ=0
    g25: Circle CenterX=-27.0274 CenterY=159.25 CenterZ=0 NormalX=0 NormalY=0 NormalZ=1 AngleXU=0 Radius=5
    g26: Circle CenterX=-27.0274 CenterY=309.342 CenterZ=0 NormalX=0 NormalY=0 NormalZ=1 AngleXU=0 Radius=5
    g27: Circle CenterX=-27.0274 CenterY=459.433 CenterZ=0 NormalX=0 NormalY=0 NormalZ=1 AngleXU=0 Radius=5
  constraints (50):
    c: Coincident(g0,g-3)
    c: Vertical(g0)
    c: Coincident(g1,g-1)
    c: Coincident(g0,g1)
    c: Coincident(g2,g3)
    c: Coincident(g3,g4)
    c: Coincident(g4,g5)
    c: Coincident(g5,g2)
    c: Horizontal(g2)
    c: Horizontal(g4)
    c: Vertical(g3)
    c: Vertical(g5)
    c: Coincident(g2,g-6)
    c: Coincident(g3,g0)
    c: Coincident(g6,g7)
    c: Coincident(g7,g8)
    c: Coincident(g8,g9)
    c: Coincident(g9,g6)
    c: Vertical(g6)
    c: Vertical(g8)
    c: Horizontal(g7)
    c: Horizontal(g9)
    c: Equal(g8,g9)
    c: PointOnObject(g6,g-8)
    c: Coincident(g6,g2)
    c: Coincident(g10,g8)
    c: Coincident(g10,g2)
    c: Symmetric(g10,g10,g11)
    c: Symmetric(g2,g2,g12)
    c: Symmetric(g4,g4,g12)
    c: Symmetric(g5,g5,g13)
    c: Symmetric(g3,g3,g13)
    c: Coincident(g14,g11)
    c: PointOnObject(g14,g12)
    c: Horizontal(g14)
    c: Coincident(g17,g14)
    c: Diameter(g16) = 10
    c: Diameter(g17) = 10
    c: Diameter(g18) = 10
    c: Diameter(g21) = 10
    c: Diameter(g20) = 10
    c: Diameter(g19) = 10
    c: Coincident(g23,g11)
    c: PointOnObject(g23,g13)
    c: Vertical(g23)
    c: Coincident(g24,g22)
    c: Vertical(g24)
    c: Diameter(g27) = 10
    c: Diameter(g26) = 10
    c: Diameter(g25) = 10
FEATURE [PartDesign::Pad] Pad082
  Direction = (1,-0.00077381,0)
  Length = 5
  Length2 = 10
  Profile = -> Sketch156
  ReferenceAxis = -> Sketch156 [N_Axis]
  Refine = true
  Suppressed = false
  Type = 0
FEATURE [PartDesign::Body] Body078  label="Cuerpo123"
  AllowCompound = false
  Group = -> [Binder088,Sketch156,Pad082]
  Origin = -> Origin082
  Tip = -> Pad082
FEATURE [PartDesign::SubShapeBinder] Binder089  label="Binder090"
  BindCopyOnChange = 0
  BindMode = 2
  ClaimChildren = false
  Context = -> Body079 [Binder089.]
  Fuse = false
  MakeFace = true
  OffsetFill = false
  OffsetIntersection = false
  OffsetJoinType = 0
  OffsetOpenResult = false
  PartialLoad = false
  Refine = true
  Relative = true
  _Version = 2
FEATURE [Sketcher::SketchObject] Sketch157
  ArcFitTolerance = 1e-06
  AttachmentSupport = -> [Binder089]
  ExternalGeometry = -> [Binder089]
  FullyConstrained = false
  MakeInternals = false
  MapMode = 5
  Placement = pos=(2000,-1.54762,0) rot=(0.577648,0.577201,0.577201;2.09395rad)
  sketch-geometry (28):
    g0: LineSegment [constr] StartX=-36.5524 StartY=38.1 StartZ=0 EndX=-36.5524 EndY=-0.366907 EndZ=0
    g1: LineSegment [constr] StartX=0 StartY=0 StartZ=0 EndX=-36.5524 EndY=-0.366907 EndZ=0
    g2: LineSegment StartX=751.551 StartY=619.05 StartZ=0 EndX=-36.5524 EndY=619.05 EndZ=0
    g3: LineSegment StartX=-36.5524 StartY=619.05 StartZ=0 EndX=-36.5524 EndY=-0.366907 EndZ=0
    g4: LineSegment StartX=-36.5524 StartY=-0.366907 StartZ=0 EndX=751.551 EndY=-0.366907 EndZ=0
    g5: LineSegment StartX=751.551 StartY=-0.366907 StartZ=0 EndX=751.551 EndY=619.05 EndZ=0
    g6: LineSegment [constr] StartX=751.551 StartY=600 StartZ=0 EndX=751.551 EndY=619.05 EndZ=0
    g7: LineSegment [constr] StartX=751.551 StartY=619.05 StartZ=0 EndX=732.501 EndY=619.05 EndZ=0
    g8: LineSegment [constr] StartX=732.501 StartY=619.05 StartZ=0 EndX=732.501 EndY=600 EndZ=0
    g9: LineSegment [constr] StartX=732.501 StartY=600 StartZ=0 EndX=751.551 EndY=600 EndZ=0
    g10: LineSegment [constr] StartX=732.501 StartY=600 StartZ=0 EndX=751.551 EndY=619.05 EndZ=0
    g11: Circle CenterX=742.026 CenterY=609.525 CenterZ=0 NormalX=0 NormalY=0 NormalZ=1 AngleXU=0 Radius=5.27408
    g12: LineSegment [constr] StartX=357.499 StartY=619.05 StartZ=0 EndX=357.499 EndY=-0.366907 EndZ=0
    g13: LineSegment [constr] StartX=751.551 StartY=309.342 StartZ=0 EndX=-36.5524 EndY=309.342 EndZ=0
    g14: LineSegment [constr] StartX=742.026 StartY=609.525 StartZ=0 EndX=357.499 EndY=609.525 EndZ=0
    g15: Circle CenterX=549.763 CenterY=609.525 CenterZ=0 NormalX=0 NormalY=0 NormalZ=1 AngleXU=0 Radius=5
    g16: Circle CenterX=357.499 CenterY=609.525 CenterZ=0 NormalX=0 NormalY=0 NormalZ=1 AngleXU=0 Radius=5
    g17: Circle CenterX=165.236 CenterY=609.525 CenterZ=0 NormalX=0 NormalY=0 NormalZ=1 AngleXU=0 Radius=5
    g18: Circle CenterX=165.236 CenterY=9.15809 CenterZ=0 NormalX=0 NormalY=0 NormalZ=1 AngleXU=0 Radius=5
    g19: Circle CenterX=357.499 CenterY=9.15809 CenterZ=0 NormalX=0 NormalY=0 NormalZ=1 AngleXU=0 Radius=5
    g20: Circle CenterX=549.763 CenterY=9.15809 CenterZ=0 NormalX=0 NormalY=0 NormalZ=1 AngleXU=0 Radius=5
    g21: LineSegment [constr] StartX=742.026 StartY=609.525 StartZ=0 EndX=742.026 EndY=309.342 EndZ=0
    g22: LineSegment [constr] StartX=742.026 StartY=309.342 StartZ=0 EndX=742.026 EndY=9.15809 EndZ=0
    g23: Circle CenterX=742.026 CenterY=159.25 CenterZ=0 NormalX=0 NormalY=0 NormalZ=1 AngleXU=0 Radius=5
    g24: Circle CenterX=742.026 CenterY=309.342 CenterZ=0 NormalX=0 NormalY=0 NormalZ=1 AngleXU=0 Radius=5
    g25: Circle CenterX=742.026 CenterY=459.433 CenterZ=0 NormalX=0 NormalY=0 NormalZ=1 AngleXU=0 Radius=5
    g26: Circle CenterX=-27.0274 CenterY=9.15809 CenterZ=0 NormalX=0 NormalY=0 NormalZ=1 AngleXU=0 Radius=5.27408
    g27: Circle CenterX=-27.0274 CenterY=609.525 CenterZ=0 NormalX=0 NormalY=0 NormalZ=1 AngleXU=0 Radius=5.27408
  constraints (52):
    c: Coincident(g0,g-3)
    c: Vertical(g0)
    c: Coincident(g1,g-1)
    c: Coincident(g0,g1)
    c: Coincident(g3,g4)
    c: Coincident(g4,g5)
    c: Coincident(g5,g2)
    c: Horizontal(g2)
    c: Horizontal(g4)
    c: Vertical(g3)
    c: Vertical(g5)
    c: Coincident(g2,g-6)
    c: Coincident(g3,g0)
    c: Coincident(g6,g7)
    c: Coincident(g7,g8)
    c: Coincident(g8,g9)
    c: Coincident(g9,g6)
    c: Vertical(g6)
    c: Vertical(g8)
    c: Horizontal(g7)
    c: Horizontal(g9)
    c: Equal(g8,g9)
    c: PointOnObject(g6,g-8)
    c: Coincident(g6,g2)
    c: Coincident(g10,g8)
    c: Coincident(g10,g2)
    c: Symmetric(g10,g10,g11)
    c: Symmetric(g2,g2,g12)
    c: Symmetric(g4,g4,g12)
    c: Symmetric(g5,g5,g13)
    c: Symmetric(g3,g3,g13)
    c: Coincident(g14,g11)
    c: PointOnObject(g14,g12)
    c: Horizontal(g14)
    c: Coincident(g16,g14)
    c: Diameter(g15) = 10
    c: Diameter(g16) = 10
    c: Diameter(g17) = 10
    c: Diameter(g20) = 10
    c: Diameter(g19) = 10
    c: Diameter(g18) = 10
    c: Coincident(g21,g11)
    c: PointOnObject(g21,g13)
    c: Vertical(g21)
    c: Coincident(g22,g21)
    c: Vertical(g22)
    c: Symmetric(g22,g22,g23)
    c: Coincident(g24,g21)
    c: Symmetric(g21,g21,g25)
    c: Diameter(g25) = 10
    c: Diameter(g24) = 10
    c: Diameter(g23) = 10
FEATURE [PartDesign::Pad] Pad083
  Direction = (1,-0.00077381,0)
  Length = 5
  Length2 = 10
  Profile = -> Sketch157
  ReferenceAxis = -> Sketch157 [N_Axis]
  Refine = true
  Suppressed = false
  Type = 0
FEATURE [PartDesign::Body] Body079  label="Cuerpo124"
  AllowCompound = false
  Group = -> [Binder089,Sketch157,Pad083]
  Origin = -> Origin083
  Placement = pos=(-0.609841,788.1,-4.547e-13) rot=(0,0,1;0rad)
  Tip = -> Pad083
FEATURE [App::Part] Part002  label="Exterior"
  Group = -> [Body035,Body042,Body043,Group015,Group016,Body044,Body039,Body040,Body041,Body045,Body046,Body047,Body048,Body049,Body050,Body051,Body052,Body053,Body054,Body055,Body073,Body074,Body075,Body076,Body077,Body078,Body079]
  Origin = -> Origin036
FEATURE [PartDesign::SubShapeBinder] Binder090  label="Binder091"
  BindCopyOnChange = 0
  BindMode = 2
  ClaimChildren = false
  Context = -> Part003 [Body080.Binder090.]
  Fuse = false
  MakeFace = true
  OffsetFill = false
  OffsetIntersection = false
  OffsetJoinType = 0
  OffsetOpenResult = false
  PartialLoad = false
  Refine = true
  Relative = true
  _Version = 2
FEATURE [Sketcher::SketchObject] Sketch158
  ArcFitTolerance = 1e-06
  AttachmentSupport = -> [Binder090]
  ExternalGeometry = -> [Binder090]
  FullyConstrained = true
  MakeInternals = false
  MapMode = 5
  Placement = pos=(0,0,38.1) rot=(0,0,1;0rad)
  sketch-geometry (8):
    g0: LineSegment [constr] StartX=1461.9 StartY=1500 StartZ=0 EndX=1500 EndY=1500 EndZ=0
    g1: LineSegment [constr] StartX=1480.95 StartY=1500 StartZ=0 EndX=1480.95 EndY=-4.547e-13 EndZ=0
    g2: LineSegment [constr] StartX=980.935 StartY=1500 StartZ=0 EndX=1019.04 EndY=1500 EndZ=0
    g3: LineSegment [constr] StartX=999.985 StartY=1500 StartZ=0 EndX=999.985 EndY=-4.547e-13 EndZ=0
    g4: LineSegment StartX=999.985 StartY=1500 StartZ=0 EndX=999.985 EndY=1350 EndZ=0
    g5: LineSegment StartX=999.985 StartY=1350 StartZ=0 EndX=1480.95 EndY=1350 EndZ=0
    g6: LineSegment StartX=1480.95 StartY=1350 StartZ=0 EndX=1480.95 EndY=1500 EndZ=0
    g7: LineSegment StartX=1480.95 StartY=1500 StartZ=0 EndX=999.985 EndY=1500 EndZ=0
  constraints (21):
    c: Coincident(g0,g-8)
    c: Coincident(g0,g-5)
    c: Symmetric(g0,g0,g1)
    c: PointOnObject(g1,g-7)
    c: Vertical(g1)
    c: Coincident(g2,g-9)
    c: Coincident(g2,g-10)
    c: Symmetric(g2,g2,g3)
    c: PointOnObject(g3,g-7)
    c: Vertical(g3)
    c: Coincident(g4,g5)
    c: Coincident(g5,g6)
    c: Coincident(g6,g7)
    c: Coincident(g7,g4)
    c: Vertical(g4)
    c: Vertical(g6)
    c: Horizontal(g5)
    c: Horizontal(g7)
    c: Distance(g5,g7) = 150
    c: Coincident(g4,g3)
    c: PointOnObject(g5,g1)
FEATURE [PartDesign::Pad] Pad084
  Direction = (0,0,1)
  Length = 10
  Length2 = 10
  Profile = -> Sketch158
  ReferenceAxis = -> Sketch158 [N_Axis]
  Refine = true
  Suppressed = false
  Type = 0
FEATURE [PartDesign::Body] Body080  label="Cuerpo125"
  AllowCompound = false
  Group = -> [Binder090,Sketch158,Pad084]
  Origin = -> Origin085
  Placement = pos=(0,-5,0) rot=(0,0,1;0rad)
  Tip = -> Pad084
FEATURE [PartDesign::SubShapeBinder] Binder091  label="Binder092"
  BindCopyOnChange = 0
  BindMode = 2
  ClaimChildren = false
  Context = -> Part003 [Body081.Binder091.]
  Fuse = false
  MakeFace = true
  OffsetFill = false
  OffsetIntersection = false
  OffsetJoinType = 0
  OffsetOpenResult = false
  PartialLoad = false
  Refine = true
  Relative = true
  _Version = 2
FEATURE [Sketcher::SketchObject] Sketch159
  ArcFitTolerance = 1e-06
  AttachmentSupport = -> [Binder091]
  ExternalGeometry = -> [Binder091]
  FullyConstrained = true
  MakeInternals = false
  MapMode = 5
  Placement = pos=(0,0,38.1) rot=(0,0,1;0rad)
  sketch-geometry (8):
    g0: LineSegment [constr] StartX=1461.9 StartY=1500 StartZ=0 EndX=1500 EndY=1500 EndZ=0
    g1: LineSegment [constr] StartX=1480.95 StartY=1500 StartZ=0 EndX=1480.95 EndY=-4.547e-13 EndZ=0
    g2: LineSegment [constr] StartX=980.935 StartY=1500 StartZ=0 EndX=1019.04 EndY=1500 EndZ=0
    g3: LineSegment [constr] StartX=999.985 StartY=1500 StartZ=0 EndX=999.985 EndY=-4.547e-13 EndZ=0
    g4: LineSegment StartX=999.985 StartY=1500 StartZ=0 EndX=999.985 EndY=1350 EndZ=0
    g5: LineSegment StartX=999.985 StartY=1350 StartZ=0 EndX=1480.95 EndY=1350 EndZ=0
    g6: LineSegment StartX=1480.95 StartY=1350 StartZ=0 EndX=1480.95 EndY=1500 EndZ=0
    g7: LineSegment StartX=1480.95 StartY=1500 StartZ=0 EndX=999.985 EndY=1500 EndZ=0
  constraints (21):
    c: Coincident(g0,g-8)
    c: Coincident(g0,g-5)
    c: Symmetric(g0,g0,g1)
    c: PointOnObject(g1,g-7)
    c: Vertical(g1)
    c: Coincident(g2,g-9)
    c: Coincident(g2,g-10)
    c: Symmetric(g2,g2,g3)
    c: PointOnObject(g3,g-7)
    c: Vertical(g3)
    c: Coincident(g4,g5)
    c: Coincident(g5,g6)
    c: Coincident(g6,g7)
    c: Coincident(g7,g4)
    c: Vertical(g4)
    c: Vertical(g6)
    c: Horizontal(g5)
    c: Horizontal(g7)
    c: Distance(g5,g7) = 150
    c: Coincident(g4,g3)
    c: PointOnObject(g5,g1)
FEATURE [PartDesign::Pad] Pad085
  Direction = (0,0,1)
  Length = 10
  Length2 = 10
  Profile = -> Sketch159
  ReferenceAxis = -> Sketch159 [N_Axis]
  Refine = true
  Suppressed = false
  Type = 0
FEATURE [PartDesign::Body] Body081  label="Cuerpo126"
  AllowCompound = false
  Group = -> [Binder091,Sketch159,Pad085]
  Origin = -> Origin086
  Placement = pos=(0,-160,0) rot=(0,0,1;0rad)
  Tip = -> Pad085
FEATURE [PartDesign::SubShapeBinder] Binder092  label="Binder093"
  BindCopyOnChange = 0
  BindMode = 2
  ClaimChildren = false
  Context = -> Part003 [Body082.Binder092.]
  Fuse = false
  MakeFace = true
  OffsetFill = false
  OffsetIntersection = false
  OffsetJoinType = 0
  OffsetOpenResult = false
  PartialLoad = false
  Refine = true
  Relative = true
  _Version = 2
FEATURE [Sketcher::SketchObject] Sketch160
  ArcFitTolerance = 1e-06
  AttachmentSupport = -> [Binder092]
  ExternalGeometry = -> [Binder092]
  FullyConstrained = true
  MakeInternals = false
  MapMode = 5
  Placement = pos=(0,0,38.1) rot=(0,0,1;0rad)
  sketch-geometry (8):
    g0: LineSegment [constr] StartX=1461.9 StartY=1500 StartZ=0 EndX=1500 EndY=1500 EndZ=0
    g1: LineSegment [constr] StartX=1480.95 StartY=1500 StartZ=0 EndX=1480.95 EndY=-4.547e-13 EndZ=0
    g2: LineSegment [constr] StartX=980.935 StartY=1500 StartZ=0 EndX=1019.04 EndY=1500 EndZ=0
    g3: LineSegment [constr] StartX=999.985 StartY=1500 StartZ=0 EndX=999.985 EndY=-4.547e-13 EndZ=0
    g4: LineSegment StartX=999.985 StartY=1500 StartZ=0 EndX=999.985 EndY=1350 EndZ=0
    g5: LineSegment StartX=999.985 StartY=1350 StartZ=0 EndX=1480.95 EndY=1350 EndZ=0
    g6: LineSegment StartX=1480.95 StartY=1350 StartZ=0 EndX=1480.95 EndY=1500 EndZ=0
    g7: LineSegment StartX=1480.95 StartY=1500 StartZ=0 EndX=999.985 EndY=1500 EndZ=0
  constraints (21):
    c: Coincident(g0,g-8)
    c: Coincident(g0,g-5)
    c: Symmetric(g0,g0,g1)
    c: PointOnObject(g1,g-7)
    c: Vertical(g1)
    c: Coincident(g2,g-9)
    c: Coincident(g2,g-10)
    c: Symmetric(g2,g2,g3)
    c: PointOnObject(g3,g-7)
    c: Vertical(g3)
    c: Coincident(g4,g5)
    c: Coincident(g5,g6)
    c: Coincident(g6,g7)
    c: Coincident(g7,g4)
    c: Vertical(g4)
    c: Vertical(g6)
    c: Horizontal(g5)
    c: Horizontal(g7)
    c: Distance(g5,g7) = 150
    c: Coincident(g4,g3)
    c: PointOnObject(g5,g1)
FEATURE [PartDesign::Pad] Pad086
  Direction = (0,0,1)
  Length = 10
  Length2 = 10
  Profile = -> Sketch160
  ReferenceAxis = -> Sketch160 [N_Axis]
  Refine = true
  Suppressed = false
  Type = 0
FEATURE [PartDesign::Body] Body082  label="Cuerpo127"
  AllowCompound = false
  Group = -> [Binder092,Sketch160,Pad086]
  Origin = -> Origin087
  Placement = pos=(0,-315,0) rot=(0,0,1;0rad)
  Tip = -> Pad086
FEATURE [PartDesign::SubShapeBinder] Binder093  label="Binder094"
  BindCopyOnChange = 0
  BindMode = 2
  ClaimChildren = false
  Context = -> Part003 [Body083.Binder093.]
  Fuse = false
  MakeFace = true
  OffsetFill = false
  OffsetIntersection = false
  OffsetJoinType = 0
  OffsetOpenResult = false
  PartialLoad = false
  Refine = true
  Relative = true
  _Version = 2
FEATURE [Sketcher::SketchObject] Sketch161
  ArcFitTolerance = 1e-06
  AttachmentSupport = -> [Binder093]
  ExternalGeometry = -> [Binder093]
  FullyConstrained = true
  MakeInternals = false
  MapMode = 5
  Placement = pos=(0,0,38.1) rot=(0,0,1;0rad)
  sketch-geometry (8):
    g0: LineSegment [constr] StartX=1461.9 StartY=1500 StartZ=0 EndX=1500 EndY=1500 EndZ=0
    g1: LineSegment [constr] StartX=1480.95 StartY=1500 StartZ=0 EndX=1480.95 EndY=-4.547e-13 EndZ=0
    g2: LineSegment [constr] StartX=980.935 StartY=1500 StartZ=0 EndX=1019.04 EndY=1500 EndZ=0
    g3: LineSegment [constr] StartX=999.985 StartY=1500 StartZ=0 EndX=999.985 EndY=-4.547e-13 EndZ=0
    g4: LineSegment StartX=999.985 StartY=1500 StartZ=0 EndX=999.985 EndY=1350 EndZ=0
    g5: LineSegment StartX=999.985 StartY=1350 StartZ=0 EndX=1480.95 EndY=1350 EndZ=0
    g6: LineSegment StartX=1480.95 StartY=1350 StartZ=0 EndX=1480.95 EndY=1500 EndZ=0
    g7: LineSegment StartX=1480.95 StartY=1500 StartZ=0 EndX=999.985 EndY=1500 EndZ=0
  constraints (21):
    c: Coincident(g0,g-8)
    c: Coincident(g0,g-5)
    c: Symmetric(g0,g0,g1)
    c: PointOnObject(g1,g-7)
    c: Vertical(g1)
    c: Coincident(g2,g-9)
    c: Coincident(g2,g-10)
    c: Symmetric(g2,g2,g3)
    c: PointOnObject(g3,g-7)
    c: Vertical(g3)
    c: Coincident(g4,g5)
    c: Coincident(g5,g6)
    c: Coincident(g6,g7)
    c: Coincident(g7,g4)
    c: Vertical(g4)
    c: Vertical(g6)
    c: Horizontal(g5)
    c: Horizontal(g7)
    c: Distance(g5,g7) = 150
    c: Coincident(g4,g3)
    c: PointOnObject(g5,g1)
FEATURE [PartDesign::Pad] Pad087
  Direction = (0,0,1)
  Length = 10
  Length2 = 10
  Profile = -> Sketch161
  ReferenceAxis = -> Sketch161 [N_Axis]
  Refine = true
  Suppressed = false
  Type = 0
FEATURE [PartDesign::Body] Body083  label="Cuerpo128"
  AllowCompound = false
  Group = -> [Binder093,Sketch161,Pad087]
  Origin = -> Origin088
  Placement = pos=(0,-780,0) rot=(0,0,1;0rad)
  Tip = -> Pad087
FEATURE [PartDesign::SubShapeBinder] Binder094  label="Binder095"
  BindCopyOnChange = 0
  BindMode = 2
  ClaimChildren = false
  Context = -> Part003 [Body084.Binder094.]
  Fuse = false
  MakeFace = true
  OffsetFill = false
  OffsetIntersection = false
  OffsetJoinType = 0
  OffsetOpenResult = false
  PartialLoad = false
  Refine = true
  Relative = true
  _Version = 2
FEATURE [Sketcher::SketchObject] Sketch162
  ArcFitTolerance = 1e-06
  AttachmentSupport = -> [Binder094]
  ExternalGeometry = -> [Binder094]
  FullyConstrained = true
  MakeInternals = false
  MapMode = 5
  Placement = pos=(0,0,38.1) rot=(0,0,1;0rad)
  sketch-geometry (8):
    g0: LineSegment [constr] StartX=1461.9 StartY=1500 StartZ=0 EndX=1500 EndY=1500 EndZ=0
    g1: LineSegment [constr] StartX=1480.95 StartY=1500 StartZ=0 EndX=1480.95 EndY=-4.547e-13 EndZ=0
    g2: LineSegment [constr] StartX=980.935 StartY=1500 StartZ=0 EndX=1019.04 EndY=1500 EndZ=0
    g3: LineSegment [constr] StartX=999.985 StartY=1500 StartZ=0 EndX=999.985 EndY=-4.547e-13 EndZ=0
    g4: LineSegment StartX=999.985 StartY=1500 StartZ=0 EndX=999.985 EndY=1350 EndZ=0
    g5: LineSegment StartX=999.985 StartY=1350 StartZ=0 EndX=1480.95 EndY=1350 EndZ=0
    g6: LineSegment StartX=1480.95 StartY=1350 StartZ=0 EndX=1480.95 EndY=1500 EndZ=0
    g7: LineSegment StartX=1480.95 StartY=1500 StartZ=0 EndX=999.985 EndY=1500 EndZ=0
  constraints (21):
    c: Coincident(g0,g-8)
    c: Coincident(g0,g-5)
    c: Symmetric(g0,g0,g1)
    c: PointOnObject(g1,g-7)
    c: Vertical(g1)
    c: Coincident(g2,g-9)
    c: Coincident(g2,g-10)
    c: Symmetric(g2,g2,g3)
    c: PointOnObject(g3,g-7)
    c: Vertical(g3)
    c: Coincident(g4,g5)
    c: Coincident(g5,g6)
    c: Coincident(g6,g7)
    c: Coincident(g7,g4)
    c: Vertical(g4)
    c: Vertical(g6)
    c: Horizontal(g5)
    c: Horizontal(g7)
    c: Distance(g5,g7) = 150
    c: Coincident(g4,g3)
    c: PointOnObject(g5,g1)
FEATURE [PartDesign::Pad] Pad088
  Direction = (0,0,1)
  Length = 10
  Length2 = 10
  Profile = -> Sketch162
  ReferenceAxis = -> Sketch162 [N_Axis]
  Refine = true
  Suppressed = false
  Type = 0
FEATURE [PartDesign::Body] Body084  label="Cuerpo129"
  AllowCompound = false
  Group = -> [Binder094,Sketch162,Pad088]
  Origin = -> Origin089
  Placement = pos=(0,-470,0) rot=(0,0,1;0rad)
  Tip = -> Pad088
FEATURE [PartDesign::SubShapeBinder] Binder095  label="Binder096"
  BindCopyOnChange = 0
  BindMode = 2
  ClaimChildren = false
  Context = -> Part003 [Body085.Binder095.]
  Fuse = false
  MakeFace = true
  OffsetFill = false
  OffsetIntersection = false
  OffsetJoinType = 0
  OffsetOpenResult = false
  PartialLoad = false
  Refine = true
  Relative = true
  _Version = 2
FEATURE [Sketcher::SketchObject] Sketch163
  ArcFitTolerance = 1e-06
  AttachmentSupport = -> [Binder095]
  ExternalGeometry = -> [Binder095]
  FullyConstrained = true
  MakeInternals = false
  MapMode = 5
  Placement = pos=(0,0,38.1) rot=(0,0,1;0rad)
  sketch-geometry (8):
    g0: LineSegment [constr] StartX=1461.9 StartY=1500 StartZ=0 EndX=1500 EndY=1500 EndZ=0
    g1: LineSegment [constr] StartX=1480.95 StartY=1500 StartZ=0 EndX=1480.95 EndY=-4.547e-13 EndZ=0
    g2: LineSegment [constr] StartX=980.935 StartY=1500 StartZ=0 EndX=1019.04 EndY=1500 EndZ=0
    g3: LineSegment [constr] StartX=999.985 StartY=1500 StartZ=0 EndX=999.985 EndY=-4.547e-13 EndZ=0
    g4: LineSegment StartX=999.985 StartY=1500 StartZ=0 EndX=999.985 EndY=1350 EndZ=0
    g5: LineSegment StartX=999.985 StartY=1350 StartZ=0 EndX=1480.95 EndY=1350 EndZ=0
    g6: LineSegment StartX=1480.95 StartY=1350 StartZ=0 EndX=1480.95 EndY=1500 EndZ=0
    g7: LineSegment StartX=1480.95 StartY=1500 StartZ=0 EndX=999.985 EndY=1500 EndZ=0
  constraints (21):
    c: Coincident(g0,g-8)
    c: Coincident(g0,g-5)
    c: Symmetric(g0,g0,g1)
    c: PointOnObject(g1,g-7)
    c: Vertical(g1)
    c: Coincident(g2,g-9)
    c: Coincident(g2,g-10)
    c: Symmetric(g2,g2,g3)
    c: PointOnObject(g3,g-7)
    c: Vertical(g3)
    c: Coincident(g4,g5)
    c: Coincident(g5,g6)
    c: Coincident(g6,g7)
    c: Coincident(g7,g4)
    c: Vertical(g4)
    c: Vertical(g6)
    c: Horizontal(g5)
    c: Horizontal(g7)
    c: Distance(g5,g7) = 150
    c: Coincident(g4,g3)
    c: PointOnObject(g5,g1)
FEATURE [PartDesign::Pad] Pad089
  Direction = (0,0,1)
  Length = 10
  Length2 = 10
  Profile = -> Sketch163
  ReferenceAxis = -> Sketch163 [N_Axis]
  Refine = true
  Suppressed = false
  Type = 0
FEATURE [PartDesign::Body] Body085  label="Cuerpo130"
  AllowCompound = false
  Group = -> [Binder095,Sketch163,Pad089]
  Origin = -> Origin090
  Placement = pos=(0,-625,0) rot=(0,0,1;0rad)
  Tip = -> Pad089
FEATURE [PartDesign::SubShapeBinder] Binder096  label="Binder097"
  BindCopyOnChange = 0
  BindMode = 2
  ClaimChildren = false
  Context = -> Part003 [Body086.Binder096.]
  Fuse = false
  MakeFace = true
  OffsetFill = false
  OffsetIntersection = false
  OffsetJoinType = 0
  OffsetOpenResult = false
  PartialLoad = false
  Refine = true
  Relative = true
  _Version = 2
FEATURE [Sketcher::SketchObject] Sketch164
  ArcFitTolerance = 1e-06
  AttachmentSupport = -> [Binder096]
  ExternalGeometry = -> [Binder096]
  FullyConstrained = true
  MakeInternals = false
  MapMode = 5
  Placement = pos=(0,0,38.1) rot=(0,0,1;0rad)
  sketch-geometry (8):
    g0: LineSegment [constr] StartX=1461.9 StartY=1500 StartZ=0 EndX=1500 EndY=1500 EndZ=0
    g1: LineSegment [constr] StartX=1480.95 StartY=1500 StartZ=0 EndX=1480.95 EndY=-4.547e-13 EndZ=0
    g2: LineSegment [constr] StartX=980.935 StartY=1500 StartZ=0 EndX=1019.04 EndY=1500 EndZ=0
    g3: LineSegment [constr] StartX=999.985 StartY=1500 StartZ=0 EndX=999.985 EndY=-4.547e-13 EndZ=0
    g4: LineSegment StartX=999.985 StartY=1500 StartZ=0 EndX=999.985 EndY=1350 EndZ=0
    g5: LineSegment StartX=999.985 StartY=1350 StartZ=0 EndX=1480.95 EndY=1350 EndZ=0
    g6: LineSegment StartX=1480.95 StartY=1350 StartZ=0 EndX=1480.95 EndY=1500 EndZ=0
    g7: LineSegment StartX=1480.95 StartY=1500 StartZ=0 EndX=999.985 EndY=1500 EndZ=0
  constraints (21):
    c: Coincident(g0,g-8)
    c: Coincident(g0,g-5)
    c: Symmetric(g0,g0,g1)
    c: PointOnObject(g1,g-7)
    c: Vertical(g1)
    c: Coincident(g2,g-9)
    c: Coincident(g2,g-10)
    c: Symmetric(g2,g2,g3)
    c: PointOnObject(g3,g-7)
    c: Vertical(g3)
    c: Coincident(g4,g5)
    c: Coincident(g5,g6)
    c: Coincident(g6,g7)
    c: Coincident(g7,g4)
    c: Vertical(g4)
    c: Vertical(g6)
    c: Horizontal(g5)
    c: Horizontal(g7)
    c: Distance(g5,g7) = 150
    c: Coincident(g4,g3)
    c: PointOnObject(g5,g1)
FEATURE [PartDesign::Pad] Pad090
  Direction = (0,0,1)
  Length = 10
  Length2 = 10
  Profile = -> Sketch164
  ReferenceAxis = -> Sketch164 [N_Axis]
  Refine = true
  Suppressed = false
  Type = 0
FEATURE [PartDesign::Body] Body086  label="Cuerpo131"
  AllowCompound = false
  Group = -> [Binder096,Sketch164,Pad090]
  Origin = -> Origin091
  Placement = pos=(0,-1245,0) rot=(0,0,1;0rad)
  Tip = -> Pad090
FEATURE [PartDesign::SubShapeBinder] Binder097  label="Binder098"
  BindCopyOnChange = 0
  BindMode = 2
  ClaimChildren = false
  Context = -> Part003 [Body087.Binder097.]
  Fuse = false
  MakeFace = true
  OffsetFill = false
  OffsetIntersection = false
  OffsetJoinType = 0
  OffsetOpenResult = false
  PartialLoad = false
  Refine = true
  Relative = true
  _Version = 2
FEATURE [Sketcher::SketchObject] Sketch165
  ArcFitTolerance = 1e-06
  AttachmentSupport = -> [Binder097]
  ExternalGeometry = -> [Binder097]
  FullyConstrained = true
  MakeInternals = false
  MapMode = 5
  Placement = pos=(0,0,38.1) rot=(0,0,1;0rad)
  sketch-geometry (8):
    g0: LineSegment [constr] StartX=1461.9 StartY=1500 StartZ=0 EndX=1500 EndY=1500 EndZ=0
    g1: LineSegment [constr] StartX=1480.95 StartY=1500 StartZ=0 EndX=1480.95 EndY=-4.547e-13 EndZ=0
    g2: LineSegment [constr] StartX=980.935 StartY=1500 StartZ=0 EndX=1019.04 EndY=1500 EndZ=0
    g3: LineSegment [constr] StartX=999.985 StartY=1500 StartZ=0 EndX=999.985 EndY=-4.547e-13 EndZ=0
    g4: LineSegment StartX=999.985 StartY=1500 StartZ=0 EndX=999.985 EndY=1350 EndZ=0
    g5: LineSegment StartX=999.985 StartY=1350 StartZ=0 EndX=1480.95 EndY=1350 EndZ=0
    g6: LineSegment StartX=1480.95 StartY=1350 StartZ=0 EndX=1480.95 EndY=1500 EndZ=0
    g7: LineSegment StartX=1480.95 StartY=1500 StartZ=0 EndX=999.985 EndY=1500 EndZ=0
  constraints (21):
    c: Coincident(g0,g-8)
    c: Coincident(g0,g-5)
    c: Symmetric(g0,g0,g1)
    c: PointOnObject(g1,g-7)
    c: Vertical(g1)
    c: Coincident(g2,g-9)
    c: Coincident(g2,g-10)
    c: Symmetric(g2,g2,g3)
    c: PointOnObject(g3,g-7)
    c: Vertical(g3)
    c: Coincident(g4,g5)
    c: Coincident(g5,g6)
    c: Coincident(g6,g7)
    c: Coincident(g7,g4)
    c: Vertical(g4)
    c: Vertical(g6)
    c: Horizontal(g5)
    c: Horizontal(g7)
    c: Distance(g5,g7) = 150
    c: Coincident(g4,g3)
    c: PointOnObject(g5,g1)
FEATURE [PartDesign::Pad] Pad091
  Direction = (0,0,1)
  Length = 10
  Length2 = 10
  Profile = -> Sketch165
  ReferenceAxis = -> Sketch165 [N_Axis]
  Refine = true
  Suppressed = false
  Type = 0
FEATURE [PartDesign::Body] Body087  label="Cuerpo132"
  AllowCompound = false
  Group = -> [Binder097,Sketch165,Pad091]
  Origin = -> Origin092
  Placement = pos=(0,-935,0) rot=(0,0,1;0rad)
  Tip = -> Pad091
FEATURE [PartDesign::SubShapeBinder] Binder098  label="Binder099"
  BindCopyOnChange = 0
  BindMode = 2
  ClaimChildren = false
  Context = -> Part003 [Body088.Binder098.]
  Fuse = false
  MakeFace = true
  OffsetFill = false
  OffsetIntersection = false
  OffsetJoinType = 0
  OffsetOpenResult = false
  PartialLoad = false
  Refine = true
  Relative = true
  _Version = 2
FEATURE [Sketcher::SketchObject] Sketch166
  ArcFitTolerance = 1e-06
  AttachmentSupport = -> [Binder098]
  ExternalGeometry = -> [Binder098]
  FullyConstrained = true
  MakeInternals = false
  MapMode = 5
  Placement = pos=(0,0,38.1) rot=(0,0,1;0rad)
  sketch-geometry (8):
    g0: LineSegment [constr] StartX=1461.9 StartY=1500 StartZ=0 EndX=1500 EndY=1500 EndZ=0
    g1: LineSegment [constr] StartX=1480.95 StartY=1500 StartZ=0 EndX=1480.95 EndY=-4.547e-13 EndZ=0
    g2: LineSegment [constr] StartX=980.935 StartY=1500 StartZ=0 EndX=1019.04 EndY=1500 EndZ=0
    g3: LineSegment [constr] StartX=999.985 StartY=1500 StartZ=0 EndX=999.985 EndY=-4.547e-13 EndZ=0
    g4: LineSegment StartX=999.985 StartY=1500 StartZ=0 EndX=999.985 EndY=1350 EndZ=0
    g5: LineSegment StartX=999.985 StartY=1350 StartZ=0 EndX=1480.95 EndY=1350 EndZ=0
    g6: LineSegment StartX=1480.95 StartY=1350 StartZ=0 EndX=1480.95 EndY=1500 EndZ=0
    g7: LineSegment StartX=1480.95 StartY=1500 StartZ=0 EndX=999.985 EndY=1500 EndZ=0
  constraints (21):
    c: Coincident(g0,g-8)
    c: Coincident(g0,g-5)
    c: Symmetric(g0,g0,g1)
    c: PointOnObject(g1,g-7)
    c: Vertical(g1)
    c: Coincident(g2,g-9)
    c: Coincident(g2,g-10)
    c: Symmetric(g2,g2,g3)
    c: PointOnObject(g3,g-7)
    c: Vertical(g3)
    c: Coincident(g4,g5)
    c: Coincident(g5,g6)
    c: Coincident(g6,g7)
    c: Coincident(g7,g4)
    c: Vertical(g4)
    c: Vertical(g6)
    c: Horizontal(g5)
    c: Horizontal(g7)
    c: Distance(g5,g7) = 150
    c: Coincident(g4,g3)
    c: PointOnObject(g5,g1)
FEATURE [PartDesign::Pad] Pad092
  Direction = (0,0,1)
  Length = 10
  Length2 = 10
  Profile = -> Sketch166
  ReferenceAxis = -> Sketch166 [N_Axis]
  Refine = true
  Suppressed = false
  Type = 0
FEATURE [PartDesign::Body] Body088  label="Cuerpo133"
  AllowCompound = false
  Group = -> [Binder098,Sketch166,Pad092]
  Origin = -> Origin093
  Placement = pos=(0,-1090,0) rot=(0,0,1;0rad)
  Tip = -> Pad092
FEATURE [PartDesign::SubShapeBinder] Binder099  label="Binder100"
  BindCopyOnChange = 0
  BindMode = 2
  ClaimChildren = false
  Context = -> Part003 [Body089.Binder099.]
  Fuse = false
  MakeFace = true
  OffsetFill = false
  OffsetIntersection = false
  OffsetJoinType = 0
  OffsetOpenResult = false
  PartialLoad = false
  Refine = true
  Relative = true
  _Version = 2
FEATURE [Sketcher::SketchObject] Sketch167
  ArcFitTolerance = 1e-06
  AttachmentSupport = -> [Binder099]
  ExternalGeometry = -> [Binder099]
  FullyConstrained = true
  MakeInternals = false
  MapMode = 5
  Placement = pos=(0,0,38.1) rot=(0,0,1;0rad)
  sketch-geometry (12):
    g0: LineSegment [constr] StartX=1480.95 StartY=105 StartZ=0 EndX=1480.95 EndY=-4.405e-13 EndZ=0
    g1: LineSegment [constr] StartX=999.985 StartY=105 StartZ=0 EndX=999.985 EndY=0 EndZ=0
    g2: LineSegment [constr] StartX=999.985 StartY=0 StartZ=0 EndX=1480.95 EndY=-4.47e-13 EndZ=0
    g3: LineSegment [constr] StartX=1240.47 StartY=-2.235e-13 StartZ=0 EndX=1240.47 EndY=5 EndZ=0
    g4: LineSegment [constr] StartX=1240.47 StartY=105 StartZ=0 EndX=1240.47 EndY=100 EndZ=0
    g5: LineSegment [constr] StartX=1240.47 StartY=100 StartZ=0 EndX=1240.47 EndY=5 EndZ=0
    g6: LineSegment [constr] StartX=1240.47 StartY=100 StartZ=0 EndX=999.985 EndY=100 EndZ=0
    g7: LineSegment StartX=1480.95 StartY=5 StartZ=0 EndX=1480.95 EndY=100 EndZ=0
    g8: LineSegment StartX=1480.95 StartY=100 StartZ=0 EndX=999.985 EndY=100 EndZ=0
    g9: LineSegment StartX=999.985 StartY=100 StartZ=0 EndX=999.985 EndY=5 EndZ=0
    g10: LineSegment StartX=999.985 StartY=5 StartZ=0 EndX=1480.95 EndY=5 EndZ=0
    g11: GeomPoint [constr] X=1240.47 Y=52.5 Z=0
  constraints (29):
    c: Coincident(g0,g-4)
    c: Symmetric(g-6,g-6,g0)
    c: Coincident(g1,g-4)
    c: PointOnObject(g1,g-1)
    c: Vertical(g1)
    c: Coincident(g2,g1)
    c: Coincident(g2,g0)
    c: Distance(g3) = 5
    c: Symmetric(g2,g2,g3)
    c: Vertical(g3)
    c: Distance(g4) = 5
    c: Symmetric(g-4,g-4,g4)
    c: Vertical(g4)
    c: Coincident(g5,g4)
    c: Coincident(g5,g3)
    c: Coincident(g6,g4)
    c: PointOnObject(g6,g1)
    c: Horizontal(g6)
    c: Coincident(g7,g8)
    c: Coincident(g8,g9)
    c: Coincident(g9,g10)
    c: Coincident(g10,g7)
    c: Vertical(g7)
    c: Vertical(g9)
    c: Horizontal(g8)
    c: Horizontal(g10)
    c: Symmetric(g9,g7,g11)
    c: Symmetric(g5,g5,g11)
    c: Coincident(g8,g6)
FEATURE [PartDesign::Pad] Pad093
  Direction = (0,0,1)
  Length = 10
  Length2 = 10
  Profile = -> Sketch167
  ReferenceAxis = -> Sketch167 [N_Axis]
  Refine = true
  Suppressed = false
  Type = 0
FEATURE [PartDesign::Body] Body089  label="Cuerpo134"
  AllowCompound = false
  Group = -> [Binder099,Sketch167,Pad093]
  Origin = -> Origin094
  Tip = -> Pad093
FEATURE [App::DocumentObjectGroup] Group017  label="Grupo"
  Group = -> [Body081,Body089,Body087,Body088,Body082,Body084,Body085,Body080,Body083,Body086]
FEATURE [PartDesign::SubShapeBinder] Binder100  label="Binder101"
  BindCopyOnChange = 0
  BindMode = 2
  ClaimChildren = false
  Context = -> Part003 [Body090.Binder100.]
  Fuse = false
  MakeFace = true
  OffsetFill = false
  OffsetIntersection = false
  OffsetJoinType = 0
  OffsetOpenResult = false
  PartialLoad = false
  Refine = true
  Relative = true
  _Version = 2
FEATURE [Sketcher::SketchObject] Sketch168
  ArcFitTolerance = 1e-06
  AttachmentSupport = -> [Binder100]
  ExternalGeometry = -> [Binder100]
  FullyConstrained = false
  MakeInternals = false
  MapMode = 5
  Placement = pos=(0,0,38.1) rot=(0,0,1;0rad)
  sketch-geometry (6):
    g0: LineSegment [constr] StartX=999.985 StartY=1495 StartZ=0 EndX=999.985 EndY=-4.547e-13 EndZ=0
    g1: LineSegment [constr] StartX=753.752 StartY=1500 StartZ=0 EndX=753.752 EndY=1495 EndZ=0
    g2: LineSegment StartX=999.985 StartY=1495 StartZ=0 EndX=499.971 EndY=1495 EndZ=0
    g3: LineSegment StartX=499.971 StartY=1495 StartZ=0 EndX=499.971 EndY=1345 EndZ=0
    g4: LineSegment StartX=499.971 StartY=1345 StartZ=0 EndX=999.985 EndY=1345 EndZ=0
    g5: LineSegment StartX=999.985 StartY=1345 StartZ=0 EndX=999.985 EndY=1495 EndZ=0
  constraints (17):
    c: Coincident(g0,g-3)
    c: PointOnObject(g0,g-6)
    c: Vertical(g0)
    c: Distance(g1) = 5
    c: PointOnObject(g1,g-5)
    c: Vertical(g1)
    c: Coincident(g2,g3)
    c: Coincident(g3,g4)
    c: Coincident(g4,g5)
    c: Coincident(g5,g2)
    c: Horizontal(g2)
    c: Horizontal(g4)
    c: Vertical(g3)
    c: Vertical(g5)
    c: Distance(g2,g4) = 150
    c: Coincident(g2,g0)
    c: PointOnObject(g3,g-4)
FEATURE [PartDesign::Pad] Pad094
  Direction = (0,0,1)
  Length = 10
  Length2 = 10
  Profile = -> Sketch168
  ReferenceAxis = -> Sketch168 [N_Axis]
  Refine = true
  Suppressed = false
  Type = 0
FEATURE [PartDesign::Body] Body090  label="Cuerpo135"
  AllowCompound = false
  Group = -> [Binder100,Sketch168,Pad094]
  Origin = -> Origin095
  Placement = pos=(0,-875,-1.42e-14) rot=(0,0,1;0rad)
  Tip = -> Pad094
FEATURE [PartDesign::SubShapeBinder] Binder102  label="Binder103"
  BindCopyOnChange = 0
  BindMode = 2
  ClaimChildren = false
  Context = -> Part003 [Body091.Binder101.]
  Fuse = false
  MakeFace = true
  OffsetFill = false
  OffsetIntersection = false
  OffsetJoinType = 0
  OffsetOpenResult = false
  PartialLoad = false
  Refine = true
  Relative = true
  _Version = 2
FEATURE [Sketcher::SketchObject] Sketch170
  ArcFitTolerance = 1e-06
  AttachmentSupport = -> [Binder102]
  ExternalGeometry = -> [Binder102]
  FullyConstrained = false
  MakeInternals = false
  MapMode = 5
  Placement = pos=(0,0,38.1) rot=(0,0,1;0rad)
  sketch-geometry (6):
    g0: LineSegment [constr] StartX=999.985 StartY=1495 StartZ=0 EndX=999.985 EndY=-4.547e-13 EndZ=0
    g1: LineSegment [constr] StartX=753.752 StartY=1500 StartZ=0 EndX=753.752 EndY=1495 EndZ=0
    g2: LineSegment StartX=999.985 StartY=1495 StartZ=0 EndX=499.971 EndY=1495 EndZ=0
    g3: LineSegment StartX=499.971 StartY=1495 StartZ=0 EndX=499.971 EndY=1345 EndZ=0
    g4: LineSegment StartX=499.971 StartY=1345 StartZ=0 EndX=999.985 EndY=1345 EndZ=0
    g5: LineSegment StartX=999.985 StartY=1345 StartZ=0 EndX=999.985 EndY=1495 EndZ=0
  constraints (17):
    c: Coincident(g0,g-3)
    c: PointOnObject(g0,g-6)
    c: Vertical(g0)
    c: Distance(g1) = 5
    c: PointOnObject(g1,g-5)
    c: Vertical(g1)
    c: Coincident(g2,g3)
    c: Coincident(g3,g4)
    c: Coincident(g4,g5)
    c: Coincident(g5,g2)
    c: Horizontal(g2)
    c: Horizontal(g4)
    c: Vertical(g3)
    c: Vertical(g5)
    c: Distance(g2,g4) = 150
    c: Coincident(g2,g0)
    c: PointOnObject(g3,g-4)
FEATURE [PartDesign::Pad] Pad096
  Direction = (0,0,1)
  Length = 10
  Length2 = 10
  Profile = -> Sketch170
  ReferenceAxis = -> Sketch170 [N_Axis]
  Refine = true
  Suppressed = false
  Type = 0
FEATURE [PartDesign::Body] Body092  label="Cuerpo137"
  AllowCompound = false
  Group = -> [Binder102,Sketch170,Pad096]
  Origin = -> Origin097
  Placement = pos=(0,-1030,-1.42e-14) rot=(0,0,1;0rad)
  Tip = -> Pad096
FEATURE [PartDesign::SubShapeBinder] Binder103  label="Binder104"
  BindCopyOnChange = 0
  BindMode = 2
  ClaimChildren = false
  Context = -> Part003 [Body093.Binder103.]
  Fuse = false
  MakeFace = true
  OffsetFill = false
  OffsetIntersection = false
  OffsetJoinType = 0
  OffsetOpenResult = false
  PartialLoad = false
  Refine = true
  Relative = true
  _Version = 2
FEATURE [Sketcher::SketchObject] Sketch171
  ArcFitTolerance = 1e-06
  AttachmentSupport = -> [Binder103]
  ExternalGeometry = -> [Binder103]
  FullyConstrained = false
  MakeInternals = false
  MapMode = 5
  Placement = pos=(0,0,38.1) rot=(0,0,1;0rad)
  sketch-geometry (6):
    g0: LineSegment [constr] StartX=999.985 StartY=1495 StartZ=0 EndX=999.985 EndY=-4.547e-13 EndZ=0
    g1: LineSegment [constr] StartX=753.752 StartY=1500 StartZ=0 EndX=753.752 EndY=1495 EndZ=0
    g2: LineSegment StartX=999.985 StartY=1495 StartZ=0 EndX=499.971 EndY=1495 EndZ=0
    g3: LineSegment StartX=499.971 StartY=1495 StartZ=0 EndX=499.971 EndY=1345 EndZ=0
    g4: LineSegment StartX=499.971 StartY=1345 StartZ=0 EndX=999.985 EndY=1345 EndZ=0
    g5: LineSegment StartX=999.985 StartY=1345 StartZ=0 EndX=999.985 EndY=1495 EndZ=0
  constraints (17):
    c: Coincident(g0,g-3)
    c: PointOnObject(g0,g-6)
    c: Vertical(g0)
    c: Distance(g1) = 5
    c: PointOnObject(g1,g-5)
    c: Vertical(g1)
    c: Coincident(g2,g3)
    c: Coincident(g3,g4)
    c: Coincident(g4,g5)
    c: Coincident(g5,g2)
    c: Horizontal(g2)
    c: Horizontal(g4)
    c: Vertical(g3)
    c: Vertical(g5)
    c: Distance(g2,g4) = 150
    c: Coincident(g2,g0)
    c: PointOnObject(g3,g-4)
FEATURE [PartDesign::Pad] Pad097
  Direction = (0,0,1)
  Length = 10
  Length2 = 10
  Profile = -> Sketch171
  ReferenceAxis = -> Sketch171 [N_Axis]
  Refine = true
  Suppressed = false
  Type = 0
FEATURE [PartDesign::Body] Body093  label="Cuerpo138"
  AllowCompound = false
  Group = -> [Binder103,Sketch171,Pad097]
  Origin = -> Origin098
  Placement = pos=(0,-1185,-1.42e-14) rot=(0,0,1;0rad)
  Tip = -> Pad097
FEATURE [PartDesign::SubShapeBinder] Binder104  label="Binder105"
  BindCopyOnChange = 0
  BindMode = 2
  ClaimChildren = false
  Context = -> Part003 [Body091.Binder101.]
  Fuse = false
  MakeFace = true
  OffsetFill = false
  OffsetIntersection = false
  OffsetJoinType = 0
  OffsetOpenResult = false
  PartialLoad = false
  Refine = true
  Relative = true
  _Version = 2
FEATURE [Sketcher::SketchObject] Sketch172
  ArcFitTolerance = 1e-06
  AttachmentSupport = -> [Binder104]
  ExternalGeometry = -> [Binder104]
  FullyConstrained = false
  MakeInternals = false
  MapMode = 5
  Placement = pos=(0,0,38.1) rot=(0,0,1;0rad)
  sketch-geometry (6):
    g0: LineSegment [constr] StartX=999.985 StartY=1495 StartZ=0 EndX=999.985 EndY=-4.547e-13 EndZ=0
    g1: LineSegment [constr] StartX=753.752 StartY=1500 StartZ=0 EndX=753.752 EndY=1495 EndZ=0
    g2: LineSegment StartX=999.985 StartY=1495 StartZ=0 EndX=499.971 EndY=1495 EndZ=0
    g3: LineSegment StartX=499.971 StartY=1495 StartZ=0 EndX=499.971 EndY=1345 EndZ=0
    g4: LineSegment StartX=499.971 StartY=1345 StartZ=0 EndX=999.985 EndY=1345 EndZ=0
    g5: LineSegment StartX=999.985 StartY=1345 StartZ=0 EndX=999.985 EndY=1495 EndZ=0
  constraints (17):
    c: Coincident(g0,g-3)
    c: PointOnObject(g0,g-6)
    c: Vertical(g0)
    c: Distance(g1) = 5
    c: PointOnObject(g1,g-5)
    c: Vertical(g1)
    c: Coincident(g2,g3)
    c: Coincident(g3,g4)
    c: Coincident(g4,g5)
    c: Coincident(g5,g2)
    c: Horizontal(g2)
    c: Horizontal(g4)
    c: Vertical(g3)
    c: Vertical(g5)
    c: Distance(g2,g4) = 150
    c: Coincident(g2,g0)
    c: PointOnObject(g3,g-4)
FEATURE [PartDesign::Pad] Pad098
  Direction = (0,0,1)
  Length = 10
  Length2 = 10
  Profile = -> Sketch172
  ReferenceAxis = -> Sketch172 [N_Axis]
  Refine = true
  Suppressed = false
  Type = 0
FEATURE [PartDesign::Body] Body094  label="Cuerpo139"
  AllowCompound = false
  Group = -> [Binder104,Sketch172,Pad098]
  Origin = -> Origin099
  Placement = pos=(0,-1340,-1.42e-14) rot=(0,0,1;0rad)
  Tip = -> Pad098
FEATURE [PartDesign::SubShapeBinder] Binder105  label="Binder106"
  BindCopyOnChange = 0
  BindMode = 2
  ClaimChildren = false
  Context = -> Part003 [Body095.Binder105.]
  Fuse = false
  MakeFace = true
  OffsetFill = false
  OffsetIntersection = false
  OffsetJoinType = 0
  OffsetOpenResult = false
  PartialLoad = false
  Refine = true
  Relative = true
  _Version = 2
FEATURE [Sketcher::SketchObject] Sketch173
  ArcFitTolerance = 1e-06
  AttachmentSupport = -> [Binder105]
  ExternalGeometry = -> [Binder105]
  FullyConstrained = false
  MakeInternals = false
  MapMode = 5
  Placement = pos=(0,0,38.1) rot=(0,0,1;0rad)
  sketch-geometry (6):
    g0: LineSegment [constr] StartX=999.985 StartY=1495 StartZ=0 EndX=999.985 EndY=-4.547e-13 EndZ=0
    g1: LineSegment [constr] StartX=753.752 StartY=1500 StartZ=0 EndX=753.752 EndY=1495 EndZ=0
    g2: LineSegment StartX=999.985 StartY=1495 StartZ=0 EndX=499.971 EndY=1495 EndZ=0
    g3: LineSegment StartX=499.971 StartY=1495 StartZ=0 EndX=499.971 EndY=1345 EndZ=0
    g4: LineSegment StartX=499.971 StartY=1345 StartZ=0 EndX=999.985 EndY=1345 EndZ=0
    g5: LineSegment StartX=999.985 StartY=1345 StartZ=0 EndX=999.985 EndY=1495 EndZ=0
  constraints (17):
    c: Coincident(g0,g-3)
    c: PointOnObject(g0,g-6)
    c: Vertical(g0)
    c: Distance(g1) = 5
    c: PointOnObject(g1,g-5)
    c: Vertical(g1)
    c: Coincident(g2,g3)
    c: Coincident(g3,g4)
    c: Coincident(g4,g5)
    c: Coincident(g5,g2)
    c: Horizontal(g2)
    c: Horizontal(g4)
    c: Vertical(g3)
    c: Vertical(g5)
    c: Distance(g2,g4) = 150
    c: Coincident(g2,g0)
    c: PointOnObject(g3,g-4)
FEATURE [PartDesign::Pad] Pad099
  Direction = (0,0,1)
  Length = 10
  Length2 = 10
  Profile = -> Sketch173
  ReferenceAxis = -> Sketch173 [N_Axis]
  Refine = true
  Suppressed = false
  Type = 0
FEATURE [PartDesign::Body] Body095  label="Cuerpo140"
  AllowCompound = false
  Group = -> [Binder105,Sketch173,Pad099]
  Origin = -> Origin100
  Placement = pos=(0,-255,-1.42e-14) rot=(0,0,1;0rad)
  Tip = -> Pad099
FEATURE [PartDesign::SubShapeBinder] Binder106  label="Binder107"
  BindCopyOnChange = 0
  BindMode = 2
  ClaimChildren = false
  Context = -> Part003 [Body091.Binder101.]
  Fuse = false
  MakeFace = true
  OffsetFill = false
  OffsetIntersection = false
  OffsetJoinType = 0
  OffsetOpenResult = false
  PartialLoad = false
  Refine = true
  Relative = true
  _Version = 2
FEATURE [Sketcher::SketchObject] Sketch174
  ArcFitTolerance = 1e-06
  AttachmentSupport = -> [Binder106]
  ExternalGeometry = -> [Binder106]
  FullyConstrained = false
  MakeInternals = false
  MapMode = 5
  Placement = pos=(0,0,38.1) rot=(0,0,1;0rad)
  sketch-geometry (6):
    g0: LineSegment [constr] StartX=999.985 StartY=1495 StartZ=0 EndX=999.985 EndY=-4.547e-13 EndZ=0
    g1: LineSegment [constr] StartX=753.752 StartY=1500 StartZ=0 EndX=753.752 EndY=1495 EndZ=0
    g2: LineSegment StartX=999.985 StartY=1495 StartZ=0 EndX=499.971 EndY=1495 EndZ=0
    g3: LineSegment StartX=499.971 StartY=1495 StartZ=0 EndX=499.971 EndY=1345 EndZ=0
    g4: LineSegment StartX=499.971 StartY=1345 StartZ=0 EndX=999.985 EndY=1345 EndZ=0
    g5: LineSegment StartX=999.985 StartY=1345 StartZ=0 EndX=999.985 EndY=1495 EndZ=0
  constraints (17):
    c: Coincident(g0,g-3)
    c: PointOnObject(g0,g-6)
    c: Vertical(g0)
    c: Distance(g1) = 5
    c: PointOnObject(g1,g-5)
    c: Vertical(g1)
    c: Coincident(g2,g3)
    c: Coincident(g3,g4)
    c: Coincident(g4,g5)
    c: Coincident(g5,g2)
    c: Horizontal(g2)
    c: Horizontal(g4)
    c: Vertical(g3)
    c: Vertical(g5)
    c: Distance(g2,g4) = 150
    c: Coincident(g2,g0)
    c: PointOnObject(g3,g-4)
FEATURE [PartDesign::Pad] Pad100
  Direction = (0,0,1)
  Length = 10
  Length2 = 10
  Profile = -> Sketch174
  ReferenceAxis = -> Sketch174 [N_Axis]
  Refine = true
  Suppressed = false
  Type = 0
FEATURE [PartDesign::Body] Body096  label="Cuerpo141"
  AllowCompound = false
  Group = -> [Binder106,Sketch174,Pad100]
  Origin = -> Origin101
  Placement = pos=(0,-410,-1.42e-14) rot=(0,0,1;0rad)
  Tip = -> Pad100
FEATURE [PartDesign::SubShapeBinder] Binder107  label="Binder108"
  BindCopyOnChange = 0
  BindMode = 2
  ClaimChildren = false
  Context = -> Part003 [Body097.Binder107.]
  Fuse = false
  MakeFace = true
  OffsetFill = false
  OffsetIntersection = false
  OffsetJoinType = 0
  OffsetOpenResult = false
  PartialLoad = false
  Refine = true
  Relative = true
  _Version = 2
FEATURE [Sketcher::SketchObject] Sketch175
  ArcFitTolerance = 1e-06
  AttachmentSupport = -> [Binder107]
  ExternalGeometry = -> [Binder107]
  FullyConstrained = false
  MakeInternals = false
  MapMode = 5
  Placement = pos=(0,0,38.1) rot=(0,0,1;0rad)
  sketch-geometry (6):
    g0: LineSegment [constr] StartX=999.985 StartY=1495 StartZ=0 EndX=999.985 EndY=-4.547e-13 EndZ=0
    g1: LineSegment [constr] StartX=753.752 StartY=1500 StartZ=0 EndX=753.752 EndY=1495 EndZ=0
    g2: LineSegment StartX=999.985 StartY=1495 StartZ=0 EndX=499.971 EndY=1495 EndZ=0
    g3: LineSegment StartX=499.971 StartY=1495 StartZ=0 EndX=499.971 EndY=1345 EndZ=0
    g4: LineSegment StartX=499.971 StartY=1345 StartZ=0 EndX=999.985 EndY=1345 EndZ=0
    g5: LineSegment StartX=999.985 StartY=1345 StartZ=0 EndX=999.985 EndY=1495 EndZ=0
  constraints (17):
    c: Coincident(g0,g-3)
    c: PointOnObject(g0,g-6)
    c: Vertical(g0)
    c: Distance(g1) = 5
    c: PointOnObject(g1,g-5)
    c: Vertical(g1)
    c: Coincident(g2,g3)
    c: Coincident(g3,g4)
    c: Coincident(g4,g5)
    c: Coincident(g5,g2)
    c: Horizontal(g2)
    c: Horizontal(g4)
    c: Vertical(g3)
    c: Vertical(g5)
    c: Distance(g2,g4) = 150
    c: Coincident(g2,g0)
    c: PointOnObject(g3,g-4)
FEATURE [PartDesign::Pad] Pad101
  Direction = (0,0,1)
  Length = 10
  Length2 = 10
  Profile = -> Sketch175
  ReferenceAxis = -> Sketch175 [N_Axis]
  Refine = true
  Suppressed = false
  Type = 0
FEATURE [PartDesign::Body] Body097  label="Cuerpo142"
  AllowCompound = false
  Group = -> [Binder107,Sketch175,Pad101]
  Origin = -> Origin102
  Placement = pos=(0,-565,-1.42e-14) rot=(0,0,1;0rad)
  Tip = -> Pad101
FEATURE [PartDesign::SubShapeBinder] Binder108  label="Binder109"
  BindCopyOnChange = 0
  BindMode = 2
  ClaimChildren = false
  Context = -> Part003 [Body091.Binder101.]
  Fuse = false
  MakeFace = true
  OffsetFill = false
  OffsetIntersection = false
  OffsetJoinType = 0
  OffsetOpenResult = false
  PartialLoad = false
  Refine = true
  Relative = true
  _Version = 2
FEATURE [Sketcher::SketchObject] Sketch176
  ArcFitTolerance = 1e-06
  AttachmentSupport = -> [Binder108]
  ExternalGeometry = -> [Binder108]
  FullyConstrained = false
  MakeInternals = false
  MapMode = 5
  Placement = pos=(0,0,38.1) rot=(0,0,1;0rad)
  sketch-geometry (6):
    g0: LineSegment [constr] StartX=999.985 StartY=1495 StartZ=0 EndX=999.985 EndY=-4.547e-13 EndZ=0
    g1: LineSegment [constr] StartX=753.752 StartY=1500 StartZ=0 EndX=753.752 EndY=1495 EndZ=0
    g2: LineSegment StartX=999.985 StartY=1495 StartZ=0 EndX=499.971 EndY=1495 EndZ=0
    g3: LineSegment StartX=499.971 StartY=1495 StartZ=0 EndX=499.971 EndY=1345 EndZ=0
    g4: LineSegment StartX=499.971 StartY=1345 StartZ=0 EndX=999.985 EndY=1345 EndZ=0
    g5: LineSegment StartX=999.985 StartY=1345 StartZ=0 EndX=999.985 EndY=1495 EndZ=0
  constraints (17):
    c: Coincident(g0,g-3)
    c: PointOnObject(g0,g-6)
    c: Vertical(g0)
    c: Distance(g1) = 5
    c: PointOnObject(g1,g-5)
    c: Vertical(g1)
    c: Coincident(g2,g3)
    c: Coincident(g3,g4)
    c: Coincident(g4,g5)
    c: Coincident(g5,g2)
    c: Horizontal(g2)
    c: Horizontal(g4)
    c: Vertical(g3)
    c: Vertical(g5)
    c: Distance(g2,g4) = 150
    c: Coincident(g2,g0)
    c: PointOnObject(g3,g-4)
FEATURE [PartDesign::Pad] Pad102
  Direction = (0,0,1)
  Length = 10
  Length2 = 10
  Profile = -> Sketch176
  ReferenceAxis = -> Sketch176 [N_Axis]
  Refine = true
  Suppressed = false
  Type = 0
FEATURE [PartDesign::Body] Body098  label="Cuerpo143"
  AllowCompound = false
  Group = -> [Binder108,Sketch176,Pad102]
  Origin = -> Origin103
  Placement = pos=(0,-720,-1.42e-14) rot=(0,0,1;0rad)
  Tip = -> Pad102
FEATURE [PartDesign::SubShapeBinder] Binder109  label="Binder110"
  BindCopyOnChange = 0
  BindMode = 2
  ClaimChildren = false
  Context = -> Part003 [Body099.Binder109.]
  Fuse = false
  MakeFace = true
  OffsetFill = false
  OffsetIntersection = false
  OffsetJoinType = 0
  OffsetOpenResult = false
  PartialLoad = false
  Refine = true
  Relative = true
  _Version = 2
FEATURE [Sketcher::SketchObject] Sketch177
  ArcFitTolerance = 1e-06
  AttachmentSupport = -> [Binder109]
  ExternalGeometry = -> [Binder109]
  FullyConstrained = false
  MakeInternals = false
  MapMode = 5
  Placement = pos=(0,0,38.1) rot=(0,0,1;0rad)
  sketch-geometry (6):
    g0: LineSegment [constr] StartX=999.985 StartY=1495 StartZ=0 EndX=999.985 EndY=-4.547e-13 EndZ=0
    g1: LineSegment [constr] StartX=753.752 StartY=1500 StartZ=0 EndX=753.752 EndY=1495 EndZ=0
    g2: LineSegment StartX=999.985 StartY=1495 StartZ=0 EndX=499.971 EndY=1495 EndZ=0
    g3: LineSegment StartX=499.971 StartY=1495 StartZ=0 EndX=499.971 EndY=1345 EndZ=0
    g4: LineSegment StartX=499.971 StartY=1345 StartZ=0 EndX=999.985 EndY=1345 EndZ=0
    g5: LineSegment StartX=999.985 StartY=1345 StartZ=0 EndX=999.985 EndY=1495 EndZ=0
  constraints (17):
    c: Coincident(g0,g-3)
    c: PointOnObject(g0,g-6)
    c: Vertical(g0)
    c: Distance(g1) = 5
    c: PointOnObject(g1,g-5)
    c: Vertical(g1)
    c: Coincident(g2,g3)
    c: Coincident(g3,g4)
    c: Coincident(g4,g5)
    c: Coincident(g5,g2)
    c: Horizontal(g2)
    c: Horizontal(g4)
    c: Vertical(g3)
    c: Vertical(g5)
    c: Distance(g2,g4) = 150
    c: Coincident(g2,g0)
    c: PointOnObject(g3,g-4)
FEATURE [PartDesign::Pad] Pad103
  Direction = (0,0,1)
  Length = 10
  Length2 = 10
  Profile = -> Sketch177
  ReferenceAxis = -> Sketch177 [N_Axis]
  Refine = true
  Suppressed = false
  Type = 0
FEATURE [PartDesign::Body] Body099  label="Cuerpo144"
  AllowCompound = false
  Group = -> [Binder109,Sketch177,Pad103]
  Origin = -> Origin104
  Placement = pos=(0,-100,-1.42e-14) rot=(0,0,1;0rad)
  Tip = -> Pad103
FEATURE [PartDesign::SubShapeBinder] Binder110  label="Binder111"
  BindCopyOnChange = 0
  BindMode = 2
  ClaimChildren = false
  Context = -> Part003 [Body100.Binder110.]
  Fuse = false
  MakeFace = true
  OffsetFill = false
  OffsetIntersection = false
  OffsetJoinType = 0
  OffsetOpenResult = false
  PartialLoad = false
  Refine = true
  Relative = true
  _Version = 2
FEATURE [Sketcher::SketchObject] Sketch178
  ArcFitTolerance = 1e-06
  AttachmentSupport = -> [Binder110]
  ExternalGeometry = -> [Binder110]
  FullyConstrained = true
  MakeInternals = false
  MapMode = 5
  Placement = pos=(0,0,38.1) rot=(0,0,1;0rad)
  sketch-geometry (9):
    g0: LineSegment [constr] StartX=749.978 StartY=1395 StartZ=0 EndX=749.978 EndY=1400 EndZ=0
    g1: LineSegment [constr] StartX=749.978 StartY=1500 StartZ=0 EndX=749.978 EndY=1495 EndZ=0
    g2: LineSegment [constr] StartX=749.978 StartY=1400 StartZ=0 EndX=749.978 EndY=1495 EndZ=0
    g3: LineSegment [constr] StartX=749.978 StartY=1400 StartZ=0 EndX=499.971 EndY=1400 EndZ=0
    g4: LineSegment StartX=999.985 StartY=1495 StartZ=0 EndX=499.971 EndY=1495 EndZ=0
    g5: LineSegment StartX=499.971 StartY=1495 StartZ=0 EndX=499.971 EndY=1400 EndZ=0
    g6: LineSegment StartX=499.971 StartY=1400 StartZ=0 EndX=999.985 EndY=1400 EndZ=0
    g7: LineSegment StartX=999.985 StartY=1400 StartZ=0 EndX=999.985 EndY=1495 EndZ=0
    g8: GeomPoint [constr] X=749.978 Y=1447.5 Z=0
  constraints (23):
    c: Distance(g0) = 5
    c: Symmetric(g-6,g-6,g0)
    c: Vertical(g0)
    c: Distance(g1) = 5
    c: PointOnObject(g1,g-5)
    c: Vertical(g1)
    c: Coincident(g2,g0)
    c: Coincident(g2,g1)
    c: Vertical(g2)
    c: Coincident(g3,g0)
    c: PointOnObject(g3,g-3)
    c: Horizontal(g3)
    c: Coincident(g4,g5)
    c: Coincident(g5,g6)
    c: Coincident(g6,g7)
    c: Coincident(g7,g4)
    c: Horizontal(g4)
    c: Horizontal(g6)
    c: Vertical(g5)
    c: Vertical(g7)
    c: Symmetric(g6,g4,g8)
    c: Symmetric(g2,g2,g8)
    c: Coincident(g5,g3)
FEATURE [PartDesign::Pad] Pad104
  Direction = (0,0,1)
  Length = 10
  Length2 = 10
  Profile = -> Sketch178
  ReferenceAxis = -> Sketch178 [N_Axis]
  Refine = true
  Suppressed = false
  Type = 0
FEATURE [PartDesign::Body] Body100  label="Cuerpo145"
  AllowCompound = false
  Group = -> [Binder110,Sketch178,Pad104]
  Origin = -> Origin105
  Tip = -> Pad104
FEATURE [App::DocumentObjectGroup] Group018  label="Grupo001"
  Group = -> [Body093,Body096,Body098,Body090,Body094,Body097,Body092,Body095,Body099,Body100]
FEATURE [App::Part] Part003  label="Piso"
  Group = -> [Body085,Body087,Body082,Body081,Body084,Body083,Body088,Body086,Body080,Body089,Group017,Body095,Body092,Body094,Body093,Body096,Body100,Body090,Body098,Body097,Body099,Group018]
  Origin = -> Origin084
